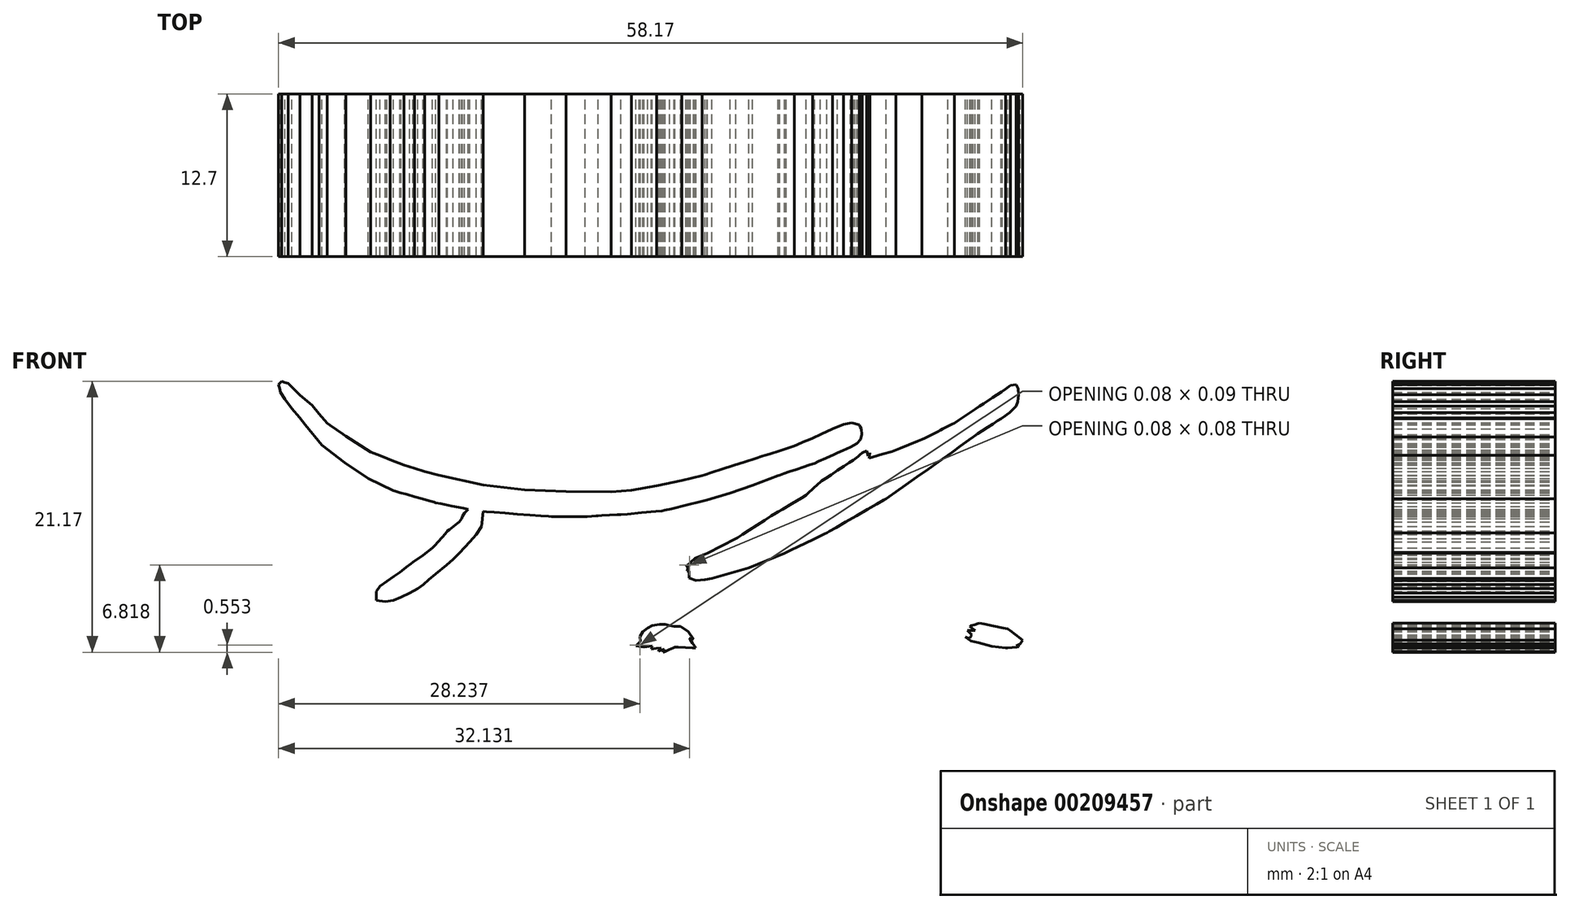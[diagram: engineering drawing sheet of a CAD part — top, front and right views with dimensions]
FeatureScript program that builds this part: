
annotation { "Feature Type Name" : "Feature", "Feature Type Description" : "" }
export const myFeature = defineFeature(function(context is Context, id is Id, definition is map)
    precondition{}
    {
        {
            var Q0;
            Q0=qCreatedBy(makeId("Front.planeOp"),FACE);
            var sketch = newSketch(context, id + "F0", { "sketchPlane" : qUnion([Q0])});
            skLineSegment(sketch, "E0", {"start": v(-84.86, 9.06) * mm, "end": v(-85.86, 10.23) * mm});
            skLineSegment(sketch, "E1", {"start": v(-85.86, 10.23) * mm, "end": v(-86.65, 11.35) * mm});
            skLineSegment(sketch, "E2", {"start": v(-86.65, 11.35) * mm, "end": v(-87.17, 12.6) * mm});
            skLineSegment(sketch, "E3", {"start": v(-87.17, 12.6) * mm, "end": v(-87.36, 14.14) * mm});
            skLineSegment(sketch, "E4", {"start": v(-87.36, 14.14) * mm, "end": v(-87.36, 15.32) * mm});
            skLineSegment(sketch, "E5", {"start": v(-87.36, 15.32) * mm, "end": v(-87.27, 15.8) * mm});
            skLineSegment(sketch, "E6", {"start": v(-87.27, 15.8) * mm, "end": v(-87.27, 16.26) * mm});
            skLineSegment(sketch, "E7", {"start": v(-87.27, 16.26) * mm, "end": v(-87.56, 16.7) * mm});
            skLineSegment(sketch, "E8", {"start": v(-87.56, 16.7) * mm, "end": v(-87.92, 17.1) * mm});
            skLineSegment(sketch, "E9", {"start": v(-87.92, 17.1) * mm, "end": v(-88.01, 17.22) * mm});
            skLineSegment(sketch, "E10", {"start": v(-88.01, 17.22) * mm, "end": v(-88.2, 17.49) * mm});
            skLineSegment(sketch, "E11", {"start": v(-88.2, 17.49) * mm, "end": v(-88.39, 17.75) * mm});
            skLineSegment(sketch, "E12", {"start": v(-88.39, 17.75) * mm, "end": v(-88.47, 17.87) * mm});
            skLineSegment(sketch, "E13", {"start": v(-88.47, 17.87) * mm, "end": v(-88.6, 18.03) * mm});
            skLineSegment(sketch, "E14", {"start": v(-88.6, 18.03) * mm, "end": v(-88.88, 18.37) * mm});
            skLineSegment(sketch, "E15", {"start": v(-88.88, 18.37) * mm, "end": v(-89.16, 18.72) * mm});
            skLineSegment(sketch, "E16", {"start": v(-89.16, 18.72) * mm, "end": v(-89.29, 18.88) * mm});
            skLineSegment(sketch, "E17", {"start": v(-89.29, 18.88) * mm, "end": v(-90.13, 20.03) * mm});
            skLineSegment(sketch, "E18", {"start": v(-90.13, 20.03) * mm, "end": v(-91.15, 21.5) * mm});
            skLineSegment(sketch, "E19", {"start": v(-91.15, 21.5) * mm, "end": v(-92.13, 23) * mm});
            skLineSegment(sketch, "E20", {"start": v(-92.13, 23) * mm, "end": v(-92.85, 24.22) * mm});
            skLineSegment(sketch, "E21", {"start": v(-92.85, 24.22) * mm, "end": v(-92.91, 24.33) * mm});
            skLineSegment(sketch, "E22", {"start": v(-92.91, 24.33) * mm, "end": v(-93.06, 24.63) * mm});
            skLineSegment(sketch, "E23", {"start": v(-93.06, 24.63) * mm, "end": v(-93.27, 25.05) * mm});
            skLineSegment(sketch, "E24", {"start": v(-93.27, 25.05) * mm, "end": v(-93.5, 25.53) * mm});
            skLineSegment(sketch, "E25", {"start": v(-93.5, 25.53) * mm, "end": v(-93.75, 26) * mm});
            skLineSegment(sketch, "E26", {"start": v(-93.75, 26) * mm, "end": v(-93.96, 26.43) * mm});
            skLineSegment(sketch, "E27", {"start": v(-93.96, 26.43) * mm, "end": v(-94.1, 26.73) * mm});
            skLineSegment(sketch, "E28", {"start": v(-94.1, 26.73) * mm, "end": v(-94.16, 26.84) * mm});
            skLineSegment(sketch, "E29", {"start": v(-94.16, 26.84) * mm, "end": v(-94.25, 27.07) * mm});
            skLineSegment(sketch, "E30", {"start": v(-94.25, 27.07) * mm, "end": v(-94.43, 27.56) * mm});
            skLineSegment(sketch, "E31", {"start": v(-94.43, 27.56) * mm, "end": v(-94.62, 28.05) * mm});
            skLineSegment(sketch, "E32", {"start": v(-94.62, 28.05) * mm, "end": v(-94.7, 28.28) * mm});
            skLineSegment(sketch, "E33", {"start": v(-94.7, 28.28) * mm, "end": v(-94.84, 28.6) * mm});
            skLineSegment(sketch, "E34", {"start": v(-94.84, 28.6) * mm, "end": v(-95.11, 29.3) * mm});
            skLineSegment(sketch, "E35", {"start": v(-95.11, 29.3) * mm, "end": v(-95.39, 30) * mm});
            skLineSegment(sketch, "E36", {"start": v(-95.39, 30) * mm, "end": v(-95.51, 30.31) * mm});
            skLineSegment(sketch, "E37", {"start": v(-95.51, 30.31) * mm, "end": v(-95.87, 32.15) * mm});
            skLineSegment(sketch, "E38", {"start": v(-95.87, 32.15) * mm, "end": v(-96.11, 34.04) * mm});
            skLineSegment(sketch, "E39", {"start": v(-96.11, 34.04) * mm, "end": v(-96.15, 34.45) * mm});
            skLineSegment(sketch, "E40", {"start": v(-96.15, 34.45) * mm, "end": v(-96.22, 35.35) * mm});
            skLineSegment(sketch, "E41", {"start": v(-96.22, 35.35) * mm, "end": v(-96.3, 36.25) * mm});
            skLineSegment(sketch, "E42", {"start": v(-96.3, 36.25) * mm, "end": v(-96.33, 36.66) * mm});
            skLineSegment(sketch, "E43", {"start": v(-96.33, 36.66) * mm, "end": v(-96.29, 36.97) * mm});
            skLineSegment(sketch, "E44", {"start": v(-96.29, 36.97) * mm, "end": v(-96.2, 37.63) * mm});
            skLineSegment(sketch, "E45", {"start": v(-96.2, 37.63) * mm, "end": v(-96.1, 38.3) * mm});
            skLineSegment(sketch, "E46", {"start": v(-96.1, 38.3) * mm, "end": v(-96.05, 38.6) * mm});
            skLineSegment(sketch, "E47", {"start": v(-96.05, 38.6) * mm, "end": v(-94.25, 44.05) * mm});
            skLineSegment(sketch, "E48", {"start": v(-94.25, 44.05) * mm, "end": v(-91, 48.77) * mm});
            skLineSegment(sketch, "E49", {"start": v(-91, 48.77) * mm, "end": v(-89.57, 50.22) * mm});
            skLineSegment(sketch, "E50", {"start": v(-89.57, 50.22) * mm, "end": v(-88.05, 51.58) * mm});
            skLineSegment(sketch, "E51", {"start": v(-88.05, 51.58) * mm, "end": v(-85.3, 53.9) * mm});
            skLineSegment(sketch, "E52", {"start": v(-85.3, 53.9) * mm, "end": v(-82.38, 56) * mm});
            skLineSegment(sketch, "E53", {"start": v(-82.38, 56) * mm, "end": v(-82.2, 56.1) * mm});
            skLineSegment(sketch, "E54", {"start": v(-82.2, 56.1) * mm, "end": v(-81.72, 56.35) * mm});
            skLineSegment(sketch, "E55", {"start": v(-81.72, 56.35) * mm, "end": v(-81.04, 56.71) * mm});
            skLineSegment(sketch, "E56", {"start": v(-81.04, 56.71) * mm, "end": v(-80.26, 57.13) * mm});
            skLineSegment(sketch, "E57", {"start": v(-80.26, 57.13) * mm, "end": v(-79.49, 57.55) * mm});
            skLineSegment(sketch, "E58", {"start": v(-79.49, 57.55) * mm, "end": v(-78.8, 57.92) * mm});
            skLineSegment(sketch, "E59", {"start": v(-78.8, 57.92) * mm, "end": v(-78.33, 58.17) * mm});
            skLineSegment(sketch, "E60", {"start": v(-78.33, 58.17) * mm, "end": v(-78.15, 58.27) * mm});
            skLineSegment(sketch, "E61", {"start": v(-78.15, 58.27) * mm, "end": v(-77.98, 58.35) * mm});
            skLineSegment(sketch, "E62", {"start": v(-77.98, 58.35) * mm, "end": v(-77.54, 58.56) * mm});
            skLineSegment(sketch, "E63", {"start": v(-77.54, 58.56) * mm, "end": v(-76.92, 58.85) * mm});
            skLineSegment(sketch, "E64", {"start": v(-76.92, 58.85) * mm, "end": v(-76.2, 59.19) * mm});
            skLineSegment(sketch, "E65", {"start": v(-76.2, 59.19) * mm, "end": v(-75.49, 59.52) * mm});
            skLineSegment(sketch, "E66", {"start": v(-75.49, 59.52) * mm, "end": v(-74.86, 59.82) * mm});
            skLineSegment(sketch, "E67", {"start": v(-74.86, 59.82) * mm, "end": v(-74.42, 60.02) * mm});
            skLineSegment(sketch, "E68", {"start": v(-74.42, 60.02) * mm, "end": v(-74.25, 60.1) * mm});
            skLineSegment(sketch, "E69", {"start": v(-74.25, 60.1) * mm, "end": v(-73.91, 60.24) * mm});
            skLineSegment(sketch, "E70", {"start": v(-73.91, 60.24) * mm, "end": v(-73.15, 60.56) * mm});
            skLineSegment(sketch, "E71", {"start": v(-73.15, 60.56) * mm, "end": v(-72.4, 60.87) * mm});
            skLineSegment(sketch, "E72", {"start": v(-72.4, 60.87) * mm, "end": v(-72.05, 61.02) * mm});
            skLineSegment(sketch, "E73", {"start": v(-72.05, 61.02) * mm, "end": v(-69.88, 61.65) * mm});
            skLineSegment(sketch, "E74", {"start": v(-69.88, 61.65) * mm, "end": v(-67.33, 62.24) * mm});
            skLineSegment(sketch, "E75", {"start": v(-67.33, 62.24) * mm, "end": v(-64.75, 62.74) * mm});
            skLineSegment(sketch, "E76", {"start": v(-64.75, 62.74) * mm, "end": v(-62.49, 63.11) * mm});
            skLineSegment(sketch, "E77", {"start": v(-62.49, 63.11) * mm, "end": v(-54.95, 63.92) * mm});
            skLineSegment(sketch, "E78", {"start": v(-54.95, 63.92) * mm, "end": v(-54.74, 63.94) * mm});
            skLineSegment(sketch, "E79", {"start": v(-54.74, 63.94) * mm, "end": v(-54.27, 63.97) * mm});
            skLineSegment(sketch, "E80", {"start": v(-54.27, 63.97) * mm, "end": v(-53.8, 64) * mm});
            skLineSegment(sketch, "E81", {"start": v(-53.8, 64) * mm, "end": v(-53.6, 64) * mm});
            skLineSegment(sketch, "E82", {"start": v(-53.6, 64) * mm, "end": v(-53.37, 64) * mm});
            skLineSegment(sketch, "E83", {"start": v(-53.37, 64) * mm, "end": v(-52.88, 64) * mm});
            skLineSegment(sketch, "E84", {"start": v(-52.88, 64) * mm, "end": v(-52.38, 64) * mm});
            skLineSegment(sketch, "E85", {"start": v(-52.38, 64) * mm, "end": v(-52.16, 64) * mm});
            skLineSegment(sketch, "E86", {"start": v(-52.16, 64) * mm, "end": v(-51.94, 64) * mm});
            skLineSegment(sketch, "E87", {"start": v(-51.94, 64) * mm, "end": v(-51.48, 63.96) * mm});
            skLineSegment(sketch, "E88", {"start": v(-51.48, 63.96) * mm, "end": v(-51.01, 63.93) * mm});
            skLineSegment(sketch, "E89", {"start": v(-51.01, 63.93) * mm, "end": v(-50.8, 63.9) * mm});
            skLineSegment(sketch, "E90", {"start": v(-50.8, 63.9) * mm, "end": v(-50.59, 63.9) * mm});
            skLineSegment(sketch, "E91", {"start": v(-50.59, 63.9) * mm, "end": v(-50.12, 63.9) * mm});
            skLineSegment(sketch, "E92", {"start": v(-50.12, 63.9) * mm, "end": v(-49.66, 63.9) * mm});
            skLineSegment(sketch, "E93", {"start": v(-49.66, 63.9) * mm, "end": v(-49.45, 63.9) * mm});
            skLineSegment(sketch, "E94", {"start": v(-49.45, 63.9) * mm, "end": v(-49.02, 63.87) * mm});
            skLineSegment(sketch, "E95", {"start": v(-49.02, 63.87) * mm, "end": v(-48.6, 63.84) * mm});
            skLineSegment(sketch, "E96", {"start": v(-48.6, 63.84) * mm, "end": v(-48.06, 63.81) * mm});
            skLineSegment(sketch, "E97", {"start": v(-48.06, 63.81) * mm, "end": v(-46.87, 63.75) * mm});
            skLineSegment(sketch, "E98", {"start": v(-46.87, 63.75) * mm, "end": v(-45.67, 63.68) * mm});
            skLineSegment(sketch, "E99", {"start": v(-45.67, 63.68) * mm, "end": v(-45.13, 63.66) * mm});
            skLineSegment(sketch, "E100", {"start": v(-45.13, 63.66) * mm, "end": v(-44.84, 63.6) * mm});
            skLineSegment(sketch, "E101", {"start": v(-44.84, 63.6) * mm, "end": v(-44.2, 63.5) * mm});
            skLineSegment(sketch, "E102", {"start": v(-44.2, 63.5) * mm, "end": v(-43.56, 63.4) * mm});
            skLineSegment(sketch, "E103", {"start": v(-43.56, 63.4) * mm, "end": v(-43.27, 63.35) * mm});
            skLineSegment(sketch, "E104", {"start": v(-43.27, 63.35) * mm, "end": v(-36.5, 62.05) * mm});
            skLineSegment(sketch, "E105", {"start": v(-36.5, 62.05) * mm, "end": v(-28.96, 59.87) * mm});
            skLineSegment(sketch, "E106", {"start": v(-28.96, 59.87) * mm, "end": v(-28.68, 59.78) * mm});
            skLineSegment(sketch, "E107", {"start": v(-28.68, 59.78) * mm, "end": v(-28.07, 59.57) * mm});
            skLineSegment(sketch, "E108", {"start": v(-28.07, 59.57) * mm, "end": v(-27.46, 59.37) * mm});
            skLineSegment(sketch, "E109", {"start": v(-27.46, 59.37) * mm, "end": v(-27.18, 59.28) * mm});
            skLineSegment(sketch, "E110", {"start": v(-27.18, 59.28) * mm, "end": v(-26.85, 59.12) * mm});
            skLineSegment(sketch, "E111", {"start": v(-26.85, 59.12) * mm, "end": v(-26.12, 58.77) * mm});
            skLineSegment(sketch, "E112", {"start": v(-26.12, 58.77) * mm, "end": v(-25.4, 58.42) * mm});
            skLineSegment(sketch, "E113", {"start": v(-25.4, 58.42) * mm, "end": v(-25.06, 58.26) * mm});
            skLineSegment(sketch, "E114", {"start": v(-25.06, 58.26) * mm, "end": v(-24.81, 58.1) * mm});
            skLineSegment(sketch, "E115", {"start": v(-24.81, 58.1) * mm, "end": v(-24.26, 57.77) * mm});
            skLineSegment(sketch, "E116", {"start": v(-24.26, 57.77) * mm, "end": v(-23.7, 57.43) * mm});
            skLineSegment(sketch, "E117", {"start": v(-23.7, 57.43) * mm, "end": v(-23.45, 57.27) * mm});
            skLineSegment(sketch, "E118", {"start": v(-23.45, 57.27) * mm, "end": v(-23.26, 57.17) * mm});
            skLineSegment(sketch, "E119", {"start": v(-23.26, 57.17) * mm, "end": v(-22.82, 56.94) * mm});
            skLineSegment(sketch, "E120", {"start": v(-22.82, 56.94) * mm, "end": v(-22.38, 56.7) * mm});
            skLineSegment(sketch, "E121", {"start": v(-22.38, 56.7) * mm, "end": v(-22.18, 56.6) * mm});
            skLineSegment(sketch, "E122", {"start": v(-22.18, 56.6) * mm, "end": v(-20.73, 55.63) * mm});
            skLineSegment(sketch, "E123", {"start": v(-20.73, 55.63) * mm, "end": v(-19.32, 54.46) * mm});
            skLineSegment(sketch, "E124", {"start": v(-19.32, 54.46) * mm, "end": v(-18.02, 53.17) * mm});
            skLineSegment(sketch, "E125", {"start": v(-18.02, 53.17) * mm, "end": v(-16.91, 51.82) * mm});
            skLineSegment(sketch, "E126", {"start": v(-16.91, 51.82) * mm, "end": v(-16.7, 51.49) * mm});
            skLineSegment(sketch, "E127", {"start": v(-16.7, 51.49) * mm, "end": v(-16.26, 50.76) * mm});
            skLineSegment(sketch, "E128", {"start": v(-16.26, 50.76) * mm, "end": v(-15.8, 50.03) * mm});
            skLineSegment(sketch, "E129", {"start": v(-15.8, 50.03) * mm, "end": v(-15.6, 49.7) * mm});
            skLineSegment(sketch, "E130", {"start": v(-15.6, 49.7) * mm, "end": v(-15.52, 49.52) * mm});
            skLineSegment(sketch, "E131", {"start": v(-15.52, 49.52) * mm, "end": v(-15.33, 49.1) * mm});
            skLineSegment(sketch, "E132", {"start": v(-15.33, 49.1) * mm, "end": v(-15.14, 48.7) * mm});
            skLineSegment(sketch, "E133", {"start": v(-15.14, 48.7) * mm, "end": v(-15.05, 48.51) * mm});
            skLineSegment(sketch, "E134", {"start": v(-15.05, 48.51) * mm, "end": v(-15, 48.4) * mm});
            skLineSegment(sketch, "E135", {"start": v(-15, 48.4) * mm, "end": v(-14.86, 48.12) * mm});
            skLineSegment(sketch, "E136", {"start": v(-14.86, 48.12) * mm, "end": v(-14.66, 47.71) * mm});
            skLineSegment(sketch, "E137", {"start": v(-14.66, 47.71) * mm, "end": v(-14.43, 47.25) * mm});
            skLineSegment(sketch, "E138", {"start": v(-14.43, 47.25) * mm, "end": v(-14.2, 46.78) * mm});
            skLineSegment(sketch, "E139", {"start": v(-14.2, 46.78) * mm, "end": v(-14, 46.37) * mm});
            skLineSegment(sketch, "E140", {"start": v(-14, 46.37) * mm, "end": v(-13.86, 46.08) * mm});
            skLineSegment(sketch, "E141", {"start": v(-13.86, 46.08) * mm, "end": v(-13.8, 45.98) * mm});
            skLineSegment(sketch, "E142", {"start": v(-13.8, 45.98) * mm, "end": v(-12.93, 42.88) * mm});
            skLineSegment(sketch, "E143", {"start": v(-12.93, 42.88) * mm, "end": v(-12.52, 39.7) * mm});
            skLineSegment(sketch, "E144", {"start": v(-12.52, 39.7) * mm, "end": v(-12.5, 39.43) * mm});
            skLineSegment(sketch, "E145", {"start": v(-12.5, 39.43) * mm, "end": v(-12.44, 38.82) * mm});
            skLineSegment(sketch, "E146", {"start": v(-12.44, 38.82) * mm, "end": v(-12.39, 38.2) * mm});
            skLineSegment(sketch, "E147", {"start": v(-12.39, 38.2) * mm, "end": v(-12.36, 37.93) * mm});
            skLineSegment(sketch, "E148", {"start": v(-12.36, 37.93) * mm, "end": v(-12.75, 33.76) * mm});
            skLineSegment(sketch, "E149", {"start": v(-12.75, 33.76) * mm, "end": v(-13.59, 29.63) * mm});
            skLineSegment(sketch, "E150", {"start": v(-13.59, 29.63) * mm, "end": v(-13.63, 29.37) * mm});
            skLineSegment(sketch, "E151", {"start": v(-13.63, 29.37) * mm, "end": v(-13.71, 28.79) * mm});
            skLineSegment(sketch, "E152", {"start": v(-13.71, 28.79) * mm, "end": v(-13.8, 28.2) * mm});
            skLineSegment(sketch, "E153", {"start": v(-13.8, 28.2) * mm, "end": v(-13.84, 27.94) * mm});
            skLineSegment(sketch, "E154", {"start": v(-13.84, 27.94) * mm, "end": v(-13.9, 27.66) * mm});
            skLineSegment(sketch, "E155", {"start": v(-13.9, 27.66) * mm, "end": v(-14.01, 27.05) * mm});
            skLineSegment(sketch, "E156", {"start": v(-14.01, 27.05) * mm, "end": v(-14.14, 26.44) * mm});
            skLineSegment(sketch, "E157", {"start": v(-14.14, 26.44) * mm, "end": v(-14.19, 26.16) * mm});
            skLineSegment(sketch, "E158", {"start": v(-14.19, 26.16) * mm, "end": v(-14.22, 25.91) * mm});
            skLineSegment(sketch, "E159", {"start": v(-14.22, 25.91) * mm, "end": v(-14.3, 25.36) * mm});
            skLineSegment(sketch, "E160", {"start": v(-14.3, 25.36) * mm, "end": v(-14.36, 24.8) * mm});
            skLineSegment(sketch, "E161", {"start": v(-14.36, 24.8) * mm, "end": v(-14.4, 24.55) * mm});
            skLineSegment(sketch, "E162", {"start": v(-14.4, 24.55) * mm, "end": v(-14.14, 24.68) * mm});
            skLineSegment(sketch, "E163", {"start": v(-14.14, 24.68) * mm, "end": v(-13.89, 24.8) * mm});
            skLineSegment(sketch, "E164", {"start": v(-13.89, 24.8) * mm, "end": v(-13.72, 24.55) * mm});
            skLineSegment(sketch, "E165", {"start": v(-13.72, 24.55) * mm, "end": v(-13.55, 24.3) * mm});
            skLineSegment(sketch, "E166", {"start": v(-13.55, 24.3) * mm, "end": v(-13.63, 24.17) * mm});
            skLineSegment(sketch, "E167", {"start": v(-13.63, 24.17) * mm, "end": v(-13.72, 24.05) * mm});
            skLineSegment(sketch, "E168", {"start": v(-13.72, 24.05) * mm, "end": v(-13.55, 24.05) * mm});
            skLineSegment(sketch, "E169", {"start": v(-13.55, 24.05) * mm, "end": v(-13.58, 23.91) * mm});
            skLineSegment(sketch, "E170", {"start": v(-13.58, 23.91) * mm, "end": v(-13.63, 23.62) * mm});
            skLineSegment(sketch, "E171", {"start": v(-13.63, 23.62) * mm, "end": v(-13.7, 23.33) * mm});
            skLineSegment(sketch, "E172", {"start": v(-13.7, 23.33) * mm, "end": v(-13.72, 23.2) * mm});
            skLineSegment(sketch, "E173", {"start": v(-13.72, 23.2) * mm, "end": v(-13.55, 23.2) * mm});
            skLineSegment(sketch, "E174", {"start": v(-13.55, 23.2) * mm, "end": v(-14.06, 22.2) * mm});
            skLineSegment(sketch, "E175", {"start": v(-14.06, 22.2) * mm, "end": v(-14.68, 21.25) * mm});
            skLineSegment(sketch, "E176", {"start": v(-14.68, 21.25) * mm, "end": v(-15.5, 20.04) * mm});
            skLineSegment(sketch, "E177", {"start": v(-15.5, 20.04) * mm, "end": v(-16.47, 18.86) * mm});
            skLineSegment(sketch, "E178", {"start": v(-16.47, 18.86) * mm, "end": v(-17.57, 17.82) * mm});
            skLineSegment(sketch, "E179", {"start": v(-17.57, 17.82) * mm, "end": v(-18.8, 17.02) * mm});
            skLineSegment(sketch, "E180", {"start": v(-18.8, 17.02) * mm, "end": v(-18.93, 16.97) * mm});
            skLineSegment(sketch, "E181", {"start": v(-18.93, 16.97) * mm, "end": v(-19.22, 16.85) * mm});
            skLineSegment(sketch, "E182", {"start": v(-19.22, 16.85) * mm, "end": v(-19.51, 16.74) * mm});
            skLineSegment(sketch, "E183", {"start": v(-19.51, 16.74) * mm, "end": v(-19.64, 16.7) * mm});
            skLineSegment(sketch, "E184", {"start": v(-19.64, 16.7) * mm, "end": v(-20.61, 16.39) * mm});
            skLineSegment(sketch, "E185", {"start": v(-20.61, 16.39) * mm, "end": v(-21.6, 16.2) * mm});
            skLineSegment(sketch, "E186", {"start": v(-21.6, 16.2) * mm, "end": v(-22.03, 16.1) * mm});
            skLineSegment(sketch, "E187", {"start": v(-22.03, 16.1) * mm, "end": v(-22.42, 16.04) * mm});
            skLineSegment(sketch, "E188", {"start": v(-22.42, 16.04) * mm, "end": v(-22.75, 16.22) * mm});
            skLineSegment(sketch, "E189", {"start": v(-22.75, 16.22) * mm, "end": v(-22.97, 16.52) * mm});
            skLineSegment(sketch, "E190", {"start": v(-22.97, 16.52) * mm, "end": v(-23.01, 17) * mm});
            skLineSegment(sketch, "E191", {"start": v(-23.01, 17) * mm, "end": v(-22.87, 17.6) * mm});
            skLineSegment(sketch, "E192", {"start": v(-22.87, 17.6) * mm, "end": v(-22.65, 18.17) * mm});
            skLineSegment(sketch, "E193", {"start": v(-22.65, 18.17) * mm, "end": v(-22.43, 18.63) * mm});
            skLineSegment(sketch, "E194", {"start": v(-22.43, 18.63) * mm, "end": v(-22.07, 19.34) * mm});
            skLineSegment(sketch, "E195", {"start": v(-22.07, 19.34) * mm, "end": v(-21.87, 19.81) * mm});
            skLineSegment(sketch, "E196", {"start": v(-21.87, 19.81) * mm, "end": v(-21.71, 20.28) * mm});
            skLineSegment(sketch, "E197", {"start": v(-21.71, 20.28) * mm, "end": v(-21.48, 21) * mm});
            skLineSegment(sketch, "E198", {"start": v(-21.48, 21) * mm, "end": v(-21.2, 21.78) * mm});
            skLineSegment(sketch, "E199", {"start": v(-21.2, 21.78) * mm, "end": v(-21.1, 22.6) * mm});
            skLineSegment(sketch, "E200", {"start": v(-21.1, 22.6) * mm, "end": v(-21.11, 22.8) * mm});
            skLineSegment(sketch, "E201", {"start": v(-21.11, 22.8) * mm, "end": v(-21.15, 23.28) * mm});
            skLineSegment(sketch, "E202", {"start": v(-21.15, 23.28) * mm, "end": v(-21.2, 23.97) * mm});
            skLineSegment(sketch, "E203", {"start": v(-21.2, 23.97) * mm, "end": v(-21.27, 24.77) * mm});
            skLineSegment(sketch, "E204", {"start": v(-21.27, 24.77) * mm, "end": v(-21.34, 25.56) * mm});
            skLineSegment(sketch, "E205", {"start": v(-21.34, 25.56) * mm, "end": v(-21.4, 26.25) * mm});
            skLineSegment(sketch, "E206", {"start": v(-21.4, 26.25) * mm, "end": v(-21.43, 26.74) * mm});
            skLineSegment(sketch, "E207", {"start": v(-21.43, 26.74) * mm, "end": v(-21.45, 26.93) * mm});
            skLineSegment(sketch, "E208", {"start": v(-21.45, 26.93) * mm, "end": v(-21.51, 27.44) * mm});
            skLineSegment(sketch, "E209", {"start": v(-21.51, 27.44) * mm, "end": v(-21.65, 28.58) * mm});
            skLineSegment(sketch, "E210", {"start": v(-21.65, 28.58) * mm, "end": v(-21.8, 29.71) * mm});
            skLineSegment(sketch, "E211", {"start": v(-21.8, 29.71) * mm, "end": v(-21.86, 30.23) * mm});
            skLineSegment(sketch, "E212", {"start": v(-21.86, 30.23) * mm, "end": v(-21.88, 30.41) * mm});
            skLineSegment(sketch, "E213", {"start": v(-21.88, 30.41) * mm, "end": v(-21.94, 30.82) * mm});
            skLineSegment(sketch, "E214", {"start": v(-21.94, 30.82) * mm, "end": v(-22, 31.23) * mm});
            skLineSegment(sketch, "E215", {"start": v(-22, 31.23) * mm, "end": v(-22.01, 31.41) * mm});
            skLineSegment(sketch, "E216", {"start": v(-22.01, 31.41) * mm, "end": v(-22.26, 30.93) * mm});
            skLineSegment(sketch, "E217", {"start": v(-22.26, 30.93) * mm, "end": v(-22.39, 30.4) * mm});
            skLineSegment(sketch, "E218", {"start": v(-22.39, 30.4) * mm, "end": v(-22.73, 29.53) * mm});
            skLineSegment(sketch, "E219", {"start": v(-22.73, 29.53) * mm, "end": v(-23.14, 28.7) * mm});
            skLineSegment(sketch, "E220", {"start": v(-23.14, 28.7) * mm, "end": v(-23.32, 28.39) * mm});
            skLineSegment(sketch, "E221", {"start": v(-23.32, 28.39) * mm, "end": v(-23.74, 27.69) * mm});
            skLineSegment(sketch, "E222", {"start": v(-23.74, 27.69) * mm, "end": v(-24.15, 26.99) * mm});
            skLineSegment(sketch, "E223", {"start": v(-24.15, 26.99) * mm, "end": v(-24.33, 26.67) * mm});
            skLineSegment(sketch, "E224", {"start": v(-24.33, 26.67) * mm, "end": v(-24.95, 25.62) * mm});
            skLineSegment(sketch, "E225", {"start": v(-24.95, 25.62) * mm, "end": v(-25.5, 24.7) * mm});
            skLineSegment(sketch, "E226", {"start": v(-25.5, 24.7) * mm, "end": v(-26.1, 23.79) * mm});
            skLineSegment(sketch, "E227", {"start": v(-26.1, 23.79) * mm, "end": v(-26.86, 22.78) * mm});
            skLineSegment(sketch, "E228", {"start": v(-26.86, 22.78) * mm, "end": v(-27.22, 22.32) * mm});
            skLineSegment(sketch, "E229", {"start": v(-27.22, 22.32) * mm, "end": v(-27.69, 21.78) * mm});
            skLineSegment(sketch, "E230", {"start": v(-27.69, 21.78) * mm, "end": v(-28.18, 21.28) * mm});
            skLineSegment(sketch, "E231", {"start": v(-28.18, 21.28) * mm, "end": v(-28.62, 20.95) * mm});
            skLineSegment(sketch, "E232", {"start": v(-28.62, 20.95) * mm, "end": v(-29.1, 20.8) * mm});
            skLineSegment(sketch, "E233", {"start": v(-29.1, 20.8) * mm, "end": v(-29.45, 20.87) * mm});
            skLineSegment(sketch, "E234", {"start": v(-29.45, 20.87) * mm, "end": v(-29.64, 21.17) * mm});
            skLineSegment(sketch, "E235", {"start": v(-29.64, 21.17) * mm, "end": v(-29.63, 21.67) * mm});
            skLineSegment(sketch, "E236", {"start": v(-29.63, 21.67) * mm, "end": v(-29.62, 22.16) * mm});
            skLineSegment(sketch, "E237", {"start": v(-29.62, 22.16) * mm, "end": v(-29.3, 22.6) * mm});
            skLineSegment(sketch, "E238", {"start": v(-29.3, 22.6) * mm, "end": v(-29.22, 22.7) * mm});
            skLineSegment(sketch, "E239", {"start": v(-29.22, 22.7) * mm, "end": v(-29.02, 22.96) * mm});
            skLineSegment(sketch, "E240", {"start": v(-29.02, 22.96) * mm, "end": v(-28.74, 23.33) * mm});
            skLineSegment(sketch, "E241", {"start": v(-28.74, 23.33) * mm, "end": v(-28.41, 23.75) * mm});
            skLineSegment(sketch, "E242", {"start": v(-28.41, 23.75) * mm, "end": v(-28.09, 24.17) * mm});
            skLineSegment(sketch, "E243", {"start": v(-28.09, 24.17) * mm, "end": v(-27.8, 24.54) * mm});
            skLineSegment(sketch, "E244", {"start": v(-27.8, 24.54) * mm, "end": v(-27.6, 24.8) * mm});
            skLineSegment(sketch, "E245", {"start": v(-27.6, 24.8) * mm, "end": v(-27.53, 24.9) * mm});
            skLineSegment(sketch, "E246", {"start": v(-27.53, 24.9) * mm, "end": v(-26.58, 26.57) * mm});
            skLineSegment(sketch, "E247", {"start": v(-26.58, 26.57) * mm, "end": v(-25.86, 28.54) * mm});
            skLineSegment(sketch, "E248", {"start": v(-25.86, 28.54) * mm, "end": v(-25.33, 30.6) * mm});
            skLineSegment(sketch, "E249", {"start": v(-25.33, 30.6) * mm, "end": v(-25, 32.51) * mm});
            skLineSegment(sketch, "E250", {"start": v(-25, 32.51) * mm, "end": v(-24.98, 32.75) * mm});
            skLineSegment(sketch, "E251", {"start": v(-24.98, 32.75) * mm, "end": v(-24.94, 33.28) * mm});
            skLineSegment(sketch, "E252", {"start": v(-24.94, 33.28) * mm, "end": v(-24.9, 33.8) * mm});
            skLineSegment(sketch, "E253", {"start": v(-24.9, 33.8) * mm, "end": v(-24.88, 34.04) * mm});
            skLineSegment(sketch, "E254", {"start": v(-24.88, 34.04) * mm, "end": v(-24.83, 34.33) * mm});
            skLineSegment(sketch, "E255", {"start": v(-24.83, 34.33) * mm, "end": v(-24.72, 34.97) * mm});
            skLineSegment(sketch, "E256", {"start": v(-24.72, 34.97) * mm, "end": v(-24.6, 35.6) * mm});
            skLineSegment(sketch, "E257", {"start": v(-24.6, 35.6) * mm, "end": v(-24.55, 35.9) * mm});
            skLineSegment(sketch, "E258", {"start": v(-24.55, 35.9) * mm, "end": v(-24.47, 35.9) * mm});
            skLineSegment(sketch, "E259", {"start": v(-24.47, 35.9) * mm, "end": v(-24.39, 35.81) * mm});
            skLineSegment(sketch, "E260", {"start": v(-24.39, 35.81) * mm, "end": v(-24.3, 35.73) * mm});
            skLineSegment(sketch, "E261", {"start": v(-24.3, 35.73) * mm, "end": v(-24.26, 35.86) * mm});
            skLineSegment(sketch, "E262", {"start": v(-24.26, 35.86) * mm, "end": v(-24.22, 35.98) * mm});
            skLineSegment(sketch, "E263", {"start": v(-24.22, 35.98) * mm, "end": v(-23.94, 35.14) * mm});
            skLineSegment(sketch, "E264", {"start": v(-23.94, 35.14) * mm, "end": v(-23.84, 34.3) * mm});
            skLineSegment(sketch, "E265", {"start": v(-23.84, 34.3) * mm, "end": v(-23.67, 33.38) * mm});
            skLineSegment(sketch, "E266", {"start": v(-23.67, 33.38) * mm, "end": v(-23.65, 32.43) * mm});
            skLineSegment(sketch, "E267", {"start": v(-23.65, 32.43) * mm, "end": v(-23.7, 31.97) * mm});
            skLineSegment(sketch, "E268", {"start": v(-23.7, 31.97) * mm, "end": v(-23.85, 30.95) * mm});
            skLineSegment(sketch, "E269", {"start": v(-23.85, 30.95) * mm, "end": v(-23.98, 29.93) * mm});
            skLineSegment(sketch, "E270", {"start": v(-23.98, 29.93) * mm, "end": v(-24.05, 29.46) * mm});
            skLineSegment(sketch, "E271", {"start": v(-24.05, 29.46) * mm, "end": v(-23.83, 29.9) * mm});
            skLineSegment(sketch, "E272", {"start": v(-23.83, 29.9) * mm, "end": v(-23.66, 30.11) * mm});
            skLineSegment(sketch, "E273", {"start": v(-23.66, 30.11) * mm, "end": v(-23.5, 30.26) * mm});
            skLineSegment(sketch, "E274", {"start": v(-23.5, 30.26) * mm, "end": v(-23.26, 30.5) * mm});
            skLineSegment(sketch, "E275", {"start": v(-23.26, 30.5) * mm, "end": v(-23.15, 30.64) * mm});
            skLineSegment(sketch, "E276", {"start": v(-23.15, 30.64) * mm, "end": v(-22.9, 30.95) * mm});
            skLineSegment(sketch, "E277", {"start": v(-22.9, 30.95) * mm, "end": v(-22.64, 31.27) * mm});
            skLineSegment(sketch, "E278", {"start": v(-22.64, 31.27) * mm, "end": v(-22.52, 31.41) * mm});
            skLineSegment(sketch, "E279", {"start": v(-22.52, 31.41) * mm, "end": v(-22.17, 31.61) * mm});
            skLineSegment(sketch, "E280", {"start": v(-22.17, 31.61) * mm, "end": v(-22.11, 32.09) * mm});
            skLineSegment(sketch, "E281", {"start": v(-22.11, 32.09) * mm, "end": v(-22.22, 32.68) * mm});
            skLineSegment(sketch, "E282", {"start": v(-22.22, 32.68) * mm, "end": v(-22.33, 33.22) * mm});
            skLineSegment(sketch, "E283", {"start": v(-22.33, 33.22) * mm, "end": v(-22.29, 33.72) * mm});
            skLineSegment(sketch, "E284", {"start": v(-22.29, 33.72) * mm, "end": v(-21.93, 34.2) * mm});
            skLineSegment(sketch, "E285", {"start": v(-21.93, 34.2) * mm, "end": v(-21.89, 34.04) * mm});
            skLineSegment(sketch, "E286", {"start": v(-21.89, 34.04) * mm, "end": v(-21.85, 33.87) * mm});
            skLineSegment(sketch, "E287", {"start": v(-21.85, 33.87) * mm, "end": v(-21.44, 33.66) * mm});
            skLineSegment(sketch, "E288", {"start": v(-21.44, 33.66) * mm, "end": v(-21.29, 33.19) * mm});
            skLineSegment(sketch, "E289", {"start": v(-21.29, 33.19) * mm, "end": v(-21.26, 33.07) * mm});
            skLineSegment(sketch, "E290", {"start": v(-21.26, 33.07) * mm, "end": v(-21.2, 32.8) * mm});
            skLineSegment(sketch, "E291", {"start": v(-21.2, 32.8) * mm, "end": v(-21.12, 32.55) * mm});
            skLineSegment(sketch, "E292", {"start": v(-21.12, 32.55) * mm, "end": v(-21.1, 32.43) * mm});
            skLineSegment(sketch, "E293", {"start": v(-21.1, 32.43) * mm, "end": v(-20.93, 32.03) * mm});
            skLineSegment(sketch, "E294", {"start": v(-20.93, 32.03) * mm, "end": v(-20.8, 31.74) * mm});
            skLineSegment(sketch, "E295", {"start": v(-20.8, 31.74) * mm, "end": v(-20.69, 31.42) * mm});
            skLineSegment(sketch, "E296", {"start": v(-20.69, 31.42) * mm, "end": v(-20.59, 30.9) * mm});
            skLineSegment(sketch, "E297", {"start": v(-20.59, 30.9) * mm, "end": v(-20.56, 30.67) * mm});
            skLineSegment(sketch, "E298", {"start": v(-20.56, 30.67) * mm, "end": v(-20.48, 30.06) * mm});
            skLineSegment(sketch, "E299", {"start": v(-20.48, 30.06) * mm, "end": v(-20.36, 29.19) * mm});
            skLineSegment(sketch, "E300", {"start": v(-20.36, 29.19) * mm, "end": v(-20.24, 28.2) * mm});
            skLineSegment(sketch, "E301", {"start": v(-20.24, 28.2) * mm, "end": v(-20.1, 27.2) * mm});
            skLineSegment(sketch, "E302", {"start": v(-20.1, 27.2) * mm, "end": v(-20, 26.33) * mm});
            skLineSegment(sketch, "E303", {"start": v(-20, 26.33) * mm, "end": v(-19.91, 25.72) * mm});
            skLineSegment(sketch, "E304", {"start": v(-19.91, 25.72) * mm, "end": v(-19.88, 25.48) * mm});
            skLineSegment(sketch, "E305", {"start": v(-19.88, 25.48) * mm, "end": v(-19.85, 25.06) * mm});
            skLineSegment(sketch, "E306", {"start": v(-19.85, 25.06) * mm, "end": v(-19.76, 24.13) * mm});
            skLineSegment(sketch, "E307", {"start": v(-19.76, 24.13) * mm, "end": v(-19.68, 23.2) * mm});
            skLineSegment(sketch, "E308", {"start": v(-19.68, 23.2) * mm, "end": v(-19.64, 22.78) * mm});
            skLineSegment(sketch, "E309", {"start": v(-19.64, 22.78) * mm, "end": v(-19.67, 22.51) * mm});
            skLineSegment(sketch, "E310", {"start": v(-19.67, 22.51) * mm, "end": v(-19.73, 21.93) * mm});
            skLineSegment(sketch, "E311", {"start": v(-19.73, 21.93) * mm, "end": v(-19.79, 21.35) * mm});
            skLineSegment(sketch, "E312", {"start": v(-19.79, 21.35) * mm, "end": v(-19.81, 21.08) * mm});
            skLineSegment(sketch, "E313", {"start": v(-19.81, 21.08) * mm, "end": v(-19.06, 21.61) * mm});
            skLineSegment(sketch, "E314", {"start": v(-19.06, 21.61) * mm, "end": v(-18.53, 22.17) * mm});
            skLineSegment(sketch, "E315", {"start": v(-18.53, 22.17) * mm, "end": v(-18.07, 22.71) * mm});
            skLineSegment(sketch, "E316", {"start": v(-18.07, 22.71) * mm, "end": v(-17.53, 23.2) * mm});
            skLineSegment(sketch, "E317", {"start": v(-17.53, 23.2) * mm, "end": v(-16.77, 23.56) * mm});
            skLineSegment(sketch, "E318", {"start": v(-16.77, 23.56) * mm, "end": v(-16.17, 23.9) * mm});
            skLineSegment(sketch, "E319", {"start": v(-16.17, 23.9) * mm, "end": v(-16.13, 24.22) * mm});
            skLineSegment(sketch, "E320", {"start": v(-16.13, 24.22) * mm, "end": v(-16.17, 24.55) * mm});
            skLineSegment(sketch, "E321", {"start": v(-16.17, 24.55) * mm, "end": v(-16.09, 25.57) * mm});
            skLineSegment(sketch, "E322", {"start": v(-16.09, 25.57) * mm, "end": v(-16.05, 25.8) * mm});
            skLineSegment(sketch, "E323", {"start": v(-16.05, 25.8) * mm, "end": v(-15.95, 26.42) * mm});
            skLineSegment(sketch, "E324", {"start": v(-15.95, 26.42) * mm, "end": v(-15.81, 27.29) * mm});
            skLineSegment(sketch, "E325", {"start": v(-15.81, 27.29) * mm, "end": v(-15.65, 28.28) * mm});
            skLineSegment(sketch, "E326", {"start": v(-15.65, 28.28) * mm, "end": v(-15.5, 29.27) * mm});
            skLineSegment(sketch, "E327", {"start": v(-15.5, 29.27) * mm, "end": v(-15.35, 30.14) * mm});
            skLineSegment(sketch, "E328", {"start": v(-15.35, 30.14) * mm, "end": v(-15.26, 30.76) * mm});
            skLineSegment(sketch, "E329", {"start": v(-15.26, 30.76) * mm, "end": v(-15.22, 30.99) * mm});
            skLineSegment(sketch, "E330", {"start": v(-15.22, 30.99) * mm, "end": v(-15.2, 31.18) * mm});
            skLineSegment(sketch, "E331", {"start": v(-15.2, 31.18) * mm, "end": v(-15.13, 31.68) * mm});
            skLineSegment(sketch, "E332", {"start": v(-15.13, 31.68) * mm, "end": v(-15.04, 32.38) * mm});
            skLineSegment(sketch, "E333", {"start": v(-15.04, 32.38) * mm, "end": v(-14.93, 33.2) * mm});
            skLineSegment(sketch, "E334", {"start": v(-14.93, 33.2) * mm, "end": v(-14.82, 34) * mm});
            skLineSegment(sketch, "E335", {"start": v(-14.82, 34) * mm, "end": v(-14.73, 34.7) * mm});
            skLineSegment(sketch, "E336", {"start": v(-14.73, 34.7) * mm, "end": v(-14.67, 35.2) * mm});
            skLineSegment(sketch, "E337", {"start": v(-14.67, 35.2) * mm, "end": v(-14.64, 35.4) * mm});
            skLineSegment(sketch, "E338", {"start": v(-14.64, 35.4) * mm, "end": v(-14.6, 35.81) * mm});
            skLineSegment(sketch, "E339", {"start": v(-14.6, 35.81) * mm, "end": v(-14.56, 36.24) * mm});
            skLineSegment(sketch, "E340", {"start": v(-14.56, 36.24) * mm, "end": v(-14.55, 36.58) * mm});
            skLineSegment(sketch, "E341", {"start": v(-14.55, 36.58) * mm, "end": v(-14.52, 37.34) * mm});
            skLineSegment(sketch, "E342", {"start": v(-14.52, 37.34) * mm, "end": v(-14.5, 38.1) * mm});
            skLineSegment(sketch, "E343", {"start": v(-14.5, 38.1) * mm, "end": v(-14.48, 38.44) * mm});
            skLineSegment(sketch, "E344", {"start": v(-14.48, 38.44) * mm, "end": v(-14.52, 38.88) * mm});
            skLineSegment(sketch, "E345", {"start": v(-14.52, 38.88) * mm, "end": v(-14.62, 39.84) * mm});
            skLineSegment(sketch, "E346", {"start": v(-14.62, 39.84) * mm, "end": v(-14.72, 40.8) * mm});
            skLineSegment(sketch, "E347", {"start": v(-14.72, 40.8) * mm, "end": v(-14.77, 41.23) * mm});
            skLineSegment(sketch, "E348", {"start": v(-14.77, 41.23) * mm, "end": v(-15.95, 45.54) * mm});
            skLineSegment(sketch, "E349", {"start": v(-15.95, 45.54) * mm, "end": v(-17.95, 49.4) * mm});
            skLineSegment(sketch, "E350", {"start": v(-17.95, 49.4) * mm, "end": v(-20.75, 52.75) * mm});
            skLineSegment(sketch, "E351", {"start": v(-20.75, 52.75) * mm, "end": v(-24.3, 55.46) * mm});
            skLineSegment(sketch, "E352", {"start": v(-24.3, 55.46) * mm, "end": v(-26.3, 56.55) * mm});
            skLineSegment(sketch, "E353", {"start": v(-26.3, 56.55) * mm, "end": v(-28.36, 57.51) * mm});
            skLineSegment(sketch, "E354", {"start": v(-28.36, 57.51) * mm, "end": v(-28.6, 57.62) * mm});
            skLineSegment(sketch, "E355", {"start": v(-28.6, 57.62) * mm, "end": v(-29.08, 57.84) * mm});
            skLineSegment(sketch, "E356", {"start": v(-29.08, 57.84) * mm, "end": v(-29.58, 58.06) * mm});
            skLineSegment(sketch, "E357", {"start": v(-29.58, 58.06) * mm, "end": v(-29.8, 58.16) * mm});
            skLineSegment(sketch, "E358", {"start": v(-29.8, 58.16) * mm, "end": v(-34.87, 59.74) * mm});
            skLineSegment(sketch, "E359", {"start": v(-34.87, 59.74) * mm, "end": v(-40.05, 60.91) * mm});
            skLineSegment(sketch, "E360", {"start": v(-40.05, 60.91) * mm, "end": v(-48.94, 62.06) * mm});
            skLineSegment(sketch, "E361", {"start": v(-48.94, 62.06) * mm, "end": v(-49.11, 62.08) * mm});
            skLineSegment(sketch, "E362", {"start": v(-49.11, 62.08) * mm, "end": v(-49.49, 62.1) * mm});
            skLineSegment(sketch, "E363", {"start": v(-49.49, 62.1) * mm, "end": v(-49.87, 62.13) * mm});
            skLineSegment(sketch, "E364", {"start": v(-49.87, 62.13) * mm, "end": v(-50.04, 62.15) * mm});
            skLineSegment(sketch, "E365", {"start": v(-50.04, 62.15) * mm, "end": v(-50.24, 62.15) * mm});
            skLineSegment(sketch, "E366", {"start": v(-50.24, 62.15) * mm, "end": v(-50.75, 62.15) * mm});
            skLineSegment(sketch, "E367", {"start": v(-50.75, 62.15) * mm, "end": v(-51.49, 62.15) * mm});
            skLineSegment(sketch, "E368", {"start": v(-51.49, 62.15) * mm, "end": v(-52.32, 62.15) * mm});
            skLineSegment(sketch, "E369", {"start": v(-52.32, 62.15) * mm, "end": v(-53.17, 62.15) * mm});
            skLineSegment(sketch, "E370", {"start": v(-53.17, 62.15) * mm, "end": v(-53.9, 62.15) * mm});
            skLineSegment(sketch, "E371", {"start": v(-53.9, 62.15) * mm, "end": v(-54.42, 62.15) * mm});
            skLineSegment(sketch, "E372", {"start": v(-54.42, 62.15) * mm, "end": v(-54.61, 62.15) * mm});
            skLineSegment(sketch, "E373", {"start": v(-54.61, 62.15) * mm, "end": v(-54.77, 62.14) * mm});
            skLineSegment(sketch, "E374", {"start": v(-54.77, 62.14) * mm, "end": v(-55.12, 62.1) * mm});
            skLineSegment(sketch, "E375", {"start": v(-55.12, 62.1) * mm, "end": v(-55.47, 62.08) * mm});
            skLineSegment(sketch, "E376", {"start": v(-55.47, 62.08) * mm, "end": v(-55.63, 62.07) * mm});
            skLineSegment(sketch, "E377", {"start": v(-55.63, 62.07) * mm, "end": v(-56.05, 62.04) * mm});
            skLineSegment(sketch, "E378", {"start": v(-56.05, 62.04) * mm, "end": v(-56.98, 61.97) * mm});
            skLineSegment(sketch, "E379", {"start": v(-56.98, 61.97) * mm, "end": v(-57.91, 61.9) * mm});
            skLineSegment(sketch, "E380", {"start": v(-57.91, 61.9) * mm, "end": v(-58.34, 61.88) * mm});
            skLineSegment(sketch, "E381", {"start": v(-58.34, 61.88) * mm, "end": v(-58.72, 61.81) * mm});
            skLineSegment(sketch, "E382", {"start": v(-58.72, 61.81) * mm, "end": v(-59.1, 61.75) * mm});
            skLineSegment(sketch, "E383", {"start": v(-59.1, 61.75) * mm, "end": v(-59.28, 61.72) * mm});
            skLineSegment(sketch, "E384", {"start": v(-59.28, 61.72) * mm, "end": v(-59.77, 61.64) * mm});
            skLineSegment(sketch, "E385", {"start": v(-59.77, 61.64) * mm, "end": v(-60.46, 61.54) * mm});
            skLineSegment(sketch, "E386", {"start": v(-60.46, 61.54) * mm, "end": v(-61.26, 61.42) * mm});
            skLineSegment(sketch, "E387", {"start": v(-61.26, 61.42) * mm, "end": v(-62.05, 61.3) * mm});
            skLineSegment(sketch, "E388", {"start": v(-62.05, 61.3) * mm, "end": v(-62.74, 61.19) * mm});
            skLineSegment(sketch, "E389", {"start": v(-62.74, 61.19) * mm, "end": v(-63.23, 61.11) * mm});
            skLineSegment(sketch, "E390", {"start": v(-63.23, 61.11) * mm, "end": v(-63.42, 61.08) * mm});
            skLineSegment(sketch, "E391", {"start": v(-63.42, 61.08) * mm, "end": v(-67.56, 60.2) * mm});
            skLineSegment(sketch, "E392", {"start": v(-67.56, 60.2) * mm, "end": v(-71.63, 59.04) * mm});
            skLineSegment(sketch, "E393", {"start": v(-71.63, 59.04) * mm, "end": v(-78.06, 56.1) * mm});
            skLineSegment(sketch, "E394", {"start": v(-78.06, 56.1) * mm, "end": v(-78.25, 56) * mm});
            skLineSegment(sketch, "E395", {"start": v(-78.25, 56) * mm, "end": v(-78.74, 55.7) * mm});
            skLineSegment(sketch, "E396", {"start": v(-78.74, 55.7) * mm, "end": v(-79.43, 55.29) * mm});
            skLineSegment(sketch, "E397", {"start": v(-79.43, 55.29) * mm, "end": v(-80.22, 54.8) * mm});
            skLineSegment(sketch, "E398", {"start": v(-80.22, 54.8) * mm, "end": v(-81.02, 54.33) * mm});
            skLineSegment(sketch, "E399", {"start": v(-81.02, 54.33) * mm, "end": v(-81.7, 53.91) * mm});
            skLineSegment(sketch, "E400", {"start": v(-81.7, 53.91) * mm, "end": v(-82.2, 53.62) * mm});
            skLineSegment(sketch, "E401", {"start": v(-82.2, 53.62) * mm, "end": v(-82.38, 53.5) * mm});
            skLineSegment(sketch, "E402", {"start": v(-82.38, 53.5) * mm, "end": v(-85, 51.53) * mm});
            skLineSegment(sketch, "E403", {"start": v(-85, 51.53) * mm, "end": v(-87.38, 49.28) * mm});
            skLineSegment(sketch, "E404", {"start": v(-87.38, 49.28) * mm, "end": v(-89.02, 47.6) * mm});
            skLineSegment(sketch, "E405", {"start": v(-89.02, 47.6) * mm, "end": v(-90.54, 45.8) * mm});
            skLineSegment(sketch, "E406", {"start": v(-90.54, 45.8) * mm, "end": v(-91.98, 43.66) * mm});
            skLineSegment(sketch, "E407", {"start": v(-91.98, 43.66) * mm, "end": v(-93.15, 41.29) * mm});
            skLineSegment(sketch, "E408", {"start": v(-93.15, 41.29) * mm, "end": v(-94, 38.79) * mm});
            skLineSegment(sketch, "E409", {"start": v(-94, 38.79) * mm, "end": v(-94.41, 36.24) * mm});
            skLineSegment(sketch, "E410", {"start": v(-94.41, 36.24) * mm, "end": v(-94.45, 35.81) * mm});
            skLineSegment(sketch, "E411", {"start": v(-94.45, 35.81) * mm, "end": v(-94.49, 35.4) * mm});
            skLineSegment(sketch, "E412", {"start": v(-94.49, 35.4) * mm, "end": v(-94.3, 32.7) * mm});
            skLineSegment(sketch, "E413", {"start": v(-94.3, 32.7) * mm, "end": v(-93.7, 30.06) * mm});
            skLineSegment(sketch, "E414", {"start": v(-93.7, 30.06) * mm, "end": v(-93.59, 29.8) * mm});
            skLineSegment(sketch, "E415", {"start": v(-93.59, 29.8) * mm, "end": v(-93.35, 29.21) * mm});
            skLineSegment(sketch, "E416", {"start": v(-93.35, 29.21) * mm, "end": v(-93.11, 28.63) * mm});
            skLineSegment(sketch, "E417", {"start": v(-93.11, 28.63) * mm, "end": v(-93, 28.36) * mm});
            skLineSegment(sketch, "E418", {"start": v(-93, 28.36) * mm, "end": v(-92.94, 28.21) * mm});
            skLineSegment(sketch, "E419", {"start": v(-92.94, 28.21) * mm, "end": v(-92.76, 27.82) * mm});
            skLineSegment(sketch, "E420", {"start": v(-92.76, 27.82) * mm, "end": v(-92.52, 27.27) * mm});
            skLineSegment(sketch, "E421", {"start": v(-92.52, 27.27) * mm, "end": v(-92.23, 26.63) * mm});
            skLineSegment(sketch, "E422", {"start": v(-92.23, 26.63) * mm, "end": v(-91.95, 26) * mm});
            skLineSegment(sketch, "E423", {"start": v(-91.95, 26) * mm, "end": v(-91.7, 25.44) * mm});
            skLineSegment(sketch, "E424", {"start": v(-91.7, 25.44) * mm, "end": v(-91.53, 25.04) * mm});
            skLineSegment(sketch, "E425", {"start": v(-91.53, 25.04) * mm, "end": v(-91.46, 24.9) * mm});
            skLineSegment(sketch, "E426", {"start": v(-91.46, 24.9) * mm, "end": v(-89.22, 21.39) * mm});
            skLineSegment(sketch, "E427", {"start": v(-89.22, 21.39) * mm, "end": v(-86.45, 18.29) * mm});
            skLineSegment(sketch, "E428", {"start": v(-86.45, 18.29) * mm, "end": v(-85.93, 19.2) * mm});
            skLineSegment(sketch, "E429", {"start": v(-85.93, 19.2) * mm, "end": v(-85.37, 19.95) * mm});
            skLineSegment(sketch, "E430", {"start": v(-85.37, 19.95) * mm, "end": v(-84.7, 20.61) * mm});
            skLineSegment(sketch, "E431", {"start": v(-84.7, 20.61) * mm, "end": v(-83.82, 21.2) * mm});
            skLineSegment(sketch, "E432", {"start": v(-83.82, 21.2) * mm, "end": v(-82.89, 21.62) * mm});
            skLineSegment(sketch, "E433", {"start": v(-82.89, 21.62) * mm, "end": v(-81.62, 21.76) * mm});
            skLineSegment(sketch, "E434", {"start": v(-81.62, 21.76) * mm, "end": v(-80.35, 21.62) * mm});
            skLineSegment(sketch, "E435", {"start": v(-80.35, 21.62) * mm, "end": v(-79.66, 21.43) * mm});
            skLineSegment(sketch, "E436", {"start": v(-79.66, 21.43) * mm, "end": v(-78.95, 21.13) * mm});
            skLineSegment(sketch, "E437", {"start": v(-78.95, 21.13) * mm, "end": v(-78.37, 20.7) * mm});
            skLineSegment(sketch, "E438", {"start": v(-78.37, 20.7) * mm, "end": v(-78.06, 20.07) * mm});
            skLineSegment(sketch, "E439", {"start": v(-78.06, 20.07) * mm, "end": v(-78.32, 19.86) * mm});
            skLineSegment(sketch, "E440", {"start": v(-78.32, 19.86) * mm, "end": v(-78.58, 19.64) * mm});
            skLineSegment(sketch, "E441", {"start": v(-78.58, 19.64) * mm, "end": v(-78.35, 19.37) * mm});
            skLineSegment(sketch, "E442", {"start": v(-78.35, 19.37) * mm, "end": v(-78.58, 19.13) * mm});
            skLineSegment(sketch, "E443", {"start": v(-78.58, 19.13) * mm, "end": v(-79.04, 19.13) * mm});
            skLineSegment(sketch, "E444", {"start": v(-79.04, 19.13) * mm, "end": v(-79.5, 19.13) * mm});
            skLineSegment(sketch, "E445", {"start": v(-79.5, 19.13) * mm, "end": v(-80.67, 18.92) * mm});
            skLineSegment(sketch, "E446", {"start": v(-80.67, 18.92) * mm, "end": v(-81.86, 18.35) * mm});
            skLineSegment(sketch, "E447", {"start": v(-81.86, 18.35) * mm, "end": v(-82.93, 17.56) * mm});
            skLineSegment(sketch, "E448", {"start": v(-82.93, 17.56) * mm, "end": v(-83.73, 16.68) * mm});
            skLineSegment(sketch, "E449", {"start": v(-83.73, 16.68) * mm, "end": v(-84.17, 15.95) * mm});
            skLineSegment(sketch, "E450", {"start": v(-84.17, 15.95) * mm, "end": v(-84.54, 15.1) * mm});
            skLineSegment(sketch, "E451", {"start": v(-84.54, 15.1) * mm, "end": v(-84.8, 14.22) * mm});
            skLineSegment(sketch, "E452", {"start": v(-84.8, 14.22) * mm, "end": v(-84.92, 13.38) * mm});
            skLineSegment(sketch, "E453", {"start": v(-84.92, 13.38) * mm, "end": v(-84.84, 12.62) * mm});
            skLineSegment(sketch, "E454", {"start": v(-84.84, 12.62) * mm, "end": v(-84.6, 11.8) * mm});
            skLineSegment(sketch, "E455", {"start": v(-84.6, 11.8) * mm, "end": v(-84.28, 11.02) * mm});
            skLineSegment(sketch, "E456", {"start": v(-84.28, 11.02) * mm, "end": v(-83.94, 10.33) * mm});
            skLineSegment(sketch, "E457", {"start": v(-83.94, 10.33) * mm, "end": v(-83.13, 9.1) * mm});
            skLineSegment(sketch, "E458", {"start": v(-83.13, 9.1) * mm, "end": v(-82.04, 8.16) * mm});
            skLineSegment(sketch, "E459", {"start": v(-82.04, 8.16) * mm, "end": v(-80.51, 7.68) * mm});
            skLineSegment(sketch, "E460", {"start": v(-80.51, 7.68) * mm, "end": v(-78.91, 7.7) * mm});
            skLineSegment(sketch, "E461", {"start": v(-78.91, 7.7) * mm, "end": v(-78.66, 7.72) * mm});
            skLineSegment(sketch, "E462", {"start": v(-78.66, 7.72) * mm, "end": v(-78.4, 7.74) * mm});
            skLineSegment(sketch, "E463", {"start": v(-78.4, 7.74) * mm, "end": v(-78.06, 7.85) * mm});
            skLineSegment(sketch, "E464", {"start": v(-78.06, 7.85) * mm, "end": v(-77.72, 7.96) * mm});
            skLineSegment(sketch, "E465", {"start": v(-77.72, 7.96) * mm, "end": v(-77.72, 7.79) * mm});
            skLineSegment(sketch, "E466", {"start": v(-77.72, 7.79) * mm, "end": v(-77.39, 7.79) * mm});
            skLineSegment(sketch, "E467", {"start": v(-77.39, 7.79) * mm, "end": v(-77.05, 7.79) * mm});
            skLineSegment(sketch, "E468", {"start": v(-77.05, 7.79) * mm, "end": v(-76.84, 7.66) * mm});
            skLineSegment(sketch, "E469", {"start": v(-76.84, 7.66) * mm, "end": v(-76.62, 7.54) * mm});
            skLineSegment(sketch, "E470", {"start": v(-76.62, 7.54) * mm, "end": v(-76.3, 9.18) * mm});
            skLineSegment(sketch, "E471", {"start": v(-76.3, 9.18) * mm, "end": v(-76.1, 10.84) * mm});
            skLineSegment(sketch, "E472", {"start": v(-76.1, 10.84) * mm, "end": v(-76.08, 10.98) * mm});
            skLineSegment(sketch, "E473", {"start": v(-76.08, 10.98) * mm, "end": v(-76.03, 11.3) * mm});
            skLineSegment(sketch, "E474", {"start": v(-76.03, 11.3) * mm, "end": v(-75.98, 11.62) * mm});
            skLineSegment(sketch, "E475", {"start": v(-75.98, 11.62) * mm, "end": v(-75.96, 11.77) * mm});
            skLineSegment(sketch, "E476", {"start": v(-75.96, 11.77) * mm, "end": v(-75.9, 12.76) * mm});
            skLineSegment(sketch, "E477", {"start": v(-75.9, 12.76) * mm, "end": v(-75.7, 13.72) * mm});
            skLineSegment(sketch, "E478", {"start": v(-75.7, 13.72) * mm, "end": v(-75.65, 13.55) * mm});
            skLineSegment(sketch, "E479", {"start": v(-75.65, 13.55) * mm, "end": v(-75.6, 13.38) * mm});
            skLineSegment(sketch, "E480", {"start": v(-75.6, 13.38) * mm, "end": v(-75.65, 13.8) * mm});
            skLineSegment(sketch, "E481", {"start": v(-75.65, 13.8) * mm, "end": v(-75.7, 14.23) * mm});
            skLineSegment(sketch, "E482", {"start": v(-75.7, 14.23) * mm, "end": v(-75.78, 14.18) * mm});
            skLineSegment(sketch, "E483", {"start": v(-75.78, 14.18) * mm, "end": v(-75.86, 14.14) * mm});
            skLineSegment(sketch, "E484", {"start": v(-75.86, 14.14) * mm, "end": v(-75.84, 14.27) * mm});
            skLineSegment(sketch, "E485", {"start": v(-75.84, 14.27) * mm, "end": v(-75.78, 14.56) * mm});
            skLineSegment(sketch, "E486", {"start": v(-75.78, 14.56) * mm, "end": v(-75.72, 14.85) * mm});
            skLineSegment(sketch, "E487", {"start": v(-75.72, 14.85) * mm, "end": v(-75.7, 14.99) * mm});
            skLineSegment(sketch, "E488", {"start": v(-75.7, 14.99) * mm, "end": v(-75.65, 14.6) * mm});
            skLineSegment(sketch, "E489", {"start": v(-75.65, 14.6) * mm, "end": v(-75.6, 14.23) * mm});
            skLineSegment(sketch, "E490", {"start": v(-75.6, 14.23) * mm, "end": v(-75.59, 14.45) * mm});
            skLineSegment(sketch, "E491", {"start": v(-75.59, 14.45) * mm, "end": v(-75.54, 14.94) * mm});
            skLineSegment(sketch, "E492", {"start": v(-75.54, 14.94) * mm, "end": v(-75.49, 15.44) * mm});
            skLineSegment(sketch, "E493", {"start": v(-75.49, 15.44) * mm, "end": v(-75.46, 15.66) * mm});
            skLineSegment(sketch, "E494", {"start": v(-75.46, 15.66) * mm, "end": v(-75.45, 15.8) * mm});
            skLineSegment(sketch, "E495", {"start": v(-75.45, 15.8) * mm, "end": v(-75.41, 16.09) * mm});
            skLineSegment(sketch, "E496", {"start": v(-75.41, 16.09) * mm, "end": v(-75.38, 16.38) * mm});
            skLineSegment(sketch, "E497", {"start": v(-75.38, 16.38) * mm, "end": v(-75.36, 16.5) * mm});
            skLineSegment(sketch, "E498", {"start": v(-75.36, 16.5) * mm, "end": v(-75.36, 16.34) * mm});
            skLineSegment(sketch, "E499", {"start": v(-75.36, 16.34) * mm, "end": v(-75.36, 15.96) * mm});
            skLineSegment(sketch, "E500", {"start": v(-75.36, 15.96) * mm, "end": v(-75.36, 15.58) * mm});
            skLineSegment(sketch, "E501", {"start": v(-75.36, 15.58) * mm, "end": v(-75.36, 15.4) * mm});
            skLineSegment(sketch, "E502", {"start": v(-75.36, 15.4) * mm, "end": v(-75.39, 15.17) * mm});
            skLineSegment(sketch, "E503", {"start": v(-75.39, 15.17) * mm, "end": v(-75.44, 14.65) * mm});
            skLineSegment(sketch, "E504", {"start": v(-75.44, 14.65) * mm, "end": v(-75.5, 14.12) * mm});
            skLineSegment(sketch, "E505", {"start": v(-75.5, 14.12) * mm, "end": v(-75.52, 13.89) * mm});
            skLineSegment(sketch, "E506", {"start": v(-75.52, 13.89) * mm, "end": v(-75.54, 13.54) * mm});
            skLineSegment(sketch, "E507", {"start": v(-75.54, 13.54) * mm, "end": v(-75.57, 12.78) * mm});
            skLineSegment(sketch, "E508", {"start": v(-75.57, 12.78) * mm, "end": v(-75.6, 12.03) * mm});
            skLineSegment(sketch, "E509", {"start": v(-75.6, 12.03) * mm, "end": v(-75.6, 11.68) * mm});
            skLineSegment(sketch, "E510", {"start": v(-75.6, 11.68) * mm, "end": v(-75.65, 11.37) * mm});
            skLineSegment(sketch, "E511", {"start": v(-75.65, 11.37) * mm, "end": v(-75.73, 10.67) * mm});
            skLineSegment(sketch, "E512", {"start": v(-75.73, 10.67) * mm, "end": v(-75.81, 9.97) * mm});
            skLineSegment(sketch, "E513", {"start": v(-75.81, 9.97) * mm, "end": v(-75.85, 9.65) * mm});
            skLineSegment(sketch, "E514", {"start": v(-75.85, 9.65) * mm, "end": v(-75.87, 9.32) * mm});
            skLineSegment(sketch, "E515", {"start": v(-75.87, 9.32) * mm, "end": v(-75.9, 8.6) * mm});
            skLineSegment(sketch, "E516", {"start": v(-75.9, 8.6) * mm, "end": v(-75.94, 7.87) * mm});
            skLineSegment(sketch, "E517", {"start": v(-75.94, 7.87) * mm, "end": v(-75.95, 7.54) * mm});
            skLineSegment(sketch, "E518", {"start": v(-75.95, 7.54) * mm, "end": v(-76, 7.11) * mm});
            skLineSegment(sketch, "E519", {"start": v(-76, 7.11) * mm, "end": v(-76.08, 6.18) * mm});
            skLineSegment(sketch, "E520", {"start": v(-76.08, 6.18) * mm, "end": v(-76.16, 5.25) * mm});
            skLineSegment(sketch, "E521", {"start": v(-76.16, 5.25) * mm, "end": v(-76.2, 4.83) * mm});
            skLineSegment(sketch, "E522", {"start": v(-76.2, 4.83) * mm, "end": v(-76.21, 4.3) * mm});
            skLineSegment(sketch, "E523", {"start": v(-76.21, 4.3) * mm, "end": v(-76.24, 3.13) * mm});
            skLineSegment(sketch, "E524", {"start": v(-76.24, 3.13) * mm, "end": v(-76.27, 1.97) * mm});
            skLineSegment(sketch, "E525", {"start": v(-76.27, 1.97) * mm, "end": v(-76.29, 1.44) * mm});
            skLineSegment(sketch, "E526", {"start": v(-76.29, 1.44) * mm, "end": v(-76.22, 0.76) * mm});
            skLineSegment(sketch, "E527", {"start": v(-76.22, 0.76) * mm, "end": v(-75.95, 0.33) * mm});
            skLineSegment(sketch, "E528", {"start": v(-75.95, 0.33) * mm, "end": v(-75.6, -0.08) * mm});
            skLineSegment(sketch, "E529", {"start": v(-75.6, -0.08) * mm, "end": v(-75.08, -0.69) * mm});
            skLineSegment(sketch, "E530", {"start": v(-75.08, -0.69) * mm, "end": v(-74.57, -1.16) * mm});
            skLineSegment(sketch, "E531", {"start": v(-74.57, -1.16) * mm, "end": v(-74, -1.57) * mm});
            skLineSegment(sketch, "E532", {"start": v(-74, -1.57) * mm, "end": v(-73.32, -1.98) * mm});
            skLineSegment(sketch, "E533", {"start": v(-73.32, -1.98) * mm, "end": v(-69.6, -3.68) * mm});
            skLineSegment(sketch, "E534", {"start": v(-69.6, -3.68) * mm, "end": v(-69.41, -3.73) * mm});
            skLineSegment(sketch, "E535", {"start": v(-69.41, -3.73) * mm, "end": v(-69, -3.85) * mm});
            skLineSegment(sketch, "E536", {"start": v(-69, -3.85) * mm, "end": v(-68.6, -3.96) * mm});
            skLineSegment(sketch, "E537", {"start": v(-68.6, -3.96) * mm, "end": v(-68.41, -4) * mm});
            skLineSegment(sketch, "E538", {"start": v(-68.41, -4) * mm, "end": v(-68.27, -4.07) * mm});
            skLineSegment(sketch, "E539", {"start": v(-68.27, -4.07) * mm, "end": v(-67.95, -4.21) * mm});
            skLineSegment(sketch, "E540", {"start": v(-67.95, -4.21) * mm, "end": v(-67.63, -4.35) * mm});
            skLineSegment(sketch, "E541", {"start": v(-67.63, -4.35) * mm, "end": v(-67.48, -4.41) * mm});
            skLineSegment(sketch, "E542", {"start": v(-67.48, -4.41) * mm, "end": v(-67.3, -4.48) * mm});
            skLineSegment(sketch, "E543", {"start": v(-67.3, -4.48) * mm, "end": v(-66.89, -4.62) * mm});
            skLineSegment(sketch, "E544", {"start": v(-66.89, -4.62) * mm, "end": v(-66.48, -4.76) * mm});
            skLineSegment(sketch, "E545", {"start": v(-66.48, -4.76) * mm, "end": v(-66.3, -4.82) * mm});
            skLineSegment(sketch, "E546", {"start": v(-66.3, -4.82) * mm, "end": v(-65.95, -4.91) * mm});
            skLineSegment(sketch, "E547", {"start": v(-65.95, -4.91) * mm, "end": v(-65.2, -5.11) * mm});
            skLineSegment(sketch, "E548", {"start": v(-65.2, -5.11) * mm, "end": v(-64.44, -5.31) * mm});
            skLineSegment(sketch, "E549", {"start": v(-64.44, -5.31) * mm, "end": v(-64.1, -5.4) * mm});
            skLineSegment(sketch, "E550", {"start": v(-64.1, -5.4) * mm, "end": v(-63.82, -5.45) * mm});
            skLineSegment(sketch, "E551", {"start": v(-63.82, -5.45) * mm, "end": v(-63.2, -5.56) * mm});
            skLineSegment(sketch, "E552", {"start": v(-63.2, -5.56) * mm, "end": v(-62.6, -5.68) * mm});
            skLineSegment(sketch, "E553", {"start": v(-62.6, -5.68) * mm, "end": v(-62.32, -5.73) * mm});
            skLineSegment(sketch, "E554", {"start": v(-62.32, -5.73) * mm, "end": v(-62.01, -5.8) * mm});
            skLineSegment(sketch, "E555", {"start": v(-62.01, -5.8) * mm, "end": v(-61.34, -5.93) * mm});
            skLineSegment(sketch, "E556", {"start": v(-61.34, -5.93) * mm, "end": v(-60.67, -6.07) * mm});
            skLineSegment(sketch, "E557", {"start": v(-60.67, -6.07) * mm, "end": v(-60.37, -6.14) * mm});
            skLineSegment(sketch, "E558", {"start": v(-60.37, -6.14) * mm, "end": v(-60.05, -6.23) * mm});
            skLineSegment(sketch, "E559", {"start": v(-60.05, -6.23) * mm, "end": v(-59.35, -6.43) * mm});
            skLineSegment(sketch, "E560", {"start": v(-59.35, -6.43) * mm, "end": v(-58.65, -6.64) * mm});
            skLineSegment(sketch, "E561", {"start": v(-58.65, -6.64) * mm, "end": v(-58.34, -6.73) * mm});
            skLineSegment(sketch, "E562", {"start": v(-58.34, -6.73) * mm, "end": v(-57.91, -6.84) * mm});
            skLineSegment(sketch, "E563", {"start": v(-57.91, -6.84) * mm, "end": v(-56.98, -7.07) * mm});
            skLineSegment(sketch, "E564", {"start": v(-56.98, -7.07) * mm, "end": v(-56.05, -7.3) * mm});
            skLineSegment(sketch, "E565", {"start": v(-56.05, -7.3) * mm, "end": v(-55.63, -7.4) * mm});
            skLineSegment(sketch, "E566", {"start": v(-55.63, -7.4) * mm, "end": v(-55.36, -7.5) * mm});
            skLineSegment(sketch, "E567", {"start": v(-55.36, -7.5) * mm, "end": v(-54.78, -7.69) * mm});
            skLineSegment(sketch, "E568", {"start": v(-54.78, -7.69) * mm, "end": v(-54.2, -7.89) * mm});
            skLineSegment(sketch, "E569", {"start": v(-54.2, -7.89) * mm, "end": v(-53.93, -7.98) * mm});
            skLineSegment(sketch, "E570", {"start": v(-53.93, -7.98) * mm, "end": v(-53.7, -8.04) * mm});
            skLineSegment(sketch, "E571", {"start": v(-53.7, -8.04) * mm, "end": v(-53.22, -8.16) * mm});
            skLineSegment(sketch, "E572", {"start": v(-53.22, -8.16) * mm, "end": v(-52.72, -8.29) * mm});
            skLineSegment(sketch, "E573", {"start": v(-52.72, -8.29) * mm, "end": v(-52.5, -8.35) * mm});
            skLineSegment(sketch, "E574", {"start": v(-52.5, -8.35) * mm, "end": v(-51.21, -8.6) * mm});
            skLineSegment(sketch, "E575", {"start": v(-51.21, -8.6) * mm, "end": v(-49.7, -8.86) * mm});
            skLineSegment(sketch, "E576", {"start": v(-49.7, -8.86) * mm, "end": v(-48.19, -9.06) * mm});
            skLineSegment(sketch, "E577", {"start": v(-48.19, -9.06) * mm, "end": v(-46.9, -9.14) * mm});
            skLineSegment(sketch, "E578", {"start": v(-46.9, -9.14) * mm, "end": v(-46.58, -9.14) * mm});
            skLineSegment(sketch, "E579", {"start": v(-46.58, -9.14) * mm, "end": v(-45.85, -9.14) * mm});
            skLineSegment(sketch, "E580", {"start": v(-45.85, -9.14) * mm, "end": v(-45.12, -9.14) * mm});
            skLineSegment(sketch, "E581", {"start": v(-45.12, -9.14) * mm, "end": v(-44.79, -9.14) * mm});
            skLineSegment(sketch, "E582", {"start": v(-44.79, -9.14) * mm, "end": v(-44.6, -9.13) * mm});
            skLineSegment(sketch, "E583", {"start": v(-44.6, -9.13) * mm, "end": v(-44.15, -9.1) * mm});
            skLineSegment(sketch, "E584", {"start": v(-44.15, -9.1) * mm, "end": v(-43.72, -9.06) * mm});
            skLineSegment(sketch, "E585", {"start": v(-43.72, -9.06) * mm, "end": v(-43.52, -9.05) * mm});
            skLineSegment(sketch, "E586", {"start": v(-43.52, -9.05) * mm, "end": v(-43.1, -9.05) * mm});
            skLineSegment(sketch, "E587", {"start": v(-43.1, -9.05) * mm, "end": v(-42.67, -9.05) * mm});
            skLineSegment(sketch, "E588", {"start": v(-42.67, -9.05) * mm, "end": v(-42.3, -8.92) * mm});
            skLineSegment(sketch, "E589", {"start": v(-42.3, -8.92) * mm, "end": v(-41.49, -8.64) * mm});
            skLineSegment(sketch, "E590", {"start": v(-41.49, -8.64) * mm, "end": v(-40.67, -8.37) * mm});
            skLineSegment(sketch, "E591", {"start": v(-40.67, -8.37) * mm, "end": v(-40.3, -8.24) * mm});
            skLineSegment(sketch, "E592", {"start": v(-40.3, -8.24) * mm, "end": v(-40.17, -8.2) * mm});
            skLineSegment(sketch, "E593", {"start": v(-40.17, -8.2) * mm, "end": v(-39.83, -8.11) * mm});
            skLineSegment(sketch, "E594", {"start": v(-39.83, -8.11) * mm, "end": v(-39.34, -7.98) * mm});
            skLineSegment(sketch, "E595", {"start": v(-39.34, -7.98) * mm, "end": v(-38.78, -7.83) * mm});
            skLineSegment(sketch, "E596", {"start": v(-38.78, -7.83) * mm, "end": v(-38.22, -7.67) * mm});
            skLineSegment(sketch, "E597", {"start": v(-38.22, -7.67) * mm, "end": v(-37.73, -7.54) * mm});
            skLineSegment(sketch, "E598", {"start": v(-37.73, -7.54) * mm, "end": v(-37.39, -7.45) * mm});
            skLineSegment(sketch, "E599", {"start": v(-37.39, -7.45) * mm, "end": v(-37.25, -7.41) * mm});
            skLineSegment(sketch, "E600", {"start": v(-37.25, -7.41) * mm, "end": v(-36.95, -7.32) * mm});
            skLineSegment(sketch, "E601", {"start": v(-36.95, -7.32) * mm, "end": v(-36.28, -7.13) * mm});
            skLineSegment(sketch, "E602", {"start": v(-36.28, -7.13) * mm, "end": v(-35.61, -6.93) * mm});
            skLineSegment(sketch, "E603", {"start": v(-35.61, -6.93) * mm, "end": v(-35.3, -6.84) * mm});
            skLineSegment(sketch, "E604", {"start": v(-35.3, -6.84) * mm, "end": v(-34.95, -6.78) * mm});
            skLineSegment(sketch, "E605", {"start": v(-34.95, -6.78) * mm, "end": v(-34.17, -6.65) * mm});
            skLineSegment(sketch, "E606", {"start": v(-34.17, -6.65) * mm, "end": v(-33.38, -6.53) * mm});
            skLineSegment(sketch, "E607", {"start": v(-33.38, -6.53) * mm, "end": v(-33.02, -6.47) * mm});
            skLineSegment(sketch, "E608", {"start": v(-33.02, -6.47) * mm, "end": v(-28.45, -5.38) * mm});
            skLineSegment(sketch, "E609", {"start": v(-28.45, -5.38) * mm, "end": v(-24.22, -3.37) * mm});
            skLineSegment(sketch, "E610", {"start": v(-24.22, -3.37) * mm, "end": v(-23.63, -2.86) * mm});
            skLineSegment(sketch, "E611", {"start": v(-23.63, -2.86) * mm, "end": v(-23.04, -2.2) * mm});
            skLineSegment(sketch, "E612", {"start": v(-23.04, -2.2) * mm, "end": v(-22.5, -1.5) * mm});
            skLineSegment(sketch, "E613", {"start": v(-22.5, -1.5) * mm, "end": v(-22.04, -0.85) * mm});
            skLineSegment(sketch, "E614", {"start": v(-22.04, -0.85) * mm, "end": v(-21.12, 0.75) * mm});
            skLineSegment(sketch, "E615", {"start": v(-21.12, 0.75) * mm, "end": v(-20.42, 2.46) * mm});
            skLineSegment(sketch, "E616", {"start": v(-20.42, 2.46) * mm, "end": v(-20.37, 2.7) * mm});
            skLineSegment(sketch, "E617", {"start": v(-20.37, 2.7) * mm, "end": v(-20.24, 3.26) * mm});
            skLineSegment(sketch, "E618", {"start": v(-20.24, 3.26) * mm, "end": v(-20.1, 3.81) * mm});
            skLineSegment(sketch, "E619", {"start": v(-20.1, 3.81) * mm, "end": v(-20.05, 4.06) * mm});
            skLineSegment(sketch, "E620", {"start": v(-20.05, 4.06) * mm, "end": v(-19.98, 4.44) * mm});
            skLineSegment(sketch, "E621", {"start": v(-19.98, 4.44) * mm, "end": v(-19.82, 5.25) * mm});
            skLineSegment(sketch, "E622", {"start": v(-19.82, 5.25) * mm, "end": v(-19.66, 6.07) * mm});
            skLineSegment(sketch, "E623", {"start": v(-19.66, 6.07) * mm, "end": v(-19.58, 6.43) * mm});
            skLineSegment(sketch, "E624", {"start": v(-19.58, 6.43) * mm, "end": v(-19.56, 6.86) * mm});
            skLineSegment(sketch, "E625", {"start": v(-19.56, 6.86) * mm, "end": v(-19.54, 7.28) * mm});
            skLineSegment(sketch, "E626", {"start": v(-19.54, 7.28) * mm, "end": v(-19.5, 7.55) * mm});
            skLineSegment(sketch, "E627", {"start": v(-19.5, 7.55) * mm, "end": v(-19.43, 8.13) * mm});
            skLineSegment(sketch, "E628", {"start": v(-19.43, 8.13) * mm, "end": v(-19.35, 8.71) * mm});
            skLineSegment(sketch, "E629", {"start": v(-19.35, 8.71) * mm, "end": v(-19.32, 8.97) * mm});
            skLineSegment(sketch, "E630", {"start": v(-19.32, 8.97) * mm, "end": v(-19.3, 9.25) * mm});
            skLineSegment(sketch, "E631", {"start": v(-19.3, 9.25) * mm, "end": v(-19.26, 9.86) * mm});
            skLineSegment(sketch, "E632", {"start": v(-19.26, 9.86) * mm, "end": v(-19.22, 10.48) * mm});
            skLineSegment(sketch, "E633", {"start": v(-19.22, 10.48) * mm, "end": v(-19.2, 10.75) * mm});
            skLineSegment(sketch, "E634", {"start": v(-19.2, 10.75) * mm, "end": v(-19.18, 10.89) * mm});
            skLineSegment(sketch, "E635", {"start": v(-19.18, 10.89) * mm, "end": v(-19.13, 11.18) * mm});
            skLineSegment(sketch, "E636", {"start": v(-19.13, 11.18) * mm, "end": v(-19.08, 11.47) * mm});
            skLineSegment(sketch, "E637", {"start": v(-19.08, 11.47) * mm, "end": v(-19.05, 11.6) * mm});
            skLineSegment(sketch, "E638", {"start": v(-19.05, 11.6) * mm, "end": v(-19.05, 11.94) * mm});
            skLineSegment(sketch, "E639", {"start": v(-19.05, 11.94) * mm, "end": v(-19.05, 12.28) * mm});
            skLineSegment(sketch, "E640", {"start": v(-19.05, 12.28) * mm, "end": v(-18.82, 13.82) * mm});
            skLineSegment(sketch, "E641", {"start": v(-18.82, 13.82) * mm, "end": v(-18.46, 15.32) * mm});
            skLineSegment(sketch, "E642", {"start": v(-18.46, 15.32) * mm, "end": v(-18.14, 15.8) * mm});
            skLineSegment(sketch, "E643", {"start": v(-18.14, 15.8) * mm, "end": v(-17.66, 16.03) * mm});
            skLineSegment(sketch, "E644", {"start": v(-17.66, 16.03) * mm, "end": v(-17.19, 16.07) * mm});
            skLineSegment(sketch, "E645", {"start": v(-17.19, 16.07) * mm, "end": v(-16.89, 15.93) * mm});
            skLineSegment(sketch, "E646", {"start": v(-16.89, 15.93) * mm, "end": v(-16.78, 15.6) * mm});
            skLineSegment(sketch, "E647", {"start": v(-16.78, 15.6) * mm, "end": v(-16.8, 15.2) * mm});
            skLineSegment(sketch, "E648", {"start": v(-16.8, 15.2) * mm, "end": v(-16.88, 14.8) * mm});
            skLineSegment(sketch, "E649", {"start": v(-16.88, 14.8) * mm, "end": v(-16.89, 14.48) * mm});
            skLineSegment(sketch, "E650", {"start": v(-16.89, 14.48) * mm, "end": v(-16.73, 14.19) * mm});
            skLineSegment(sketch, "E651", {"start": v(-16.73, 14.19) * mm, "end": v(-16.47, 13.95) * mm});
            skLineSegment(sketch, "E652", {"start": v(-16.47, 13.95) * mm, "end": v(-16.32, 13.7) * mm});
            skLineSegment(sketch, "E653", {"start": v(-16.32, 13.7) * mm, "end": v(-16.17, 13.46) * mm});
            skLineSegment(sketch, "E654", {"start": v(-16.17, 13.46) * mm, "end": v(-16.17, 13.63) * mm});
            skLineSegment(sketch, "E655", {"start": v(-16.17, 13.63) * mm, "end": v(-16.17, 13.8) * mm});
            skLineSegment(sketch, "E656", {"start": v(-16.17, 13.8) * mm, "end": v(-16.13, 13.7) * mm});
            skLineSegment(sketch, "E657", {"start": v(-16.13, 13.7) * mm, "end": v(-16.04, 13.46) * mm});
            skLineSegment(sketch, "E658", {"start": v(-16.04, 13.46) * mm, "end": v(-15.94, 13.23) * mm});
            skLineSegment(sketch, "E659", {"start": v(-15.94, 13.23) * mm, "end": v(-15.9, 13.12) * mm});
            skLineSegment(sketch, "E660", {"start": v(-15.9, 13.12) * mm, "end": v(-15.14, 11.43) * mm});
            skLineSegment(sketch, "E661", {"start": v(-15.14, 11.43) * mm, "end": v(-14.95, 9.67) * mm});
            skLineSegment(sketch, "E662", {"start": v(-14.95, 9.67) * mm, "end": v(-15.37, 7.96) * mm});
            skLineSegment(sketch, "E663", {"start": v(-15.37, 7.96) * mm, "end": v(-15.77, 7.3) * mm});
            skLineSegment(sketch, "E664", {"start": v(-15.77, 7.3) * mm, "end": v(-16.23, 6.69) * mm});
            skLineSegment(sketch, "E665", {"start": v(-16.23, 6.69) * mm, "end": v(-16.79, 6) * mm});
            skLineSegment(sketch, "E666", {"start": v(-16.79, 6) * mm, "end": v(-17.44, 5.42) * mm});
            skLineSegment(sketch, "E667", {"start": v(-17.44, 5.42) * mm, "end": v(-17.53, 5.63) * mm});
            skLineSegment(sketch, "E668", {"start": v(-17.53, 5.63) * mm, "end": v(-17.61, 5.84) * mm});
            skLineSegment(sketch, "E669", {"start": v(-17.61, 5.84) * mm, "end": v(-17.49, 6.05) * mm});
            skLineSegment(sketch, "E670", {"start": v(-17.49, 6.05) * mm, "end": v(-17.36, 6.27) * mm});
            skLineSegment(sketch, "E671", {"start": v(-17.36, 6.27) * mm, "end": v(-17.61, 6.22) * mm});
            skLineSegment(sketch, "E672", {"start": v(-17.61, 6.22) * mm, "end": v(-17.87, 6.18) * mm});
            skLineSegment(sketch, "E673", {"start": v(-17.87, 6.18) * mm, "end": v(-17.9, 6.02) * mm});
            skLineSegment(sketch, "E674", {"start": v(-17.9, 6.02) * mm, "end": v(-18, 5.59) * mm});
            skLineSegment(sketch, "E675", {"start": v(-18, 5.59) * mm, "end": v(-18.12, 4.98) * mm});
            skLineSegment(sketch, "E676", {"start": v(-18.12, 4.98) * mm, "end": v(-18.27, 4.28) * mm});
            skLineSegment(sketch, "E677", {"start": v(-18.27, 4.28) * mm, "end": v(-18.41, 3.58) * mm});
            skLineSegment(sketch, "E678", {"start": v(-18.41, 3.58) * mm, "end": v(-18.54, 2.97) * mm});
            skLineSegment(sketch, "E679", {"start": v(-18.54, 2.97) * mm, "end": v(-18.63, 2.53) * mm});
            skLineSegment(sketch, "E680", {"start": v(-18.63, 2.53) * mm, "end": v(-18.66, 2.37) * mm});
            skLineSegment(sketch, "E681", {"start": v(-18.66, 2.37) * mm, "end": v(-19.9, -0.68) * mm});
            skLineSegment(sketch, "E682", {"start": v(-19.9, -0.68) * mm, "end": v(-20.22, -1.33) * mm});
            skLineSegment(sketch, "E683", {"start": v(-20.22, -1.33) * mm, "end": v(-20.6, -2.08) * mm});
            skLineSegment(sketch, "E684", {"start": v(-20.6, -2.08) * mm, "end": v(-21.03, -2.8) * mm});
            skLineSegment(sketch, "E685", {"start": v(-21.03, -2.8) * mm, "end": v(-21.47, -3.36) * mm});
            skLineSegment(sketch, "E686", {"start": v(-21.47, -3.36) * mm, "end": v(-21.94, -3.77) * mm});
            skLineSegment(sketch, "E687", {"start": v(-21.94, -3.77) * mm, "end": v(-22.57, -4.22) * mm});
            skLineSegment(sketch, "E688", {"start": v(-22.57, -4.22) * mm, "end": v(-23.24, -4.65) * mm});
            skLineSegment(sketch, "E689", {"start": v(-23.24, -4.65) * mm, "end": v(-23.8, -5) * mm});
            skLineSegment(sketch, "E690", {"start": v(-23.8, -5) * mm, "end": v(-24.91, -5.66) * mm});
            skLineSegment(sketch, "E691", {"start": v(-24.91, -5.66) * mm, "end": v(-26.08, -6.23) * mm});
            skLineSegment(sketch, "E692", {"start": v(-26.08, -6.23) * mm, "end": v(-29.8, -7.27) * mm});
            skLineSegment(sketch, "E693", {"start": v(-29.8, -7.27) * mm, "end": v(-33.61, -7.91) * mm});
            skLineSegment(sketch, "E694", {"start": v(-33.61, -7.91) * mm, "end": v(-33.76, -7.95) * mm});
            skLineSegment(sketch, "E695", {"start": v(-33.76, -7.95) * mm, "end": v(-34.16, -8.05) * mm});
            skLineSegment(sketch, "E696", {"start": v(-34.16, -8.05) * mm, "end": v(-34.71, -8.2) * mm});
            skLineSegment(sketch, "E697", {"start": v(-34.71, -8.2) * mm, "end": v(-35.35, -8.37) * mm});
            skLineSegment(sketch, "E698", {"start": v(-35.35, -8.37) * mm, "end": v(-35.99, -8.54) * mm});
            skLineSegment(sketch, "E699", {"start": v(-35.99, -8.54) * mm, "end": v(-36.54, -8.69) * mm});
            skLineSegment(sketch, "E700", {"start": v(-36.54, -8.69) * mm, "end": v(-36.94, -8.8) * mm});
            skLineSegment(sketch, "E701", {"start": v(-36.94, -8.8) * mm, "end": v(-37.09, -8.83) * mm});
            skLineSegment(sketch, "E702", {"start": v(-37.09, -8.83) * mm, "end": v(-37.46, -8.88) * mm});
            skLineSegment(sketch, "E703", {"start": v(-37.46, -8.88) * mm, "end": v(-38.27, -9) * mm});
            skLineSegment(sketch, "E704", {"start": v(-38.27, -9) * mm, "end": v(-39.09, -9.11) * mm});
            skLineSegment(sketch, "E705", {"start": v(-39.09, -9.11) * mm, "end": v(-39.46, -9.17) * mm});
            skLineSegment(sketch, "E706", {"start": v(-39.46, -9.17) * mm, "end": v(-39.72, -9.21) * mm});
            skLineSegment(sketch, "E707", {"start": v(-39.72, -9.21) * mm, "end": v(-40.3, -9.31) * mm});
            skLineSegment(sketch, "E708", {"start": v(-40.3, -9.31) * mm, "end": v(-40.88, -9.41) * mm});
            skLineSegment(sketch, "E709", {"start": v(-40.88, -9.41) * mm, "end": v(-41.15, -9.46) * mm});
            skLineSegment(sketch, "E710", {"start": v(-41.15, -9.46) * mm, "end": v(-41.3, -9.47) * mm});
            skLineSegment(sketch, "E711", {"start": v(-41.3, -9.47) * mm, "end": v(-41.66, -9.51) * mm});
            skLineSegment(sketch, "E712", {"start": v(-41.66, -9.51) * mm, "end": v(-42, -9.55) * mm});
            skLineSegment(sketch, "E713", {"start": v(-42, -9.55) * mm, "end": v(-42.16, -9.57) * mm});
            skLineSegment(sketch, "E714", {"start": v(-42.16, -9.57) * mm, "end": v(-42.25, -9.48) * mm});
            skLineSegment(sketch, "E715", {"start": v(-42.25, -9.48) * mm, "end": v(-42.33, -9.4) * mm});
            skLineSegment(sketch, "E716", {"start": v(-42.33, -9.4) * mm, "end": v(-42.3, -9.52) * mm});
            skLineSegment(sketch, "E717", {"start": v(-42.3, -9.52) * mm, "end": v(-42.25, -9.65) * mm});
            skLineSegment(sketch, "E718", {"start": v(-42.25, -9.65) * mm, "end": v(-42.42, -9.65) * mm});
            skLineSegment(sketch, "E719", {"start": v(-42.42, -9.65) * mm, "end": v(-42.33, -10.24) * mm});
            skLineSegment(sketch, "E720", {"start": v(-42.33, -10.24) * mm, "end": v(-42.53, -10.75) * mm});
            skLineSegment(sketch, "E721", {"start": v(-42.53, -10.75) * mm, "end": v(-42.89, -10.83) * mm});
            skLineSegment(sketch, "E722", {"start": v(-42.89, -10.83) * mm, "end": v(-43.27, -10.84) * mm});
            skLineSegment(sketch, "E723", {"start": v(-43.27, -10.84) * mm, "end": v(-43.15, -11.45) * mm});
            skLineSegment(sketch, "E724", {"start": v(-43.15, -11.45) * mm, "end": v(-43.12, -12.01) * mm});
            skLineSegment(sketch, "E725", {"start": v(-43.12, -12.01) * mm, "end": v(-43.7, -12.42) * mm});
            skLineSegment(sketch, "E726", {"start": v(-43.7, -12.42) * mm, "end": v(-44.45, -12.63) * mm});
            skLineSegment(sketch, "E727", {"start": v(-44.45, -12.63) * mm, "end": v(-44.74, -12.69) * mm});
            skLineSegment(sketch, "E728", {"start": v(-44.74, -12.69) * mm, "end": v(-45.38, -12.83) * mm});
            skLineSegment(sketch, "E729", {"start": v(-45.38, -12.83) * mm, "end": v(-46.02, -12.97) * mm});
            skLineSegment(sketch, "E730", {"start": v(-46.02, -12.97) * mm, "end": v(-46.31, -13.03) * mm});
            skLineSegment(sketch, "E731", {"start": v(-46.31, -13.03) * mm, "end": v(-47.45, -13.1) * mm});
            skLineSegment(sketch, "E732", {"start": v(-47.45, -13.1) * mm, "end": v(-48.51, -13.3) * mm});
            skLineSegment(sketch, "E733", {"start": v(-48.51, -13.3) * mm, "end": v(-47.63, -13.45) * mm});
            skLineSegment(sketch, "E734", {"start": v(-47.63, -13.45) * mm, "end": v(-46.74, -13.53) * mm});
            skLineSegment(sketch, "E735", {"start": v(-46.74, -13.53) * mm, "end": v(-46.36, -13.47) * mm});
            skLineSegment(sketch, "E736", {"start": v(-46.36, -13.47) * mm, "end": v(-45.97, -13.4) * mm});
            skLineSegment(sketch, "E737", {"start": v(-45.97, -13.4) * mm, "end": v(-45.6, -13.38) * mm});
            skLineSegment(sketch, "E738", {"start": v(-45.6, -13.38) * mm, "end": v(-45.21, -13.35) * mm});
            skLineSegment(sketch, "E739", {"start": v(-45.21, -13.35) * mm, "end": v(-44.52, -13.24) * mm});
            skLineSegment(sketch, "E740", {"start": v(-44.52, -13.24) * mm, "end": v(-43.67, -13.08) * mm});
            skLineSegment(sketch, "E741", {"start": v(-43.67, -13.08) * mm, "end": v(-42.83, -12.88) * mm});
            skLineSegment(sketch, "E742", {"start": v(-42.83, -12.88) * mm, "end": v(-42.16, -12.68) * mm});
            skLineSegment(sketch, "E743", {"start": v(-42.16, -12.68) * mm, "end": v(-41.72, -12.51) * mm});
            skLineSegment(sketch, "E744", {"start": v(-41.72, -12.51) * mm, "end": v(-41.16, -12.27) * mm});
            skLineSegment(sketch, "E745", {"start": v(-41.16, -12.27) * mm, "end": v(-40.67, -11.96) * mm});
            skLineSegment(sketch, "E746", {"start": v(-40.67, -11.96) * mm, "end": v(-40.42, -11.6) * mm});
            skLineSegment(sketch, "E747", {"start": v(-40.42, -11.6) * mm, "end": v(-40.56, -11.1) * mm});
            skLineSegment(sketch, "E748", {"start": v(-40.56, -11.1) * mm, "end": v(-39.94, -10.43) * mm});
            skLineSegment(sketch, "E749", {"start": v(-39.94, -10.43) * mm, "end": v(-39.2, -10.01) * mm});
            skLineSegment(sketch, "E750", {"start": v(-39.2, -10.01) * mm, "end": v(-38.69, -10.17) * mm});
            skLineSegment(sketch, "E751", {"start": v(-38.69, -10.17) * mm, "end": v(-38.23, -10.57) * mm});
            skLineSegment(sketch, "E752", {"start": v(-38.23, -10.57) * mm, "end": v(-37.9, -11.09) * mm});
            skLineSegment(sketch, "E753", {"start": v(-37.9, -11.09) * mm, "end": v(-37.71, -11.6) * mm});
            skLineSegment(sketch, "E754", {"start": v(-37.71, -11.6) * mm, "end": v(-37.74, -12.24) * mm});
            skLineSegment(sketch, "E755", {"start": v(-37.74, -12.24) * mm, "end": v(-37.89, -12.87) * mm});
            skLineSegment(sketch, "E756", {"start": v(-37.89, -12.87) * mm, "end": v(-38.33, -13.36) * mm});
            skLineSegment(sketch, "E757", {"start": v(-38.33, -13.36) * mm, "end": v(-38.86, -13.79) * mm});
            skLineSegment(sketch, "E758", {"start": v(-38.86, -13.79) * mm, "end": v(-39.54, -14.26) * mm});
            skLineSegment(sketch, "E759", {"start": v(-39.54, -14.26) * mm, "end": v(-40.1, -14.6) * mm});
            skLineSegment(sketch, "E760", {"start": v(-40.1, -14.6) * mm, "end": v(-40.7, -14.9) * mm});
            skLineSegment(sketch, "E761", {"start": v(-40.7, -14.9) * mm, "end": v(-41.4, -15.26) * mm});
            skLineSegment(sketch, "E762", {"start": v(-41.4, -15.26) * mm, "end": v(-42.2, -15.66) * mm});
            skLineSegment(sketch, "E763", {"start": v(-42.2, -15.66) * mm, "end": v(-43.2, -16.15) * mm});
            skLineSegment(sketch, "E764", {"start": v(-43.2, -16.15) * mm, "end": v(-44.19, -16.6) * mm});
            skLineSegment(sketch, "E765", {"start": v(-44.19, -16.6) * mm, "end": v(-44.96, -16.9) * mm});
            skLineSegment(sketch, "E766", {"start": v(-44.96, -16.9) * mm, "end": v(-47.14, -17.23) * mm});
            skLineSegment(sketch, "E767", {"start": v(-47.14, -17.23) * mm, "end": v(-49.36, -17.27) * mm});
            skLineSegment(sketch, "E768", {"start": v(-49.36, -17.27) * mm, "end": v(-51.06, -17) * mm});
            skLineSegment(sketch, "E769", {"start": v(-51.06, -17) * mm, "end": v(-52.58, -16.17) * mm});
            skLineSegment(sketch, "E770", {"start": v(-52.58, -16.17) * mm, "end": v(-53.2, -17.4) * mm});
            skLineSegment(sketch, "E771", {"start": v(-53.2, -17.4) * mm, "end": v(-53.99, -18.54) * mm});
            skLineSegment(sketch, "E772", {"start": v(-53.99, -18.54) * mm, "end": v(-54.96, -19.5) * mm});
            skLineSegment(sketch, "E773", {"start": v(-54.96, -19.5) * mm, "end": v(-56.14, -20.2) * mm});
            skLineSegment(sketch, "E774", {"start": v(-56.14, -20.2) * mm, "end": v(-57.52, -20.66) * mm});
            skLineSegment(sketch, "E775", {"start": v(-57.52, -20.66) * mm, "end": v(-58.78, -20.94) * mm});
            skLineSegment(sketch, "E776", {"start": v(-58.78, -20.94) * mm, "end": v(-60.03, -21.27) * mm});
            skLineSegment(sketch, "E777", {"start": v(-60.03, -21.27) * mm, "end": v(-61.38, -21.9) * mm});
            skLineSegment(sketch, "E778", {"start": v(-61.38, -21.9) * mm, "end": v(-62.04, -22.2) * mm});
            skLineSegment(sketch, "E779", {"start": v(-62.04, -22.2) * mm, "end": v(-62.58, -22.52) * mm});
            skLineSegment(sketch, "E780", {"start": v(-62.58, -22.52) * mm, "end": v(-62.71, -23.03) * mm});
            skLineSegment(sketch, "E781", {"start": v(-62.71, -23.03) * mm, "end": v(-62.8, -23.28) * mm});
            skLineSegment(sketch, "E782", {"start": v(-62.8, -23.28) * mm, "end": v(-62.87, -23.54) * mm});
            skLineSegment(sketch, "E783", {"start": v(-62.87, -23.54) * mm, "end": v(-62.9, -23.72) * mm});
            skLineSegment(sketch, "E784", {"start": v(-62.9, -23.72) * mm, "end": v(-62.93, -24.13) * mm});
            skLineSegment(sketch, "E785", {"start": v(-62.93, -24.13) * mm, "end": v(-62.97, -24.54) * mm});
            skLineSegment(sketch, "E786", {"start": v(-62.97, -24.54) * mm, "end": v(-62.99, -24.72) * mm});
            skLineSegment(sketch, "E787", {"start": v(-62.99, -24.72) * mm, "end": v(-62.97, -24.9) * mm});
            skLineSegment(sketch, "E788", {"start": v(-62.97, -24.9) * mm, "end": v(-62.95, -25.32) * mm});
            skLineSegment(sketch, "E789", {"start": v(-62.95, -25.32) * mm, "end": v(-62.92, -25.72) * mm});
            skLineSegment(sketch, "E790", {"start": v(-62.92, -25.72) * mm, "end": v(-62.9, -25.9) * mm});
            skLineSegment(sketch, "E791", {"start": v(-62.9, -25.9) * mm, "end": v(-62.87, -26.82) * mm});
            skLineSegment(sketch, "E792", {"start": v(-62.87, -26.82) * mm, "end": v(-62.77, -27.6) * mm});
            skLineSegment(sketch, "E793", {"start": v(-62.77, -27.6) * mm, "end": v(-62.6, -28.35) * mm});
            skLineSegment(sketch, "E794", {"start": v(-62.6, -28.35) * mm, "end": v(-62.33, -29.2) * mm});
            skLineSegment(sketch, "E795", {"start": v(-62.33, -29.2) * mm, "end": v(-62.12, -29.95) * mm});
            skLineSegment(sketch, "E796", {"start": v(-62.12, -29.95) * mm, "end": v(-61.85, -30.65) * mm});
            skLineSegment(sketch, "E797", {"start": v(-61.85, -30.65) * mm, "end": v(-61.41, -31.39) * mm});
            skLineSegment(sketch, "E798", {"start": v(-61.41, -31.39) * mm, "end": v(-60.92, -32.09) * mm});
            skLineSegment(sketch, "E799", {"start": v(-60.92, -32.09) * mm, "end": v(-60.56, -32.5) * mm});
            skLineSegment(sketch, "E800", {"start": v(-60.56, -32.5) * mm, "end": v(-60.29, -32.8) * mm});
            skLineSegment(sketch, "E801", {"start": v(-60.29, -32.8) * mm, "end": v(-60.05, -33.14) * mm});
            skLineSegment(sketch, "E802", {"start": v(-60.05, -33.14) * mm, "end": v(-59.79, -33.7) * mm});
            skLineSegment(sketch, "E803", {"start": v(-59.79, -33.7) * mm, "end": v(-59.79, -34.8) * mm});
            skLineSegment(sketch, "E804", {"start": v(-59.79, -34.8) * mm, "end": v(-59.95, -35.22) * mm});
            skLineSegment(sketch, "E805", {"start": v(-59.95, -35.22) * mm, "end": v(-59.95, -35.64) * mm});
            skLineSegment(sketch, "E806", {"start": v(-59.95, -35.64) * mm, "end": v(-60.38, -36.82) * mm});
            skLineSegment(sketch, "E807", {"start": v(-60.38, -36.82) * mm, "end": v(-60.74, -37.52) * mm});
            skLineSegment(sketch, "E808", {"start": v(-60.74, -37.52) * mm, "end": v(-61.16, -38.16) * mm});
            skLineSegment(sketch, "E809", {"start": v(-61.16, -38.16) * mm, "end": v(-61.77, -39.12) * mm});
            skLineSegment(sketch, "E810", {"start": v(-61.77, -39.12) * mm, "end": v(-61.83, -39.23) * mm});
            skLineSegment(sketch, "E811", {"start": v(-61.83, -39.23) * mm, "end": v(-61.96, -39.5) * mm});
            skLineSegment(sketch, "E812", {"start": v(-61.96, -39.5) * mm, "end": v(-62.09, -39.76) * mm});
            skLineSegment(sketch, "E813", {"start": v(-62.09, -39.76) * mm, "end": v(-62.14, -39.88) * mm});
            skLineSegment(sketch, "E814", {"start": v(-62.14, -39.88) * mm, "end": v(-62.22, -40) * mm});
            skLineSegment(sketch, "E815", {"start": v(-62.22, -40) * mm, "end": v(-62.4, -40.3) * mm});
            skLineSegment(sketch, "E816", {"start": v(-62.4, -40.3) * mm, "end": v(-62.58, -40.6) * mm});
            skLineSegment(sketch, "E817", {"start": v(-62.58, -40.6) * mm, "end": v(-62.65, -40.72) * mm});
            skLineSegment(sketch, "E818", {"start": v(-62.65, -40.72) * mm, "end": v(-61.53, -41.15) * mm});
            skLineSegment(sketch, "E819", {"start": v(-61.53, -41.15) * mm, "end": v(-60.26, -41.87) * mm});
            skLineSegment(sketch, "E820", {"start": v(-60.26, -41.87) * mm, "end": v(-58.97, -42.66) * mm});
            skLineSegment(sketch, "E821", {"start": v(-58.97, -42.66) * mm, "end": v(-57.83, -43.32) * mm});
            skLineSegment(sketch, "E822", {"start": v(-57.83, -43.32) * mm, "end": v(-57.53, -43.46) * mm});
            skLineSegment(sketch, "E823", {"start": v(-57.53, -43.46) * mm, "end": v(-56.86, -43.78) * mm});
            skLineSegment(sketch, "E824", {"start": v(-56.86, -43.78) * mm, "end": v(-56.19, -44.1) * mm});
            skLineSegment(sketch, "E825", {"start": v(-56.19, -44.1) * mm, "end": v(-55.88, -44.24) * mm});
            skLineSegment(sketch, "E826", {"start": v(-55.88, -44.24) * mm, "end": v(-55.62, -44.33) * mm});
            skLineSegment(sketch, "E827", {"start": v(-55.62, -44.33) * mm, "end": v(-55.04, -44.53) * mm});
            skLineSegment(sketch, "E828", {"start": v(-55.04, -44.53) * mm, "end": v(-54.45, -44.73) * mm});
            skLineSegment(sketch, "E829", {"start": v(-54.45, -44.73) * mm, "end": v(-54.19, -44.83) * mm});
            skLineSegment(sketch, "E830", {"start": v(-54.19, -44.83) * mm, "end": v(-53.9, -44.94) * mm});
            skLineSegment(sketch, "E831", {"start": v(-53.9, -44.94) * mm, "end": v(-53.26, -45.2) * mm});
            skLineSegment(sketch, "E832", {"start": v(-53.26, -45.2) * mm, "end": v(-52.62, -45.46) * mm});
            skLineSegment(sketch, "E833", {"start": v(-52.62, -45.46) * mm, "end": v(-52.32, -45.58) * mm});
            skLineSegment(sketch, "E834", {"start": v(-52.32, -45.58) * mm, "end": v(-49.31, -46.38) * mm});
            skLineSegment(sketch, "E835", {"start": v(-49.31, -46.38) * mm, "end": v(-46.23, -46.74) * mm});
            skLineSegment(sketch, "E836", {"start": v(-46.23, -46.74) * mm, "end": v(-46.04, -46.74) * mm});
            skLineSegment(sketch, "E837", {"start": v(-46.04, -46.74) * mm, "end": v(-45.64, -46.74) * mm});
            skLineSegment(sketch, "E838", {"start": v(-45.64, -46.74) * mm, "end": v(-45.23, -46.74) * mm});
            skLineSegment(sketch, "E839", {"start": v(-45.23, -46.74) * mm, "end": v(-45.04, -46.74) * mm});
            skLineSegment(sketch, "E840", {"start": v(-45.04, -46.74) * mm, "end": v(-44.85, -46.72) * mm});
            skLineSegment(sketch, "E841", {"start": v(-44.85, -46.72) * mm, "end": v(-44.4, -46.7) * mm});
            skLineSegment(sketch, "E842", {"start": v(-44.4, -46.7) * mm, "end": v(-43.97, -46.66) * mm});
            skLineSegment(sketch, "E843", {"start": v(-43.97, -46.66) * mm, "end": v(-43.77, -46.65) * mm});
            skLineSegment(sketch, "E844", {"start": v(-43.77, -46.65) * mm, "end": v(-42.97, -46.63) * mm});
            skLineSegment(sketch, "E845", {"start": v(-42.97, -46.63) * mm, "end": v(-42.16, -46.53) * mm});
            skLineSegment(sketch, "E846", {"start": v(-42.16, -46.53) * mm, "end": v(-39.13, -45.71) * mm});
            skLineSegment(sketch, "E847", {"start": v(-39.13, -45.71) * mm, "end": v(-36.15, -44.6) * mm});
            skLineSegment(sketch, "E848", {"start": v(-36.15, -44.6) * mm, "end": v(-35.92, -44.48) * mm});
            skLineSegment(sketch, "E849", {"start": v(-35.92, -44.48) * mm, "end": v(-35.4, -44.22) * mm});
            skLineSegment(sketch, "E850", {"start": v(-35.4, -44.22) * mm, "end": v(-34.87, -43.96) * mm});
            skLineSegment(sketch, "E851", {"start": v(-34.87, -43.96) * mm, "end": v(-34.63, -43.84) * mm});
            skLineSegment(sketch, "E852", {"start": v(-34.63, -43.84) * mm, "end": v(-34.51, -43.8) * mm});
            skLineSegment(sketch, "E853", {"start": v(-34.51, -43.8) * mm, "end": v(-34.2, -43.66) * mm});
            skLineSegment(sketch, "E854", {"start": v(-34.2, -43.66) * mm, "end": v(-33.77, -43.47) * mm});
            skLineSegment(sketch, "E855", {"start": v(-33.77, -43.47) * mm, "end": v(-33.27, -43.26) * mm});
            skLineSegment(sketch, "E856", {"start": v(-33.27, -43.26) * mm, "end": v(-32.78, -43.04) * mm});
            skLineSegment(sketch, "E857", {"start": v(-32.78, -43.04) * mm, "end": v(-32.34, -42.85) * mm});
            skLineSegment(sketch, "E858", {"start": v(-32.34, -42.85) * mm, "end": v(-32.04, -42.72) * mm});
            skLineSegment(sketch, "E859", {"start": v(-32.04, -42.72) * mm, "end": v(-31.92, -42.67) * mm});
            skLineSegment(sketch, "E860", {"start": v(-31.92, -42.67) * mm, "end": v(-31.85, -43.05) * mm});
            skLineSegment(sketch, "E861", {"start": v(-31.85, -43.05) * mm, "end": v(-31.82, -43.57) * mm});
            skLineSegment(sketch, "E862", {"start": v(-31.82, -43.57) * mm, "end": v(-31.85, -44.07) * mm});
            skLineSegment(sketch, "E863", {"start": v(-31.85, -44.07) * mm, "end": v(-31.97, -44.42) * mm});
            skLineSegment(sketch, "E864", {"start": v(-31.97, -44.42) * mm, "end": v(-32.36, -44.68) * mm});
            skLineSegment(sketch, "E865", {"start": v(-32.36, -44.68) * mm, "end": v(-33.02, -45) * mm});
            skLineSegment(sketch, "E866", {"start": v(-33.02, -45) * mm, "end": v(-33.7, -45.3) * mm});
            skLineSegment(sketch, "E867", {"start": v(-33.7, -45.3) * mm, "end": v(-34.2, -45.5) * mm});
            skLineSegment(sketch, "E868", {"start": v(-34.2, -45.5) * mm, "end": v(-34.46, -45.62) * mm});
            skLineSegment(sketch, "E869", {"start": v(-34.46, -45.62) * mm, "end": v(-35.01, -45.9) * mm});
            skLineSegment(sketch, "E870", {"start": v(-35.01, -45.9) * mm, "end": v(-35.56, -46.16) * mm});
            skLineSegment(sketch, "E871", {"start": v(-35.56, -46.16) * mm, "end": v(-35.81, -46.29) * mm});
            skLineSegment(sketch, "E872", {"start": v(-35.81, -46.29) * mm, "end": v(-36.56, -46.6) * mm});
            skLineSegment(sketch, "E873", {"start": v(-36.56, -46.6) * mm, "end": v(-37.5, -46.95) * mm});
            skLineSegment(sketch, "E874", {"start": v(-37.5, -46.95) * mm, "end": v(-38.43, -47.27) * mm});
            skLineSegment(sketch, "E875", {"start": v(-38.43, -47.27) * mm, "end": v(-39.2, -47.5) * mm});
            skLineSegment(sketch, "E876", {"start": v(-39.2, -47.5) * mm, "end": v(-39.56, -47.6) * mm});
            skLineSegment(sketch, "E877", {"start": v(-39.56, -47.6) * mm, "end": v(-40.35, -47.83) * mm});
            skLineSegment(sketch, "E878", {"start": v(-40.35, -47.83) * mm, "end": v(-41.13, -48.05) * mm});
            skLineSegment(sketch, "E879", {"start": v(-41.13, -48.05) * mm, "end": v(-41.49, -48.15) * mm});
            skLineSegment(sketch, "E880", {"start": v(-41.49, -48.15) * mm, "end": v(-42.13, -48.25) * mm});
            skLineSegment(sketch, "E881", {"start": v(-42.13, -48.25) * mm, "end": v(-42.92, -48.34) * mm});
            skLineSegment(sketch, "E882", {"start": v(-42.92, -48.34) * mm, "end": v(-43.72, -48.4) * mm});
            skLineSegment(sketch, "E883", {"start": v(-43.72, -48.4) * mm, "end": v(-44.37, -48.43) * mm});
            skLineSegment(sketch, "E884", {"start": v(-44.37, -48.43) * mm, "end": v(-44.7, -48.44) * mm});
            skLineSegment(sketch, "E885", {"start": v(-44.7, -48.44) * mm, "end": v(-45.43, -48.47) * mm});
            skLineSegment(sketch, "E886", {"start": v(-45.43, -48.47) * mm, "end": v(-46.15, -48.5) * mm});
            skLineSegment(sketch, "E887", {"start": v(-46.15, -48.5) * mm, "end": v(-46.48, -48.51) * mm});
            skLineSegment(sketch, "E888", {"start": v(-46.48, -48.51) * mm, "end": v(-46.64, -48.5) * mm});
            skLineSegment(sketch, "E889", {"start": v(-46.64, -48.5) * mm, "end": v(-47, -48.47) * mm});
            skLineSegment(sketch, "E890", {"start": v(-47, -48.47) * mm, "end": v(-47.34, -48.45) * mm});
            skLineSegment(sketch, "E891", {"start": v(-47.34, -48.45) * mm, "end": v(-47.5, -48.44) * mm});
            skLineSegment(sketch, "E892", {"start": v(-47.5, -48.44) * mm, "end": v(-50.87, -47.87) * mm});
            skLineSegment(sketch, "E893", {"start": v(-50.87, -47.87) * mm, "end": v(-54.1, -46.8) * mm});
            skLineSegment(sketch, "E894", {"start": v(-54.1, -46.8) * mm, "end": v(-54.35, -46.72) * mm});
            skLineSegment(sketch, "E895", {"start": v(-54.35, -46.72) * mm, "end": v(-54.9, -46.55) * mm});
            skLineSegment(sketch, "E896", {"start": v(-54.9, -46.55) * mm, "end": v(-55.46, -46.38) * mm});
            skLineSegment(sketch, "E897", {"start": v(-55.46, -46.38) * mm, "end": v(-55.71, -46.3) * mm});
            skLineSegment(sketch, "E898", {"start": v(-55.71, -46.3) * mm, "end": v(-55.88, -46.23) * mm});
            skLineSegment(sketch, "E899", {"start": v(-55.88, -46.23) * mm, "end": v(-56.26, -46.07) * mm});
            skLineSegment(sketch, "E900", {"start": v(-56.26, -46.07) * mm, "end": v(-56.64, -45.91) * mm});
            skLineSegment(sketch, "E901", {"start": v(-56.64, -45.91) * mm, "end": v(-56.81, -45.84) * mm});
            skLineSegment(sketch, "E902", {"start": v(-56.81, -45.84) * mm, "end": v(-57.13, -45.71) * mm});
            skLineSegment(sketch, "E903", {"start": v(-57.13, -45.71) * mm, "end": v(-57.83, -45.44) * mm});
            skLineSegment(sketch, "E904", {"start": v(-57.83, -45.44) * mm, "end": v(-58.53, -45.16) * mm});
            skLineSegment(sketch, "E905", {"start": v(-58.53, -45.16) * mm, "end": v(-58.84, -45.03) * mm});
            skLineSegment(sketch, "E906", {"start": v(-58.84, -45.03) * mm, "end": v(-60.92, -44.35) * mm});
            skLineSegment(sketch, "E907", {"start": v(-60.92, -44.35) * mm, "end": v(-63.08, -43.97) * mm});
            skLineSegment(sketch, "E908", {"start": v(-63.08, -43.97) * mm, "end": v(-63.49, -43.94) * mm});
            skLineSegment(sketch, "E909", {"start": v(-63.49, -43.94) * mm, "end": v(-64.02, -43.9) * mm});
            skLineSegment(sketch, "E910", {"start": v(-64.02, -43.9) * mm, "end": v(-64.53, -43.82) * mm});
            skLineSegment(sketch, "E911", {"start": v(-64.53, -43.82) * mm, "end": v(-64.85, -43.64) * mm});
            skLineSegment(sketch, "E912", {"start": v(-64.85, -43.64) * mm, "end": v(-64.94, -43.3) * mm});
            skLineSegment(sketch, "E913", {"start": v(-64.94, -43.3) * mm, "end": v(-64.94, -42.92) * mm});
            skLineSegment(sketch, "E914", {"start": v(-64.94, -42.92) * mm, "end": v(-64.94, -42.08) * mm});
            skLineSegment(sketch, "E915", {"start": v(-64.94, -42.08) * mm, "end": v(-64.67, -41.35) * mm});
            skLineSegment(sketch, "E916", {"start": v(-64.67, -41.35) * mm, "end": v(-64.35, -40.64) * mm});
            skLineSegment(sketch, "E917", {"start": v(-64.35, -40.64) * mm, "end": v(-64.93, -40.59) * mm});
            skLineSegment(sketch, "E918", {"start": v(-64.93, -40.59) * mm, "end": v(-65.34, -40.25) * mm});
            skLineSegment(sketch, "E919", {"start": v(-65.34, -40.25) * mm, "end": v(-65.62, -39.75) * mm});
            skLineSegment(sketch, "E920", {"start": v(-65.62, -39.75) * mm, "end": v(-65.81, -39.2) * mm});
            skLineSegment(sketch, "E921", {"start": v(-65.81, -39.2) * mm, "end": v(-65.94, -38.6) * mm});
            skLineSegment(sketch, "E922", {"start": v(-65.94, -38.6) * mm, "end": v(-65.96, -38.02) * mm});
            skLineSegment(sketch, "E923", {"start": v(-65.96, -38.02) * mm, "end": v(-65.92, -36.1) * mm});
            skLineSegment(sketch, "E924", {"start": v(-65.92, -36.1) * mm, "end": v(-65.34, -34.3) * mm});
            skLineSegment(sketch, "E925", {"start": v(-65.34, -34.3) * mm, "end": v(-64.95, -33.72) * mm});
            skLineSegment(sketch, "E926", {"start": v(-64.95, -33.72) * mm, "end": v(-64.43, -33.28) * mm});
            skLineSegment(sketch, "E927", {"start": v(-64.43, -33.28) * mm, "end": v(-63.95, -33.27) * mm});
            skLineSegment(sketch, "E928", {"start": v(-63.95, -33.27) * mm, "end": v(-63.76, -33.7) * mm});
            skLineSegment(sketch, "E929", {"start": v(-63.76, -33.7) * mm, "end": v(-63.58, -33.36) * mm});
            skLineSegment(sketch, "E930", {"start": v(-63.58, -33.36) * mm, "end": v(-63.62, -33.01) * mm});
            skLineSegment(sketch, "E931", {"start": v(-63.62, -33.01) * mm, "end": v(-63.78, -32.56) * mm});
            skLineSegment(sketch, "E932", {"start": v(-63.78, -32.56) * mm, "end": v(-63.98, -32.1) * mm});
            skLineSegment(sketch, "E933", {"start": v(-63.98, -32.1) * mm, "end": v(-64.14, -31.75) * mm});
            skLineSegment(sketch, "E934", {"start": v(-64.14, -31.75) * mm, "end": v(-64.5, -30.45) * mm});
            skLineSegment(sketch, "E935", {"start": v(-64.5, -30.45) * mm, "end": v(-64.6, -29.13) * mm});
            skLineSegment(sketch, "E936", {"start": v(-64.6, -29.13) * mm, "end": v(-64.65, -28.7) * mm});
            skLineSegment(sketch, "E937", {"start": v(-64.65, -28.7) * mm, "end": v(-64.69, -28.28) * mm});
            skLineSegment(sketch, "E938", {"start": v(-64.69, -28.28) * mm, "end": v(-64.72, -27.42) * mm});
            skLineSegment(sketch, "E939", {"start": v(-64.72, -27.42) * mm, "end": v(-64.74, -26.64) * mm});
            skLineSegment(sketch, "E940", {"start": v(-64.74, -26.64) * mm, "end": v(-64.7, -25.86) * mm});
            skLineSegment(sketch, "E941", {"start": v(-64.7, -25.86) * mm, "end": v(-64.55, -24.98) * mm});
            skLineSegment(sketch, "E942", {"start": v(-64.55, -24.98) * mm, "end": v(-63.55, -22.18) * mm});
            skLineSegment(sketch, "E943", {"start": v(-63.55, -22.18) * mm, "end": v(-63.5, -22.06) * mm});
            skLineSegment(sketch, "E944", {"start": v(-63.5, -22.06) * mm, "end": v(-63.38, -21.8) * mm});
            skLineSegment(sketch, "E945", {"start": v(-63.38, -21.8) * mm, "end": v(-63.26, -21.54) * mm});
            skLineSegment(sketch, "E946", {"start": v(-63.26, -21.54) * mm, "end": v(-63.2, -21.42) * mm});
            skLineSegment(sketch, "E947", {"start": v(-63.2, -21.42) * mm, "end": v(-63.19, -21.04) * mm});
            skLineSegment(sketch, "E948", {"start": v(-63.19, -21.04) * mm, "end": v(-63.22, -20.44) * mm});
            skLineSegment(sketch, "E949", {"start": v(-63.22, -20.44) * mm, "end": v(-63.28, -19.82) * mm});
            skLineSegment(sketch, "E950", {"start": v(-63.28, -19.82) * mm, "end": v(-63.32, -19.39) * mm});
            skLineSegment(sketch, "E951", {"start": v(-63.32, -19.39) * mm, "end": v(-63.27, -18.75) * mm});
            skLineSegment(sketch, "E952", {"start": v(-63.27, -18.75) * mm, "end": v(-63.13, -18.12) * mm});
            skLineSegment(sketch, "E953", {"start": v(-63.13, -18.12) * mm, "end": v(-62.6, -16.84) * mm});
            skLineSegment(sketch, "E954", {"start": v(-62.6, -16.84) * mm, "end": v(-61.86, -15.84) * mm});
            skLineSegment(sketch, "E955", {"start": v(-61.86, -15.84) * mm, "end": v(-60.93, -14.98) * mm});
            skLineSegment(sketch, "E956", {"start": v(-60.93, -14.98) * mm, "end": v(-59.86, -14.14) * mm});
            skLineSegment(sketch, "E957", {"start": v(-59.86, -14.14) * mm, "end": v(-61.8, -13.74) * mm});
            skLineSegment(sketch, "E958", {"start": v(-61.8, -13.74) * mm, "end": v(-63.67, -13.1) * mm});
            skLineSegment(sketch, "E959", {"start": v(-63.67, -13.1) * mm, "end": v(-64.85, -12.68) * mm});
            skLineSegment(sketch, "E960", {"start": v(-64.85, -12.68) * mm, "end": v(-65.73, -12.28) * mm});
            skLineSegment(sketch, "E961", {"start": v(-65.73, -12.28) * mm, "end": v(-66.56, -11.76) * mm});
            skLineSegment(sketch, "E962", {"start": v(-66.56, -11.76) * mm, "end": v(-67.56, -11) * mm});
            skLineSegment(sketch, "E963", {"start": v(-67.56, -11) * mm, "end": v(-67.85, -10.74) * mm});
            skLineSegment(sketch, "E964", {"start": v(-67.85, -10.74) * mm, "end": v(-68.2, -10.38) * mm});
            skLineSegment(sketch, "E965", {"start": v(-68.2, -10.38) * mm, "end": v(-68.44, -9.97) * mm});
            skLineSegment(sketch, "E966", {"start": v(-68.44, -9.97) * mm, "end": v(-68.4, -9.62) * mm});
            skLineSegment(sketch, "E967", {"start": v(-68.4, -9.62) * mm, "end": v(-68.14, -9.5) * mm});
            skLineSegment(sketch, "E968", {"start": v(-68.14, -9.5) * mm, "end": v(-67.82, -9.49) * mm});
            skLineSegment(sketch, "E969", {"start": v(-67.82, -9.49) * mm, "end": v(-67.06, -9.6) * mm});
            skLineSegment(sketch, "E970", {"start": v(-67.06, -9.6) * mm, "end": v(-66.21, -9.64) * mm});
            skLineSegment(sketch, "E971", {"start": v(-66.21, -9.64) * mm, "end": v(-65.55, -9.48) * mm});
            skLineSegment(sketch, "E972", {"start": v(-65.55, -9.48) * mm, "end": v(-64.8, -9.23) * mm});
            skLineSegment(sketch, "E973", {"start": v(-64.8, -9.23) * mm, "end": v(-64.06, -8.95) * mm});
            skLineSegment(sketch, "E974", {"start": v(-64.06, -8.95) * mm, "end": v(-63.42, -8.73) * mm});
            skLineSegment(sketch, "E975", {"start": v(-63.42, -8.73) * mm, "end": v(-61.87, -8.52) * mm});
            skLineSegment(sketch, "E976", {"start": v(-61.87, -8.52) * mm, "end": v(-60.28, -8.47) * mm});
            skLineSegment(sketch, "E977", {"start": v(-60.28, -8.47) * mm, "end": v(-58.13, -8.72) * mm});
            skLineSegment(sketch, "E978", {"start": v(-58.13, -8.72) * mm, "end": v(-56.05, -9.38) * mm});
            skLineSegment(sketch, "E979", {"start": v(-56.05, -9.38) * mm, "end": v(-55.6, -9.59) * mm});
            skLineSegment(sketch, "E980", {"start": v(-55.6, -9.59) * mm, "end": v(-55.16, -9.89) * mm});
            skLineSegment(sketch, "E981", {"start": v(-55.16, -9.89) * mm, "end": v(-54.97, -10.26) * mm});
            skLineSegment(sketch, "E982", {"start": v(-54.97, -10.26) * mm, "end": v(-55.29, -10.67) * mm});
            skLineSegment(sketch, "E983", {"start": v(-55.29, -10.67) * mm, "end": v(-55.2, -10.92) * mm});
            skLineSegment(sketch, "E984", {"start": v(-55.2, -10.92) * mm, "end": v(-55.12, -11.17) * mm});
            skLineSegment(sketch, "E985", {"start": v(-55.12, -11.17) * mm, "end": v(-55.42, -11.2) * mm});
            skLineSegment(sketch, "E986", {"start": v(-55.42, -11.2) * mm, "end": v(-55.71, -11.22) * mm});
            skLineSegment(sketch, "E987", {"start": v(-55.71, -11.22) * mm, "end": v(-56, -11.13) * mm});
            skLineSegment(sketch, "E988", {"start": v(-56, -11.13) * mm, "end": v(-56.64, -10.95) * mm});
            skLineSegment(sketch, "E989", {"start": v(-56.64, -10.95) * mm, "end": v(-57.28, -10.76) * mm});
            skLineSegment(sketch, "E990", {"start": v(-57.28, -10.76) * mm, "end": v(-57.57, -10.67) * mm});
            skLineSegment(sketch, "E991", {"start": v(-57.57, -10.67) * mm, "end": v(-57.91, -10.67) * mm});
            skLineSegment(sketch, "E992", {"start": v(-57.91, -10.67) * mm, "end": v(-58.25, -10.67) * mm});
            skLineSegment(sketch, "E993", {"start": v(-58.25, -10.67) * mm, "end": v(-58.46, -10.66) * mm});
            skLineSegment(sketch, "E994", {"start": v(-58.46, -10.66) * mm, "end": v(-58.93, -10.63) * mm});
            skLineSegment(sketch, "E995", {"start": v(-58.93, -10.63) * mm, "end": v(-59.4, -10.6) * mm});
            skLineSegment(sketch, "E996", {"start": v(-59.4, -10.6) * mm, "end": v(-59.6, -10.58) * mm});
            skLineSegment(sketch, "E997", {"start": v(-59.6, -10.58) * mm, "end": v(-59.92, -10.63) * mm});
            skLineSegment(sketch, "E998", {"start": v(-59.92, -10.63) * mm, "end": v(-60.62, -10.74) * mm});
            skLineSegment(sketch, "E999", {"start": v(-60.62, -10.74) * mm, "end": v(-61.32, -10.85) * mm});
            skLineSegment(sketch, "E1000", {"start": v(-61.32, -10.85) * mm, "end": v(-61.64, -10.9) * mm});
            skLineSegment(sketch, "E1001", {"start": v(-61.64, -10.9) * mm, "end": v(-61.92, -10.94) * mm});
            skLineSegment(sketch, "E1002", {"start": v(-61.92, -10.94) * mm, "end": v(-62.53, -11.04) * mm});
            skLineSegment(sketch, "E1003", {"start": v(-62.53, -11.04) * mm, "end": v(-63.14, -11.13) * mm});
            skLineSegment(sketch, "E1004", {"start": v(-63.14, -11.13) * mm, "end": v(-63.42, -11.17) * mm});
            skLineSegment(sketch, "E1005", {"start": v(-63.42, -11.17) * mm, "end": v(-62.97, -11.28) * mm});
            skLineSegment(sketch, "E1006", {"start": v(-62.97, -11.28) * mm, "end": v(-61.98, -11.5) * mm});
            skLineSegment(sketch, "E1007", {"start": v(-61.98, -11.5) * mm, "end": v(-60.99, -11.72) * mm});
            skLineSegment(sketch, "E1008", {"start": v(-60.99, -11.72) * mm, "end": v(-60.54, -11.82) * mm});
            skLineSegment(sketch, "E1009", {"start": v(-60.54, -11.82) * mm, "end": v(-60.31, -11.79) * mm});
            skLineSegment(sketch, "E1010", {"start": v(-60.31, -11.79) * mm, "end": v(-59.82, -11.71) * mm});
            skLineSegment(sketch, "E1011", {"start": v(-59.82, -11.71) * mm, "end": v(-59.32, -11.64) * mm});
            skLineSegment(sketch, "E1012", {"start": v(-59.32, -11.64) * mm, "end": v(-59.1, -11.6) * mm});
            skLineSegment(sketch, "E1013", {"start": v(-59.1, -11.6) * mm, "end": v(-58.95, -11.66) * mm});
            skLineSegment(sketch, "E1014", {"start": v(-58.95, -11.66) * mm, "end": v(-58.63, -11.77) * mm});
            skLineSegment(sketch, "E1015", {"start": v(-58.63, -11.77) * mm, "end": v(-58.31, -11.88) * mm});
            skLineSegment(sketch, "E1016", {"start": v(-58.31, -11.88) * mm, "end": v(-58.17, -11.93) * mm});
            skLineSegment(sketch, "E1017", {"start": v(-58.17, -11.93) * mm, "end": v(-57.87, -11.9) * mm});
            skLineSegment(sketch, "E1018", {"start": v(-57.87, -11.9) * mm, "end": v(-57.57, -11.85) * mm});
            skLineSegment(sketch, "E1019", {"start": v(-57.57, -11.85) * mm, "end": v(-57.62, -12.02) * mm});
            skLineSegment(sketch, "E1020", {"start": v(-57.62, -12.02) * mm, "end": v(-57.66, -12.2) * mm});
            skLineSegment(sketch, "E1021", {"start": v(-57.66, -12.2) * mm, "end": v(-57.45, -12.02) * mm});
            skLineSegment(sketch, "E1022", {"start": v(-57.45, -12.02) * mm, "end": v(-57.24, -11.85) * mm});
            skLineSegment(sketch, "E1023", {"start": v(-57.24, -11.85) * mm, "end": v(-57.15, -12.02) * mm});
            skLineSegment(sketch, "E1024", {"start": v(-57.15, -12.02) * mm, "end": v(-57.07, -12.2) * mm});
            skLineSegment(sketch, "E1025", {"start": v(-57.07, -12.2) * mm, "end": v(-56.8, -12.11) * mm});
            skLineSegment(sketch, "E1026", {"start": v(-56.8, -12.11) * mm, "end": v(-56.61, -12.18) * mm});
            skLineSegment(sketch, "E1027", {"start": v(-56.61, -12.18) * mm, "end": v(-56.53, -12.35) * mm});
            skLineSegment(sketch, "E1028", {"start": v(-56.53, -12.35) * mm, "end": v(-56.59, -12.62) * mm});
            skLineSegment(sketch, "E1029", {"start": v(-56.59, -12.62) * mm, "end": v(-56.91, -13.05) * mm});
            skLineSegment(sketch, "E1030", {"start": v(-56.91, -13.05) * mm, "end": v(-57.3, -13.46) * mm});
            skLineSegment(sketch, "E1031", {"start": v(-57.3, -13.46) * mm, "end": v(-57.69, -13.94) * mm});
            skLineSegment(sketch, "E1032", {"start": v(-57.69, -13.94) * mm, "end": v(-57.88, -14.2) * mm});
            skLineSegment(sketch, "E1033", {"start": v(-57.88, -14.2) * mm, "end": v(-58.13, -14.46) * mm});
            skLineSegment(sketch, "E1034", {"start": v(-58.13, -14.46) * mm, "end": v(-58.67, -14.98) * mm});
            skLineSegment(sketch, "E1035", {"start": v(-58.67, -14.98) * mm, "end": v(-59.37, -15.57) * mm});
            skLineSegment(sketch, "E1036", {"start": v(-59.37, -15.57) * mm, "end": v(-60, -16.17) * mm});
            skLineSegment(sketch, "E1037", {"start": v(-60, -16.17) * mm, "end": v(-60.31, -16.78) * mm});
            skLineSegment(sketch, "E1038", {"start": v(-60.31, -16.78) * mm, "end": v(-60.6, -17.64) * mm});
            skLineSegment(sketch, "E1039", {"start": v(-60.6, -17.64) * mm, "end": v(-60.8, -18.53) * mm});
            skLineSegment(sketch, "E1040", {"start": v(-60.8, -18.53) * mm, "end": v(-60.87, -19.22) * mm});
            skLineSegment(sketch, "E1041", {"start": v(-60.87, -19.22) * mm, "end": v(-60.83, -19.56) * mm});
            skLineSegment(sketch, "E1042", {"start": v(-60.83, -19.56) * mm, "end": v(-60.8, -19.9) * mm});
            skLineSegment(sketch, "E1043", {"start": v(-60.8, -19.9) * mm, "end": v(-60.27, -19.5) * mm});
            skLineSegment(sketch, "E1044", {"start": v(-60.27, -19.5) * mm, "end": v(-59.7, -19.22) * mm});
            skLineSegment(sketch, "E1045", {"start": v(-59.7, -19.22) * mm, "end": v(-59, -19.2) * mm});
            skLineSegment(sketch, "E1046", {"start": v(-59, -19.2) * mm, "end": v(-58.25, -19.22) * mm});
            skLineSegment(sketch, "E1047", {"start": v(-58.25, -19.22) * mm, "end": v(-57.53, -19.13) * mm});
            skLineSegment(sketch, "E1048", {"start": v(-57.53, -19.13) * mm, "end": v(-56.73, -18.9) * mm});
            skLineSegment(sketch, "E1049", {"start": v(-56.73, -18.9) * mm, "end": v(-55.98, -18.58) * mm});
            skLineSegment(sketch, "E1050", {"start": v(-55.98, -18.58) * mm, "end": v(-55.38, -18.18) * mm});
            skLineSegment(sketch, "E1051", {"start": v(-55.38, -18.18) * mm, "end": v(-54.88, -17.62) * mm});
            skLineSegment(sketch, "E1052", {"start": v(-54.88, -17.62) * mm, "end": v(-54.41, -17.02) * mm});
            skLineSegment(sketch, "E1053", {"start": v(-54.41, -17.02) * mm, "end": v(-54.19, -16.7) * mm});
            skLineSegment(sketch, "E1054", {"start": v(-54.19, -16.7) * mm, "end": v(-53.9, -16.28) * mm});
            skLineSegment(sketch, "E1055", {"start": v(-53.9, -16.28) * mm, "end": v(-53.65, -15.83) * mm});
            skLineSegment(sketch, "E1056", {"start": v(-53.65, -15.83) * mm, "end": v(-53.55, -15.5) * mm});
            skLineSegment(sketch, "E1057", {"start": v(-53.55, -15.5) * mm, "end": v(-53.75, -15.06) * mm});
            skLineSegment(sketch, "E1058", {"start": v(-53.75, -15.06) * mm, "end": v(-54.06, -14.65) * mm});
            skLineSegment(sketch, "E1059", {"start": v(-54.06, -14.65) * mm, "end": v(-55.22, -13.04) * mm});
            skLineSegment(sketch, "E1060", {"start": v(-55.22, -13.04) * mm, "end": v(-55.54, -12.69) * mm});
            skLineSegment(sketch, "E1061", {"start": v(-55.54, -12.69) * mm, "end": v(-55.8, -12.35) * mm});
            skLineSegment(sketch, "E1062", {"start": v(-55.8, -12.35) * mm, "end": v(-55.94, -11.98) * mm});
            skLineSegment(sketch, "E1063", {"start": v(-55.94, -11.98) * mm, "end": v(-55.88, -11.51) * mm});
            skLineSegment(sketch, "E1064", {"start": v(-55.88, -11.51) * mm, "end": v(-55.7, -11.6) * mm});
            skLineSegment(sketch, "E1065", {"start": v(-55.7, -11.6) * mm, "end": v(-55.31, -11.76) * mm});
            skLineSegment(sketch, "E1066", {"start": v(-55.31, -11.76) * mm, "end": v(-54.92, -11.93) * mm});
            skLineSegment(sketch, "E1067", {"start": v(-54.92, -11.93) * mm, "end": v(-54.75, -12) * mm});
            skLineSegment(sketch, "E1068", {"start": v(-54.75, -12) * mm, "end": v(-54.5, -12.14) * mm});
            skLineSegment(sketch, "E1069", {"start": v(-54.5, -12.14) * mm, "end": v(-54.24, -12.27) * mm});
            skLineSegment(sketch, "E1070", {"start": v(-54.24, -12.27) * mm, "end": v(-54.17, -12.4) * mm});
            skLineSegment(sketch, "E1071", {"start": v(-54.17, -12.4) * mm, "end": v(-54.1, -12.53) * mm});
            skLineSegment(sketch, "E1072", {"start": v(-54.1, -12.53) * mm, "end": v(-53.8, -12.59) * mm});
            skLineSegment(sketch, "E1073", {"start": v(-53.8, -12.59) * mm, "end": v(-53.68, -12.87) * mm});
            skLineSegment(sketch, "E1074", {"start": v(-53.68, -12.87) * mm, "end": v(-53.37, -13.04) * mm});
            skLineSegment(sketch, "E1075", {"start": v(-53.37, -13.04) * mm, "end": v(-53.05, -13.25) * mm});
            skLineSegment(sketch, "E1076", {"start": v(-53.05, -13.25) * mm, "end": v(-52.74, -13.32) * mm});
            skLineSegment(sketch, "E1077", {"start": v(-52.74, -13.32) * mm, "end": v(-52.42, -13.1) * mm});
            skLineSegment(sketch, "E1078", {"start": v(-52.42, -13.1) * mm, "end": v(-52.24, -12.78) * mm});
            skLineSegment(sketch, "E1079", {"start": v(-52.24, -12.78) * mm, "end": v(-53.25, -12.26) * mm});
            skLineSegment(sketch, "E1080", {"start": v(-53.25, -12.26) * mm, "end": v(-53.76, -11.26) * mm});
            skLineSegment(sketch, "E1081", {"start": v(-53.76, -11.26) * mm, "end": v(-53.52, -11.1) * mm});
            skLineSegment(sketch, "E1082", {"start": v(-53.52, -11.1) * mm, "end": v(-53.43, -10.84) * mm});
            skLineSegment(sketch, "E1083", {"start": v(-53.43, -10.84) * mm, "end": v(-53.22, -10.92) * mm});
            skLineSegment(sketch, "E1084", {"start": v(-53.22, -10.92) * mm, "end": v(-53, -11) * mm});
            skLineSegment(sketch, "E1085", {"start": v(-53, -11) * mm, "end": v(-53.22, -10.75) * mm});
            skLineSegment(sketch, "E1086", {"start": v(-53.22, -10.75) * mm, "end": v(-53.43, -10.5) * mm});
            skLineSegment(sketch, "E1087", {"start": v(-53.43, -10.5) * mm, "end": v(-53.09, -10.46) * mm});
            skLineSegment(sketch, "E1088", {"start": v(-53.09, -10.46) * mm, "end": v(-52.75, -10.41) * mm});
            skLineSegment(sketch, "E1089", {"start": v(-52.75, -10.41) * mm, "end": v(-53.39, -9.93) * mm});
            skLineSegment(sketch, "E1090", {"start": v(-53.39, -9.93) * mm, "end": v(-54.19, -9.68) * mm});
            skLineSegment(sketch, "E1091", {"start": v(-54.19, -9.68) * mm, "end": v(-54.36, -9.63) * mm});
            skLineSegment(sketch, "E1092", {"start": v(-54.36, -9.63) * mm, "end": v(-54.82, -9.5) * mm});
            skLineSegment(sketch, "E1093", {"start": v(-54.82, -9.5) * mm, "end": v(-55.48, -9.32) * mm});
            skLineSegment(sketch, "E1094", {"start": v(-55.48, -9.32) * mm, "end": v(-56.22, -9.1) * mm});
            skLineSegment(sketch, "E1095", {"start": v(-56.22, -9.1) * mm, "end": v(-56.97, -8.9) * mm});
            skLineSegment(sketch, "E1096", {"start": v(-56.97, -8.9) * mm, "end": v(-57.62, -8.72) * mm});
            skLineSegment(sketch, "E1097", {"start": v(-57.62, -8.72) * mm, "end": v(-58.08, -8.59) * mm});
            skLineSegment(sketch, "E1098", {"start": v(-58.08, -8.59) * mm, "end": v(-58.25, -8.54) * mm});
            skLineSegment(sketch, "E1099", {"start": v(-58.25, -8.54) * mm, "end": v(-58.61, -8.43) * mm});
            skLineSegment(sketch, "E1100", {"start": v(-58.61, -8.43) * mm, "end": v(-59.4, -8.2) * mm});
            skLineSegment(sketch, "E1101", {"start": v(-59.4, -8.2) * mm, "end": v(-60.18, -7.98) * mm});
            skLineSegment(sketch, "E1102", {"start": v(-60.18, -7.98) * mm, "end": v(-60.54, -7.87) * mm});
            skLineSegment(sketch, "E1103", {"start": v(-60.54, -7.87) * mm, "end": v(-60.76, -7.83) * mm});
            skLineSegment(sketch, "E1104", {"start": v(-60.76, -7.83) * mm, "end": v(-61.35, -7.7) * mm});
            skLineSegment(sketch, "E1105", {"start": v(-61.35, -7.7) * mm, "end": v(-62.17, -7.54) * mm});
            skLineSegment(sketch, "E1106", {"start": v(-62.17, -7.54) * mm, "end": v(-63.12, -7.35) * mm});
            skLineSegment(sketch, "E1107", {"start": v(-63.12, -7.35) * mm, "end": v(-64.07, -7.15) * mm});
            skLineSegment(sketch, "E1108", {"start": v(-64.07, -7.15) * mm, "end": v(-64.9, -6.99) * mm});
            skLineSegment(sketch, "E1109", {"start": v(-64.9, -6.99) * mm, "end": v(-65.48, -6.87) * mm});
            skLineSegment(sketch, "E1110", {"start": v(-65.48, -6.87) * mm, "end": v(-65.7, -6.82) * mm});
            skLineSegment(sketch, "E1111", {"start": v(-65.7, -6.82) * mm, "end": v(-66, -6.72) * mm});
            skLineSegment(sketch, "E1112", {"start": v(-66, -6.72) * mm, "end": v(-66.68, -6.5) * mm});
            skLineSegment(sketch, "E1113", {"start": v(-66.68, -6.5) * mm, "end": v(-67.35, -6.27) * mm});
            skLineSegment(sketch, "E1114", {"start": v(-67.35, -6.27) * mm, "end": v(-67.65, -6.16) * mm});
            skLineSegment(sketch, "E1115", {"start": v(-67.65, -6.16) * mm, "end": v(-67.78, -6.1) * mm});
            skLineSegment(sketch, "E1116", {"start": v(-67.78, -6.1) * mm, "end": v(-68.07, -5.98) * mm});
            skLineSegment(sketch, "E1117", {"start": v(-68.07, -5.98) * mm, "end": v(-68.37, -5.85) * mm});
            skLineSegment(sketch, "E1118", {"start": v(-68.37, -5.85) * mm, "end": v(-68.5, -5.8) * mm});
            skLineSegment(sketch, "E1119", {"start": v(-68.5, -5.8) * mm, "end": v(-68.68, -5.74) * mm});
            skLineSegment(sketch, "E1120", {"start": v(-68.68, -5.74) * mm, "end": v(-69.09, -5.62) * mm});
            skLineSegment(sketch, "E1121", {"start": v(-69.09, -5.62) * mm, "end": v(-69.5, -5.5) * mm});
            skLineSegment(sketch, "E1122", {"start": v(-69.5, -5.5) * mm, "end": v(-69.68, -5.45) * mm});
            skLineSegment(sketch, "E1123", {"start": v(-69.68, -5.45) * mm, "end": v(-69.8, -5.4) * mm});
            skLineSegment(sketch, "E1124", {"start": v(-69.8, -5.4) * mm, "end": v(-70.1, -5.28) * mm});
            skLineSegment(sketch, "E1125", {"start": v(-70.1, -5.28) * mm, "end": v(-70.54, -5.1) * mm});
            skLineSegment(sketch, "E1126", {"start": v(-70.54, -5.1) * mm, "end": v(-71.04, -4.9) * mm});
            skLineSegment(sketch, "E1127", {"start": v(-71.04, -4.9) * mm, "end": v(-71.53, -4.71) * mm});
            skLineSegment(sketch, "E1128", {"start": v(-71.53, -4.71) * mm, "end": v(-71.97, -4.54) * mm});
            skLineSegment(sketch, "E1129", {"start": v(-71.97, -4.54) * mm, "end": v(-72.27, -4.42) * mm});
            skLineSegment(sketch, "E1130", {"start": v(-72.27, -4.42) * mm, "end": v(-72.4, -4.37) * mm});
            skLineSegment(sketch, "E1131", {"start": v(-72.4, -4.37) * mm, "end": v(-72.54, -4.28) * mm});
            skLineSegment(sketch, "E1132", {"start": v(-72.54, -4.28) * mm, "end": v(-72.86, -4.09) * mm});
            skLineSegment(sketch, "E1133", {"start": v(-72.86, -4.09) * mm, "end": v(-73.18, -3.9) * mm});
            skLineSegment(sketch, "E1134", {"start": v(-73.18, -3.9) * mm, "end": v(-73.32, -3.8) * mm});
            skLineSegment(sketch, "E1135", {"start": v(-73.32, -3.8) * mm, "end": v(-73.4, -3.68) * mm});
            skLineSegment(sketch, "E1136", {"start": v(-73.4, -3.68) * mm, "end": v(-73.5, -3.56) * mm});
            skLineSegment(sketch, "E1137", {"start": v(-73.5, -3.56) * mm, "end": v(-73.45, -3.64) * mm});
            skLineSegment(sketch, "E1138", {"start": v(-73.45, -3.64) * mm, "end": v(-73.4, -3.73) * mm});
            skLineSegment(sketch, "E1139", {"start": v(-73.4, -3.73) * mm, "end": v(-73.5, -3.73) * mm});
            skLineSegment(sketch, "E1140", {"start": v(-73.5, -3.73) * mm, "end": v(-73.98, -3.22) * mm});
            skLineSegment(sketch, "E1141", {"start": v(-73.98, -3.22) * mm, "end": v(-74.6, -2.84) * mm});
            skLineSegment(sketch, "E1142", {"start": v(-74.6, -2.84) * mm, "end": v(-75.73, -1.97) * mm});
            skLineSegment(sketch, "E1143", {"start": v(-75.73, -1.97) * mm, "end": v(-76.62, -0.85) * mm});
            skLineSegment(sketch, "E1144", {"start": v(-76.62, -0.85) * mm, "end": v(-76.46, -0.97) * mm});
            skLineSegment(sketch, "E1145", {"start": v(-76.46, -0.97) * mm, "end": v(-76.29, -1.1) * mm});
            skLineSegment(sketch, "E1146", {"start": v(-76.29, -1.1) * mm, "end": v(-76.53, -0.74) * mm});
            skLineSegment(sketch, "E1147", {"start": v(-76.53, -0.74) * mm, "end": v(-76.88, -0.5) * mm});
            skLineSegment(sketch, "E1148", {"start": v(-76.88, -0.5) * mm, "end": v(-76.95, -0.02) * mm});
            skLineSegment(sketch, "E1149", {"start": v(-76.95, -0.02) * mm, "end": v(-77.03, 0.39) * mm});
            skLineSegment(sketch, "E1150", {"start": v(-77.03, 0.39) * mm, "end": v(-77.1, 0.83) * mm});
            skLineSegment(sketch, "E1151", {"start": v(-77.1, 0.83) * mm, "end": v(-77.13, 1.44) * mm});
            skLineSegment(sketch, "E1152", {"start": v(-77.13, 1.44) * mm, "end": v(-77.1, 2.37) * mm});
            skLineSegment(sketch, "E1153", {"start": v(-77.1, 2.37) * mm, "end": v(-77.04, 2.81) * mm});
            skLineSegment(sketch, "E1154", {"start": v(-77.04, 2.81) * mm, "end": v(-76.94, 3.19) * mm});
            skLineSegment(sketch, "E1155", {"start": v(-76.94, 3.19) * mm, "end": v(-76.82, 3.9) * mm});
            skLineSegment(sketch, "E1156", {"start": v(-76.82, 3.9) * mm, "end": v(-76.8, 4.17) * mm});
            skLineSegment(sketch, "E1157", {"start": v(-76.8, 4.17) * mm, "end": v(-76.76, 4.78) * mm});
            skLineSegment(sketch, "E1158", {"start": v(-76.76, 4.78) * mm, "end": v(-76.73, 5.4) * mm});
            skLineSegment(sketch, "E1159", {"start": v(-76.73, 5.4) * mm, "end": v(-76.7, 5.67) * mm});
            skLineSegment(sketch, "E1160", {"start": v(-76.7, 5.67) * mm, "end": v(-76.7, 5.88) * mm});
            skLineSegment(sketch, "E1161", {"start": v(-76.7, 5.88) * mm, "end": v(-76.67, 6.35) * mm});
            skLineSegment(sketch, "E1162", {"start": v(-76.67, 6.35) * mm, "end": v(-76.64, 6.82) * mm});
            skLineSegment(sketch, "E1163", {"start": v(-76.64, 6.82) * mm, "end": v(-76.62, 7.03) * mm});
            skLineSegment(sketch, "E1164", {"start": v(-76.62, 7.03) * mm, "end": v(-78.5, 6.27) * mm});
            skLineSegment(sketch, "E1165", {"start": v(-78.5, 6.27) * mm, "end": v(-80.52, 6.3) * mm});
            skLineSegment(sketch, "E1166", {"start": v(-80.52, 6.3) * mm, "end": v(-80.72, 6.34) * mm});
            skLineSegment(sketch, "E1167", {"start": v(-80.72, 6.34) * mm, "end": v(-81.15, 6.41) * mm});
            skLineSegment(sketch, "E1168", {"start": v(-81.15, 6.41) * mm, "end": v(-81.6, 6.49) * mm});
            skLineSegment(sketch, "E1169", {"start": v(-81.6, 6.49) * mm, "end": v(-81.79, 6.52) * mm});
            skLineSegment(sketch, "E1170", {"start": v(-81.79, 6.52) * mm, "end": v(-81.92, 6.11) * mm});
            skLineSegment(sketch, "E1171", {"start": v(-81.92, 6.11) * mm, "end": v(-82.24, 5.85) * mm});
            skLineSegment(sketch, "E1172", {"start": v(-82.24, 5.85) * mm, "end": v(-82.76, 5.5) * mm});
            skLineSegment(sketch, "E1173", {"start": v(-82.76, 5.5) * mm, "end": v(-83.32, 5.15) * mm});
            skLineSegment(sketch, "E1174", {"start": v(-83.32, 5.15) * mm, "end": v(-83.74, 4.87) * mm});
            skLineSegment(sketch, "E1175", {"start": v(-83.74, 4.87) * mm, "end": v(-84.48, 4.17) * mm});
            skLineSegment(sketch, "E1176", {"start": v(-84.48, 4.17) * mm, "end": v(-85.24, 3.27) * mm});
            skLineSegment(sketch, "E1177", {"start": v(-85.24, 3.27) * mm, "end": v(-85.94, 2.31) * mm});
            skLineSegment(sketch, "E1178", {"start": v(-85.94, 2.31) * mm, "end": v(-86.5, 1.44) * mm});
            skLineSegment(sketch, "E1179", {"start": v(-86.5, 1.44) * mm, "end": v(-88.2, -2.61) * mm});
            skLineSegment(sketch, "E1180", {"start": v(-88.2, -2.61) * mm, "end": v(-88.9, -6.94) * mm});
            skLineSegment(sketch, "E1181", {"start": v(-88.9, -6.94) * mm, "end": v(-88.9, -7.5) * mm});
            skLineSegment(sketch, "E1182", {"start": v(-88.9, -7.5) * mm, "end": v(-88.9, -8.76) * mm});
            skLineSegment(sketch, "E1183", {"start": v(-88.9, -8.76) * mm, "end": v(-88.9, -10.01) * mm});
            skLineSegment(sketch, "E1184", {"start": v(-88.9, -10.01) * mm, "end": v(-88.9, -10.58) * mm});
            skLineSegment(sketch, "E1185", {"start": v(-88.9, -10.58) * mm, "end": v(-88.86, -11) * mm});
            skLineSegment(sketch, "E1186", {"start": v(-88.86, -11) * mm, "end": v(-88.82, -11.43) * mm});
            skLineSegment(sketch, "E1187", {"start": v(-88.82, -11.43) * mm, "end": v(-88.73, -12.52) * mm});
            skLineSegment(sketch, "E1188", {"start": v(-88.73, -12.52) * mm, "end": v(-88.6, -13.49) * mm});
            skLineSegment(sketch, "E1189", {"start": v(-88.6, -13.49) * mm, "end": v(-88.38, -14.44) * mm});
            skLineSegment(sketch, "E1190", {"start": v(-88.38, -14.44) * mm, "end": v(-88.05, -15.5) * mm});
            skLineSegment(sketch, "E1191", {"start": v(-88.05, -15.5) * mm, "end": v(-87.91, -15.88) * mm});
            skLineSegment(sketch, "E1192", {"start": v(-87.91, -15.88) * mm, "end": v(-87.6, -16.72) * mm});
            skLineSegment(sketch, "E1193", {"start": v(-87.6, -16.72) * mm, "end": v(-87.28, -17.56) * mm});
            skLineSegment(sketch, "E1194", {"start": v(-87.28, -17.56) * mm, "end": v(-87.14, -17.95) * mm});
            skLineSegment(sketch, "E1195", {"start": v(-87.14, -17.95) * mm, "end": v(-86.83, -18.79) * mm});
            skLineSegment(sketch, "E1196", {"start": v(-86.83, -18.79) * mm, "end": v(-86.36, -19.56) * mm});
            skLineSegment(sketch, "E1197", {"start": v(-86.36, -19.56) * mm, "end": v(-86.3, -19.32) * mm});
            skLineSegment(sketch, "E1198", {"start": v(-86.3, -19.32) * mm, "end": v(-86.17, -18.8) * mm});
            skLineSegment(sketch, "E1199", {"start": v(-86.17, -18.8) * mm, "end": v(-86.04, -18.27) * mm});
            skLineSegment(sketch, "E1200", {"start": v(-86.04, -18.27) * mm, "end": v(-85.98, -18.03) * mm});
            skLineSegment(sketch, "E1201", {"start": v(-85.98, -18.03) * mm, "end": v(-85.78, -16.9) * mm});
            skLineSegment(sketch, "E1202", {"start": v(-85.78, -16.9) * mm, "end": v(-85.27, -15.85) * mm});
            skLineSegment(sketch, "E1203", {"start": v(-85.27, -15.85) * mm, "end": v(-85.03, -15.63) * mm});
            skLineSegment(sketch, "E1204", {"start": v(-85.03, -15.63) * mm, "end": v(-84.64, -15.38) * mm});
            skLineSegment(sketch, "E1205", {"start": v(-84.64, -15.38) * mm, "end": v(-84.23, -15.18) * mm});
            skLineSegment(sketch, "E1206", {"start": v(-84.23, -15.18) * mm, "end": v(-83.94, -15.13) * mm});
            skLineSegment(sketch, "E1207", {"start": v(-83.94, -15.13) * mm, "end": v(-83.72, -15.4) * mm});
            skLineSegment(sketch, "E1208", {"start": v(-83.72, -15.4) * mm, "end": v(-83.56, -15.75) * mm});
            skLineSegment(sketch, "E1209", {"start": v(-83.56, -15.75) * mm, "end": v(-82.6, -17.36) * mm});
            skLineSegment(sketch, "E1210", {"start": v(-82.6, -17.36) * mm, "end": v(-82.5, -17.5) * mm});
            skLineSegment(sketch, "E1211", {"start": v(-82.5, -17.5) * mm, "end": v(-82.24, -17.85) * mm});
            skLineSegment(sketch, "E1212", {"start": v(-82.24, -17.85) * mm, "end": v(-81.86, -18.35) * mm});
            skLineSegment(sketch, "E1213", {"start": v(-81.86, -18.35) * mm, "end": v(-81.43, -18.92) * mm});
            skLineSegment(sketch, "E1214", {"start": v(-81.43, -18.92) * mm, "end": v(-81, -19.5) * mm});
            skLineSegment(sketch, "E1215", {"start": v(-81, -19.5) * mm, "end": v(-80.62, -20) * mm});
            skLineSegment(sketch, "E1216", {"start": v(-80.62, -20) * mm, "end": v(-80.36, -20.35) * mm});
            skLineSegment(sketch, "E1217", {"start": v(-80.36, -20.35) * mm, "end": v(-80.25, -20.49) * mm});
            skLineSegment(sketch, "E1218", {"start": v(-80.25, -20.49) * mm, "end": v(-79.22, -21.88) * mm});
            skLineSegment(sketch, "E1219", {"start": v(-79.22, -21.88) * mm, "end": v(-78.06, -23.2) * mm});
            skLineSegment(sketch, "E1220", {"start": v(-78.06, -23.2) * mm, "end": v(-77.98, -23.03) * mm});
            skLineSegment(sketch, "E1221", {"start": v(-77.98, -23.03) * mm, "end": v(-77.9, -22.86) * mm});
            skLineSegment(sketch, "E1222", {"start": v(-77.9, -22.86) * mm, "end": v(-77.98, -22.56) * mm});
            skLineSegment(sketch, "E1223", {"start": v(-77.98, -22.56) * mm, "end": v(-78.06, -22.27) * mm});
            skLineSegment(sketch, "E1224", {"start": v(-78.06, -22.27) * mm, "end": v(-77.5, -22.58) * mm});
            skLineSegment(sketch, "E1225", {"start": v(-77.5, -22.58) * mm, "end": v(-77.05, -23.02) * mm});
            skLineSegment(sketch, "E1226", {"start": v(-77.05, -23.02) * mm, "end": v(-76.81, -23.22) * mm});
            skLineSegment(sketch, "E1227", {"start": v(-76.81, -23.22) * mm, "end": v(-76.29, -23.66) * mm});
            skLineSegment(sketch, "E1228", {"start": v(-76.29, -23.66) * mm, "end": v(-75.76, -24.1) * mm});
            skLineSegment(sketch, "E1229", {"start": v(-75.76, -24.1) * mm, "end": v(-75.52, -24.3) * mm});
            skLineSegment(sketch, "E1230", {"start": v(-75.52, -24.3) * mm, "end": v(-74.57, -24.83) * mm});
            skLineSegment(sketch, "E1231", {"start": v(-74.57, -24.83) * mm, "end": v(-73.58, -25.22) * mm});
            skLineSegment(sketch, "E1232", {"start": v(-73.58, -25.22) * mm, "end": v(-73.23, -25.36) * mm});
            skLineSegment(sketch, "E1233", {"start": v(-73.23, -25.36) * mm, "end": v(-72.48, -25.7) * mm});
            skLineSegment(sketch, "E1234", {"start": v(-72.48, -25.7) * mm, "end": v(-71.72, -26.01) * mm});
            skLineSegment(sketch, "E1235", {"start": v(-71.72, -26.01) * mm, "end": v(-71.37, -26.16) * mm});
            skLineSegment(sketch, "E1236", {"start": v(-71.37, -26.16) * mm, "end": v(-71.94, -25.36) * mm});
            skLineSegment(sketch, "E1237", {"start": v(-71.94, -25.36) * mm, "end": v(-72.49, -24.55) * mm});
            skLineSegment(sketch, "E1238", {"start": v(-72.49, -24.55) * mm, "end": v(-72.88, -23.6) * mm});
            skLineSegment(sketch, "E1239", {"start": v(-72.88, -23.6) * mm, "end": v(-73.04, -22.93) * mm});
            skLineSegment(sketch, "E1240", {"start": v(-73.04, -22.93) * mm, "end": v(-73.14, -22.3) * mm});
            skLineSegment(sketch, "E1241", {"start": v(-73.14, -22.3) * mm, "end": v(-73.38, -21.42) * mm});
            skLineSegment(sketch, "E1242", {"start": v(-73.38, -21.42) * mm, "end": v(-73.44, -21.22) * mm});
            skLineSegment(sketch, "E1243", {"start": v(-73.44, -21.22) * mm, "end": v(-73.6, -20.7) * mm});
            skLineSegment(sketch, "E1244", {"start": v(-73.6, -20.7) * mm, "end": v(-73.83, -19.97) * mm});
            skLineSegment(sketch, "E1245", {"start": v(-73.83, -19.97) * mm, "end": v(-74.09, -19.13) * mm});
            skLineSegment(sketch, "E1246", {"start": v(-74.09, -19.13) * mm, "end": v(-74.34, -18.3) * mm});
            skLineSegment(sketch, "E1247", {"start": v(-74.34, -18.3) * mm, "end": v(-74.57, -17.56) * mm});
            skLineSegment(sketch, "E1248", {"start": v(-74.57, -17.56) * mm, "end": v(-74.73, -17.04) * mm});
            skLineSegment(sketch, "E1249", {"start": v(-74.73, -17.04) * mm, "end": v(-74.8, -16.85) * mm});
            skLineSegment(sketch, "E1250", {"start": v(-74.8, -16.85) * mm, "end": v(-75.2, -14.45) * mm});
            skLineSegment(sketch, "E1251", {"start": v(-75.2, -14.45) * mm, "end": v(-75.45, -12.02) * mm});
            skLineSegment(sketch, "E1252", {"start": v(-75.45, -12.02) * mm, "end": v(-75.47, -11.89) * mm});
            skLineSegment(sketch, "E1253", {"start": v(-75.47, -11.89) * mm, "end": v(-75.52, -11.6) * mm});
            skLineSegment(sketch, "E1254", {"start": v(-75.52, -11.6) * mm, "end": v(-75.57, -11.3) * mm});
            skLineSegment(sketch, "E1255", {"start": v(-75.57, -11.3) * mm, "end": v(-75.58, -11.17) * mm});
            skLineSegment(sketch, "E1256", {"start": v(-75.58, -11.17) * mm, "end": v(-75.63, -10.71) * mm});
            skLineSegment(sketch, "E1257", {"start": v(-75.63, -10.71) * mm, "end": v(-75.73, -9.7) * mm});
            skLineSegment(sketch, "E1258", {"start": v(-75.73, -9.7) * mm, "end": v(-75.82, -8.67) * mm});
            skLineSegment(sketch, "E1259", {"start": v(-75.82, -8.67) * mm, "end": v(-75.87, -8.21) * mm});
            skLineSegment(sketch, "E1260", {"start": v(-75.87, -8.21) * mm, "end": v(-75.88, -8.04) * mm});
            skLineSegment(sketch, "E1261", {"start": v(-75.88, -8.04) * mm, "end": v(-75.92, -7.59) * mm});
            skLineSegment(sketch, "E1262", {"start": v(-75.92, -7.59) * mm, "end": v(-75.97, -6.95) * mm});
            skLineSegment(sketch, "E1263", {"start": v(-75.97, -6.95) * mm, "end": v(-76.03, -6.22) * mm});
            skLineSegment(sketch, "E1264", {"start": v(-76.03, -6.22) * mm, "end": v(-76.1, -5.5) * mm});
            skLineSegment(sketch, "E1265", {"start": v(-76.1, -5.5) * mm, "end": v(-76.15, -4.85) * mm});
            skLineSegment(sketch, "E1266", {"start": v(-76.15, -4.85) * mm, "end": v(-76.19, -4.4) * mm});
            skLineSegment(sketch, "E1267", {"start": v(-76.19, -4.4) * mm, "end": v(-76.2, -4.23) * mm});
            skLineSegment(sketch, "E1268", {"start": v(-76.2, -4.23) * mm, "end": v(-76.25, -3.76) * mm});
            skLineSegment(sketch, "E1269", {"start": v(-76.25, -3.76) * mm, "end": v(-76.28, -3.36) * mm});
            skLineSegment(sketch, "E1270", {"start": v(-76.28, -3.36) * mm, "end": v(-76.18, -3) * mm});
            skLineSegment(sketch, "E1271", {"start": v(-76.18, -3) * mm, "end": v(-75.86, -2.62) * mm});
            skLineSegment(sketch, "E1272", {"start": v(-75.86, -2.62) * mm, "end": v(-75.22, -3.23) * mm});
            skLineSegment(sketch, "E1273", {"start": v(-75.22, -3.23) * mm, "end": v(-74.68, -3.83) * mm});
            skLineSegment(sketch, "E1274", {"start": v(-74.68, -3.83) * mm, "end": v(-74.57, -4.25) * mm});
            skLineSegment(sketch, "E1275", {"start": v(-74.57, -4.25) * mm, "end": v(-74.5, -4.84) * mm});
            skLineSegment(sketch, "E1276", {"start": v(-74.5, -4.84) * mm, "end": v(-74.44, -5.45) * mm});
            skLineSegment(sketch, "E1277", {"start": v(-74.44, -5.45) * mm, "end": v(-74.41, -5.93) * mm});
            skLineSegment(sketch, "E1278", {"start": v(-74.41, -5.93) * mm, "end": v(-74.4, -6.11) * mm});
            skLineSegment(sketch, "E1279", {"start": v(-74.4, -6.11) * mm, "end": v(-74.36, -6.6) * mm});
            skLineSegment(sketch, "E1280", {"start": v(-74.36, -6.6) * mm, "end": v(-74.3, -7.3) * mm});
            skLineSegment(sketch, "E1281", {"start": v(-74.3, -7.3) * mm, "end": v(-74.25, -8.09) * mm});
            skLineSegment(sketch, "E1282", {"start": v(-74.25, -8.09) * mm, "end": v(-74.18, -8.88) * mm});
            skLineSegment(sketch, "E1283", {"start": v(-74.18, -8.88) * mm, "end": v(-74.13, -9.57) * mm});
            skLineSegment(sketch, "E1284", {"start": v(-74.13, -9.57) * mm, "end": v(-74.1, -10.06) * mm});
            skLineSegment(sketch, "E1285", {"start": v(-74.1, -10.06) * mm, "end": v(-74.08, -10.24) * mm});
            skLineSegment(sketch, "E1286", {"start": v(-74.08, -10.24) * mm, "end": v(-74.04, -10.52) * mm});
            skLineSegment(sketch, "E1287", {"start": v(-74.04, -10.52) * mm, "end": v(-73.96, -11.13) * mm});
            skLineSegment(sketch, "E1288", {"start": v(-73.96, -11.13) * mm, "end": v(-73.88, -11.74) * mm});
            skLineSegment(sketch, "E1289", {"start": v(-73.88, -11.74) * mm, "end": v(-73.84, -12.02) * mm});
            skLineSegment(sketch, "E1290", {"start": v(-73.84, -12.02) * mm, "end": v(-73.56, -14.6) * mm});
            skLineSegment(sketch, "E1291", {"start": v(-73.56, -14.6) * mm, "end": v(-73.24, -16.8) * mm});
            skLineSegment(sketch, "E1292", {"start": v(-73.24, -16.8) * mm, "end": v(-72.77, -18.99) * mm});
            skLineSegment(sketch, "E1293", {"start": v(-72.77, -18.99) * mm, "end": v(-72.05, -21.5) * mm});
            skLineSegment(sketch, "E1294", {"start": v(-72.05, -21.5) * mm, "end": v(-71.9, -21.9) * mm});
            skLineSegment(sketch, "E1295", {"start": v(-71.9, -21.9) * mm, "end": v(-71.55, -22.77) * mm});
            skLineSegment(sketch, "E1296", {"start": v(-71.55, -22.77) * mm, "end": v(-71.2, -23.65) * mm});
            skLineSegment(sketch, "E1297", {"start": v(-71.2, -23.65) * mm, "end": v(-71.05, -24.04) * mm});
            skLineSegment(sketch, "E1298", {"start": v(-71.05, -24.04) * mm, "end": v(-70.96, -24.28) * mm});
            skLineSegment(sketch, "E1299", {"start": v(-70.96, -24.28) * mm, "end": v(-70.76, -24.8) * mm});
            skLineSegment(sketch, "E1300", {"start": v(-70.76, -24.8) * mm, "end": v(-70.56, -25.33) * mm});
            skLineSegment(sketch, "E1301", {"start": v(-70.56, -25.33) * mm, "end": v(-70.47, -25.57) * mm});
            skLineSegment(sketch, "E1302", {"start": v(-70.47, -25.57) * mm, "end": v(-69.84, -26.38) * mm});
            skLineSegment(sketch, "E1303", {"start": v(-69.84, -26.38) * mm, "end": v(-69.33, -26.93) * mm});
            skLineSegment(sketch, "E1304", {"start": v(-69.33, -26.93) * mm, "end": v(-69.04, -27.71) * mm});
            skLineSegment(sketch, "E1305", {"start": v(-69.04, -27.71) * mm, "end": v(-69, -28.53) * mm});
            skLineSegment(sketch, "E1306", {"start": v(-69, -28.53) * mm, "end": v(-71, -28.1) * mm});
            skLineSegment(sketch, "E1307", {"start": v(-71, -28.1) * mm, "end": v(-72.9, -27.33) * mm});
            skLineSegment(sketch, "E1308", {"start": v(-72.9, -27.33) * mm, "end": v(-73.99, -26.9) * mm});
            skLineSegment(sketch, "E1309", {"start": v(-73.99, -26.9) * mm, "end": v(-74.86, -26.53) * mm});
            skLineSegment(sketch, "E1310", {"start": v(-74.86, -26.53) * mm, "end": v(-75.68, -26.04) * mm});
            skLineSegment(sketch, "E1311", {"start": v(-75.68, -26.04) * mm, "end": v(-76.62, -25.23) * mm});
            skLineSegment(sketch, "E1312", {"start": v(-76.62, -25.23) * mm, "end": v(-76.58, -25.72) * mm});
            skLineSegment(sketch, "E1313", {"start": v(-76.58, -25.72) * mm, "end": v(-76.57, -25.93) * mm});
            skLineSegment(sketch, "E1314", {"start": v(-76.57, -25.93) * mm, "end": v(-76.63, -26.12) * mm});
            skLineSegment(sketch, "E1315", {"start": v(-76.63, -26.12) * mm, "end": v(-76.8, -26.58) * mm});
            skLineSegment(sketch, "E1316", {"start": v(-76.8, -26.58) * mm, "end": v(-77.48, -26.2) * mm});
            skLineSegment(sketch, "E1317", {"start": v(-77.48, -26.2) * mm, "end": v(-77.98, -25.57) * mm});
            skLineSegment(sketch, "E1318", {"start": v(-77.98, -25.57) * mm, "end": v(-78.16, -25.36) * mm});
            skLineSegment(sketch, "E1319", {"start": v(-78.16, -25.36) * mm, "end": v(-78.54, -24.9) * mm});
            skLineSegment(sketch, "E1320", {"start": v(-78.54, -24.9) * mm, "end": v(-78.93, -24.43) * mm});
            skLineSegment(sketch, "E1321", {"start": v(-78.93, -24.43) * mm, "end": v(-79.1, -24.21) * mm});
            skLineSegment(sketch, "E1322", {"start": v(-79.1, -24.21) * mm, "end": v(-79.24, -24.04) * mm});
            skLineSegment(sketch, "E1323", {"start": v(-79.24, -24.04) * mm, "end": v(-79.51, -23.66) * mm});
            skLineSegment(sketch, "E1324", {"start": v(-79.51, -23.66) * mm, "end": v(-79.8, -23.28) * mm});
            skLineSegment(sketch, "E1325", {"start": v(-79.8, -23.28) * mm, "end": v(-79.92, -23.11) * mm});
            skLineSegment(sketch, "E1326", {"start": v(-79.92, -23.11) * mm, "end": v(-80.06, -22.89) * mm});
            skLineSegment(sketch, "E1327", {"start": v(-80.06, -22.89) * mm, "end": v(-80.36, -22.4) * mm});
            skLineSegment(sketch, "E1328", {"start": v(-80.36, -22.4) * mm, "end": v(-80.66, -21.9) * mm});
            skLineSegment(sketch, "E1329", {"start": v(-80.66, -21.9) * mm, "end": v(-80.8, -21.67) * mm});
            skLineSegment(sketch, "E1330", {"start": v(-80.8, -21.67) * mm, "end": v(-80.98, -21.44) * mm});
            skLineSegment(sketch, "E1331", {"start": v(-80.98, -21.44) * mm, "end": v(-81.36, -20.91) * mm});
            skLineSegment(sketch, "E1332", {"start": v(-81.36, -20.91) * mm, "end": v(-81.74, -20.39) * mm});
            skLineSegment(sketch, "E1333", {"start": v(-81.74, -20.39) * mm, "end": v(-81.91, -20.15) * mm});
            skLineSegment(sketch, "E1334", {"start": v(-81.91, -20.15) * mm, "end": v(-81.98, -20.03) * mm});
            skLineSegment(sketch, "E1335", {"start": v(-81.98, -20.03) * mm, "end": v(-82.17, -19.7) * mm});
            skLineSegment(sketch, "E1336", {"start": v(-82.17, -19.7) * mm, "end": v(-82.43, -19.24) * mm});
            skLineSegment(sketch, "E1337", {"start": v(-82.43, -19.24) * mm, "end": v(-82.73, -18.71) * mm});
            skLineSegment(sketch, "E1338", {"start": v(-82.73, -18.71) * mm, "end": v(-83.03, -18.18) * mm});
            skLineSegment(sketch, "E1339", {"start": v(-83.03, -18.18) * mm, "end": v(-83.29, -17.72) * mm});
            skLineSegment(sketch, "E1340", {"start": v(-83.29, -17.72) * mm, "end": v(-83.47, -17.4) * mm});
            skLineSegment(sketch, "E1341", {"start": v(-83.47, -17.4) * mm, "end": v(-83.54, -17.27) * mm});
            skLineSegment(sketch, "E1342", {"start": v(-83.54, -17.27) * mm, "end": v(-83.6, -17.09) * mm});
            skLineSegment(sketch, "E1343", {"start": v(-83.6, -17.09) * mm, "end": v(-83.72, -16.68) * mm});
            skLineSegment(sketch, "E1344", {"start": v(-83.72, -16.68) * mm, "end": v(-83.85, -16.27) * mm});
            skLineSegment(sketch, "E1345", {"start": v(-83.85, -16.27) * mm, "end": v(-83.9, -16.09) * mm});
            skLineSegment(sketch, "E1346", {"start": v(-83.9, -16.09) * mm, "end": v(-84.17, -16.55) * mm});
            skLineSegment(sketch, "E1347", {"start": v(-84.17, -16.55) * mm, "end": v(-84.4, -17.02) * mm});
            skLineSegment(sketch, "E1348", {"start": v(-84.4, -17.02) * mm, "end": v(-84.42, -17.16) * mm});
            skLineSegment(sketch, "E1349", {"start": v(-84.42, -17.16) * mm, "end": v(-84.49, -17.48) * mm});
            skLineSegment(sketch, "E1350", {"start": v(-84.49, -17.48) * mm, "end": v(-84.55, -17.8) * mm});
            skLineSegment(sketch, "E1351", {"start": v(-84.55, -17.8) * mm, "end": v(-84.58, -17.95) * mm});
            skLineSegment(sketch, "E1352", {"start": v(-84.58, -17.95) * mm, "end": v(-84.71, -18.48) * mm});
            skLineSegment(sketch, "E1353", {"start": v(-84.71, -18.48) * mm, "end": v(-84.93, -19.26) * mm});
            skLineSegment(sketch, "E1354", {"start": v(-84.93, -19.26) * mm, "end": v(-85.16, -20.02) * mm});
            skLineSegment(sketch, "E1355", {"start": v(-85.16, -20.02) * mm, "end": v(-85.34, -20.49) * mm});
            skLineSegment(sketch, "E1356", {"start": v(-85.34, -20.49) * mm, "end": v(-85.87, -21.12) * mm});
            skLineSegment(sketch, "E1357", {"start": v(-85.87, -21.12) * mm, "end": v(-86.61, -21.47) * mm});
            skLineSegment(sketch, "E1358", {"start": v(-86.61, -21.47) * mm, "end": v(-87.11, -21.62) * mm});
            skLineSegment(sketch, "E1359", {"start": v(-87.11, -21.62) * mm, "end": v(-87.38, -21.45) * mm});
            skLineSegment(sketch, "E1360", {"start": v(-87.38, -21.45) * mm, "end": v(-87.56, -21.17) * mm});
            skLineSegment(sketch, "E1361", {"start": v(-87.56, -21.17) * mm, "end": v(-88.44, -19.56) * mm});
            skLineSegment(sketch, "E1362", {"start": v(-88.44, -19.56) * mm, "end": v(-89.78, -16.22) * mm});
            skLineSegment(sketch, "E1363", {"start": v(-89.78, -16.22) * mm, "end": v(-90.52, -12.7) * mm});
            skLineSegment(sketch, "E1364", {"start": v(-90.52, -12.7) * mm, "end": v(-90.53, -12.55) * mm});
            skLineSegment(sketch, "E1365", {"start": v(-90.53, -12.55) * mm, "end": v(-90.56, -12.14) * mm});
            skLineSegment(sketch, "E1366", {"start": v(-90.56, -12.14) * mm, "end": v(-90.6, -11.57) * mm});
            skLineSegment(sketch, "E1367", {"start": v(-90.6, -11.57) * mm, "end": v(-90.64, -10.92) * mm});
            skLineSegment(sketch, "E1368", {"start": v(-90.64, -10.92) * mm, "end": v(-90.7, -10.27) * mm});
            skLineSegment(sketch, "E1369", {"start": v(-90.7, -10.27) * mm, "end": v(-90.73, -9.7) * mm});
            skLineSegment(sketch, "E1370", {"start": v(-90.73, -9.7) * mm, "end": v(-90.76, -9.3) * mm});
            skLineSegment(sketch, "E1371", {"start": v(-90.76, -9.3) * mm, "end": v(-90.77, -9.14) * mm});
            skLineSegment(sketch, "E1372", {"start": v(-90.77, -9.14) * mm, "end": v(-90.78, -8.98) * mm});
            skLineSegment(sketch, "E1373", {"start": v(-90.78, -8.98) * mm, "end": v(-90.8, -8.64) * mm});
            skLineSegment(sketch, "E1374", {"start": v(-90.8, -8.64) * mm, "end": v(-90.84, -8.29) * mm});
            skLineSegment(sketch, "E1375", {"start": v(-90.84, -8.29) * mm, "end": v(-90.85, -8.13) * mm});
            skLineSegment(sketch, "E1376", {"start": v(-90.85, -8.13) * mm, "end": v(-90.85, -7.88) * mm});
            skLineSegment(sketch, "E1377", {"start": v(-90.85, -7.88) * mm, "end": v(-90.85, -7.32) * mm});
            skLineSegment(sketch, "E1378", {"start": v(-90.85, -7.32) * mm, "end": v(-90.85, -6.77) * mm});
            skLineSegment(sketch, "E1379", {"start": v(-90.85, -6.77) * mm, "end": v(-90.85, -6.52) * mm});
            skLineSegment(sketch, "E1380", {"start": v(-90.85, -6.52) * mm, "end": v(-90.73, -5.2) * mm});
            skLineSegment(sketch, "E1381", {"start": v(-90.73, -5.2) * mm, "end": v(-90.52, -3.9) * mm});
            skLineSegment(sketch, "E1382", {"start": v(-90.52, -3.9) * mm, "end": v(-89.34, 0.3) * mm});
            skLineSegment(sketch, "E1383", {"start": v(-89.34, 0.3) * mm, "end": v(-87.03, 3.98) * mm});
            skLineSegment(sketch, "E1384", {"start": v(-87.03, 3.98) * mm, "end": v(-86.91, 4.09) * mm});
            skLineSegment(sketch, "E1385", {"start": v(-86.91, 4.09) * mm, "end": v(-86.65, 4.32) * mm});
            skLineSegment(sketch, "E1386", {"start": v(-86.65, 4.32) * mm, "end": v(-86.4, 4.56) * mm});
            skLineSegment(sketch, "E1387", {"start": v(-86.4, 4.56) * mm, "end": v(-86.28, 4.67) * mm});
            skLineSegment(sketch, "E1388", {"start": v(-86.28, 4.67) * mm, "end": v(-85.8, 5.11) * mm});
            skLineSegment(sketch, "E1389", {"start": v(-85.8, 5.11) * mm, "end": v(-85.26, 5.53) * mm});
            skLineSegment(sketch, "E1390", {"start": v(-85.26, 5.53) * mm, "end": v(-84.72, 5.82) * mm});
            skLineSegment(sketch, "E1391", {"start": v(-84.72, 5.82) * mm, "end": v(-84, 6.12) * mm});
            skLineSegment(sketch, "E1392", {"start": v(-84, 6.12) * mm, "end": v(-83.26, 6.38) * mm});
            skLineSegment(sketch, "E1393", {"start": v(-83.26, 6.38) * mm, "end": v(-82.65, 6.55) * mm});
            skLineSegment(sketch, "E1394", {"start": v(-82.65, 6.55) * mm, "end": v(-82.26, 6.62) * mm});
            skLineSegment(sketch, "E1395", {"start": v(-82.26, 6.62) * mm, "end": v(-81.87, 6.69) * mm});
            skLineSegment(sketch, "E1396", {"start": v(-81.87, 6.69) * mm, "end": v(-82.66, 7.1) * mm});
            skLineSegment(sketch, "E1397", {"start": v(-82.66, 7.1) * mm, "end": v(-83.48, 7.72) * mm});
            skLineSegment(sketch, "E1398", {"start": v(-83.48, 7.72) * mm, "end": v(-84.24, 8.4) * mm});
            skLineSegment(sketch, "E1399", {"start": v(-84.24, 8.4) * mm, "end": v(-84.86, 9.06) * mm});
            skLineSegment(sketch, "E1400", {"start": v(-82.13, 37) * mm, "end": v(-81.22, 36.08) * mm});
            skLineSegment(sketch, "E1401", {"start": v(-81.22, 36.08) * mm, "end": v(-80.28, 35.28) * mm});
            skLineSegment(sketch, "E1402", {"start": v(-80.28, 35.28) * mm, "end": v(-79.73, 34.61) * mm});
            skLineSegment(sketch, "E1403", {"start": v(-79.73, 34.61) * mm, "end": v(-79.08, 33.9) * mm});
            skLineSegment(sketch, "E1404", {"start": v(-79.08, 33.9) * mm, "end": v(-78.85, 33.74) * mm});
            skLineSegment(sketch, "E1405", {"start": v(-78.85, 33.74) * mm, "end": v(-78.36, 33.39) * mm});
            skLineSegment(sketch, "E1406", {"start": v(-78.36, 33.39) * mm, "end": v(-77.87, 33.04) * mm});
            skLineSegment(sketch, "E1407", {"start": v(-77.87, 33.04) * mm, "end": v(-77.64, 32.88) * mm});
            skLineSegment(sketch, "E1408", {"start": v(-77.64, 32.88) * mm, "end": v(-75.7, 31.65) * mm});
            skLineSegment(sketch, "E1409", {"start": v(-75.7, 31.65) * mm, "end": v(-75.46, 31.56) * mm});
            skLineSegment(sketch, "E1410", {"start": v(-75.46, 31.56) * mm, "end": v(-74.93, 31.34) * mm});
            skLineSegment(sketch, "E1411", {"start": v(-74.93, 31.34) * mm, "end": v(-74.4, 31.13) * mm});
            skLineSegment(sketch, "E1412", {"start": v(-74.4, 31.13) * mm, "end": v(-74.17, 31.04) * mm});
            skLineSegment(sketch, "E1413", {"start": v(-74.17, 31.04) * mm, "end": v(-73.09, 30.64) * mm});
            skLineSegment(sketch, "E1414", {"start": v(-73.09, 30.64) * mm, "end": v(-72.28, 30.36) * mm});
            skLineSegment(sketch, "E1415", {"start": v(-72.28, 30.36) * mm, "end": v(-71.46, 30.12) * mm});
            skLineSegment(sketch, "E1416", {"start": v(-71.46, 30.12) * mm, "end": v(-70.36, 29.83) * mm});
            skLineSegment(sketch, "E1417", {"start": v(-70.36, 29.83) * mm, "end": v(-66.89, 29.07) * mm});
            skLineSegment(sketch, "E1418", {"start": v(-66.89, 29.07) * mm, "end": v(-63.66, 28.69) * mm});
            skLineSegment(sketch, "E1419", {"start": v(-63.66, 28.69) * mm, "end": v(-60.42, 28.55) * mm});
            skLineSegment(sketch, "E1420", {"start": v(-60.42, 28.55) * mm, "end": v(-56.9, 28.53) * mm});
            skLineSegment(sketch, "E1421", {"start": v(-56.9, 28.53) * mm, "end": v(-55.32, 28.67) * mm});
            skLineSegment(sketch, "E1422", {"start": v(-55.32, 28.67) * mm, "end": v(-53.35, 29) * mm});
            skLineSegment(sketch, "E1423", {"start": v(-53.35, 29) * mm, "end": v(-51.38, 29.4) * mm});
            skLineSegment(sketch, "E1424", {"start": v(-51.38, 29.4) * mm, "end": v(-49.79, 29.8) * mm});
            skLineSegment(sketch, "E1425", {"start": v(-49.79, 29.8) * mm, "end": v(-49.57, 29.86) * mm});
            skLineSegment(sketch, "E1426", {"start": v(-49.57, 29.86) * mm, "end": v(-49.02, 30.04) * mm});
            skLineSegment(sketch, "E1427", {"start": v(-49.02, 30.04) * mm, "end": v(-48.23, 30.3) * mm});
            skLineSegment(sketch, "E1428", {"start": v(-48.23, 30.3) * mm, "end": v(-47.33, 30.59) * mm});
            skLineSegment(sketch, "E1429", {"start": v(-47.33, 30.59) * mm, "end": v(-46.43, 30.88) * mm});
            skLineSegment(sketch, "E1430", {"start": v(-46.43, 30.88) * mm, "end": v(-45.64, 31.14) * mm});
            skLineSegment(sketch, "E1431", {"start": v(-45.64, 31.14) * mm, "end": v(-45.09, 31.32) * mm});
            skLineSegment(sketch, "E1432", {"start": v(-45.09, 31.32) * mm, "end": v(-44.87, 31.38) * mm});
            skLineSegment(sketch, "E1433", {"start": v(-44.87, 31.38) * mm, "end": v(-44.52, 31.5) * mm});
            skLineSegment(sketch, "E1434", {"start": v(-44.52, 31.5) * mm, "end": v(-43.73, 31.75) * mm});
            skLineSegment(sketch, "E1435", {"start": v(-43.73, 31.75) * mm, "end": v(-42.95, 32) * mm});
            skLineSegment(sketch, "E1436", {"start": v(-42.95, 32) * mm, "end": v(-42.59, 32.12) * mm});
            skLineSegment(sketch, "E1437", {"start": v(-42.59, 32.12) * mm, "end": v(-42.36, 32.22) * mm});
            skLineSegment(sketch, "E1438", {"start": v(-42.36, 32.22) * mm, "end": v(-41.87, 32.43) * mm});
            skLineSegment(sketch, "E1439", {"start": v(-41.87, 32.43) * mm, "end": v(-41.37, 32.64) * mm});
            skLineSegment(sketch, "E1440", {"start": v(-41.37, 32.64) * mm, "end": v(-41.15, 32.73) * mm});
            skLineSegment(sketch, "E1441", {"start": v(-41.15, 32.73) * mm, "end": v(-40.47, 33.04) * mm});
            skLineSegment(sketch, "E1442", {"start": v(-40.47, 33.04) * mm, "end": v(-39.6, 33.44) * mm});
            skLineSegment(sketch, "E1443", {"start": v(-39.6, 33.44) * mm, "end": v(-38.74, 33.8) * mm});
            skLineSegment(sketch, "E1444", {"start": v(-38.74, 33.8) * mm, "end": v(-38.1, 33.94) * mm});
            skLineSegment(sketch, "E1445", {"start": v(-38.1, 33.94) * mm, "end": v(-37.5, 33.78) * mm});
            skLineSegment(sketch, "E1446", {"start": v(-37.5, 33.78) * mm, "end": v(-37.42, 33.61) * mm});
            skLineSegment(sketch, "E1447", {"start": v(-37.42, 33.61) * mm, "end": v(-37.34, 33.44) * mm});
            skLineSegment(sketch, "E1448", {"start": v(-37.34, 33.44) * mm, "end": v(-37.32, 33.02) * mm});
            skLineSegment(sketch, "E1449", {"start": v(-37.32, 33.02) * mm, "end": v(-37.39, 32.61) * mm});
            skLineSegment(sketch, "E1450", {"start": v(-37.39, 32.61) * mm, "end": v(-37.7, 32.33) * mm});
            skLineSegment(sketch, "E1451", {"start": v(-37.7, 32.33) * mm, "end": v(-38.21, 32.03) * mm});
            skLineSegment(sketch, "E1452", {"start": v(-38.21, 32.03) * mm, "end": v(-38.77, 31.78) * mm});
            skLineSegment(sketch, "E1453", {"start": v(-38.77, 31.78) * mm, "end": v(-39.2, 31.6) * mm});
            skLineSegment(sketch, "E1454", {"start": v(-39.2, 31.6) * mm, "end": v(-39.48, 31.46) * mm});
            skLineSegment(sketch, "E1455", {"start": v(-39.48, 31.46) * mm, "end": v(-40.1, 31.18) * mm});
            skLineSegment(sketch, "E1456", {"start": v(-40.1, 31.18) * mm, "end": v(-40.7, 30.9) * mm});
            skLineSegment(sketch, "E1457", {"start": v(-40.7, 30.9) * mm, "end": v(-40.98, 30.77) * mm});
            skLineSegment(sketch, "E1458", {"start": v(-40.98, 30.77) * mm, "end": v(-41.1, 30.73) * mm});
            skLineSegment(sketch, "E1459", {"start": v(-41.1, 30.73) * mm, "end": v(-41.43, 30.62) * mm});
            skLineSegment(sketch, "E1460", {"start": v(-41.43, 30.62) * mm, "end": v(-41.9, 30.46) * mm});
            skLineSegment(sketch, "E1461", {"start": v(-41.9, 30.46) * mm, "end": v(-42.42, 30.28) * mm});
            skLineSegment(sketch, "E1462", {"start": v(-42.42, 30.28) * mm, "end": v(-42.95, 30.1) * mm});
            skLineSegment(sketch, "E1463", {"start": v(-42.95, 30.1) * mm, "end": v(-43.4, 29.95) * mm});
            skLineSegment(sketch, "E1464", {"start": v(-43.4, 29.95) * mm, "end": v(-43.74, 29.84) * mm});
            skLineSegment(sketch, "E1465", {"start": v(-43.74, 29.84) * mm, "end": v(-43.86, 29.8) * mm});
            skLineSegment(sketch, "E1466", {"start": v(-43.86, 29.8) * mm, "end": v(-45.86, 29.05) * mm});
            skLineSegment(sketch, "E1467", {"start": v(-45.86, 29.05) * mm, "end": v(-47.6, 28.44) * mm});
            skLineSegment(sketch, "E1468", {"start": v(-47.6, 28.44) * mm, "end": v(-49.4, 27.9) * mm});
            skLineSegment(sketch, "E1469", {"start": v(-49.4, 27.9) * mm, "end": v(-51.48, 27.38) * mm});
            skLineSegment(sketch, "E1470", {"start": v(-51.48, 27.38) * mm, "end": v(-51.7, 27.33) * mm});
            skLineSegment(sketch, "E1471", {"start": v(-51.7, 27.33) * mm, "end": v(-52.2, 27.21) * mm});
            skLineSegment(sketch, "E1472", {"start": v(-52.2, 27.21) * mm, "end": v(-52.7, 27.1) * mm});
            skLineSegment(sketch, "E1473", {"start": v(-52.7, 27.1) * mm, "end": v(-52.92, 27.05) * mm});
            skLineSegment(sketch, "E1474", {"start": v(-52.92, 27.05) * mm, "end": v(-53.42, 27) * mm});
            skLineSegment(sketch, "E1475", {"start": v(-53.42, 27) * mm, "end": v(-54.53, 26.9) * mm});
            skLineSegment(sketch, "E1476", {"start": v(-54.53, 26.9) * mm, "end": v(-55.63, 26.8) * mm});
            skLineSegment(sketch, "E1477", {"start": v(-55.63, 26.8) * mm, "end": v(-56.14, 26.76) * mm});
            skLineSegment(sketch, "E1478", {"start": v(-56.14, 26.76) * mm, "end": v(-56.41, 26.74) * mm});
            skLineSegment(sketch, "E1479", {"start": v(-56.41, 26.74) * mm, "end": v(-57.02, 26.71) * mm});
            skLineSegment(sketch, "E1480", {"start": v(-57.02, 26.71) * mm, "end": v(-57.64, 26.68) * mm});
            skLineSegment(sketch, "E1481", {"start": v(-57.64, 26.68) * mm, "end": v(-57.91, 26.67) * mm});
            skLineSegment(sketch, "E1482", {"start": v(-57.91, 26.67) * mm, "end": v(-58.07, 26.66) * mm});
            skLineSegment(sketch, "E1483", {"start": v(-58.07, 26.66) * mm, "end": v(-58.42, 26.63) * mm});
            skLineSegment(sketch, "E1484", {"start": v(-58.42, 26.63) * mm, "end": v(-58.77, 26.6) * mm});
            skLineSegment(sketch, "E1485", {"start": v(-58.77, 26.6) * mm, "end": v(-58.93, 26.6) * mm});
            skLineSegment(sketch, "E1486", {"start": v(-58.93, 26.6) * mm, "end": v(-59.11, 26.6) * mm});
            skLineSegment(sketch, "E1487", {"start": v(-59.11, 26.6) * mm, "end": v(-59.52, 26.6) * mm});
            skLineSegment(sketch, "E1488", {"start": v(-59.52, 26.6) * mm, "end": v(-59.93, 26.6) * mm});
            skLineSegment(sketch, "E1489", {"start": v(-59.93, 26.6) * mm, "end": v(-60.11, 26.6) * mm});
            skLineSegment(sketch, "E1490", {"start": v(-60.11, 26.6) * mm, "end": v(-60.34, 26.6) * mm});
            skLineSegment(sketch, "E1491", {"start": v(-60.34, 26.6) * mm, "end": v(-60.83, 26.6) * mm});
            skLineSegment(sketch, "E1492", {"start": v(-60.83, 26.6) * mm, "end": v(-61.33, 26.6) * mm});
            skLineSegment(sketch, "E1493", {"start": v(-61.33, 26.6) * mm, "end": v(-61.55, 26.6) * mm});
            skLineSegment(sketch, "E1494", {"start": v(-61.55, 26.6) * mm, "end": v(-61.78, 26.61) * mm});
            skLineSegment(sketch, "E1495", {"start": v(-61.78, 26.61) * mm, "end": v(-62.39, 26.66) * mm});
            skLineSegment(sketch, "E1496", {"start": v(-62.39, 26.66) * mm, "end": v(-63.24, 26.73) * mm});
            skLineSegment(sketch, "E1497", {"start": v(-63.24, 26.73) * mm, "end": v(-64.22, 26.8) * mm});
            skLineSegment(sketch, "E1498", {"start": v(-64.22, 26.8) * mm, "end": v(-65.2, 26.88) * mm});
            skLineSegment(sketch, "E1499", {"start": v(-65.2, 26.88) * mm, "end": v(-66.06, 26.95) * mm});
            skLineSegment(sketch, "E1500", {"start": v(-66.06, 26.95) * mm, "end": v(-66.66, 27) * mm});
            skLineSegment(sketch, "E1501", {"start": v(-66.66, 27) * mm, "end": v(-66.89, 27) * mm});
            skLineSegment(sketch, "E1502", {"start": v(-66.89, 27) * mm, "end": v(-67.02, 25.82) * mm});
            skLineSegment(sketch, "E1503", {"start": v(-67.02, 25.82) * mm, "end": v(-67.44, 25.2) * mm});
            skLineSegment(sketch, "E1504", {"start": v(-67.44, 25.2) * mm, "end": v(-67.95, 24.64) * mm});
            skLineSegment(sketch, "E1505", {"start": v(-67.95, 24.64) * mm, "end": v(-68.73, 23.77) * mm});
            skLineSegment(sketch, "E1506", {"start": v(-68.73, 23.77) * mm, "end": v(-69.23, 23.26) * mm});
            skLineSegment(sketch, "E1507", {"start": v(-69.23, 23.26) * mm, "end": v(-69.77, 22.82) * mm});
            skLineSegment(sketch, "E1508", {"start": v(-69.77, 22.82) * mm, "end": v(-70.61, 22.12) * mm});
            skLineSegment(sketch, "E1509", {"start": v(-70.61, 22.12) * mm, "end": v(-71.15, 21.66) * mm});
            skLineSegment(sketch, "E1510", {"start": v(-71.15, 21.66) * mm, "end": v(-71.56, 21.3) * mm});
            skLineSegment(sketch, "E1511", {"start": v(-71.56, 21.3) * mm, "end": v(-72, 20.99) * mm});
            skLineSegment(sketch, "E1512", {"start": v(-72, 20.99) * mm, "end": v(-72.65, 20.64) * mm});
            skLineSegment(sketch, "E1513", {"start": v(-72.65, 20.64) * mm, "end": v(-73.3, 20.3) * mm});
            skLineSegment(sketch, "E1514", {"start": v(-73.3, 20.3) * mm, "end": v(-73.91, 20.06) * mm});
            skLineSegment(sketch, "E1515", {"start": v(-73.91, 20.06) * mm, "end": v(-74.54, 19.96) * mm});
            skLineSegment(sketch, "E1516", {"start": v(-74.54, 19.96) * mm, "end": v(-75.26, 20.07) * mm});
            skLineSegment(sketch, "E1517", {"start": v(-75.26, 20.07) * mm, "end": v(-75.26, 20.74) * mm});
            skLineSegment(sketch, "E1518", {"start": v(-75.26, 20.74) * mm, "end": v(-74.95, 21.16) * mm});
            skLineSegment(sketch, "E1519", {"start": v(-74.95, 21.16) * mm, "end": v(-74.44, 21.56) * mm});
            skLineSegment(sketch, "E1520", {"start": v(-74.44, 21.56) * mm, "end": v(-73.87, 21.93) * mm});
            skLineSegment(sketch, "E1521", {"start": v(-73.87, 21.93) * mm, "end": v(-73.4, 22.24) * mm});
            skLineSegment(sketch, "E1522", {"start": v(-73.4, 22.24) * mm, "end": v(-73.25, 22.37) * mm});
            skLineSegment(sketch, "E1523", {"start": v(-73.25, 22.37) * mm, "end": v(-72.9, 22.64) * mm});
            skLineSegment(sketch, "E1524", {"start": v(-72.9, 22.64) * mm, "end": v(-72.55, 22.92) * mm});
            skLineSegment(sketch, "E1525", {"start": v(-72.55, 22.92) * mm, "end": v(-72.4, 23.05) * mm});
            skLineSegment(sketch, "E1526", {"start": v(-72.4, 23.05) * mm, "end": v(-71.61, 23.58) * mm});
            skLineSegment(sketch, "E1527", {"start": v(-71.61, 23.58) * mm, "end": v(-70.87, 24.15) * mm});
            skLineSegment(sketch, "E1528", {"start": v(-70.87, 24.15) * mm, "end": v(-70.68, 24.36) * mm});
            skLineSegment(sketch, "E1529", {"start": v(-70.68, 24.36) * mm, "end": v(-70.28, 24.81) * mm});
            skLineSegment(sketch, "E1530", {"start": v(-70.28, 24.81) * mm, "end": v(-69.87, 25.27) * mm});
            skLineSegment(sketch, "E1531", {"start": v(-69.87, 25.27) * mm, "end": v(-69.68, 25.48) * mm});
            skLineSegment(sketch, "E1532", {"start": v(-69.68, 25.48) * mm, "end": v(-69.54, 25.59) * mm});
            skLineSegment(sketch, "E1533", {"start": v(-69.54, 25.59) * mm, "end": v(-69.23, 25.83) * mm});
            skLineSegment(sketch, "E1534", {"start": v(-69.23, 25.83) * mm, "end": v(-68.91, 26.08) * mm});
            skLineSegment(sketch, "E1535", {"start": v(-68.91, 26.08) * mm, "end": v(-68.77, 26.19) * mm});
            skLineSegment(sketch, "E1536", {"start": v(-68.77, 26.19) * mm, "end": v(-68.6, 26.43) * mm});
            skLineSegment(sketch, "E1537", {"start": v(-68.6, 26.43) * mm, "end": v(-68.5, 26.64) * mm});
            skLineSegment(sketch, "E1538", {"start": v(-68.5, 26.64) * mm, "end": v(-68.37, 26.87) * mm});
            skLineSegment(sketch, "E1539", {"start": v(-68.37, 26.87) * mm, "end": v(-68.07, 27.18) * mm});
            skLineSegment(sketch, "E1540", {"start": v(-68.07, 27.18) * mm, "end": v(-68.47, 27.26) * mm});
            skLineSegment(sketch, "E1541", {"start": v(-68.47, 27.26) * mm, "end": v(-69.34, 27.43) * mm});
            skLineSegment(sketch, "E1542", {"start": v(-69.34, 27.43) * mm, "end": v(-70.22, 27.6) * mm});
            skLineSegment(sketch, "E1543", {"start": v(-70.22, 27.6) * mm, "end": v(-70.61, 27.69) * mm});
            skLineSegment(sketch, "E1544", {"start": v(-70.61, 27.69) * mm, "end": v(-70.75, 27.73) * mm});
            skLineSegment(sketch, "E1545", {"start": v(-70.75, 27.73) * mm, "end": v(-71.13, 27.83) * mm});
            skLineSegment(sketch, "E1546", {"start": v(-71.13, 27.83) * mm, "end": v(-71.66, 27.98) * mm});
            skLineSegment(sketch, "E1547", {"start": v(-71.66, 27.98) * mm, "end": v(-72.26, 28.15) * mm});
            skLineSegment(sketch, "E1548", {"start": v(-72.26, 28.15) * mm, "end": v(-72.87, 28.33) * mm});
            skLineSegment(sketch, "E1549", {"start": v(-72.87, 28.33) * mm, "end": v(-73.4, 28.48) * mm});
            skLineSegment(sketch, "E1550", {"start": v(-73.4, 28.48) * mm, "end": v(-73.77, 28.58) * mm});
            skLineSegment(sketch, "E1551", {"start": v(-73.77, 28.58) * mm, "end": v(-73.91, 28.62) * mm});
            skLineSegment(sketch, "E1552", {"start": v(-73.91, 28.62) * mm, "end": v(-75.89, 29.59) * mm});
            skLineSegment(sketch, "E1553", {"start": v(-75.89, 29.59) * mm, "end": v(-77.72, 30.8) * mm});
            skLineSegment(sketch, "E1554", {"start": v(-77.72, 30.8) * mm, "end": v(-79.5, 32.17) * mm});
            skLineSegment(sketch, "E1555", {"start": v(-79.5, 32.17) * mm, "end": v(-80.82, 33.78) * mm});
            skLineSegment(sketch, "E1556", {"start": v(-80.82, 33.78) * mm, "end": v(-81.26, 34.33) * mm});
            skLineSegment(sketch, "E1557", {"start": v(-81.26, 34.33) * mm, "end": v(-81.85, 35.04) * mm});
            skLineSegment(sketch, "E1558", {"start": v(-81.85, 35.04) * mm, "end": v(-82.4, 35.77) * mm});
            skLineSegment(sketch, "E1559", {"start": v(-82.4, 35.77) * mm, "end": v(-82.73, 36.32) * mm});
            skLineSegment(sketch, "E1560", {"start": v(-82.73, 36.32) * mm, "end": v(-82.81, 36.62) * mm});
            skLineSegment(sketch, "E1561", {"start": v(-82.81, 36.62) * mm, "end": v(-82.89, 36.92) * mm});
            skLineSegment(sketch, "E1562", {"start": v(-82.89, 36.92) * mm, "end": v(-82.76, 37.04) * mm});
            skLineSegment(sketch, "E1563", {"start": v(-82.76, 37.04) * mm, "end": v(-82.64, 37.17) * mm});
            skLineSegment(sketch, "E1564", {"start": v(-82.64, 37.17) * mm, "end": v(-82.38, 37.09) * mm});
            skLineSegment(sketch, "E1565", {"start": v(-82.38, 37.09) * mm, "end": v(-82.13, 37) * mm});
            skLineSegment(sketch, "E1566", {"start": v(-34.63, 31.79) * mm, "end": v(-34.31, 31.92) * mm});
            skLineSegment(sketch, "E1567", {"start": v(-34.31, 31.92) * mm, "end": v(-33.61, 32.2) * mm});
            skLineSegment(sketch, "E1568", {"start": v(-33.61, 32.2) * mm, "end": v(-32.92, 32.5) * mm});
            skLineSegment(sketch, "E1569", {"start": v(-32.92, 32.5) * mm, "end": v(-32.6, 32.62) * mm});
            skLineSegment(sketch, "E1570", {"start": v(-32.6, 32.62) * mm, "end": v(-32.37, 32.74) * mm});
            skLineSegment(sketch, "E1571", {"start": v(-32.37, 32.74) * mm, "end": v(-31.88, 33) * mm});
            skLineSegment(sketch, "E1572", {"start": v(-31.88, 33) * mm, "end": v(-31.38, 33.25) * mm});
            skLineSegment(sketch, "E1573", {"start": v(-31.38, 33.25) * mm, "end": v(-31.16, 33.36) * mm});
            skLineSegment(sketch, "E1574", {"start": v(-31.16, 33.36) * mm, "end": v(-30.99, 33.45) * mm});
            skLineSegment(sketch, "E1575", {"start": v(-30.99, 33.45) * mm, "end": v(-30.6, 33.63) * mm});
            skLineSegment(sketch, "E1576", {"start": v(-30.6, 33.63) * mm, "end": v(-30.23, 33.82) * mm});
            skLineSegment(sketch, "E1577", {"start": v(-30.23, 33.82) * mm, "end": v(-30.06, 33.9) * mm});
            skLineSegment(sketch, "E1578", {"start": v(-30.06, 33.9) * mm, "end": v(-29.75, 34.11) * mm});
            skLineSegment(sketch, "E1579", {"start": v(-29.75, 34.11) * mm, "end": v(-29.08, 34.56) * mm});
            skLineSegment(sketch, "E1580", {"start": v(-29.08, 34.56) * mm, "end": v(-28.41, 35.01) * mm});
            skLineSegment(sketch, "E1581", {"start": v(-28.41, 35.01) * mm, "end": v(-28.11, 35.22) * mm});
            skLineSegment(sketch, "E1582", {"start": v(-28.11, 35.22) * mm, "end": v(-27.8, 35.43) * mm});
            skLineSegment(sketch, "E1583", {"start": v(-27.8, 35.43) * mm, "end": v(-27.1, 35.9) * mm});
            skLineSegment(sketch, "E1584", {"start": v(-27.1, 35.9) * mm, "end": v(-26.4, 36.36) * mm});
            skLineSegment(sketch, "E1585", {"start": v(-26.4, 36.36) * mm, "end": v(-26.08, 36.57) * mm});
            skLineSegment(sketch, "E1586", {"start": v(-26.08, 36.57) * mm, "end": v(-25.7, 36.84) * mm});
            skLineSegment(sketch, "E1587", {"start": v(-25.7, 36.84) * mm, "end": v(-25.26, 36.9) * mm});
            skLineSegment(sketch, "E1588", {"start": v(-25.26, 36.9) * mm, "end": v(-25.07, 36.6) * mm});
            skLineSegment(sketch, "E1589", {"start": v(-25.07, 36.6) * mm, "end": v(-25.04, 36.1) * mm});
            skLineSegment(sketch, "E1590", {"start": v(-25.04, 36.1) * mm, "end": v(-25.12, 35.6) * mm});
            skLineSegment(sketch, "E1591", {"start": v(-25.12, 35.6) * mm, "end": v(-25.26, 35.22) * mm});
            skLineSegment(sketch, "E1592", {"start": v(-25.26, 35.22) * mm, "end": v(-25.74, 34.72) * mm});
            skLineSegment(sketch, "E1593", {"start": v(-25.74, 34.72) * mm, "end": v(-26.33, 34.32) * mm});
            skLineSegment(sketch, "E1594", {"start": v(-26.33, 34.32) * mm, "end": v(-26.43, 34.25) * mm});
            skLineSegment(sketch, "E1595", {"start": v(-26.43, 34.25) * mm, "end": v(-26.7, 34.09) * mm});
            skLineSegment(sketch, "E1596", {"start": v(-26.7, 34.09) * mm, "end": v(-27.06, 33.85) * mm});
            skLineSegment(sketch, "E1597", {"start": v(-27.06, 33.85) * mm, "end": v(-27.48, 33.57) * mm});
            skLineSegment(sketch, "E1598", {"start": v(-27.48, 33.57) * mm, "end": v(-27.9, 33.3) * mm});
            skLineSegment(sketch, "E1599", {"start": v(-27.9, 33.3) * mm, "end": v(-28.26, 33.06) * mm});
            skLineSegment(sketch, "E1600", {"start": v(-28.26, 33.06) * mm, "end": v(-28.52, 32.89) * mm});
            skLineSegment(sketch, "E1601", {"start": v(-28.52, 32.89) * mm, "end": v(-28.62, 32.82) * mm});
            skLineSegment(sketch, "E1602", {"start": v(-28.62, 32.82) * mm, "end": v(-28.92, 32.6) * mm});
            skLineSegment(sketch, "E1603", {"start": v(-28.92, 32.6) * mm, "end": v(-29.6, 32.11) * mm});
            skLineSegment(sketch, "E1604", {"start": v(-29.6, 32.11) * mm, "end": v(-30.26, 31.63) * mm});
            skLineSegment(sketch, "E1605", {"start": v(-30.26, 31.63) * mm, "end": v(-30.57, 31.4) * mm});
            skLineSegment(sketch, "E1606", {"start": v(-30.57, 31.4) * mm, "end": v(-30.77, 31.26) * mm});
            skLineSegment(sketch, "E1607", {"start": v(-30.77, 31.26) * mm, "end": v(-31.32, 30.87) * mm});
            skLineSegment(sketch, "E1608", {"start": v(-31.32, 30.87) * mm, "end": v(-32.1, 30.33) * mm});
            skLineSegment(sketch, "E1609", {"start": v(-32.1, 30.33) * mm, "end": v(-32.98, 29.7) * mm});
            skLineSegment(sketch, "E1610", {"start": v(-32.98, 29.7) * mm, "end": v(-33.86, 29.08) * mm});
            skLineSegment(sketch, "E1611", {"start": v(-33.86, 29.08) * mm, "end": v(-34.64, 28.53) * mm});
            skLineSegment(sketch, "E1612", {"start": v(-34.64, 28.53) * mm, "end": v(-35.18, 28.15) * mm});
            skLineSegment(sketch, "E1613", {"start": v(-35.18, 28.15) * mm, "end": v(-35.4, 28) * mm});
            skLineSegment(sketch, "E1614", {"start": v(-35.4, 28) * mm, "end": v(-35.6, 27.89) * mm});
            skLineSegment(sketch, "E1615", {"start": v(-35.6, 27.89) * mm, "end": v(-36.12, 27.58) * mm});
            skLineSegment(sketch, "E1616", {"start": v(-36.12, 27.58) * mm, "end": v(-36.87, 27.16) * mm});
            skLineSegment(sketch, "E1617", {"start": v(-36.87, 27.16) * mm, "end": v(-37.72, 26.67) * mm});
            skLineSegment(sketch, "E1618", {"start": v(-37.72, 26.67) * mm, "end": v(-38.57, 26.18) * mm});
            skLineSegment(sketch, "E1619", {"start": v(-38.57, 26.18) * mm, "end": v(-39.32, 25.75) * mm});
            skLineSegment(sketch, "E1620", {"start": v(-39.32, 25.75) * mm, "end": v(-39.85, 25.45) * mm});
            skLineSegment(sketch, "E1621", {"start": v(-39.85, 25.45) * mm, "end": v(-40.05, 25.34) * mm});
            skLineSegment(sketch, "E1622", {"start": v(-40.05, 25.34) * mm, "end": v(-40.19, 25.27) * mm});
            skLineSegment(sketch, "E1623", {"start": v(-40.19, 25.27) * mm, "end": v(-40.56, 25.09) * mm});
            skLineSegment(sketch, "E1624", {"start": v(-40.56, 25.09) * mm, "end": v(-41.1, 24.83) * mm});
            skLineSegment(sketch, "E1625", {"start": v(-41.1, 24.83) * mm, "end": v(-41.7, 24.53) * mm});
            skLineSegment(sketch, "E1626", {"start": v(-41.7, 24.53) * mm, "end": v(-42.3, 24.24) * mm});
            skLineSegment(sketch, "E1627", {"start": v(-42.3, 24.24) * mm, "end": v(-42.84, 23.98) * mm});
            skLineSegment(sketch, "E1628", {"start": v(-42.84, 23.98) * mm, "end": v(-43.21, 23.8) * mm});
            skLineSegment(sketch, "E1629", {"start": v(-43.21, 23.8) * mm, "end": v(-43.35, 23.73) * mm});
            skLineSegment(sketch, "E1630", {"start": v(-43.35, 23.73) * mm, "end": v(-46.13, 22.58) * mm});
            skLineSegment(sketch, "E1631", {"start": v(-46.13, 22.58) * mm, "end": v(-49.02, 21.78) * mm});
            skLineSegment(sketch, "E1632", {"start": v(-49.02, 21.78) * mm, "end": v(-49.58, 21.67) * mm});
            skLineSegment(sketch, "E1633", {"start": v(-49.58, 21.67) * mm, "end": v(-50.28, 21.62) * mm});
            skLineSegment(sketch, "E1634", {"start": v(-50.28, 21.62) * mm, "end": v(-50.8, 21.79) * mm});
            skLineSegment(sketch, "E1635", {"start": v(-50.8, 21.79) * mm, "end": v(-50.8, 22.35) * mm});
            skLineSegment(sketch, "E1636", {"start": v(-50.8, 22.35) * mm, "end": v(-50.97, 22.35) * mm});
            skLineSegment(sketch, "E1637", {"start": v(-50.97, 22.35) * mm, "end": v(-50.89, 22.56) * mm});
            skLineSegment(sketch, "E1638", {"start": v(-50.89, 22.56) * mm, "end": v(-50.8, 22.78) * mm});
            skLineSegment(sketch, "E1639", {"start": v(-50.8, 22.78) * mm, "end": v(-50.93, 22.73) * mm});
            skLineSegment(sketch, "E1640", {"start": v(-50.93, 22.73) * mm, "end": v(-51.06, 22.7) * mm});
            skLineSegment(sketch, "E1641", {"start": v(-51.06, 22.7) * mm, "end": v(-50.31, 23.37) * mm});
            skLineSegment(sketch, "E1642", {"start": v(-50.31, 23.37) * mm, "end": v(-49.36, 23.75) * mm});
            skLineSegment(sketch, "E1643", {"start": v(-49.36, 23.75) * mm, "end": v(-47.16, 24.87) * mm});
            skLineSegment(sketch, "E1644", {"start": v(-47.16, 24.87) * mm, "end": v(-47.02, 24.96) * mm});
            skLineSegment(sketch, "E1645", {"start": v(-47.02, 24.96) * mm, "end": v(-46.64, 25.2) * mm});
            skLineSegment(sketch, "E1646", {"start": v(-46.64, 25.2) * mm, "end": v(-46.12, 25.53) * mm});
            skLineSegment(sketch, "E1647", {"start": v(-46.12, 25.53) * mm, "end": v(-45.5, 25.92) * mm});
            skLineSegment(sketch, "E1648", {"start": v(-45.5, 25.92) * mm, "end": v(-44.9, 26.3) * mm});
            skLineSegment(sketch, "E1649", {"start": v(-44.9, 26.3) * mm, "end": v(-44.37, 26.65) * mm});
            skLineSegment(sketch, "E1650", {"start": v(-44.37, 26.65) * mm, "end": v(-44, 26.89) * mm});
            skLineSegment(sketch, "E1651", {"start": v(-44, 26.89) * mm, "end": v(-43.86, 26.97) * mm});
            skLineSegment(sketch, "E1652", {"start": v(-43.86, 26.97) * mm, "end": v(-43.51, 27.18) * mm});
            skLineSegment(sketch, "E1653", {"start": v(-43.51, 27.18) * mm, "end": v(-42.76, 27.62) * mm});
            skLineSegment(sketch, "E1654", {"start": v(-42.76, 27.62) * mm, "end": v(-42, 28.07) * mm});
            skLineSegment(sketch, "E1655", {"start": v(-42, 28.07) * mm, "end": v(-41.66, 28.27) * mm});
            skLineSegment(sketch, "E1656", {"start": v(-41.66, 28.27) * mm, "end": v(-41.49, 28.44) * mm});
            skLineSegment(sketch, "E1657", {"start": v(-41.49, 28.44) * mm, "end": v(-41.1, 28.79) * mm});
            skLineSegment(sketch, "E1658", {"start": v(-41.1, 28.79) * mm, "end": v(-40.73, 29.14) * mm});
            skLineSegment(sketch, "E1659", {"start": v(-40.73, 29.14) * mm, "end": v(-40.56, 29.3) * mm});
            skLineSegment(sketch, "E1660", {"start": v(-40.56, 29.3) * mm, "end": v(-40.44, 29.38) * mm});
            skLineSegment(sketch, "E1661", {"start": v(-40.44, 29.38) * mm, "end": v(-40.14, 29.59) * mm});
            skLineSegment(sketch, "E1662", {"start": v(-40.14, 29.59) * mm, "end": v(-39.7, 29.87) * mm});
            skLineSegment(sketch, "E1663", {"start": v(-39.7, 29.87) * mm, "end": v(-39.2, 30.2) * mm});
            skLineSegment(sketch, "E1664", {"start": v(-39.2, 30.2) * mm, "end": v(-38.71, 30.53) * mm});
            skLineSegment(sketch, "E1665", {"start": v(-38.71, 30.53) * mm, "end": v(-38.28, 30.82) * mm});
            skLineSegment(sketch, "E1666", {"start": v(-38.28, 30.82) * mm, "end": v(-37.98, 31.02) * mm});
            skLineSegment(sketch, "E1667", {"start": v(-37.98, 31.02) * mm, "end": v(-37.86, 31.1) * mm});
            skLineSegment(sketch, "E1668", {"start": v(-37.86, 31.1) * mm, "end": v(-37.6, 31.3) * mm});
            skLineSegment(sketch, "E1669", {"start": v(-37.6, 31.3) * mm, "end": v(-37.47, 31.43) * mm});
            skLineSegment(sketch, "E1670", {"start": v(-37.47, 31.43) * mm, "end": v(-37.28, 31.57) * mm});
            skLineSegment(sketch, "E1671", {"start": v(-37.28, 31.57) * mm, "end": v(-36.92, 31.75) * mm});
            skLineSegment(sketch, "E1672", {"start": v(-36.92, 31.75) * mm, "end": v(-36.87, 31.54) * mm});
            skLineSegment(sketch, "E1673", {"start": v(-36.87, 31.54) * mm, "end": v(-36.83, 31.33) * mm});
            skLineSegment(sketch, "E1674", {"start": v(-36.83, 31.33) * mm, "end": v(-36.75, 31.45) * mm});
            skLineSegment(sketch, "E1675", {"start": v(-36.75, 31.45) * mm, "end": v(-36.66, 31.58) * mm});
            skLineSegment(sketch, "E1676", {"start": v(-36.66, 31.58) * mm, "end": v(-36.7, 31.37) * mm});
            skLineSegment(sketch, "E1677", {"start": v(-36.7, 31.37) * mm, "end": v(-36.75, 31.16) * mm});
            skLineSegment(sketch, "E1678", {"start": v(-36.75, 31.16) * mm, "end": v(-36.42, 31.26) * mm});
            skLineSegment(sketch, "E1679", {"start": v(-36.42, 31.26) * mm, "end": v(-35.69, 31.47) * mm});
            skLineSegment(sketch, "E1680", {"start": v(-35.69, 31.47) * mm, "end": v(-34.96, 31.7) * mm});
            skLineSegment(sketch, "E1681", {"start": v(-34.96, 31.7) * mm, "end": v(-34.63, 31.79) * mm});
            skLineSegment(sketch, "E1682", {"start": v(-50.8, 22.86) * mm, "end": v(-50.72, 22.78) * mm});
            skLineSegment(sketch, "E1683", {"start": v(-50.72, 22.78) * mm, "end": v(-50.72, 22.86) * mm});
            skLineSegment(sketch, "E1684", {"start": v(-50.72, 22.86) * mm, "end": v(-50.8, 22.86) * mm});
            skLineSegment(sketch, "E1685", {"start": v(-25.9, 17.83) * mm, "end": v(-25.72, 17.7) * mm});
            skLineSegment(sketch, "E1686", {"start": v(-25.72, 17.7) * mm, "end": v(-25.32, 17.38) * mm});
            skLineSegment(sketch, "E1687", {"start": v(-25.32, 17.38) * mm, "end": v(-24.91, 17.08) * mm});
            skLineSegment(sketch, "E1688", {"start": v(-24.91, 17.08) * mm, "end": v(-24.72, 16.93) * mm});
            skLineSegment(sketch, "E1689", {"start": v(-24.72, 16.93) * mm, "end": v(-24.93, 16.66) * mm});
            skLineSegment(sketch, "E1690", {"start": v(-24.93, 16.66) * mm, "end": v(-25.23, 16.5) * mm});
            skLineSegment(sketch, "E1691", {"start": v(-25.23, 16.5) * mm, "end": v(-25.06, 16.5) * mm});
            skLineSegment(sketch, "E1692", {"start": v(-25.06, 16.5) * mm, "end": v(-25.06, 16.43) * mm});
            skLineSegment(sketch, "E1693", {"start": v(-25.06, 16.43) * mm, "end": v(-25.22, 16.41) * mm});
            skLineSegment(sketch, "E1694", {"start": v(-25.22, 16.41) * mm, "end": v(-25.57, 16.38) * mm});
            skLineSegment(sketch, "E1695", {"start": v(-25.57, 16.38) * mm, "end": v(-25.92, 16.36) * mm});
            skLineSegment(sketch, "E1696", {"start": v(-25.92, 16.36) * mm, "end": v(-26.08, 16.34) * mm});
            skLineSegment(sketch, "E1697", {"start": v(-26.08, 16.34) * mm, "end": v(-27.16, 16.45) * mm});
            skLineSegment(sketch, "E1698", {"start": v(-27.16, 16.45) * mm, "end": v(-28.2, 16.76) * mm});
            skLineSegment(sketch, "E1699", {"start": v(-28.2, 16.76) * mm, "end": v(-28.78, 16.87) * mm});
            skLineSegment(sketch, "E1700", {"start": v(-28.78, 16.87) * mm, "end": v(-29.21, 17.19) * mm});
            skLineSegment(sketch, "E1701", {"start": v(-29.21, 17.19) * mm, "end": v(-29.04, 17.15) * mm});
            skLineSegment(sketch, "E1702", {"start": v(-29.04, 17.15) * mm, "end": v(-28.87, 17.1) * mm});
            skLineSegment(sketch, "E1703", {"start": v(-28.87, 17.1) * mm, "end": v(-28.79, 17.23) * mm});
            skLineSegment(sketch, "E1704", {"start": v(-28.79, 17.23) * mm, "end": v(-28.7, 17.36) * mm});
            skLineSegment(sketch, "E1705", {"start": v(-28.7, 17.36) * mm, "end": v(-28.87, 17.53) * mm});
            skLineSegment(sketch, "E1706", {"start": v(-28.87, 17.53) * mm, "end": v(-29.04, 17.7) * mm});
            skLineSegment(sketch, "E1707", {"start": v(-29.04, 17.7) * mm, "end": v(-28.75, 17.7) * mm});
            skLineSegment(sketch, "E1708", {"start": v(-28.75, 17.7) * mm, "end": v(-28.45, 17.7) * mm});
            skLineSegment(sketch, "E1709", {"start": v(-28.45, 17.7) * mm, "end": v(-28.66, 17.87) * mm});
            skLineSegment(sketch, "E1710", {"start": v(-28.66, 17.87) * mm, "end": v(-28.87, 18.03) * mm});
            skLineSegment(sketch, "E1711", {"start": v(-28.87, 18.03) * mm, "end": v(-28.75, 18.07) * mm});
            skLineSegment(sketch, "E1712", {"start": v(-28.75, 18.07) * mm, "end": v(-28.5, 18.16) * mm});
            skLineSegment(sketch, "E1713", {"start": v(-28.5, 18.16) * mm, "end": v(-28.23, 18.25) * mm});
            skLineSegment(sketch, "E1714", {"start": v(-28.23, 18.25) * mm, "end": v(-28.11, 18.29) * mm});
            skLineSegment(sketch, "E1715", {"start": v(-28.11, 18.29) * mm, "end": v(-27.77, 18.22) * mm});
            skLineSegment(sketch, "E1716", {"start": v(-27.77, 18.22) * mm, "end": v(-27.01, 18.06) * mm});
            skLineSegment(sketch, "E1717", {"start": v(-27.01, 18.06) * mm, "end": v(-26.25, 17.9) * mm});
            skLineSegment(sketch, "E1718", {"start": v(-26.25, 17.9) * mm, "end": v(-25.9, 17.83) * mm});
            skLineSegment(sketch, "E1719", {"start": v(-53.68, 18.07) * mm, "end": v(-53.11, 18.2) * mm});
            skLineSegment(sketch, "E1720", {"start": v(-53.11, 18.2) * mm, "end": v(-52.69, 18.18) * mm});
            skLineSegment(sketch, "E1721", {"start": v(-52.69, 18.18) * mm, "end": v(-52.34, 18.1) * mm});
            skLineSegment(sketch, "E1722", {"start": v(-52.34, 18.1) * mm, "end": v(-51.99, 18.03) * mm});
            skLineSegment(sketch, "E1723", {"start": v(-51.99, 18.03) * mm, "end": v(-51.48, 18.03) * mm});
            skLineSegment(sketch, "E1724", {"start": v(-51.48, 18.03) * mm, "end": v(-50.86, 17.63) * mm});
            skLineSegment(sketch, "E1725", {"start": v(-50.86, 17.63) * mm, "end": v(-50.46, 17.02) * mm});
            skLineSegment(sketch, "E1726", {"start": v(-50.46, 17.02) * mm, "end": v(-50.63, 17.06) * mm});
            skLineSegment(sketch, "E1727", {"start": v(-50.63, 17.06) * mm, "end": v(-50.8, 17.1) * mm});
            skLineSegment(sketch, "E1728", {"start": v(-50.8, 17.1) * mm, "end": v(-50.72, 16.98) * mm});
            skLineSegment(sketch, "E1729", {"start": v(-50.72, 16.98) * mm, "end": v(-50.55, 16.72) * mm});
            skLineSegment(sketch, "E1730", {"start": v(-50.55, 16.72) * mm, "end": v(-50.37, 16.46) * mm});
            skLineSegment(sketch, "E1731", {"start": v(-50.37, 16.46) * mm, "end": v(-50.3, 16.34) * mm});
            skLineSegment(sketch, "E1732", {"start": v(-50.3, 16.34) * mm, "end": v(-50.55, 16.35) * mm});
            skLineSegment(sketch, "E1733", {"start": v(-50.55, 16.35) * mm, "end": v(-51.1, 16.38) * mm});
            skLineSegment(sketch, "E1734", {"start": v(-51.1, 16.38) * mm, "end": v(-51.65, 16.4) * mm});
            skLineSegment(sketch, "E1735", {"start": v(-51.65, 16.4) * mm, "end": v(-51.9, 16.42) * mm});
            skLineSegment(sketch, "E1736", {"start": v(-51.9, 16.42) * mm, "end": v(-52.05, 16.35) * mm});
            skLineSegment(sketch, "E1737", {"start": v(-52.05, 16.35) * mm, "end": v(-52.37, 16.21) * mm});
            skLineSegment(sketch, "E1738", {"start": v(-52.37, 16.21) * mm, "end": v(-52.69, 16.07) * mm});
            skLineSegment(sketch, "E1739", {"start": v(-52.69, 16.07) * mm, "end": v(-52.83, 16) * mm});
            skLineSegment(sketch, "E1740", {"start": v(-52.83, 16) * mm, "end": v(-52.8, 16.13) * mm});
            skLineSegment(sketch, "E1741", {"start": v(-52.8, 16.13) * mm, "end": v(-52.75, 16.26) * mm});
            skLineSegment(sketch, "E1742", {"start": v(-52.75, 16.26) * mm, "end": v(-52.96, 16.17) * mm});
            skLineSegment(sketch, "E1743", {"start": v(-52.96, 16.17) * mm, "end": v(-53.17, 16.09) * mm});
            skLineSegment(sketch, "E1744", {"start": v(-53.17, 16.09) * mm, "end": v(-53.17, 16.17) * mm});
            skLineSegment(sketch, "E1745", {"start": v(-53.17, 16.17) * mm, "end": v(-53.09, 16.26) * mm});
            skLineSegment(sketch, "E1746", {"start": v(-53.09, 16.26) * mm, "end": v(-53, 16.34) * mm});
            skLineSegment(sketch, "E1747", {"start": v(-53, 16.34) * mm, "end": v(-53.38, 16.3) * mm});
            skLineSegment(sketch, "E1748", {"start": v(-53.38, 16.3) * mm, "end": v(-53.76, 16.26) * mm});
            skLineSegment(sketch, "E1749", {"start": v(-53.76, 16.26) * mm, "end": v(-53.72, 16.38) * mm});
            skLineSegment(sketch, "E1750", {"start": v(-53.72, 16.38) * mm, "end": v(-53.68, 16.5) * mm});
            skLineSegment(sketch, "E1751", {"start": v(-53.68, 16.5) * mm, "end": v(-54.31, 16.42) * mm});
            skLineSegment(sketch, "E1752", {"start": v(-54.31, 16.42) * mm, "end": v(-54.95, 16.5) * mm});
            skLineSegment(sketch, "E1753", {"start": v(-54.95, 16.5) * mm, "end": v(-54.78, 16.68) * mm});
            skLineSegment(sketch, "E1754", {"start": v(-54.78, 16.68) * mm, "end": v(-54.61, 16.85) * mm});
            skLineSegment(sketch, "E1755", {"start": v(-54.61, 16.85) * mm, "end": v(-54.64, 17.23) * mm});
            skLineSegment(sketch, "E1756", {"start": v(-54.64, 17.23) * mm, "end": v(-54.41, 17.6) * mm});
            skLineSegment(sketch, "E1757", {"start": v(-54.41, 17.6) * mm, "end": v(-54.05, 17.9) * mm});
            skLineSegment(sketch, "E1758", {"start": v(-54.05, 17.9) * mm, "end": v(-53.68, 18.07) * mm});
            skLineSegment(sketch, "E1759", {"start": v(-54.7, 16.6) * mm, "end": v(-54.61, 16.5) * mm});
            skLineSegment(sketch, "E1760", {"start": v(-54.61, 16.5) * mm, "end": v(-54.61, 16.6) * mm});
            skLineSegment(sketch, "E1761", {"start": v(-54.61, 16.6) * mm, "end": v(-54.7, 16.6) * mm});
            skLineSegment(sketch, "E1762", {"start": v(-25.82, 15.58) * mm, "end": v(-25.9, 15.5) * mm});
            skLineSegment(sketch, "E1763", {"start": v(-25.9, 15.5) * mm, "end": v(-25.9, 15.58) * mm});
            skLineSegment(sketch, "E1764", {"start": v(-25.9, 15.58) * mm, "end": v(-25.82, 15.58) * mm});
            skLineSegment(sketch, "E1765", {"start": v(-17.1, 14.14) * mm, "end": v(-17.13, 13.95) * mm});
            skLineSegment(sketch, "E1766", {"start": v(-17.13, 13.95) * mm, "end": v(-17.2, 13.55) * mm});
            skLineSegment(sketch, "E1767", {"start": v(-17.2, 13.55) * mm, "end": v(-17.25, 13.14) * mm});
            skLineSegment(sketch, "E1768", {"start": v(-17.25, 13.14) * mm, "end": v(-17.28, 12.95) * mm});
            skLineSegment(sketch, "E1769", {"start": v(-17.28, 12.95) * mm, "end": v(-17.28, 12.53) * mm});
            skLineSegment(sketch, "E1770", {"start": v(-17.28, 12.53) * mm, "end": v(-17.28, 12.1) * mm});
            skLineSegment(sketch, "E1771", {"start": v(-17.28, 12.1) * mm, "end": v(-17.32, 11.78) * mm});
            skLineSegment(sketch, "E1772", {"start": v(-17.32, 11.78) * mm, "end": v(-17.4, 11.05) * mm});
            skLineSegment(sketch, "E1773", {"start": v(-17.4, 11.05) * mm, "end": v(-17.49, 10.32) * mm});
            skLineSegment(sketch, "E1774", {"start": v(-17.49, 10.32) * mm, "end": v(-17.53, 10) * mm});
            skLineSegment(sketch, "E1775", {"start": v(-17.53, 10) * mm, "end": v(-17.57, 9.57) * mm});
            skLineSegment(sketch, "E1776", {"start": v(-17.57, 9.57) * mm, "end": v(-17.65, 8.64) * mm});
            skLineSegment(sketch, "E1777", {"start": v(-17.65, 8.64) * mm, "end": v(-17.74, 7.7) * mm});
            skLineSegment(sketch, "E1778", {"start": v(-17.74, 7.7) * mm, "end": v(-17.78, 7.28) * mm});
            skLineSegment(sketch, "E1779", {"start": v(-17.78, 7.28) * mm, "end": v(-17.32, 7.7) * mm});
            skLineSegment(sketch, "E1780", {"start": v(-17.32, 7.7) * mm, "end": v(-16.95, 8.21) * mm});
            skLineSegment(sketch, "E1781", {"start": v(-16.95, 8.21) * mm, "end": v(-16.65, 8.65) * mm});
            skLineSegment(sketch, "E1782", {"start": v(-16.65, 8.65) * mm, "end": v(-16.32, 9.19) * mm});
            skLineSegment(sketch, "E1783", {"start": v(-16.32, 9.19) * mm, "end": v(-16.06, 9.75) * mm});
            skLineSegment(sketch, "E1784", {"start": v(-16.06, 9.75) * mm, "end": v(-15.93, 10.25) * mm});
            skLineSegment(sketch, "E1785", {"start": v(-15.93, 10.25) * mm, "end": v(-16.03, 11.02) * mm});
            skLineSegment(sketch, "E1786", {"start": v(-16.03, 11.02) * mm, "end": v(-16.28, 11.77) * mm});
            skLineSegment(sketch, "E1787", {"start": v(-16.28, 11.77) * mm, "end": v(-16.67, 12.95) * mm});
            skLineSegment(sketch, "E1788", {"start": v(-16.67, 12.95) * mm, "end": v(-16.93, 14.14) * mm});
            skLineSegment(sketch, "E1789", {"start": v(-16.93, 14.14) * mm, "end": v(-17.1, 14.14) * mm});
            skLineSegment(sketch, "E1790", {"start": v(-54.7, 9.8) * mm, "end": v(-53.86, 10.58) * mm});
            skLineSegment(sketch, "E1791", {"start": v(-53.86, 10.58) * mm, "end": v(-52.83, 11.03) * mm});
            skLineSegment(sketch, "E1792", {"start": v(-52.83, 11.03) * mm, "end": v(-52.05, 11.4) * mm});
            skLineSegment(sketch, "E1793", {"start": v(-52.05, 11.4) * mm, "end": v(-51.22, 11.63) * mm});
            skLineSegment(sketch, "E1794", {"start": v(-51.22, 11.63) * mm, "end": v(-50.55, 11.63) * mm});
            skLineSegment(sketch, "E1795", {"start": v(-50.55, 11.63) * mm, "end": v(-49.86, 11.53) * mm});
            skLineSegment(sketch, "E1796", {"start": v(-49.86, 11.53) * mm, "end": v(-49.29, 11.36) * mm});
            skLineSegment(sketch, "E1797", {"start": v(-49.29, 11.36) * mm, "end": v(-48.75, 11.1) * mm});
            skLineSegment(sketch, "E1798", {"start": v(-48.75, 11.1) * mm, "end": v(-48.18, 10.7) * mm});
            skLineSegment(sketch, "E1799", {"start": v(-48.18, 10.7) * mm, "end": v(-47.7, 10.25) * mm});
            skLineSegment(sketch, "E1800", {"start": v(-47.7, 10.25) * mm, "end": v(-47.5, 9.65) * mm});
            skLineSegment(sketch, "E1801", {"start": v(-47.5, 9.65) * mm, "end": v(-47.58, 9.76) * mm});
            skLineSegment(sketch, "E1802", {"start": v(-47.58, 9.76) * mm, "end": v(-47.75, 10) * mm});
            skLineSegment(sketch, "E1803", {"start": v(-47.75, 10) * mm, "end": v(-47.93, 10.22) * mm});
            skLineSegment(sketch, "E1804", {"start": v(-47.93, 10.22) * mm, "end": v(-48, 10.33) * mm});
            skLineSegment(sketch, "E1805", {"start": v(-48, 10.33) * mm, "end": v(-47.68, 9.67) * mm});
            skLineSegment(sketch, "E1806", {"start": v(-47.68, 9.67) * mm, "end": v(-47.5, 8.97) * mm});
            skLineSegment(sketch, "E1807", {"start": v(-47.5, 8.97) * mm, "end": v(-47.75, 9.5) * mm});
            skLineSegment(sketch, "E1808", {"start": v(-47.75, 9.5) * mm, "end": v(-47.97, 9.9) * mm});
            skLineSegment(sketch, "E1809", {"start": v(-47.97, 9.9) * mm, "end": v(-48.27, 10.23) * mm});
            skLineSegment(sketch, "E1810", {"start": v(-48.27, 10.23) * mm, "end": v(-48.77, 10.58) * mm});
            skLineSegment(sketch, "E1811", {"start": v(-48.77, 10.58) * mm, "end": v(-48.2, 10.02) * mm});
            skLineSegment(sketch, "E1812", {"start": v(-48.2, 10.02) * mm, "end": v(-47.92, 9.31) * mm});
            skLineSegment(sketch, "E1813", {"start": v(-47.92, 9.31) * mm, "end": v(-48.1, 9.57) * mm});
            skLineSegment(sketch, "E1814", {"start": v(-48.1, 9.57) * mm, "end": v(-48.26, 9.82) * mm});
            skLineSegment(sketch, "E1815", {"start": v(-48.26, 9.82) * mm, "end": v(-47.88, 9.01) * mm});
            skLineSegment(sketch, "E1816", {"start": v(-47.88, 9.01) * mm, "end": v(-47.68, 8.4) * mm});
            skLineSegment(sketch, "E1817", {"start": v(-47.68, 8.4) * mm, "end": v(-47.57, 7.79) * mm});
            skLineSegment(sketch, "E1818", {"start": v(-47.57, 7.79) * mm, "end": v(-47.47, 6.94) * mm});
            skLineSegment(sketch, "E1819", {"start": v(-47.47, 6.94) * mm, "end": v(-47.45, 6.81) * mm});
            skLineSegment(sketch, "E1820", {"start": v(-47.45, 6.81) * mm, "end": v(-47.41, 6.52) * mm});
            skLineSegment(sketch, "E1821", {"start": v(-47.41, 6.52) * mm, "end": v(-47.37, 6.23) * mm});
            skLineSegment(sketch, "E1822", {"start": v(-47.37, 6.23) * mm, "end": v(-47.35, 6.1) * mm});
            skLineSegment(sketch, "E1823", {"start": v(-47.35, 6.1) * mm, "end": v(-47.4, 5.7) * mm});
            skLineSegment(sketch, "E1824", {"start": v(-47.4, 5.7) * mm, "end": v(-47.41, 5.25) * mm});
            skLineSegment(sketch, "E1825", {"start": v(-47.41, 5.25) * mm, "end": v(-47.29, 5.46) * mm});
            skLineSegment(sketch, "E1826", {"start": v(-47.29, 5.46) * mm, "end": v(-47.16, 5.67) * mm});
            skLineSegment(sketch, "E1827", {"start": v(-47.16, 5.67) * mm, "end": v(-47.33, 5.18) * mm});
            skLineSegment(sketch, "E1828", {"start": v(-47.33, 5.18) * mm, "end": v(-47.58, 4.74) * mm});
            skLineSegment(sketch, "E1829", {"start": v(-47.58, 4.74) * mm, "end": v(-47.63, 4.64) * mm});
            skLineSegment(sketch, "E1830", {"start": v(-47.63, 4.64) * mm, "end": v(-47.74, 4.4) * mm});
            skLineSegment(sketch, "E1831", {"start": v(-47.74, 4.4) * mm, "end": v(-47.85, 4.17) * mm});
            skLineSegment(sketch, "E1832", {"start": v(-47.85, 4.17) * mm, "end": v(-47.9, 4.06) * mm});
            skLineSegment(sketch, "E1833", {"start": v(-47.9, 4.06) * mm, "end": v(-48.27, 3.63) * mm});
            skLineSegment(sketch, "E1834", {"start": v(-48.27, 3.63) * mm, "end": v(-48.68, 3.22) * mm});
            skLineSegment(sketch, "E1835", {"start": v(-48.68, 3.22) * mm, "end": v(-49.3, 2.54) * mm});
            skLineSegment(sketch, "E1836", {"start": v(-49.3, 2.54) * mm, "end": v(-50.04, 2) * mm});
            skLineSegment(sketch, "E1837", {"start": v(-50.04, 2) * mm, "end": v(-50.97, 1.76) * mm});
            skLineSegment(sketch, "E1838", {"start": v(-50.97, 1.76) * mm, "end": v(-51.61, 1.67) * mm});
            skLineSegment(sketch, "E1839", {"start": v(-51.61, 1.67) * mm, "end": v(-52.22, 1.66) * mm});
            skLineSegment(sketch, "E1840", {"start": v(-52.22, 1.66) * mm, "end": v(-52.33, 1.76) * mm});
            skLineSegment(sketch, "E1841", {"start": v(-52.33, 1.76) * mm, "end": v(-52.57, 1.97) * mm});
            skLineSegment(sketch, "E1842", {"start": v(-52.57, 1.97) * mm, "end": v(-52.8, 2.2) * mm});
            skLineSegment(sketch, "E1843", {"start": v(-52.8, 2.2) * mm, "end": v(-52.92, 2.29) * mm});
            skLineSegment(sketch, "E1844", {"start": v(-52.92, 2.29) * mm, "end": v(-52.88, 2.46) * mm});
            skLineSegment(sketch, "E1845", {"start": v(-52.88, 2.46) * mm, "end": v(-52.83, 2.62) * mm});
            skLineSegment(sketch, "E1846", {"start": v(-52.83, 2.62) * mm, "end": v(-52.96, 2.67) * mm});
            skLineSegment(sketch, "E1847", {"start": v(-52.96, 2.67) * mm, "end": v(-53.09, 2.7) * mm});
            skLineSegment(sketch, "E1848", {"start": v(-53.09, 2.7) * mm, "end": v(-52.96, 2.84) * mm});
            skLineSegment(sketch, "E1849", {"start": v(-52.96, 2.84) * mm, "end": v(-52.83, 2.96) * mm});
            skLineSegment(sketch, "E1850", {"start": v(-52.83, 2.96) * mm, "end": v(-53.02, 3.55) * mm});
            skLineSegment(sketch, "E1851", {"start": v(-53.02, 3.55) * mm, "end": v(-52.98, 3.92) * mm});
            skLineSegment(sketch, "E1852", {"start": v(-52.98, 3.92) * mm, "end": v(-52.84, 4.22) * mm});
            skLineSegment(sketch, "E1853", {"start": v(-52.84, 4.22) * mm, "end": v(-52.71, 4.57) * mm});
            skLineSegment(sketch, "E1854", {"start": v(-52.71, 4.57) * mm, "end": v(-52.72, 4.78) * mm});
            skLineSegment(sketch, "E1855", {"start": v(-52.72, 4.78) * mm, "end": v(-52.74, 5) * mm});
            skLineSegment(sketch, "E1856", {"start": v(-52.74, 5) * mm, "end": v(-52.68, 5.25) * mm});
            skLineSegment(sketch, "E1857", {"start": v(-52.68, 5.25) * mm, "end": v(-52.46, 5.58) * mm});
            skLineSegment(sketch, "E1858", {"start": v(-52.46, 5.58) * mm, "end": v(-52.07, 5.85) * mm});
            skLineSegment(sketch, "E1859", {"start": v(-52.07, 5.85) * mm, "end": v(-51.77, 5.8) * mm});
            skLineSegment(sketch, "E1860", {"start": v(-51.77, 5.8) * mm, "end": v(-51.48, 5.65) * mm});
            skLineSegment(sketch, "E1861", {"start": v(-51.48, 5.65) * mm, "end": v(-50.6, 5.4) * mm});
            skLineSegment(sketch, "E1862", {"start": v(-50.6, 5.4) * mm, "end": v(-49.85, 5.84) * mm});
            skLineSegment(sketch, "E1863", {"start": v(-49.85, 5.84) * mm, "end": v(-49.6, 6.27) * mm});
            skLineSegment(sketch, "E1864", {"start": v(-49.6, 6.27) * mm, "end": v(-49.63, 6.93) * mm});
            skLineSegment(sketch, "E1865", {"start": v(-49.63, 6.93) * mm, "end": v(-49.94, 7.54) * mm});
            skLineSegment(sketch, "E1866", {"start": v(-49.94, 7.54) * mm, "end": v(-50.42, 8.29) * mm});
            skLineSegment(sketch, "E1867", {"start": v(-50.42, 8.29) * mm, "end": v(-50.88, 8.71) * mm});
            skLineSegment(sketch, "E1868", {"start": v(-50.88, 8.71) * mm, "end": v(-51.43, 9.03) * mm});
            skLineSegment(sketch, "E1869", {"start": v(-51.43, 9.03) * mm, "end": v(-52.05, 9.2) * mm});
            skLineSegment(sketch, "E1870", {"start": v(-52.05, 9.2) * mm, "end": v(-52.66, 9.14) * mm});
            skLineSegment(sketch, "E1871", {"start": v(-52.66, 9.14) * mm, "end": v(-52.5, 9.06) * mm});
            skLineSegment(sketch, "E1872", {"start": v(-52.5, 9.06) * mm, "end": v(-52.32, 8.97) * mm});
            skLineSegment(sketch, "E1873", {"start": v(-52.32, 8.97) * mm, "end": v(-53.03, 8.83) * mm});
            skLineSegment(sketch, "E1874", {"start": v(-53.03, 8.83) * mm, "end": v(-53.43, 8.3) * mm});
            skLineSegment(sketch, "E1875", {"start": v(-53.43, 8.3) * mm, "end": v(-53.95, 8) * mm});
            skLineSegment(sketch, "E1876", {"start": v(-53.95, 8) * mm, "end": v(-54.36, 7.54) * mm});
            skLineSegment(sketch, "E1877", {"start": v(-54.36, 7.54) * mm, "end": v(-54.48, 7.62) * mm});
            skLineSegment(sketch, "E1878", {"start": v(-54.48, 7.62) * mm, "end": v(-54.61, 7.7) * mm});
            skLineSegment(sketch, "E1879", {"start": v(-54.61, 7.7) * mm, "end": v(-54.7, 7.4) * mm});
            skLineSegment(sketch, "E1880", {"start": v(-54.7, 7.4) * mm, "end": v(-54.78, 7.11) * mm});
            skLineSegment(sketch, "E1881", {"start": v(-54.78, 7.11) * mm, "end": v(-54.86, 7.11) * mm});
            skLineSegment(sketch, "E1882", {"start": v(-54.86, 7.11) * mm, "end": v(-54.95, 7.2) * mm});
            skLineSegment(sketch, "E1883", {"start": v(-54.95, 7.2) * mm, "end": v(-55.03, 7.28) * mm});
            skLineSegment(sketch, "E1884", {"start": v(-55.03, 7.28) * mm, "end": v(-55.08, 7.07) * mm});
            skLineSegment(sketch, "E1885", {"start": v(-55.08, 7.07) * mm, "end": v(-55.12, 6.86) * mm});
            skLineSegment(sketch, "E1886", {"start": v(-55.12, 6.86) * mm, "end": v(-55.24, 7.22) * mm});
            skLineSegment(sketch, "E1887", {"start": v(-55.24, 7.22) * mm, "end": v(-55.54, 7.45) * mm});
            skLineSegment(sketch, "E1888", {"start": v(-55.54, 7.45) * mm, "end": v(-55.38, 8) * mm});
            skLineSegment(sketch, "E1889", {"start": v(-55.38, 8) * mm, "end": v(-55.17, 8.68) * mm});
            skLineSegment(sketch, "E1890", {"start": v(-55.17, 8.68) * mm, "end": v(-54.93, 9.34) * mm});
            skLineSegment(sketch, "E1891", {"start": v(-54.93, 9.34) * mm, "end": v(-54.7, 9.8) * mm});
            skLineSegment(sketch, "E1892", {"start": v(-25.3, 8.8) * mm, "end": v(-25.09, 7.63) * mm});
            skLineSegment(sketch, "E1893", {"start": v(-25.09, 7.63) * mm, "end": v(-25.1, 6.43) * mm});
            skLineSegment(sketch, "E1894", {"start": v(-25.1, 6.43) * mm, "end": v(-25.32, 5.83) * mm});
            skLineSegment(sketch, "E1895", {"start": v(-25.32, 5.83) * mm, "end": v(-25.47, 5.43) * mm});
            skLineSegment(sketch, "E1896", {"start": v(-25.47, 5.43) * mm, "end": v(-25.38, 5.16) * mm});
            skLineSegment(sketch, "E1897", {"start": v(-25.38, 5.16) * mm, "end": v(-25.18, 4.81) * mm});
            skLineSegment(sketch, "E1898", {"start": v(-25.18, 4.81) * mm, "end": v(-25.05, 4.42) * mm});
            skLineSegment(sketch, "E1899", {"start": v(-25.05, 4.42) * mm, "end": v(-25.15, 3.98) * mm});
            skLineSegment(sketch, "E1900", {"start": v(-25.15, 3.98) * mm, "end": v(-26.1, 3.06) * mm});
            skLineSegment(sketch, "E1901", {"start": v(-26.1, 3.06) * mm, "end": v(-27.43, 2.68) * mm});
            skLineSegment(sketch, "E1902", {"start": v(-27.43, 2.68) * mm, "end": v(-28.86, 2.73) * mm});
            skLineSegment(sketch, "E1903", {"start": v(-28.86, 2.73) * mm, "end": v(-30.13, 3.13) * mm});
            skLineSegment(sketch, "E1904", {"start": v(-30.13, 3.13) * mm, "end": v(-30.4, 3.3) * mm});
            skLineSegment(sketch, "E1905", {"start": v(-30.4, 3.3) * mm, "end": v(-30.65, 3.48) * mm});
            skLineSegment(sketch, "E1906", {"start": v(-30.65, 3.48) * mm, "end": v(-31.23, 3.79) * mm});
            skLineSegment(sketch, "E1907", {"start": v(-31.23, 3.79) * mm, "end": v(-31.75, 4.23) * mm});
            skLineSegment(sketch, "E1908", {"start": v(-31.75, 4.23) * mm, "end": v(-31.67, 4.2) * mm});
            skLineSegment(sketch, "E1909", {"start": v(-31.67, 4.2) * mm, "end": v(-31.58, 4.15) * mm});
            skLineSegment(sketch, "E1910", {"start": v(-31.58, 4.15) * mm, "end": v(-31.63, 4.25) * mm});
            skLineSegment(sketch, "E1911", {"start": v(-31.63, 4.25) * mm, "end": v(-31.75, 4.49) * mm});
            skLineSegment(sketch, "E1912", {"start": v(-31.75, 4.49) * mm, "end": v(-31.87, 4.72) * mm});
            skLineSegment(sketch, "E1913", {"start": v(-31.87, 4.72) * mm, "end": v(-31.92, 4.83) * mm});
            skLineSegment(sketch, "E1914", {"start": v(-31.92, 4.83) * mm, "end": v(-31.7, 4.7) * mm});
            skLineSegment(sketch, "E1915", {"start": v(-31.7, 4.7) * mm, "end": v(-31.5, 4.57) * mm});
            skLineSegment(sketch, "E1916", {"start": v(-31.5, 4.57) * mm, "end": v(-31.63, 5) * mm});
            skLineSegment(sketch, "E1917", {"start": v(-31.63, 5) * mm, "end": v(-31.58, 5.42) * mm});
            skLineSegment(sketch, "E1918", {"start": v(-31.58, 5.42) * mm, "end": v(-31.45, 5.34) * mm});
            skLineSegment(sketch, "E1919", {"start": v(-31.45, 5.34) * mm, "end": v(-31.33, 5.25) * mm});
            skLineSegment(sketch, "E1920", {"start": v(-31.33, 5.25) * mm, "end": v(-31.04, 5.1) * mm});
            skLineSegment(sketch, "E1921", {"start": v(-31.04, 5.1) * mm, "end": v(-30.74, 5.25) * mm});
            skLineSegment(sketch, "E1922", {"start": v(-30.74, 5.25) * mm, "end": v(-30.64, 5.17) * mm});
            skLineSegment(sketch, "E1923", {"start": v(-30.64, 5.17) * mm, "end": v(-30.44, 5) * mm});
            skLineSegment(sketch, "E1924", {"start": v(-30.44, 5) * mm, "end": v(-30.24, 4.82) * mm});
            skLineSegment(sketch, "E1925", {"start": v(-30.24, 4.82) * mm, "end": v(-30.14, 4.74) * mm});
            skLineSegment(sketch, "E1926", {"start": v(-30.14, 4.74) * mm, "end": v(-30.06, 4.83) * mm});
            skLineSegment(sketch, "E1927", {"start": v(-30.06, 4.83) * mm, "end": v(-30.14, 5.04) * mm});
            skLineSegment(sketch, "E1928", {"start": v(-30.14, 5.04) * mm, "end": v(-30.23, 5.25) * mm});
            skLineSegment(sketch, "E1929", {"start": v(-30.23, 5.25) * mm, "end": v(-30.1, 5.12) * mm});
            skLineSegment(sketch, "E1930", {"start": v(-30.1, 5.12) * mm, "end": v(-29.97, 5) * mm});
            skLineSegment(sketch, "E1931", {"start": v(-29.97, 5) * mm, "end": v(-29.3, 5.15) * mm});
            skLineSegment(sketch, "E1932", {"start": v(-29.3, 5.15) * mm, "end": v(-28.72, 5.37) * mm});
            skLineSegment(sketch, "E1933", {"start": v(-28.72, 5.37) * mm, "end": v(-28.4, 5.8) * mm});
            skLineSegment(sketch, "E1934", {"start": v(-28.4, 5.8) * mm, "end": v(-28.14, 6.43) * mm});
            skLineSegment(sketch, "E1935", {"start": v(-28.14, 6.43) * mm, "end": v(-28, 7.09) * mm});
            skLineSegment(sketch, "E1936", {"start": v(-28, 7.09) * mm, "end": v(-28, 7.62) * mm});
            skLineSegment(sketch, "E1937", {"start": v(-28, 7.62) * mm, "end": v(-28.17, 7.97) * mm});
            skLineSegment(sketch, "E1938", {"start": v(-28.17, 7.97) * mm, "end": v(-28.4, 8.3) * mm});
            skLineSegment(sketch, "E1939", {"start": v(-28.4, 8.3) * mm, "end": v(-28.96, 8.73) * mm});
            skLineSegment(sketch, "E1940", {"start": v(-28.96, 8.73) * mm, "end": v(-29.38, 8.73) * mm});
            skLineSegment(sketch, "E1941", {"start": v(-29.38, 8.73) * mm, "end": v(-29.93, 8.68) * mm});
            skLineSegment(sketch, "E1942", {"start": v(-29.93, 8.68) * mm, "end": v(-30.24, 8.6) * mm});
            skLineSegment(sketch, "E1943", {"start": v(-30.24, 8.6) * mm, "end": v(-30.52, 8.49) * mm});
            skLineSegment(sketch, "E1944", {"start": v(-30.52, 8.49) * mm, "end": v(-30.99, 8.3) * mm});
            skLineSegment(sketch, "E1945", {"start": v(-30.99, 8.3) * mm, "end": v(-30.95, 8.38) * mm});
            skLineSegment(sketch, "E1946", {"start": v(-30.95, 8.38) * mm, "end": v(-30.9, 8.47) * mm});
            skLineSegment(sketch, "E1947", {"start": v(-30.9, 8.47) * mm, "end": v(-31.07, 8.3) * mm});
            skLineSegment(sketch, "E1948", {"start": v(-31.07, 8.3) * mm, "end": v(-31.24, 8.13) * mm});
            skLineSegment(sketch, "E1949", {"start": v(-31.24, 8.13) * mm, "end": v(-31.46, 8.09) * mm});
            skLineSegment(sketch, "E1950", {"start": v(-31.46, 8.09) * mm, "end": v(-31.67, 8.04) * mm});
            skLineSegment(sketch, "E1951", {"start": v(-31.67, 8.04) * mm, "end": v(-31.62, 8.21) * mm});
            skLineSegment(sketch, "E1952", {"start": v(-31.62, 8.21) * mm, "end": v(-31.58, 8.38) * mm});
            skLineSegment(sketch, "E1953", {"start": v(-31.58, 8.38) * mm, "end": v(-31.66, 8.3) * mm});
            skLineSegment(sketch, "E1954", {"start": v(-31.66, 8.3) * mm, "end": v(-31.84, 8.13) * mm});
            skLineSegment(sketch, "E1955", {"start": v(-31.84, 8.13) * mm, "end": v(-32.01, 7.96) * mm});
            skLineSegment(sketch, "E1956", {"start": v(-32.01, 7.96) * mm, "end": v(-32.09, 7.88) * mm});
            skLineSegment(sketch, "E1957", {"start": v(-32.09, 7.88) * mm, "end": v(-32.22, 7.96) * mm});
            skLineSegment(sketch, "E1958", {"start": v(-32.22, 7.96) * mm, "end": v(-32.34, 8.04) * mm});
            skLineSegment(sketch, "E1959", {"start": v(-32.34, 8.04) * mm, "end": v(-32.43, 7.92) * mm});
            skLineSegment(sketch, "E1960", {"start": v(-32.43, 7.92) * mm, "end": v(-32.51, 7.79) * mm});
            skLineSegment(sketch, "E1961", {"start": v(-32.51, 7.79) * mm, "end": v(-32.2, 8.53) * mm});
            skLineSegment(sketch, "E1962", {"start": v(-32.2, 8.53) * mm, "end": v(-31.77, 9.03) * mm});
            skLineSegment(sketch, "E1963", {"start": v(-31.77, 9.03) * mm, "end": v(-31.27, 9.46) * mm});
            skLineSegment(sketch, "E1964", {"start": v(-31.27, 9.46) * mm, "end": v(-30.74, 10) * mm});
            skLineSegment(sketch, "E1965", {"start": v(-30.74, 10) * mm, "end": v(-31, 9.9) * mm});
            skLineSegment(sketch, "E1966", {"start": v(-31, 9.9) * mm, "end": v(-31.24, 9.82) * mm});
            skLineSegment(sketch, "E1967", {"start": v(-31.24, 9.82) * mm, "end": v(-30.89, 10.14) * mm});
            skLineSegment(sketch, "E1968", {"start": v(-30.89, 10.14) * mm, "end": v(-30.4, 10.33) * mm});
            skLineSegment(sketch, "E1969", {"start": v(-30.4, 10.33) * mm, "end": v(-30.65, 10.33) * mm});
            skLineSegment(sketch, "E1970", {"start": v(-30.65, 10.33) * mm, "end": v(-30.9, 10.33) * mm});
            skLineSegment(sketch, "E1971", {"start": v(-30.9, 10.33) * mm, "end": v(-30.21, 10.49) * mm});
            skLineSegment(sketch, "E1972", {"start": v(-30.21, 10.49) * mm, "end": v(-29.42, 10.58) * mm});
            skLineSegment(sketch, "E1973", {"start": v(-29.42, 10.58) * mm, "end": v(-28.58, 10.6) * mm});
            skLineSegment(sketch, "E1974", {"start": v(-28.58, 10.6) * mm, "end": v(-27.73, 10.5) * mm});
            skLineSegment(sketch, "E1975", {"start": v(-27.73, 10.5) * mm, "end": v(-26.92, 10.3) * mm});
            skLineSegment(sketch, "E1976", {"start": v(-26.92, 10.3) * mm, "end": v(-26.22, 9.97) * mm});
            skLineSegment(sketch, "E1977", {"start": v(-26.22, 9.97) * mm, "end": v(-25.66, 9.47) * mm});
            skLineSegment(sketch, "E1978", {"start": v(-25.66, 9.47) * mm, "end": v(-25.3, 8.8) * mm});
            skLineSegment(sketch, "E1979", {"start": v(-27.26, 10) * mm, "end": v(-27.18, 9.9) * mm});
            skLineSegment(sketch, "E1980", {"start": v(-27.18, 9.9) * mm, "end": v(-27.18, 10) * mm});
            skLineSegment(sketch, "E1981", {"start": v(-27.18, 10) * mm, "end": v(-27.26, 10) * mm});
            skLineSegment(sketch, "E1982", {"start": v(-27.69, 9.9) * mm, "end": v(-27.6, 9.82) * mm});
            skLineSegment(sketch, "E1983", {"start": v(-27.6, 9.82) * mm, "end": v(-27.6, 9.9) * mm});
            skLineSegment(sketch, "E1984", {"start": v(-27.6, 9.9) * mm, "end": v(-27.69, 9.9) * mm});
            skLineSegment(sketch, "E1985", {"start": v(-26.16, 8.72) * mm, "end": v(-26.49, 9.43) * mm});
            skLineSegment(sketch, "E1986", {"start": v(-26.49, 9.43) * mm, "end": v(-27.1, 9.9) * mm});
            skLineSegment(sketch, "E1987", {"start": v(-27.1, 9.9) * mm, "end": v(-26.7, 9.28) * mm});
            skLineSegment(sketch, "E1988", {"start": v(-26.7, 9.28) * mm, "end": v(-26.16, 8.72) * mm});
            skLineSegment(sketch, "E1989", {"start": v(-25.83, 8.64) * mm, "end": v(-25.78, 8.32) * mm});
            skLineSegment(sketch, "E1990", {"start": v(-25.78, 8.32) * mm, "end": v(-25.66, 7.62) * mm});
            skLineSegment(sketch, "E1991", {"start": v(-25.66, 7.62) * mm, "end": v(-25.54, 6.92) * mm});
            skLineSegment(sketch, "E1992", {"start": v(-25.54, 6.92) * mm, "end": v(-25.49, 6.6) * mm});
            skLineSegment(sketch, "E1993", {"start": v(-25.49, 6.6) * mm, "end": v(-25.5, 7.51) * mm});
            skLineSegment(sketch, "E1994", {"start": v(-25.5, 7.51) * mm, "end": v(-25.58, 8.34) * mm});
            skLineSegment(sketch, "E1995", {"start": v(-25.58, 8.34) * mm, "end": v(-25.86, 9.1) * mm});
            skLineSegment(sketch, "E1996", {"start": v(-25.86, 9.1) * mm, "end": v(-26.42, 9.82) * mm});
            skLineSegment(sketch, "E1997", {"start": v(-26.42, 9.82) * mm, "end": v(-26.33, 9.64) * mm});
            skLineSegment(sketch, "E1998", {"start": v(-26.33, 9.64) * mm, "end": v(-26.13, 9.23) * mm});
            skLineSegment(sketch, "E1999", {"start": v(-26.13, 9.23) * mm, "end": v(-25.93, 8.82) * mm});
            skLineSegment(sketch, "E2000", {"start": v(-25.93, 8.82) * mm, "end": v(-25.83, 8.64) * mm});
            skLineSegment(sketch, "E2001", {"start": v(-25.9, 9.48) * mm, "end": v(-25.82, 9.4) * mm});
            skLineSegment(sketch, "E2002", {"start": v(-25.82, 9.4) * mm, "end": v(-25.82, 9.48) * mm});
            skLineSegment(sketch, "E2003", {"start": v(-25.82, 9.48) * mm, "end": v(-25.9, 9.48) * mm});
            skLineSegment(sketch, "E2004", {"start": v(-25.82, 9.4) * mm, "end": v(-25.74, 9.31) * mm});
            skLineSegment(sketch, "E2005", {"start": v(-25.74, 9.31) * mm, "end": v(-25.74, 9.4) * mm});
            skLineSegment(sketch, "E2006", {"start": v(-25.74, 9.4) * mm, "end": v(-25.82, 9.4) * mm});
            skLineSegment(sketch, "E2007", {"start": v(-25.49, 8.8) * mm, "end": v(-25.57, 9.06) * mm});
            skLineSegment(sketch, "E2008", {"start": v(-25.57, 9.06) * mm, "end": v(-25.66, 9.31) * mm});
            skLineSegment(sketch, "E2009", {"start": v(-25.66, 9.31) * mm, "end": v(-25.57, 9.06) * mm});
            skLineSegment(sketch, "E2010", {"start": v(-25.57, 9.06) * mm, "end": v(-25.49, 8.8) * mm});
            skLineSegment(sketch, "E2011", {"start": v(-25.32, 6.94) * mm, "end": v(-25.36, 6.52) * mm});
            skLineSegment(sketch, "E2012", {"start": v(-25.36, 6.52) * mm, "end": v(-25.4, 6.1) * mm});
            skLineSegment(sketch, "E2013", {"start": v(-25.4, 6.1) * mm, "end": v(-25.23, 7.2) * mm});
            skLineSegment(sketch, "E2014", {"start": v(-25.23, 7.2) * mm, "end": v(-25.32, 8.3) * mm});
            skLineSegment(sketch, "E2015", {"start": v(-25.32, 8.3) * mm, "end": v(-25.32, 8.09) * mm});
            skLineSegment(sketch, "E2016", {"start": v(-25.32, 8.09) * mm, "end": v(-25.32, 7.62) * mm});
            skLineSegment(sketch, "E2017", {"start": v(-25.32, 7.62) * mm, "end": v(-25.32, 7.16) * mm});
            skLineSegment(sketch, "E2018", {"start": v(-25.32, 7.16) * mm, "end": v(-25.32, 6.94) * mm});
            skLineSegment(sketch, "E2019", {"start": v(-77.13, 7.62) * mm, "end": v(-77.05, 7.54) * mm});
            skLineSegment(sketch, "E2020", {"start": v(-77.05, 7.54) * mm, "end": v(-77.05, 7.62) * mm});
            skLineSegment(sketch, "E2021", {"start": v(-77.05, 7.62) * mm, "end": v(-77.13, 7.62) * mm});
            skLineSegment(sketch, "E2022", {"start": v(-25.74, 6.52) * mm, "end": v(-25.74, 6.73) * mm});
            skLineSegment(sketch, "E2023", {"start": v(-25.74, 6.73) * mm, "end": v(-25.74, 6.94) * mm});
            skLineSegment(sketch, "E2024", {"start": v(-25.74, 6.94) * mm, "end": v(-25.74, 6.73) * mm});
            skLineSegment(sketch, "E2025", {"start": v(-25.74, 6.73) * mm, "end": v(-25.74, 6.52) * mm});
            skLineSegment(sketch, "E2026", {"start": v(-25.66, 5.67) * mm, "end": v(-25.57, 5.88) * mm});
            skLineSegment(sketch, "E2027", {"start": v(-25.57, 5.88) * mm, "end": v(-25.49, 6.1) * mm});
            skLineSegment(sketch, "E2028", {"start": v(-25.49, 6.1) * mm, "end": v(-25.57, 5.88) * mm});
            skLineSegment(sketch, "E2029", {"start": v(-25.57, 5.88) * mm, "end": v(-25.66, 5.67) * mm});
            skLineSegment(sketch, "E2030", {"start": v(-31.5, 4.57) * mm, "end": v(-31.41, 4.49) * mm});
            skLineSegment(sketch, "E2031", {"start": v(-31.41, 4.49) * mm, "end": v(-31.41, 4.57) * mm});
            skLineSegment(sketch, "E2032", {"start": v(-31.41, 4.57) * mm, "end": v(-31.5, 4.57) * mm});
            skLineSegment(sketch, "E2033", {"start": v(-25.82, 3.73) * mm, "end": v(-25.74, 3.64) * mm});
            skLineSegment(sketch, "E2034", {"start": v(-25.74, 3.64) * mm, "end": v(-25.74, 3.73) * mm});
            skLineSegment(sketch, "E2035", {"start": v(-25.74, 3.73) * mm, "end": v(-25.82, 3.73) * mm});
            skLineSegment(sketch, "E2036", {"start": v(-25.9, 3.64) * mm, "end": v(-25.82, 3.56) * mm});
            skLineSegment(sketch, "E2037", {"start": v(-25.82, 3.56) * mm, "end": v(-25.82, 3.64) * mm});
            skLineSegment(sketch, "E2038", {"start": v(-25.82, 3.64) * mm, "end": v(-25.9, 3.64) * mm});
            skLineSegment(sketch, "E2039", {"start": v(-26, 3.56) * mm, "end": v(-25.9, 3.47) * mm});
            skLineSegment(sketch, "E2040", {"start": v(-25.9, 3.47) * mm, "end": v(-25.9, 3.56) * mm});
            skLineSegment(sketch, "E2041", {"start": v(-25.9, 3.56) * mm, "end": v(-26, 3.56) * mm});
            skLineSegment(sketch, "E2042", {"start": v(-26.42, 3.3) * mm, "end": v(-26.33, 3.22) * mm});
            skLineSegment(sketch, "E2043", {"start": v(-26.33, 3.22) * mm, "end": v(-26.33, 3.3) * mm});
            skLineSegment(sketch, "E2044", {"start": v(-26.33, 3.3) * mm, "end": v(-26.42, 3.3) * mm});
            skLineSegment(sketch, "E2045", {"start": v(-76.29, -1.1) * mm, "end": v(-76.2, -1.18) * mm});
            skLineSegment(sketch, "E2046", {"start": v(-76.2, -1.18) * mm, "end": v(-76.2, -1.1) * mm});
            skLineSegment(sketch, "E2047", {"start": v(-76.2, -1.1) * mm, "end": v(-76.29, -1.1) * mm});
            skLineSegment(sketch, "E2048", {"start": v(-76.2, -1.18) * mm, "end": v(-76.12, -1.27) * mm});
            skLineSegment(sketch, "E2049", {"start": v(-76.12, -1.27) * mm, "end": v(-76.12, -1.18) * mm});
            skLineSegment(sketch, "E2050", {"start": v(-76.12, -1.18) * mm, "end": v(-76.2, -1.18) * mm});
            skLineSegment(sketch, "E2051", {"start": v(-75.86, -1.52) * mm, "end": v(-75.86, -1.44) * mm});
            skLineSegment(sketch, "E2052", {"start": v(-75.86, -1.44) * mm, "end": v(-75.95, -1.35) * mm});
            skLineSegment(sketch, "E2053", {"start": v(-75.95, -1.35) * mm, "end": v(-76.03, -1.27) * mm});
            skLineSegment(sketch, "E2054", {"start": v(-76.03, -1.27) * mm, "end": v(-75.95, -1.4) * mm});
            skLineSegment(sketch, "E2055", {"start": v(-75.95, -1.4) * mm, "end": v(-75.86, -1.52) * mm});
            skLineSegment(sketch, "E2056", {"start": v(-41.49, -3.17) * mm, "end": v(-41.24, -3.22) * mm});
            skLineSegment(sketch, "E2057", {"start": v(-41.24, -3.22) * mm, "end": v(-40.68, -3.32) * mm});
            skLineSegment(sketch, "E2058", {"start": v(-40.68, -3.32) * mm, "end": v(-40.13, -3.42) * mm});
            skLineSegment(sketch, "E2059", {"start": v(-40.13, -3.42) * mm, "end": v(-39.88, -3.47) * mm});
            skLineSegment(sketch, "E2060", {"start": v(-39.88, -3.47) * mm, "end": v(-39.54, -3.42) * mm});
            skLineSegment(sketch, "E2061", {"start": v(-39.54, -3.42) * mm, "end": v(-38.78, -3.3) * mm});
            skLineSegment(sketch, "E2062", {"start": v(-38.78, -3.3) * mm, "end": v(-38.02, -3.19) * mm});
            skLineSegment(sketch, "E2063", {"start": v(-38.02, -3.19) * mm, "end": v(-37.68, -3.13) * mm});
            skLineSegment(sketch, "E2064", {"start": v(-37.68, -3.13) * mm, "end": v(-37.57, -3.25) * mm});
            skLineSegment(sketch, "E2065", {"start": v(-37.57, -3.25) * mm, "end": v(-37.34, -3.51) * mm});
            skLineSegment(sketch, "E2066", {"start": v(-37.34, -3.51) * mm, "end": v(-37.1, -3.77) * mm});
            skLineSegment(sketch, "E2067", {"start": v(-37.1, -3.77) * mm, "end": v(-37, -3.9) * mm});
            skLineSegment(sketch, "E2068", {"start": v(-37, -3.9) * mm, "end": v(-37.09, -3.98) * mm});
            skLineSegment(sketch, "E2069", {"start": v(-37.09, -3.98) * mm, "end": v(-37.17, -4.06) * mm});
            skLineSegment(sketch, "E2070", {"start": v(-37.17, -4.06) * mm, "end": v(-37.17, -4.15) * mm});
            skLineSegment(sketch, "E2071", {"start": v(-37.17, -4.15) * mm, "end": v(-37.09, -4.32) * mm});
            skLineSegment(sketch, "E2072", {"start": v(-37.09, -4.32) * mm, "end": v(-37, -4.49) * mm});
            skLineSegment(sketch, "E2073", {"start": v(-37, -4.49) * mm, "end": v(-38.08, -4.73) * mm});
            skLineSegment(sketch, "E2074", {"start": v(-38.08, -4.73) * mm, "end": v(-38.9, -4.84) * mm});
            skLineSegment(sketch, "E2075", {"start": v(-38.9, -4.84) * mm, "end": v(-39.73, -4.73) * mm});
            skLineSegment(sketch, "E2076", {"start": v(-39.73, -4.73) * mm, "end": v(-40.81, -4.33) * mm});
            skLineSegment(sketch, "E2077", {"start": v(-40.81, -4.33) * mm, "end": v(-41.25, -4.14) * mm});
            skLineSegment(sketch, "E2078", {"start": v(-41.25, -4.14) * mm, "end": v(-41.6, -3.95) * mm});
            skLineSegment(sketch, "E2079", {"start": v(-41.6, -3.95) * mm, "end": v(-41.84, -3.67) * mm});
            skLineSegment(sketch, "E2080", {"start": v(-41.84, -3.67) * mm, "end": v(-42, -3.22) * mm});
            skLineSegment(sketch, "E2081", {"start": v(-42, -3.22) * mm, "end": v(-41.74, -3.2) * mm});
            skLineSegment(sketch, "E2082", {"start": v(-41.74, -3.2) * mm, "end": v(-41.49, -3.17) * mm});
            skLineSegment(sketch, "E2083", {"start": v(-45.64, -6.18) * mm, "end": v(-45.68, -6.3) * mm});
            skLineSegment(sketch, "E2084", {"start": v(-45.68, -6.3) * mm, "end": v(-45.72, -6.43) * mm});
            skLineSegment(sketch, "E2085", {"start": v(-45.72, -6.43) * mm, "end": v(-45.38, -6.5) * mm});
            skLineSegment(sketch, "E2086", {"start": v(-45.38, -6.5) * mm, "end": v(-45.13, -6.33) * mm});
            skLineSegment(sketch, "E2087", {"start": v(-45.13, -6.33) * mm, "end": v(-44.8, -6.33) * mm});
            skLineSegment(sketch, "E2088", {"start": v(-44.8, -6.33) * mm, "end": v(-44.47, -6.33) * mm});
            skLineSegment(sketch, "E2089", {"start": v(-44.47, -6.33) * mm, "end": v(-44.32, -6.38) * mm});
            skLineSegment(sketch, "E2090", {"start": v(-44.32, -6.38) * mm, "end": v(-43.98, -6.49) * mm});
            skLineSegment(sketch, "E2091", {"start": v(-43.98, -6.49) * mm, "end": v(-43.65, -6.6) * mm});
            skLineSegment(sketch, "E2092", {"start": v(-43.65, -6.6) * mm, "end": v(-43.5, -6.64) * mm});
            skLineSegment(sketch, "E2093", {"start": v(-43.5, -6.64) * mm, "end": v(-43.38, -6.8) * mm});
            skLineSegment(sketch, "E2094", {"start": v(-43.38, -6.8) * mm, "end": v(-43.27, -6.94) * mm});
            skLineSegment(sketch, "E2095", {"start": v(-43.27, -6.94) * mm, "end": v(-43.75, -7.27) * mm});
            skLineSegment(sketch, "E2096", {"start": v(-43.75, -7.27) * mm, "end": v(-44.37, -7.3) * mm});
            skLineSegment(sketch, "E2097", {"start": v(-44.37, -7.3) * mm, "end": v(-45.16, -7.29) * mm});
            skLineSegment(sketch, "E2098", {"start": v(-45.16, -7.29) * mm, "end": v(-46.05, -7.13) * mm});
            skLineSegment(sketch, "E2099", {"start": v(-46.05, -7.13) * mm, "end": v(-46.83, -6.77) * mm});
            skLineSegment(sketch, "E2100", {"start": v(-46.83, -6.77) * mm, "end": v(-47.33, -6.18) * mm});
            skLineSegment(sketch, "E2101", {"start": v(-47.33, -6.18) * mm, "end": v(-47.16, -6.18) * mm});
            skLineSegment(sketch, "E2102", {"start": v(-47.16, -6.18) * mm, "end": v(-47.2, -6.01) * mm});
            skLineSegment(sketch, "E2103", {"start": v(-47.2, -6.01) * mm, "end": v(-47.25, -5.84) * mm});
            skLineSegment(sketch, "E2104", {"start": v(-47.25, -5.84) * mm, "end": v(-46.42, -5.9) * mm});
            skLineSegment(sketch, "E2105", {"start": v(-46.42, -5.9) * mm, "end": v(-45.64, -6.18) * mm});
            skLineSegment(sketch, "E2106", {"start": v(-42.08, -9.31) * mm, "end": v(-42, -9.4) * mm});
            skLineSegment(sketch, "E2107", {"start": v(-42, -9.4) * mm, "end": v(-42, -9.31) * mm});
            skLineSegment(sketch, "E2108", {"start": v(-42, -9.31) * mm, "end": v(-42.08, -9.31) * mm});
            skLineSegment(sketch, "E2109", {"start": v(-35.14, -10.47) * mm, "end": v(-34.49, -10.4) * mm});
            skLineSegment(sketch, "E2110", {"start": v(-34.49, -10.4) * mm, "end": v(-33.7, -10.35) * mm});
            skLineSegment(sketch, "E2111", {"start": v(-33.7, -10.35) * mm, "end": v(-33.58, -10.38) * mm});
            skLineSegment(sketch, "E2112", {"start": v(-33.58, -10.38) * mm, "end": v(-33.32, -10.45) * mm});
            skLineSegment(sketch, "E2113", {"start": v(-33.32, -10.45) * mm, "end": v(-33.06, -10.52) * mm});
            skLineSegment(sketch, "E2114", {"start": v(-33.06, -10.52) * mm, "end": v(-32.94, -10.55) * mm});
            skLineSegment(sketch, "E2115", {"start": v(-32.94, -10.55) * mm, "end": v(-32.8, -10.58) * mm});
            skLineSegment(sketch, "E2116", {"start": v(-32.8, -10.58) * mm, "end": v(-32.51, -10.64) * mm});
            skLineSegment(sketch, "E2117", {"start": v(-32.51, -10.64) * mm, "end": v(-32.22, -10.7) * mm});
            skLineSegment(sketch, "E2118", {"start": v(-32.22, -10.7) * mm, "end": v(-32.09, -10.73) * mm});
            skLineSegment(sketch, "E2119", {"start": v(-32.09, -10.73) * mm, "end": v(-31.97, -10.79) * mm});
            skLineSegment(sketch, "E2120", {"start": v(-31.97, -10.79) * mm, "end": v(-31.7, -10.9) * mm});
            skLineSegment(sketch, "E2121", {"start": v(-31.7, -10.9) * mm, "end": v(-31.45, -11.02) * mm});
            skLineSegment(sketch, "E2122", {"start": v(-31.45, -11.02) * mm, "end": v(-31.33, -11.07) * mm});
            skLineSegment(sketch, "E2123", {"start": v(-31.33, -11.07) * mm, "end": v(-31.2, -11.11) * mm});
            skLineSegment(sketch, "E2124", {"start": v(-31.2, -11.11) * mm, "end": v(-30.95, -11.2) * mm});
            skLineSegment(sketch, "E2125", {"start": v(-30.95, -11.2) * mm, "end": v(-30.69, -11.3) * mm});
            skLineSegment(sketch, "E2126", {"start": v(-30.69, -11.3) * mm, "end": v(-30.57, -11.34) * mm});
            skLineSegment(sketch, "E2127", {"start": v(-30.57, -11.34) * mm, "end": v(-30.22, -11.56) * mm});
            skLineSegment(sketch, "E2128", {"start": v(-30.22, -11.56) * mm, "end": v(-29.47, -12.02) * mm});
            skLineSegment(sketch, "E2129", {"start": v(-29.47, -12.02) * mm, "end": v(-28.7, -12.49) * mm});
            skLineSegment(sketch, "E2130", {"start": v(-28.7, -12.49) * mm, "end": v(-28.36, -12.7) * mm});
            skLineSegment(sketch, "E2131", {"start": v(-28.36, -12.7) * mm, "end": v(-27.57, -13.29) * mm});
            skLineSegment(sketch, "E2132", {"start": v(-27.57, -13.29) * mm, "end": v(-26.86, -14) * mm});
            skLineSegment(sketch, "E2133", {"start": v(-26.86, -14) * mm, "end": v(-26.44, -14.85) * mm});
            skLineSegment(sketch, "E2134", {"start": v(-26.44, -14.85) * mm, "end": v(-26.5, -15.83) * mm});
            skLineSegment(sketch, "E2135", {"start": v(-26.5, -15.83) * mm, "end": v(-26.89, -15.8) * mm});
            skLineSegment(sketch, "E2136", {"start": v(-26.89, -15.8) * mm, "end": v(-27.73, -15.7) * mm});
            skLineSegment(sketch, "E2137", {"start": v(-27.73, -15.7) * mm, "end": v(-28.57, -15.62) * mm});
            skLineSegment(sketch, "E2138", {"start": v(-28.57, -15.62) * mm, "end": v(-28.96, -15.58) * mm});
            skLineSegment(sketch, "E2139", {"start": v(-28.96, -15.58) * mm, "end": v(-29.16, -15.56) * mm});
            skLineSegment(sketch, "E2140", {"start": v(-29.16, -15.56) * mm, "end": v(-29.6, -15.51) * mm});
            skLineSegment(sketch, "E2141", {"start": v(-29.6, -15.51) * mm, "end": v(-30.03, -15.47) * mm});
            skLineSegment(sketch, "E2142", {"start": v(-30.03, -15.47) * mm, "end": v(-30.22, -15.45) * mm});
            skLineSegment(sketch, "E2143", {"start": v(-30.22, -15.45) * mm, "end": v(-30.38, -15.7) * mm});
            skLineSegment(sketch, "E2144", {"start": v(-30.38, -15.7) * mm, "end": v(-30.44, -16) * mm});
            skLineSegment(sketch, "E2145", {"start": v(-30.44, -16) * mm, "end": v(-30.54, -16.43) * mm});
            skLineSegment(sketch, "E2146", {"start": v(-30.54, -16.43) * mm, "end": v(-30.82, -16.77) * mm});
            skLineSegment(sketch, "E2147", {"start": v(-30.82, -16.77) * mm, "end": v(-30.96, -16.87) * mm});
            skLineSegment(sketch, "E2148", {"start": v(-30.96, -16.87) * mm, "end": v(-31.25, -17.09) * mm});
            skLineSegment(sketch, "E2149", {"start": v(-31.25, -17.09) * mm, "end": v(-31.54, -17.3) * mm});
            skLineSegment(sketch, "E2150", {"start": v(-31.54, -17.3) * mm, "end": v(-31.67, -17.4) * mm});
            skLineSegment(sketch, "E2151", {"start": v(-31.67, -17.4) * mm, "end": v(-33.33, -18.89) * mm});
            skLineSegment(sketch, "E2152", {"start": v(-33.33, -18.89) * mm, "end": v(-34.78, -20.57) * mm});
            skLineSegment(sketch, "E2153", {"start": v(-34.78, -20.57) * mm, "end": v(-34.83, -20.68) * mm});
            skLineSegment(sketch, "E2154", {"start": v(-34.83, -20.68) * mm, "end": v(-34.98, -20.97) * mm});
            skLineSegment(sketch, "E2155", {"start": v(-34.98, -20.97) * mm, "end": v(-35.17, -21.38) * mm});
            skLineSegment(sketch, "E2156", {"start": v(-35.17, -21.38) * mm, "end": v(-35.4, -21.84) * mm});
            skLineSegment(sketch, "E2157", {"start": v(-35.4, -21.84) * mm, "end": v(-35.63, -22.3) * mm});
            skLineSegment(sketch, "E2158", {"start": v(-35.63, -22.3) * mm, "end": v(-35.83, -22.72) * mm});
            skLineSegment(sketch, "E2159", {"start": v(-35.83, -22.72) * mm, "end": v(-35.97, -23) * mm});
            skLineSegment(sketch, "E2160", {"start": v(-35.97, -23) * mm, "end": v(-36.02, -23.11) * mm});
            skLineSegment(sketch, "E2161", {"start": v(-36.02, -23.11) * mm, "end": v(-36.15, -23.4) * mm});
            skLineSegment(sketch, "E2162", {"start": v(-36.15, -23.4) * mm, "end": v(-36.43, -24) * mm});
            skLineSegment(sketch, "E2163", {"start": v(-36.43, -24) * mm, "end": v(-36.71, -24.61) * mm});
            skLineSegment(sketch, "E2164", {"start": v(-36.71, -24.61) * mm, "end": v(-36.84, -24.9) * mm});
            skLineSegment(sketch, "E2165", {"start": v(-36.84, -24.9) * mm, "end": v(-37.01, -25.3) * mm});
            skLineSegment(sketch, "E2166", {"start": v(-37.01, -25.3) * mm, "end": v(-37.08, -25.74) * mm});
            skLineSegment(sketch, "E2167", {"start": v(-37.08, -25.74) * mm, "end": v(-36.82, -26.33) * mm});
            skLineSegment(sketch, "E2168", {"start": v(-36.82, -26.33) * mm, "end": v(-36.7, -26.72) * mm});
            skLineSegment(sketch, "E2169", {"start": v(-36.7, -26.72) * mm, "end": v(-36.45, -27.26) * mm});
            skLineSegment(sketch, "E2170", {"start": v(-36.45, -27.26) * mm, "end": v(-36.38, -27.36) * mm});
            skLineSegment(sketch, "E2171", {"start": v(-36.38, -27.36) * mm, "end": v(-36.17, -27.6) * mm});
            skLineSegment(sketch, "E2172", {"start": v(-36.17, -27.6) * mm, "end": v(-35.88, -27.96) * mm});
            skLineSegment(sketch, "E2173", {"start": v(-35.88, -27.96) * mm, "end": v(-35.55, -28.36) * mm});
            skLineSegment(sketch, "E2174", {"start": v(-35.55, -28.36) * mm, "end": v(-35.22, -28.77) * mm});
            skLineSegment(sketch, "E2175", {"start": v(-35.22, -28.77) * mm, "end": v(-34.92, -29.12) * mm});
            skLineSegment(sketch, "E2176", {"start": v(-34.92, -29.12) * mm, "end": v(-34.72, -29.37) * mm});
            skLineSegment(sketch, "E2177", {"start": v(-34.72, -29.37) * mm, "end": v(-34.64, -29.46) * mm});
            skLineSegment(sketch, "E2178", {"start": v(-34.64, -29.46) * mm, "end": v(-34.05, -30.12) * mm});
            skLineSegment(sketch, "E2179", {"start": v(-34.05, -30.12) * mm, "end": v(-33.74, -30.9) * mm});
            skLineSegment(sketch, "E2180", {"start": v(-33.74, -30.9) * mm, "end": v(-33.74, -31.67) * mm});
            skLineSegment(sketch, "E2181", {"start": v(-33.74, -31.67) * mm, "end": v(-33.94, -32.31) * mm});
            skLineSegment(sketch, "E2182", {"start": v(-33.94, -32.31) * mm, "end": v(-34.32, -32.76) * mm});
            skLineSegment(sketch, "E2183", {"start": v(-34.32, -32.76) * mm, "end": v(-34.8, -33.13) * mm});
            skLineSegment(sketch, "E2184", {"start": v(-34.8, -33.13) * mm, "end": v(-35.3, -33.54) * mm});
            skLineSegment(sketch, "E2185", {"start": v(-35.3, -33.54) * mm, "end": v(-35.93, -34.16) * mm});
            skLineSegment(sketch, "E2186", {"start": v(-35.93, -34.16) * mm, "end": v(-36.57, -34.7) * mm});
            skLineSegment(sketch, "E2187", {"start": v(-36.57, -34.7) * mm, "end": v(-37.25, -34.8) * mm});
            skLineSegment(sketch, "E2188", {"start": v(-37.25, -34.8) * mm, "end": v(-37.3, -34.71) * mm});
            skLineSegment(sketch, "E2189", {"start": v(-37.3, -34.71) * mm, "end": v(-37.34, -34.63) * mm});
            skLineSegment(sketch, "E2190", {"start": v(-37.34, -34.63) * mm, "end": v(-37.42, -34.63) * mm});
            skLineSegment(sketch, "E2191", {"start": v(-37.42, -34.63) * mm, "end": v(-37.38, -34.5) * mm});
            skLineSegment(sketch, "E2192", {"start": v(-37.38, -34.5) * mm, "end": v(-37.34, -34.37) * mm});
            skLineSegment(sketch, "E2193", {"start": v(-37.34, -34.37) * mm, "end": v(-37.47, -34.29) * mm});
            skLineSegment(sketch, "E2194", {"start": v(-37.47, -34.29) * mm, "end": v(-37.6, -34.2) * mm});
            skLineSegment(sketch, "E2195", {"start": v(-37.6, -34.2) * mm, "end": v(-38.21, -34.65) * mm});
            skLineSegment(sketch, "E2196", {"start": v(-38.21, -34.65) * mm, "end": v(-38.98, -34.9) * mm});
            skLineSegment(sketch, "E2197", {"start": v(-38.98, -34.9) * mm, "end": v(-39.8, -34.97) * mm});
            skLineSegment(sketch, "E2198", {"start": v(-39.8, -34.97) * mm, "end": v(-40.56, -34.84) * mm});
            skLineSegment(sketch, "E2199", {"start": v(-40.56, -34.84) * mm, "end": v(-41.12, -34.58) * mm});
            skLineSegment(sketch, "E2200", {"start": v(-41.12, -34.58) * mm, "end": v(-41.66, -34.25) * mm});
            skLineSegment(sketch, "E2201", {"start": v(-41.66, -34.25) * mm, "end": v(-41.96, -34) * mm});
            skLineSegment(sketch, "E2202", {"start": v(-41.96, -34) * mm, "end": v(-42.33, -33.65) * mm});
            skLineSegment(sketch, "E2203", {"start": v(-42.33, -33.65) * mm, "end": v(-42.67, -33.35) * mm});
            skLineSegment(sketch, "E2204", {"start": v(-42.67, -33.35) * mm, "end": v(-42.93, -33.2) * mm});
            skLineSegment(sketch, "E2205", {"start": v(-42.93, -33.2) * mm, "end": v(-43.57, -33.38) * mm});
            skLineSegment(sketch, "E2206", {"start": v(-43.57, -33.38) * mm, "end": v(-44.17, -33.72) * mm});
            skLineSegment(sketch, "E2207", {"start": v(-44.17, -33.72) * mm, "end": v(-44.63, -34.08) * mm});
            skLineSegment(sketch, "E2208", {"start": v(-44.63, -34.08) * mm, "end": v(-44.93, -34.54) * mm});
            skLineSegment(sketch, "E2209", {"start": v(-44.93, -34.54) * mm, "end": v(-44.9, -35.04) * mm});
            skLineSegment(sketch, "E2210", {"start": v(-44.9, -35.04) * mm, "end": v(-44.8, -35.73) * mm});
            skLineSegment(sketch, "E2211", {"start": v(-44.8, -35.73) * mm, "end": v(-44.8, -35.98) * mm});
            skLineSegment(sketch, "E2212", {"start": v(-44.8, -35.98) * mm, "end": v(-44.8, -36.53) * mm});
            skLineSegment(sketch, "E2213", {"start": v(-44.8, -36.53) * mm, "end": v(-44.8, -37.08) * mm});
            skLineSegment(sketch, "E2214", {"start": v(-44.8, -37.08) * mm, "end": v(-44.8, -37.34) * mm});
            skLineSegment(sketch, "E2215", {"start": v(-44.8, -37.34) * mm, "end": v(-44.76, -38.13) * mm});
            skLineSegment(sketch, "E2216", {"start": v(-44.76, -38.13) * mm, "end": v(-44.6, -39.03) * mm});
            skLineSegment(sketch, "E2217", {"start": v(-44.6, -39.03) * mm, "end": v(-44.32, -39.88) * mm});
            skLineSegment(sketch, "E2218", {"start": v(-44.32, -39.88) * mm, "end": v(-43.9, -40.53) * mm});
            skLineSegment(sketch, "E2219", {"start": v(-43.9, -40.53) * mm, "end": v(-43.32, -40.95) * mm});
            skLineSegment(sketch, "E2220", {"start": v(-43.32, -40.95) * mm, "end": v(-42.67, -41.27) * mm});
            skLineSegment(sketch, "E2221", {"start": v(-42.67, -41.27) * mm, "end": v(-41.57, -41.64) * mm});
            skLineSegment(sketch, "E2222", {"start": v(-41.57, -41.64) * mm, "end": v(-40.87, -41.63) * mm});
            skLineSegment(sketch, "E2223", {"start": v(-40.87, -41.63) * mm, "end": v(-40, -41.5) * mm});
            skLineSegment(sketch, "E2224", {"start": v(-40, -41.5) * mm, "end": v(-39.16, -41.26) * mm});
            skLineSegment(sketch, "E2225", {"start": v(-39.16, -41.26) * mm, "end": v(-38.52, -40.98) * mm});
            skLineSegment(sketch, "E2226", {"start": v(-38.52, -40.98) * mm, "end": v(-37.97, -40.47) * mm});
            skLineSegment(sketch, "E2227", {"start": v(-37.97, -40.47) * mm, "end": v(-37.42, -39.89) * mm});
            skLineSegment(sketch, "E2228", {"start": v(-37.42, -39.89) * mm, "end": v(-36.95, -39.58) * mm});
            skLineSegment(sketch, "E2229", {"start": v(-36.95, -39.58) * mm, "end": v(-36.6, -39.43) * mm});
            skLineSegment(sketch, "E2230", {"start": v(-36.6, -39.43) * mm, "end": v(-36.2, -38.96) * mm});
            skLineSegment(sketch, "E2231", {"start": v(-36.2, -38.96) * mm, "end": v(-35.73, -38.6) * mm});
            skLineSegment(sketch, "E2232", {"start": v(-35.73, -38.6) * mm, "end": v(-35.69, -38.48) * mm});
            skLineSegment(sketch, "E2233", {"start": v(-35.69, -38.48) * mm, "end": v(-35.65, -38.35) * mm});
            skLineSegment(sketch, "E2234", {"start": v(-35.65, -38.35) * mm, "end": v(-35.14, -38.25) * mm});
            skLineSegment(sketch, "E2235", {"start": v(-35.14, -38.25) * mm, "end": v(-34.7, -38.05) * mm});
            skLineSegment(sketch, "E2236", {"start": v(-34.7, -38.05) * mm, "end": v(-34.2, -38.02) * mm});
            skLineSegment(sketch, "E2237", {"start": v(-34.2, -38.02) * mm, "end": v(-33.7, -37.95) * mm});
            skLineSegment(sketch, "E2238", {"start": v(-33.7, -37.95) * mm, "end": v(-32.85, -37.39) * mm});
            skLineSegment(sketch, "E2239", {"start": v(-32.85, -37.39) * mm, "end": v(-32.4, -37.12) * mm});
            skLineSegment(sketch, "E2240", {"start": v(-32.4, -37.12) * mm, "end": v(-31.92, -36.8) * mm});
            skLineSegment(sketch, "E2241", {"start": v(-31.92, -36.8) * mm, "end": v(-30.82, -35.64) * mm});
            skLineSegment(sketch, "E2242", {"start": v(-30.82, -35.64) * mm, "end": v(-27.77, -32.8) * mm});
            skLineSegment(sketch, "E2243", {"start": v(-27.77, -32.8) * mm, "end": v(-27.42, -32.52) * mm});
            skLineSegment(sketch, "E2244", {"start": v(-27.42, -32.52) * mm, "end": v(-26.95, -32.13) * mm});
            skLineSegment(sketch, "E2245", {"start": v(-26.95, -32.13) * mm, "end": v(-26.52, -31.73) * mm});
            skLineSegment(sketch, "E2246", {"start": v(-26.52, -31.73) * mm, "end": v(-26.29, -31.41) * mm});
            skLineSegment(sketch, "E2247", {"start": v(-26.29, -31.41) * mm, "end": v(-26.28, -30.91) * mm});
            skLineSegment(sketch, "E2248", {"start": v(-26.28, -30.91) * mm, "end": v(-26.36, -30.4) * mm});
            skLineSegment(sketch, "E2249", {"start": v(-26.36, -30.4) * mm, "end": v(-26.53, -29.5) * mm});
            skLineSegment(sketch, "E2250", {"start": v(-26.53, -29.5) * mm, "end": v(-26.78, -28.8) * mm});
            skLineSegment(sketch, "E2251", {"start": v(-26.78, -28.8) * mm, "end": v(-27.12, -28.12) * mm});
            skLineSegment(sketch, "E2252", {"start": v(-27.12, -28.12) * mm, "end": v(-27.55, -27.35) * mm});
            skLineSegment(sketch, "E2253", {"start": v(-27.55, -27.35) * mm, "end": v(-27.68, -27.13) * mm});
            skLineSegment(sketch, "E2254", {"start": v(-27.68, -27.13) * mm, "end": v(-28, -26.58) * mm});
            skLineSegment(sketch, "E2255", {"start": v(-28, -26.58) * mm, "end": v(-28.46, -25.8) * mm});
            skLineSegment(sketch, "E2256", {"start": v(-28.46, -25.8) * mm, "end": v(-28.98, -24.9) * mm});
            skLineSegment(sketch, "E2257", {"start": v(-28.98, -24.9) * mm, "end": v(-29.5, -23.99) * mm});
            skLineSegment(sketch, "E2258", {"start": v(-29.5, -23.99) * mm, "end": v(-29.97, -23.2) * mm});
            skLineSegment(sketch, "E2259", {"start": v(-29.97, -23.2) * mm, "end": v(-30.3, -22.65) * mm});
            skLineSegment(sketch, "E2260", {"start": v(-30.3, -22.65) * mm, "end": v(-30.41, -22.44) * mm});
            skLineSegment(sketch, "E2261", {"start": v(-30.41, -22.44) * mm, "end": v(-30.99, -21.49) * mm});
            skLineSegment(sketch, "E2262", {"start": v(-30.99, -21.49) * mm, "end": v(-31.52, -20.5) * mm});
            skLineSegment(sketch, "E2263", {"start": v(-31.52, -20.5) * mm, "end": v(-31.92, -19.46) * mm});
            skLineSegment(sketch, "E2264", {"start": v(-31.92, -19.46) * mm, "end": v(-32.09, -18.37) * mm});
            skLineSegment(sketch, "E2265", {"start": v(-32.09, -18.37) * mm, "end": v(-31.88, -18.29) * mm});
            skLineSegment(sketch, "E2266", {"start": v(-31.88, -18.29) * mm, "end": v(-31.67, -18.2) * mm});
            skLineSegment(sketch, "E2267", {"start": v(-31.67, -18.2) * mm, "end": v(-31.46, -18.29) * mm});
            skLineSegment(sketch, "E2268", {"start": v(-31.46, -18.29) * mm, "end": v(-31.24, -18.37) * mm});
            skLineSegment(sketch, "E2269", {"start": v(-31.24, -18.37) * mm, "end": v(-31.33, -18.16) * mm});
            skLineSegment(sketch, "E2270", {"start": v(-31.33, -18.16) * mm, "end": v(-31.41, -17.95) * mm});
            skLineSegment(sketch, "E2271", {"start": v(-31.41, -17.95) * mm, "end": v(-31.25, -18.01) * mm});
            skLineSegment(sketch, "E2272", {"start": v(-31.25, -18.01) * mm, "end": v(-30.9, -18.16) * mm});
            skLineSegment(sketch, "E2273", {"start": v(-30.9, -18.16) * mm, "end": v(-30.56, -18.3) * mm});
            skLineSegment(sketch, "E2274", {"start": v(-30.56, -18.3) * mm, "end": v(-30.4, -18.37) * mm});
            skLineSegment(sketch, "E2275", {"start": v(-30.4, -18.37) * mm, "end": v(-30.27, -18.52) * mm});
            skLineSegment(sketch, "E2276", {"start": v(-30.27, -18.52) * mm, "end": v(-30, -18.84) * mm});
            skLineSegment(sketch, "E2277", {"start": v(-30, -18.84) * mm, "end": v(-29.73, -19.16) * mm});
            skLineSegment(sketch, "E2278", {"start": v(-29.73, -19.16) * mm, "end": v(-29.6, -19.3) * mm});
            skLineSegment(sketch, "E2279", {"start": v(-29.6, -19.3) * mm, "end": v(-29.48, -19.53) * mm});
            skLineSegment(sketch, "E2280", {"start": v(-29.48, -19.53) * mm, "end": v(-29.2, -20.02) * mm});
            skLineSegment(sketch, "E2281", {"start": v(-29.2, -20.02) * mm, "end": v(-28.92, -20.52) * mm});
            skLineSegment(sketch, "E2282", {"start": v(-28.92, -20.52) * mm, "end": v(-28.79, -20.74) * mm});
            skLineSegment(sketch, "E2283", {"start": v(-28.79, -20.74) * mm, "end": v(-28.46, -20.63) * mm});
            skLineSegment(sketch, "E2284", {"start": v(-28.46, -20.63) * mm, "end": v(-28.12, -20.66) * mm});
            skLineSegment(sketch, "E2285", {"start": v(-28.12, -20.66) * mm, "end": v(-27.83, -20.95) * mm});
            skLineSegment(sketch, "E2286", {"start": v(-27.83, -20.95) * mm, "end": v(-27.66, -21.34) * mm});
            skLineSegment(sketch, "E2287", {"start": v(-27.66, -21.34) * mm, "end": v(-27.58, -21.59) * mm});
            skLineSegment(sketch, "E2288", {"start": v(-27.58, -21.59) * mm, "end": v(-27.38, -22.14) * mm});
            skLineSegment(sketch, "E2289", {"start": v(-27.38, -22.14) * mm, "end": v(-27.19, -22.7) * mm});
            skLineSegment(sketch, "E2290", {"start": v(-27.19, -22.7) * mm, "end": v(-27.1, -22.94) * mm});
            skLineSegment(sketch, "E2291", {"start": v(-27.1, -22.94) * mm, "end": v(-27.02, -23.17) * mm});
            skLineSegment(sketch, "E2292", {"start": v(-27.02, -23.17) * mm, "end": v(-26.86, -23.66) * mm});
            skLineSegment(sketch, "E2293", {"start": v(-26.86, -23.66) * mm, "end": v(-26.69, -24.16) * mm});
            skLineSegment(sketch, "E2294", {"start": v(-26.69, -24.16) * mm, "end": v(-26.61, -24.38) * mm});
            skLineSegment(sketch, "E2295", {"start": v(-26.61, -24.38) * mm, "end": v(-26.56, -24.53) * mm});
            skLineSegment(sketch, "E2296", {"start": v(-26.56, -24.53) * mm, "end": v(-26.43, -24.85) * mm});
            skLineSegment(sketch, "E2297", {"start": v(-26.43, -24.85) * mm, "end": v(-26.3, -25.17) * mm});
            skLineSegment(sketch, "E2298", {"start": v(-26.3, -25.17) * mm, "end": v(-26.25, -25.32) * mm});
            skLineSegment(sketch, "E2299", {"start": v(-26.25, -25.32) * mm, "end": v(-26.2, -25.49) * mm});
            skLineSegment(sketch, "E2300", {"start": v(-26.2, -25.49) * mm, "end": v(-26.1, -25.87) * mm});
            skLineSegment(sketch, "E2301", {"start": v(-26.1, -25.87) * mm, "end": v(-26, -26.24) * mm});
            skLineSegment(sketch, "E2302", {"start": v(-26, -26.24) * mm, "end": v(-25.96, -26.42) * mm});
            skLineSegment(sketch, "E2303", {"start": v(-25.96, -26.42) * mm, "end": v(-25.9, -26.56) * mm});
            skLineSegment(sketch, "E2304", {"start": v(-25.9, -26.56) * mm, "end": v(-25.77, -26.88) * mm});
            skLineSegment(sketch, "E2305", {"start": v(-25.77, -26.88) * mm, "end": v(-25.64, -27.2) * mm});
            skLineSegment(sketch, "E2306", {"start": v(-25.64, -27.2) * mm, "end": v(-25.58, -27.35) * mm});
            skLineSegment(sketch, "E2307", {"start": v(-25.58, -27.35) * mm, "end": v(-25.52, -27.53) * mm});
            skLineSegment(sketch, "E2308", {"start": v(-25.52, -27.53) * mm, "end": v(-25.4, -27.94) * mm});
            skLineSegment(sketch, "E2309", {"start": v(-25.4, -27.94) * mm, "end": v(-25.29, -28.35) * mm});
            skLineSegment(sketch, "E2310", {"start": v(-25.29, -28.35) * mm, "end": v(-25.23, -28.53) * mm});
            skLineSegment(sketch, "E2311", {"start": v(-25.23, -28.53) * mm, "end": v(-25.13, -29) * mm});
            skLineSegment(sketch, "E2312", {"start": v(-25.13, -29) * mm, "end": v(-25.01, -29.68) * mm});
            skLineSegment(sketch, "E2313", {"start": v(-25.01, -29.68) * mm, "end": v(-24.92, -30.35) * mm});
            skLineSegment(sketch, "E2314", {"start": v(-24.92, -30.35) * mm, "end": v(-24.9, -30.81) * mm});
            skLineSegment(sketch, "E2315", {"start": v(-24.9, -30.81) * mm, "end": v(-25.06, -31.33) * mm});
            skLineSegment(sketch, "E2316", {"start": v(-25.06, -31.33) * mm, "end": v(-24.93, -31.35) * mm});
            skLineSegment(sketch, "E2317", {"start": v(-24.93, -31.35) * mm, "end": v(-24.64, -31.41) * mm});
            skLineSegment(sketch, "E2318", {"start": v(-24.64, -31.41) * mm, "end": v(-24.35, -31.47) * mm});
            skLineSegment(sketch, "E2319", {"start": v(-24.35, -31.47) * mm, "end": v(-24.22, -31.5) * mm});
            skLineSegment(sketch, "E2320", {"start": v(-24.22, -31.5) * mm, "end": v(-24.26, -31.89) * mm});
            skLineSegment(sketch, "E2321", {"start": v(-24.26, -31.89) * mm, "end": v(-24.44, -32.1) * mm});
            skLineSegment(sketch, "E2322", {"start": v(-24.44, -32.1) * mm, "end": v(-24.75, -32.37) * mm});
            skLineSegment(sketch, "E2323", {"start": v(-24.75, -32.37) * mm, "end": v(-25.08, -32.64) * mm});
            skLineSegment(sketch, "E2324", {"start": v(-25.08, -32.64) * mm, "end": v(-25.32, -32.83) * mm});
            skLineSegment(sketch, "E2325", {"start": v(-25.32, -32.83) * mm, "end": v(-26.8, -34.07) * mm});
            skLineSegment(sketch, "E2326", {"start": v(-26.8, -34.07) * mm, "end": v(-28.2, -35.4) * mm});
            skLineSegment(sketch, "E2327", {"start": v(-28.2, -35.4) * mm, "end": v(-28.28, -35.48) * mm});
            skLineSegment(sketch, "E2328", {"start": v(-28.28, -35.48) * mm, "end": v(-28.47, -35.69) * mm});
            skLineSegment(sketch, "E2329", {"start": v(-28.47, -35.69) * mm, "end": v(-28.66, -35.89) * mm});
            skLineSegment(sketch, "E2330", {"start": v(-28.66, -35.89) * mm, "end": v(-28.74, -35.98) * mm});
            skLineSegment(sketch, "E2331", {"start": v(-28.74, -35.98) * mm, "end": v(-28.82, -36.08) * mm});
            skLineSegment(sketch, "E2332", {"start": v(-28.82, -36.08) * mm, "end": v(-29, -36.3) * mm});
            skLineSegment(sketch, "E2333", {"start": v(-29, -36.3) * mm, "end": v(-29.16, -36.53) * mm});
            skLineSegment(sketch, "E2334", {"start": v(-29.16, -36.53) * mm, "end": v(-29.24, -36.64) * mm});
            skLineSegment(sketch, "E2335", {"start": v(-29.24, -36.64) * mm, "end": v(-30.28, -37.5) * mm});
            skLineSegment(sketch, "E2336", {"start": v(-30.28, -37.5) * mm, "end": v(-31.41, -38.27) * mm});
            skLineSegment(sketch, "E2337", {"start": v(-31.41, -38.27) * mm, "end": v(-32, -38.7) * mm});
            skLineSegment(sketch, "E2338", {"start": v(-32, -38.7) * mm, "end": v(-32.6, -39.08) * mm});
            skLineSegment(sketch, "E2339", {"start": v(-32.6, -39.08) * mm, "end": v(-33.78, -39.36) * mm});
            skLineSegment(sketch, "E2340", {"start": v(-33.78, -39.36) * mm, "end": v(-34.21, -39.37) * mm});
            skLineSegment(sketch, "E2341", {"start": v(-34.21, -39.37) * mm, "end": v(-34.61, -39.46) * mm});
            skLineSegment(sketch, "E2342", {"start": v(-34.61, -39.46) * mm, "end": v(-34.95, -39.88) * mm});
            skLineSegment(sketch, "E2343", {"start": v(-34.95, -39.88) * mm, "end": v(-35.21, -40.39) * mm});
            skLineSegment(sketch, "E2344", {"start": v(-35.21, -40.39) * mm, "end": v(-35.58, -40.87) * mm});
            skLineSegment(sketch, "E2345", {"start": v(-35.58, -40.87) * mm, "end": v(-36.07, -41.24) * mm});
            skLineSegment(sketch, "E2346", {"start": v(-36.07, -41.24) * mm, "end": v(-37.38, -41.97) * mm});
            skLineSegment(sketch, "E2347", {"start": v(-37.38, -41.97) * mm, "end": v(-38.78, -42.5) * mm});
            skLineSegment(sketch, "E2348", {"start": v(-38.78, -42.5) * mm, "end": v(-39.5, -42.78) * mm});
            skLineSegment(sketch, "E2349", {"start": v(-39.5, -42.78) * mm, "end": v(-40.22, -42.98) * mm});
            skLineSegment(sketch, "E2350", {"start": v(-40.22, -42.98) * mm, "end": v(-40.93, -43.04) * mm});
            skLineSegment(sketch, "E2351", {"start": v(-40.93, -43.04) * mm, "end": v(-41.78, -43.04) * mm});
            skLineSegment(sketch, "E2352", {"start": v(-41.78, -43.04) * mm, "end": v(-42.64, -42.98) * mm});
            skLineSegment(sketch, "E2353", {"start": v(-42.64, -42.98) * mm, "end": v(-43.35, -42.9) * mm});
            skLineSegment(sketch, "E2354", {"start": v(-43.35, -42.9) * mm, "end": v(-44.36, -42.69) * mm});
            skLineSegment(sketch, "E2355", {"start": v(-44.36, -42.69) * mm, "end": v(-45.3, -42.37) * mm});
            skLineSegment(sketch, "E2356", {"start": v(-45.3, -42.37) * mm, "end": v(-45.95, -41.78) * mm});
            skLineSegment(sketch, "E2357", {"start": v(-45.95, -41.78) * mm, "end": v(-46.47, -40.96) * mm});
            skLineSegment(sketch, "E2358", {"start": v(-46.47, -40.96) * mm, "end": v(-46.87, -40.05) * mm});
            skLineSegment(sketch, "E2359", {"start": v(-46.87, -40.05) * mm, "end": v(-47.12, -39.2) * mm});
            skLineSegment(sketch, "E2360", {"start": v(-47.12, -39.2) * mm, "end": v(-47.17, -38.87) * mm});
            skLineSegment(sketch, "E2361", {"start": v(-47.17, -38.87) * mm, "end": v(-47.27, -38.14) * mm});
            skLineSegment(sketch, "E2362", {"start": v(-47.27, -38.14) * mm, "end": v(-47.37, -37.41) * mm});
            skLineSegment(sketch, "E2363", {"start": v(-47.37, -37.41) * mm, "end": v(-47.42, -37.08) * mm});
            skLineSegment(sketch, "E2364", {"start": v(-47.42, -37.08) * mm, "end": v(-47.51, -36.66) * mm});
            skLineSegment(sketch, "E2365", {"start": v(-47.51, -36.66) * mm, "end": v(-47.63, -36.13) * mm});
            skLineSegment(sketch, "E2366", {"start": v(-47.63, -36.13) * mm, "end": v(-47.72, -35.6) * mm});
            skLineSegment(sketch, "E2367", {"start": v(-47.72, -35.6) * mm, "end": v(-47.72, -35.22) * mm});
            skLineSegment(sketch, "E2368", {"start": v(-47.72, -35.22) * mm, "end": v(-47.55, -34.94) * mm});
            skLineSegment(sketch, "E2369", {"start": v(-47.55, -34.94) * mm, "end": v(-47.33, -34.7) * mm});
            skLineSegment(sketch, "E2370", {"start": v(-47.33, -34.7) * mm, "end": v(-47.1, -34.24) * mm});
            skLineSegment(sketch, "E2371", {"start": v(-47.1, -34.24) * mm, "end": v(-46.79, -33.7) * mm});
            skLineSegment(sketch, "E2372", {"start": v(-46.79, -33.7) * mm, "end": v(-46.14, -33.17) * mm});
            skLineSegment(sketch, "E2373", {"start": v(-46.14, -33.17) * mm, "end": v(-45.46, -32.76) * mm});
            skLineSegment(sketch, "E2374", {"start": v(-45.46, -32.76) * mm, "end": v(-44.84, -32.56) * mm});
            skLineSegment(sketch, "E2375", {"start": v(-44.84, -32.56) * mm, "end": v(-44.2, -32.48) * mm});
            skLineSegment(sketch, "E2376", {"start": v(-44.2, -32.48) * mm, "end": v(-43.44, -32.42) * mm});
            skLineSegment(sketch, "E2377", {"start": v(-43.44, -32.42) * mm, "end": v(-43.05, -32.38) * mm});
            skLineSegment(sketch, "E2378", {"start": v(-43.05, -32.38) * mm, "end": v(-42.67, -32.34) * mm});
            skLineSegment(sketch, "E2379", {"start": v(-42.67, -32.34) * mm, "end": v(-42.76, -32.17) * mm});
            skLineSegment(sketch, "E2380", {"start": v(-42.76, -32.17) * mm, "end": v(-42.84, -32) * mm});
            skLineSegment(sketch, "E2381", {"start": v(-42.84, -32) * mm, "end": v(-42.46, -32.05) * mm});
            skLineSegment(sketch, "E2382", {"start": v(-42.46, -32.05) * mm, "end": v(-42.08, -32.09) * mm});
            skLineSegment(sketch, "E2383", {"start": v(-42.08, -32.09) * mm, "end": v(-42.23, -31.4) * mm});
            skLineSegment(sketch, "E2384", {"start": v(-42.23, -31.4) * mm, "end": v(-42.55, -30.73) * mm});
            skLineSegment(sketch, "E2385", {"start": v(-42.55, -30.73) * mm, "end": v(-42.87, -29.77) * mm});
            skLineSegment(sketch, "E2386", {"start": v(-42.87, -29.77) * mm, "end": v(-43.07, -28.79) * mm});
            skLineSegment(sketch, "E2387", {"start": v(-43.07, -28.79) * mm, "end": v(-43.1, -28.53) * mm});
            skLineSegment(sketch, "E2388", {"start": v(-43.1, -28.53) * mm, "end": v(-43.13, -27.98) * mm});
            skLineSegment(sketch, "E2389", {"start": v(-43.13, -27.98) * mm, "end": v(-43.18, -27.43) * mm});
            skLineSegment(sketch, "E2390", {"start": v(-43.18, -27.43) * mm, "end": v(-43.2, -27.18) * mm});
            skLineSegment(sketch, "E2391", {"start": v(-43.2, -27.18) * mm, "end": v(-43.32, -23.4) * mm});
            skLineSegment(sketch, "E2392", {"start": v(-43.32, -23.4) * mm, "end": v(-42.93, -19.64) * mm});
            skLineSegment(sketch, "E2393", {"start": v(-42.93, -19.64) * mm, "end": v(-42.8, -18.98) * mm});
            skLineSegment(sketch, "E2394", {"start": v(-42.8, -18.98) * mm, "end": v(-42.6, -18.17) * mm});
            skLineSegment(sketch, "E2395", {"start": v(-42.6, -18.17) * mm, "end": v(-42.36, -17.38) * mm});
            skLineSegment(sketch, "E2396", {"start": v(-42.36, -17.38) * mm, "end": v(-42.12, -16.76) * mm});
            skLineSegment(sketch, "E2397", {"start": v(-42.12, -16.76) * mm, "end": v(-41.97, -16.44) * mm});
            skLineSegment(sketch, "E2398", {"start": v(-41.97, -16.44) * mm, "end": v(-41.8, -16.18) * mm});
            skLineSegment(sketch, "E2399", {"start": v(-41.8, -16.18) * mm, "end": v(-41.57, -16.04) * mm});
            skLineSegment(sketch, "E2400", {"start": v(-41.57, -16.04) * mm, "end": v(-41.23, -16.09) * mm});
            skLineSegment(sketch, "E2401", {"start": v(-41.23, -16.09) * mm, "end": v(-41.2, -16) * mm});
            skLineSegment(sketch, "E2402", {"start": v(-41.2, -16) * mm, "end": v(-41.15, -15.92) * mm});
            skLineSegment(sketch, "E2403", {"start": v(-41.15, -15.92) * mm, "end": v(-41.06, -15.92) * mm});
            skLineSegment(sketch, "E2404", {"start": v(-41.06, -15.92) * mm, "end": v(-40.95, -16.15) * mm});
            skLineSegment(sketch, "E2405", {"start": v(-40.95, -16.15) * mm, "end": v(-40.73, -16.26) * mm});
            skLineSegment(sketch, "E2406", {"start": v(-40.73, -16.26) * mm, "end": v(-40.8, -17.07) * mm});
            skLineSegment(sketch, "E2407", {"start": v(-40.8, -17.07) * mm, "end": v(-41.06, -17.86) * mm});
            skLineSegment(sketch, "E2408", {"start": v(-41.06, -17.86) * mm, "end": v(-41.14, -18.27) * mm});
            skLineSegment(sketch, "E2409", {"start": v(-41.14, -18.27) * mm, "end": v(-41.32, -19.18) * mm});
            skLineSegment(sketch, "E2410", {"start": v(-41.32, -19.18) * mm, "end": v(-41.5, -20.08) * mm});
            skLineSegment(sketch, "E2411", {"start": v(-41.5, -20.08) * mm, "end": v(-41.57, -20.49) * mm});
            skLineSegment(sketch, "E2412", {"start": v(-41.57, -20.49) * mm, "end": v(-41.57, -25.15) * mm});
            skLineSegment(sketch, "E2413", {"start": v(-41.57, -25.15) * mm, "end": v(-41.45, -26.84) * mm});
            skLineSegment(sketch, "E2414", {"start": v(-41.45, -26.84) * mm, "end": v(-40.61, -29.46) * mm});
            skLineSegment(sketch, "E2415", {"start": v(-40.61, -29.46) * mm, "end": v(-40.44, -29.97) * mm});
            skLineSegment(sketch, "E2416", {"start": v(-40.44, -29.97) * mm, "end": v(-40.23, -30.61) * mm});
            skLineSegment(sketch, "E2417", {"start": v(-40.23, -30.61) * mm, "end": v(-40, -31.23) * mm});
            skLineSegment(sketch, "E2418", {"start": v(-40, -31.23) * mm, "end": v(-39.8, -31.67) * mm});
            skLineSegment(sketch, "E2419", {"start": v(-39.8, -31.67) * mm, "end": v(-39.78, -30.96) * mm});
            skLineSegment(sketch, "E2420", {"start": v(-39.78, -30.96) * mm, "end": v(-39.75, -30.5) * mm});
            skLineSegment(sketch, "E2421", {"start": v(-39.75, -30.5) * mm, "end": v(-39.68, -30.04) * mm});
            skLineSegment(sketch, "E2422", {"start": v(-39.68, -30.04) * mm, "end": v(-39.58, -29.38) * mm});
            skLineSegment(sketch, "E2423", {"start": v(-39.58, -29.38) * mm, "end": v(-39.17, -27) * mm});
            skLineSegment(sketch, "E2424", {"start": v(-39.17, -27) * mm, "end": v(-39.1, -26.82) * mm});
            skLineSegment(sketch, "E2425", {"start": v(-39.1, -26.82) * mm, "end": v(-38.95, -26.42) * mm});
            skLineSegment(sketch, "E2426", {"start": v(-38.95, -26.42) * mm, "end": v(-38.8, -26) * mm});
            skLineSegment(sketch, "E2427", {"start": v(-38.8, -26) * mm, "end": v(-38.73, -25.82) * mm});
            skLineSegment(sketch, "E2428", {"start": v(-38.73, -25.82) * mm, "end": v(-38.57, -25.43) * mm});
            skLineSegment(sketch, "E2429", {"start": v(-38.57, -25.43) * mm, "end": v(-38.22, -24.55) * mm});
            skLineSegment(sketch, "E2430", {"start": v(-38.22, -24.55) * mm, "end": v(-37.87, -23.68) * mm});
            skLineSegment(sketch, "E2431", {"start": v(-37.87, -23.68) * mm, "end": v(-37.71, -23.28) * mm});
            skLineSegment(sketch, "E2432", {"start": v(-37.71, -23.28) * mm, "end": v(-37.65, -23.14) * mm});
            skLineSegment(sketch, "E2433", {"start": v(-37.65, -23.14) * mm, "end": v(-37.5, -22.78) * mm});
            skLineSegment(sketch, "E2434", {"start": v(-37.5, -22.78) * mm, "end": v(-37.26, -22.26) * mm});
            skLineSegment(sketch, "E2435", {"start": v(-37.26, -22.26) * mm, "end": v(-37, -21.67) * mm});
            skLineSegment(sketch, "E2436", {"start": v(-37, -21.67) * mm, "end": v(-36.74, -21.08) * mm});
            skLineSegment(sketch, "E2437", {"start": v(-36.74, -21.08) * mm, "end": v(-36.5, -20.57) * mm});
            skLineSegment(sketch, "E2438", {"start": v(-36.5, -20.57) * mm, "end": v(-36.35, -20.2) * mm});
            skLineSegment(sketch, "E2439", {"start": v(-36.35, -20.2) * mm, "end": v(-36.28, -20.07) * mm});
            skLineSegment(sketch, "E2440", {"start": v(-36.28, -20.07) * mm, "end": v(-35.23, -18.66) * mm});
            skLineSegment(sketch, "E2441", {"start": v(-35.23, -18.66) * mm, "end": v(-34.04, -17.36) * mm});
            skLineSegment(sketch, "E2442", {"start": v(-34.04, -17.36) * mm, "end": v(-33.83, -17.17) * mm});
            skLineSegment(sketch, "E2443", {"start": v(-33.83, -17.17) * mm, "end": v(-33.55, -16.91) * mm});
            skLineSegment(sketch, "E2444", {"start": v(-33.55, -16.91) * mm, "end": v(-33.32, -16.64) * mm});
            skLineSegment(sketch, "E2445", {"start": v(-33.32, -16.64) * mm, "end": v(-33.27, -16.42) * mm});
            skLineSegment(sketch, "E2446", {"start": v(-33.27, -16.42) * mm, "end": v(-33.76, -16.13) * mm});
            skLineSegment(sketch, "E2447", {"start": v(-33.76, -16.13) * mm, "end": v(-34.36, -15.88) * mm});
            skLineSegment(sketch, "E2448", {"start": v(-34.36, -15.88) * mm, "end": v(-34.57, -15.6) * mm});
            skLineSegment(sketch, "E2449", {"start": v(-34.57, -15.6) * mm, "end": v(-35.02, -15.01) * mm});
            skLineSegment(sketch, "E2450", {"start": v(-35.02, -15.01) * mm, "end": v(-35.47, -14.41) * mm});
            skLineSegment(sketch, "E2451", {"start": v(-35.47, -14.41) * mm, "end": v(-35.67, -14.14) * mm});
            skLineSegment(sketch, "E2452", {"start": v(-35.67, -14.14) * mm, "end": v(-36.34, -13.5) * mm});
            skLineSegment(sketch, "E2453", {"start": v(-36.34, -13.5) * mm, "end": v(-36.86, -12.95) * mm});
            skLineSegment(sketch, "E2454", {"start": v(-36.86, -12.95) * mm, "end": v(-37.02, -12.69) * mm});
            skLineSegment(sketch, "E2455", {"start": v(-37.02, -12.69) * mm, "end": v(-37.16, -12.36) * mm});
            skLineSegment(sketch, "E2456", {"start": v(-37.16, -12.36) * mm, "end": v(-37.2, -12.03) * mm});
            skLineSegment(sketch, "E2457", {"start": v(-37.2, -12.03) * mm, "end": v(-37.09, -11.77) * mm});
            skLineSegment(sketch, "E2458", {"start": v(-37.09, -11.77) * mm, "end": v(-37.13, -11.6) * mm});
            skLineSegment(sketch, "E2459", {"start": v(-37.13, -11.6) * mm, "end": v(-37.17, -11.43) * mm});
            skLineSegment(sketch, "E2460", {"start": v(-37.17, -11.43) * mm, "end": v(-37.04, -11.39) * mm});
            skLineSegment(sketch, "E2461", {"start": v(-37.04, -11.39) * mm, "end": v(-36.92, -11.34) * mm});
            skLineSegment(sketch, "E2462", {"start": v(-36.92, -11.34) * mm, "end": v(-36.88, -10.72) * mm});
            skLineSegment(sketch, "E2463", {"start": v(-36.88, -10.72) * mm, "end": v(-36.66, -10.08) * mm});
            skLineSegment(sketch, "E2464", {"start": v(-36.66, -10.08) * mm, "end": v(-36.04, -10.13) * mm});
            skLineSegment(sketch, "E2465", {"start": v(-36.04, -10.13) * mm, "end": v(-35.7, -10.26) * mm});
            skLineSegment(sketch, "E2466", {"start": v(-35.7, -10.26) * mm, "end": v(-35.44, -10.39) * mm});
            skLineSegment(sketch, "E2467", {"start": v(-35.44, -10.39) * mm, "end": v(-35.14, -10.47) * mm});
            skLineSegment(sketch, "E2468", {"start": v(-57.74, -10.24) * mm, "end": v(-57.66, -10.33) * mm});
            skLineSegment(sketch, "E2469", {"start": v(-57.66, -10.33) * mm, "end": v(-57.66, -10.24) * mm});
            skLineSegment(sketch, "E2470", {"start": v(-57.66, -10.24) * mm, "end": v(-57.74, -10.24) * mm});
            skLineSegment(sketch, "E2471", {"start": v(-53, -11) * mm, "end": v(-52.92, -11.1) * mm});
            skLineSegment(sketch, "E2472", {"start": v(-52.92, -11.1) * mm, "end": v(-52.92, -11) * mm});
            skLineSegment(sketch, "E2473", {"start": v(-52.92, -11) * mm, "end": v(-53, -11) * mm});
            skLineSegment(sketch, "E2474", {"start": v(-54.7, -12.1) * mm, "end": v(-54.61, -12.2) * mm});
            skLineSegment(sketch, "E2475", {"start": v(-54.61, -12.2) * mm, "end": v(-54.61, -12.1) * mm});
            skLineSegment(sketch, "E2476", {"start": v(-54.61, -12.1) * mm, "end": v(-54.7, -12.1) * mm});
            skLineSegment(sketch, "E2477", {"start": v(-53.93, -12.53) * mm, "end": v(-53.85, -12.62) * mm});
            skLineSegment(sketch, "E2478", {"start": v(-53.85, -12.62) * mm, "end": v(-53.85, -12.53) * mm});
            skLineSegment(sketch, "E2479", {"start": v(-53.85, -12.53) * mm, "end": v(-53.93, -12.53) * mm});
            skLineSegment(sketch, "E2480", {"start": v(-53.76, -12.7) * mm, "end": v(-53.68, -12.78) * mm});
            skLineSegment(sketch, "E2481", {"start": v(-53.68, -12.78) * mm, "end": v(-53.68, -12.7) * mm});
            skLineSegment(sketch, "E2482", {"start": v(-53.68, -12.7) * mm, "end": v(-53.76, -12.7) * mm});
            skLineSegment(sketch, "E2483", {"start": v(-30.65, -13.44) * mm, "end": v(-31.1, -13.22) * mm});
            skLineSegment(sketch, "E2484", {"start": v(-31.1, -13.22) * mm, "end": v(-31.5, -13) * mm});
            skLineSegment(sketch, "E2485", {"start": v(-31.5, -13) * mm, "end": v(-32.04, -12.86) * mm});
            skLineSegment(sketch, "E2486", {"start": v(-32.04, -12.86) * mm, "end": v(-32.6, -12.78) * mm});
            skLineSegment(sketch, "E2487", {"start": v(-32.6, -12.78) * mm, "end": v(-32.12, -13.14) * mm});
            skLineSegment(sketch, "E2488", {"start": v(-32.12, -13.14) * mm, "end": v(-31.58, -13.4) * mm});
            skLineSegment(sketch, "E2489", {"start": v(-31.58, -13.4) * mm, "end": v(-31.26, -13.65) * mm});
            skLineSegment(sketch, "E2490", {"start": v(-31.26, -13.65) * mm, "end": v(-31.1, -13.84) * mm});
            skLineSegment(sketch, "E2491", {"start": v(-31.1, -13.84) * mm, "end": v(-31, -14) * mm});
            skLineSegment(sketch, "E2492", {"start": v(-31, -14) * mm, "end": v(-30.81, -14.14) * mm});
            skLineSegment(sketch, "E2493", {"start": v(-30.81, -14.14) * mm, "end": v(-29.83, -14.29) * mm});
            skLineSegment(sketch, "E2494", {"start": v(-29.83, -14.29) * mm, "end": v(-28.79, -14.22) * mm});
            skLineSegment(sketch, "E2495", {"start": v(-28.79, -14.22) * mm, "end": v(-29.64, -13.67) * mm});
            skLineSegment(sketch, "E2496", {"start": v(-29.64, -13.67) * mm, "end": v(-30.65, -13.44) * mm});
            skLineSegment(sketch, "E2497", {"start": v(-85.1, -15.66) * mm, "end": v(-85, -15.75) * mm});
            skLineSegment(sketch, "E2498", {"start": v(-85, -15.75) * mm, "end": v(-85, -15.66) * mm});
            skLineSegment(sketch, "E2499", {"start": v(-85, -15.66) * mm, "end": v(-85.1, -15.66) * mm});
            skLineSegment(sketch, "E2500", {"start": v(-26.08, -16.76) * mm, "end": v(-26.04, -16.89) * mm});
            skLineSegment(sketch, "E2501", {"start": v(-26.04, -16.89) * mm, "end": v(-26, -17.02) * mm});
            skLineSegment(sketch, "E2502", {"start": v(-26, -17.02) * mm, "end": v(-25.95, -16.89) * mm});
            skLineSegment(sketch, "E2503", {"start": v(-25.95, -16.89) * mm, "end": v(-25.9, -16.76) * mm});
            skLineSegment(sketch, "E2504", {"start": v(-25.9, -16.76) * mm, "end": v(-25.83, -17.1) * mm});
            skLineSegment(sketch, "E2505", {"start": v(-25.83, -17.1) * mm, "end": v(-25.74, -17.44) * mm});
            skLineSegment(sketch, "E2506", {"start": v(-25.74, -17.44) * mm, "end": v(-25.72, -17.05) * mm});
            skLineSegment(sketch, "E2507", {"start": v(-25.72, -17.05) * mm, "end": v(-25.49, -16.76) * mm});
            skLineSegment(sketch, "E2508", {"start": v(-25.49, -16.76) * mm, "end": v(-25.36, -16.89) * mm});
            skLineSegment(sketch, "E2509", {"start": v(-25.36, -16.89) * mm, "end": v(-25.23, -17.02) * mm});
            skLineSegment(sketch, "E2510", {"start": v(-25.23, -17.02) * mm, "end": v(-25.13, -17.43) * mm});
            skLineSegment(sketch, "E2511", {"start": v(-25.13, -17.43) * mm, "end": v(-24.97, -17.65) * mm});
            skLineSegment(sketch, "E2512", {"start": v(-24.97, -17.65) * mm, "end": v(-24.79, -17.83) * mm});
            skLineSegment(sketch, "E2513", {"start": v(-24.79, -17.83) * mm, "end": v(-24.6, -18.12) * mm});
            skLineSegment(sketch, "E2514", {"start": v(-24.6, -18.12) * mm, "end": v(-24.4, -18.65) * mm});
            skLineSegment(sketch, "E2515", {"start": v(-24.4, -18.65) * mm, "end": v(-24.15, -19.36) * mm});
            skLineSegment(sketch, "E2516", {"start": v(-24.15, -19.36) * mm, "end": v(-23.93, -20.1) * mm});
            skLineSegment(sketch, "E2517", {"start": v(-23.93, -20.1) * mm, "end": v(-23.78, -20.66) * mm});
            skLineSegment(sketch, "E2518", {"start": v(-23.78, -20.66) * mm, "end": v(-23.74, -21.02) * mm});
            skLineSegment(sketch, "E2519", {"start": v(-23.74, -21.02) * mm, "end": v(-23.64, -21.8) * mm});
            skLineSegment(sketch, "E2520", {"start": v(-23.64, -21.8) * mm, "end": v(-23.55, -22.59) * mm});
            skLineSegment(sketch, "E2521", {"start": v(-23.55, -22.59) * mm, "end": v(-23.5, -22.94) * mm});
            skLineSegment(sketch, "E2522", {"start": v(-23.5, -22.94) * mm, "end": v(-23.45, -23.2) * mm});
            skLineSegment(sketch, "E2523", {"start": v(-23.45, -23.2) * mm, "end": v(-23.33, -23.75) * mm});
            skLineSegment(sketch, "E2524", {"start": v(-23.33, -23.75) * mm, "end": v(-23.2, -24.3) * mm});
            skLineSegment(sketch, "E2525", {"start": v(-23.2, -24.3) * mm, "end": v(-23.15, -24.55) * mm});
            skLineSegment(sketch, "E2526", {"start": v(-23.15, -24.55) * mm, "end": v(-23.1, -24.8) * mm});
            skLineSegment(sketch, "E2527", {"start": v(-23.1, -24.8) * mm, "end": v(-22.98, -25.36) * mm});
            skLineSegment(sketch, "E2528", {"start": v(-22.98, -25.36) * mm, "end": v(-22.87, -25.9) * mm});
            skLineSegment(sketch, "E2529", {"start": v(-22.87, -25.9) * mm, "end": v(-22.82, -26.16) * mm});
            skLineSegment(sketch, "E2530", {"start": v(-22.82, -26.16) * mm, "end": v(-22.77, -26.36) * mm});
            skLineSegment(sketch, "E2531", {"start": v(-22.77, -26.36) * mm, "end": v(-22.64, -26.9) * mm});
            skLineSegment(sketch, "E2532", {"start": v(-22.64, -26.9) * mm, "end": v(-22.47, -27.66) * mm});
            skLineSegment(sketch, "E2533", {"start": v(-22.47, -27.66) * mm, "end": v(-22.26, -28.53) * mm});
            skLineSegment(sketch, "E2534", {"start": v(-22.26, -28.53) * mm, "end": v(-22.05, -29.4) * mm});
            skLineSegment(sketch, "E2535", {"start": v(-22.05, -29.4) * mm, "end": v(-21.88, -30.16) * mm});
            skLineSegment(sketch, "E2536", {"start": v(-21.88, -30.16) * mm, "end": v(-21.75, -30.7) * mm});
            skLineSegment(sketch, "E2537", {"start": v(-21.75, -30.7) * mm, "end": v(-21.7, -30.9) * mm});
            skLineSegment(sketch, "E2538", {"start": v(-21.7, -30.9) * mm, "end": v(-21.68, -31.1) * mm});
            skLineSegment(sketch, "E2539", {"start": v(-21.68, -31.1) * mm, "end": v(-21.64, -31.54) * mm});
            skLineSegment(sketch, "E2540", {"start": v(-21.64, -31.54) * mm, "end": v(-21.6, -31.97) * mm});
            skLineSegment(sketch, "E2541", {"start": v(-21.6, -31.97) * mm, "end": v(-21.58, -32.17) * mm});
            skLineSegment(sketch, "E2542", {"start": v(-21.58, -32.17) * mm, "end": v(-21.55, -32.6) * mm});
            skLineSegment(sketch, "E2543", {"start": v(-21.55, -32.6) * mm, "end": v(-21.5, -33.02) * mm});
            skLineSegment(sketch, "E2544", {"start": v(-21.5, -33.02) * mm, "end": v(-21.66, -34.74) * mm});
            skLineSegment(sketch, "E2545", {"start": v(-21.66, -34.74) * mm, "end": v(-22.07, -36.4) * mm});
            skLineSegment(sketch, "E2546", {"start": v(-22.07, -36.4) * mm, "end": v(-22.4, -37.7) * mm});
            skLineSegment(sketch, "E2547", {"start": v(-22.4, -37.7) * mm, "end": v(-22.85, -38.95) * mm});
            skLineSegment(sketch, "E2548", {"start": v(-22.85, -38.95) * mm, "end": v(-23, -39.21) * mm});
            skLineSegment(sketch, "E2549", {"start": v(-23, -39.21) * mm, "end": v(-23.33, -39.8) * mm});
            skLineSegment(sketch, "E2550", {"start": v(-23.33, -39.8) * mm, "end": v(-23.66, -40.37) * mm});
            skLineSegment(sketch, "E2551", {"start": v(-23.66, -40.37) * mm, "end": v(-23.81, -40.64) * mm});
            skLineSegment(sketch, "E2552", {"start": v(-23.81, -40.64) * mm, "end": v(-24, -41.02) * mm});
            skLineSegment(sketch, "E2553", {"start": v(-24, -41.02) * mm, "end": v(-24.4, -41.87) * mm});
            skLineSegment(sketch, "E2554", {"start": v(-24.4, -41.87) * mm, "end": v(-24.8, -42.71) * mm});
            skLineSegment(sketch, "E2555", {"start": v(-24.8, -42.71) * mm, "end": v(-24.99, -43.1) * mm});
            skLineSegment(sketch, "E2556", {"start": v(-24.99, -43.1) * mm, "end": v(-25.32, -43.95) * mm});
            skLineSegment(sketch, "E2557", {"start": v(-25.32, -43.95) * mm, "end": v(-25.65, -44.65) * mm});
            skLineSegment(sketch, "E2558", {"start": v(-25.65, -44.65) * mm, "end": v(-26.15, -45.21) * mm});
            skLineSegment(sketch, "E2559", {"start": v(-26.15, -45.21) * mm, "end": v(-27.01, -45.63) * mm});
            skLineSegment(sketch, "E2560", {"start": v(-27.01, -45.63) * mm, "end": v(-27.18, -45.34) * mm});
            skLineSegment(sketch, "E2561", {"start": v(-27.18, -45.34) * mm, "end": v(-27.35, -45.04) * mm});
            skLineSegment(sketch, "E2562", {"start": v(-27.35, -45.04) * mm, "end": v(-27, -43.77) * mm});
            skLineSegment(sketch, "E2563", {"start": v(-27, -43.77) * mm, "end": v(-26.42, -42.43) * mm});
            skLineSegment(sketch, "E2564", {"start": v(-26.42, -42.43) * mm, "end": v(-25.74, -41.12) * mm});
            skLineSegment(sketch, "E2565", {"start": v(-25.74, -41.12) * mm, "end": v(-25.06, -39.96) * mm});
            skLineSegment(sketch, "E2566", {"start": v(-25.06, -39.96) * mm, "end": v(-24.91, -39.71) * mm});
            skLineSegment(sketch, "E2567", {"start": v(-24.91, -39.71) * mm, "end": v(-24.59, -39.16) * mm});
            skLineSegment(sketch, "E2568", {"start": v(-24.59, -39.16) * mm, "end": v(-24.26, -38.6) * mm});
            skLineSegment(sketch, "E2569", {"start": v(-24.26, -38.6) * mm, "end": v(-24.11, -38.35) * mm});
            skLineSegment(sketch, "E2570", {"start": v(-24.11, -38.35) * mm, "end": v(-23.69, -37.23) * mm});
            skLineSegment(sketch, "E2571", {"start": v(-23.69, -37.23) * mm, "end": v(-23.36, -36.07) * mm});
            skLineSegment(sketch, "E2572", {"start": v(-23.36, -36.07) * mm, "end": v(-23.1, -35.02) * mm});
            skLineSegment(sketch, "E2573", {"start": v(-23.1, -35.02) * mm, "end": v(-22.99, -33.95) * mm});
            skLineSegment(sketch, "E2574", {"start": v(-22.99, -33.95) * mm, "end": v(-23.41, -31.03) * mm});
            skLineSegment(sketch, "E2575", {"start": v(-23.41, -31.03) * mm, "end": v(-24.24, -28.2) * mm});
            skLineSegment(sketch, "E2576", {"start": v(-24.24, -28.2) * mm, "end": v(-24.34, -27.93) * mm});
            skLineSegment(sketch, "E2577", {"start": v(-24.34, -27.93) * mm, "end": v(-24.54, -27.35) * mm});
            skLineSegment(sketch, "E2578", {"start": v(-24.54, -27.35) * mm, "end": v(-24.74, -26.76) * mm});
            skLineSegment(sketch, "E2579", {"start": v(-24.74, -26.76) * mm, "end": v(-24.83, -26.5) * mm});
            skLineSegment(sketch, "E2580", {"start": v(-24.83, -26.5) * mm, "end": v(-24.87, -26.34) * mm});
            skLineSegment(sketch, "E2581", {"start": v(-24.87, -26.34) * mm, "end": v(-24.97, -25.9) * mm});
            skLineSegment(sketch, "E2582", {"start": v(-24.97, -25.9) * mm, "end": v(-25.11, -25.3) * mm});
            skLineSegment(sketch, "E2583", {"start": v(-25.11, -25.3) * mm, "end": v(-25.27, -24.6) * mm});
            skLineSegment(sketch, "E2584", {"start": v(-25.27, -24.6) * mm, "end": v(-25.44, -23.9) * mm});
            skLineSegment(sketch, "E2585", {"start": v(-25.44, -23.9) * mm, "end": v(-25.58, -23.29) * mm});
            skLineSegment(sketch, "E2586", {"start": v(-25.58, -23.29) * mm, "end": v(-25.68, -22.85) * mm});
            skLineSegment(sketch, "E2587", {"start": v(-25.68, -22.85) * mm, "end": v(-25.71, -22.7) * mm});
            skLineSegment(sketch, "E2588", {"start": v(-25.71, -22.7) * mm, "end": v(-26.25, -20.72) * mm});
            skLineSegment(sketch, "E2589", {"start": v(-26.25, -20.72) * mm, "end": v(-26.6, -18.71) * mm});
            skLineSegment(sketch, "E2590", {"start": v(-26.6, -18.71) * mm, "end": v(-26.67, -17.77) * mm});
            skLineSegment(sketch, "E2591", {"start": v(-26.67, -17.77) * mm, "end": v(-26.5, -16.85) * mm});
            skLineSegment(sketch, "E2592", {"start": v(-26.5, -16.85) * mm, "end": v(-26.42, -16.76) * mm});
            skLineSegment(sketch, "E2593", {"start": v(-26.42, -16.76) * mm, "end": v(-26.33, -16.68) * mm});
            skLineSegment(sketch, "E2594", {"start": v(-26.33, -16.68) * mm, "end": v(-26.2, -16.72) * mm});
            skLineSegment(sketch, "E2595", {"start": v(-26.2, -16.72) * mm, "end": v(-26.08, -16.76) * mm});
            skLineSegment(sketch, "E2596", {"start": v(-31.75, -18.29) * mm, "end": v(-31.67, -18.37) * mm});
            skLineSegment(sketch, "E2597", {"start": v(-31.67, -18.37) * mm, "end": v(-31.67, -18.29) * mm});
            skLineSegment(sketch, "E2598", {"start": v(-31.67, -18.29) * mm, "end": v(-31.75, -18.29) * mm});
            skLineSegment(sketch, "E2599", {"start": v(-31.41, -18.46) * mm, "end": v(-31.33, -18.54) * mm});
            skLineSegment(sketch, "E2600", {"start": v(-31.33, -18.54) * mm, "end": v(-31.33, -18.46) * mm});
            skLineSegment(sketch, "E2601", {"start": v(-31.33, -18.46) * mm, "end": v(-31.41, -18.46) * mm});
            skLineSegment(sketch, "E2602", {"start": v(-59.6, -21.5) * mm, "end": v(-59.59, -21.76) * mm});
            skLineSegment(sketch, "E2603", {"start": v(-59.59, -21.76) * mm, "end": v(-59.54, -22.3) * mm});
            skLineSegment(sketch, "E2604", {"start": v(-59.54, -22.3) * mm, "end": v(-59.5, -22.86) * mm});
            skLineSegment(sketch, "E2605", {"start": v(-59.5, -22.86) * mm, "end": v(-59.47, -23.11) * mm});
            skLineSegment(sketch, "E2606", {"start": v(-59.47, -23.11) * mm, "end": v(-59.57, -23.66) * mm});
            skLineSegment(sketch, "E2607", {"start": v(-59.57, -23.66) * mm, "end": v(-59.64, -24.38) * mm});
            skLineSegment(sketch, "E2608", {"start": v(-59.64, -24.38) * mm, "end": v(-59.66, -24.76) * mm});
            skLineSegment(sketch, "E2609", {"start": v(-59.66, -24.76) * mm, "end": v(-59.68, -25.15) * mm});
            skLineSegment(sketch, "E2610", {"start": v(-59.68, -25.15) * mm, "end": v(-59.67, -25.34) * mm});
            skLineSegment(sketch, "E2611", {"start": v(-59.67, -25.34) * mm, "end": v(-59.64, -25.78) * mm});
            skLineSegment(sketch, "E2612", {"start": v(-59.64, -25.78) * mm, "end": v(-59.6, -26.22) * mm});
            skLineSegment(sketch, "E2613", {"start": v(-59.6, -26.22) * mm, "end": v(-59.6, -26.42) * mm});
            skLineSegment(sketch, "E2614", {"start": v(-59.6, -26.42) * mm, "end": v(-59.5, -27.07) * mm});
            skLineSegment(sketch, "E2615", {"start": v(-59.5, -27.07) * mm, "end": v(-59.4, -27.47) * mm});
            skLineSegment(sketch, "E2616", {"start": v(-59.4, -27.47) * mm, "end": v(-59.28, -27.82) * mm});
            skLineSegment(sketch, "E2617", {"start": v(-59.28, -27.82) * mm, "end": v(-59.11, -28.36) * mm});
            skLineSegment(sketch, "E2618", {"start": v(-59.11, -28.36) * mm, "end": v(-59.07, -28.6) * mm});
            skLineSegment(sketch, "E2619", {"start": v(-59.07, -28.6) * mm, "end": v(-58.96, -29.13) * mm});
            skLineSegment(sketch, "E2620", {"start": v(-58.96, -29.13) * mm, "end": v(-58.86, -29.65) * mm});
            skLineSegment(sketch, "E2621", {"start": v(-58.86, -29.65) * mm, "end": v(-58.81, -29.89) * mm});
            skLineSegment(sketch, "E2622", {"start": v(-58.81, -29.89) * mm, "end": v(-58.7, -30.86) * mm});
            skLineSegment(sketch, "E2623", {"start": v(-58.7, -30.86) * mm, "end": v(-58.81, -31.8) * mm});
            skLineSegment(sketch, "E2624", {"start": v(-58.81, -31.8) * mm, "end": v(-58.96, -32.15) * mm});
            skLineSegment(sketch, "E2625", {"start": v(-58.96, -32.15) * mm, "end": v(-59.27, -32.34) * mm});
            skLineSegment(sketch, "E2626", {"start": v(-59.27, -32.34) * mm, "end": v(-59.27, -32.51) * mm});
            skLineSegment(sketch, "E2627", {"start": v(-59.27, -32.51) * mm, "end": v(-59.27, -32.68) * mm});
            skLineSegment(sketch, "E2628", {"start": v(-59.27, -32.68) * mm, "end": v(-59.54, -32.8) * mm});
            skLineSegment(sketch, "E2629", {"start": v(-59.54, -32.8) * mm, "end": v(-59.83, -32.8) * mm});
            skLineSegment(sketch, "E2630", {"start": v(-59.83, -32.8) * mm, "end": v(-60.05, -32.49) * mm});
            skLineSegment(sketch, "E2631", {"start": v(-60.05, -32.49) * mm, "end": v(-60.14, -32.09) * mm});
            skLineSegment(sketch, "E2632", {"start": v(-60.14, -32.09) * mm, "end": v(-60.3, -31.47) * mm});
            skLineSegment(sketch, "E2633", {"start": v(-60.3, -31.47) * mm, "end": v(-60.4, -31.1) * mm});
            skLineSegment(sketch, "E2634", {"start": v(-60.4, -31.1) * mm, "end": v(-60.55, -30.77) * mm});
            skLineSegment(sketch, "E2635", {"start": v(-60.55, -30.77) * mm, "end": v(-60.75, -30.22) * mm});
            skLineSegment(sketch, "E2636", {"start": v(-60.75, -30.22) * mm, "end": v(-60.96, -29.43) * mm});
            skLineSegment(sketch, "E2637", {"start": v(-60.96, -29.43) * mm, "end": v(-61.05, -28.62) * mm});
            skLineSegment(sketch, "E2638", {"start": v(-61.05, -28.62) * mm, "end": v(-61.06, -28.36) * mm});
            skLineSegment(sketch, "E2639", {"start": v(-61.06, -28.36) * mm, "end": v(-61.09, -27.81) * mm});
            skLineSegment(sketch, "E2640", {"start": v(-61.09, -27.81) * mm, "end": v(-61.11, -27.26) * mm});
            skLineSegment(sketch, "E2641", {"start": v(-61.11, -27.26) * mm, "end": v(-61.13, -27) * mm});
            skLineSegment(sketch, "E2642", {"start": v(-61.13, -27) * mm, "end": v(-61.07, -26.57) * mm});
            skLineSegment(sketch, "E2643", {"start": v(-61.07, -26.57) * mm, "end": v(-60.95, -25.61) * mm});
            skLineSegment(sketch, "E2644", {"start": v(-60.95, -25.61) * mm, "end": v(-60.83, -24.65) * mm});
            skLineSegment(sketch, "E2645", {"start": v(-60.83, -24.65) * mm, "end": v(-60.77, -24.21) * mm});
            skLineSegment(sketch, "E2646", {"start": v(-60.77, -24.21) * mm, "end": v(-60.74, -24) * mm});
            skLineSegment(sketch, "E2647", {"start": v(-60.74, -24) * mm, "end": v(-60.66, -23.54) * mm});
            skLineSegment(sketch, "E2648", {"start": v(-60.66, -23.54) * mm, "end": v(-60.6, -23.07) * mm});
            skLineSegment(sketch, "E2649", {"start": v(-60.6, -23.07) * mm, "end": v(-60.56, -22.86) * mm});
            skLineSegment(sketch, "E2650", {"start": v(-60.56, -22.86) * mm, "end": v(-60.47, -22.65) * mm});
            skLineSegment(sketch, "E2651", {"start": v(-60.47, -22.65) * mm, "end": v(-60.3, -22.18) * mm});
            skLineSegment(sketch, "E2652", {"start": v(-60.3, -22.18) * mm, "end": v(-60.11, -21.72) * mm});
            skLineSegment(sketch, "E2653", {"start": v(-60.11, -21.72) * mm, "end": v(-60.03, -21.5) * mm});
            skLineSegment(sketch, "E2654", {"start": v(-60.03, -21.5) * mm, "end": v(-59.82, -21.5) * mm});
            skLineSegment(sketch, "E2655", {"start": v(-59.82, -21.5) * mm, "end": v(-59.6, -21.5) * mm});
            skLineSegment(sketch, "E2656", {"start": v(-78.06, -23.2) * mm, "end": v(-77.98, -23.28) * mm});
            skLineSegment(sketch, "E2657", {"start": v(-77.98, -23.28) * mm, "end": v(-77.98, -23.2) * mm});
            skLineSegment(sketch, "E2658", {"start": v(-77.98, -23.2) * mm, "end": v(-78.06, -23.2) * mm});
            skLineSegment(sketch, "E2659", {"start": v(-28.2, -23.28) * mm, "end": v(-28.11, -23.37) * mm});
            skLineSegment(sketch, "E2660", {"start": v(-28.11, -23.37) * mm, "end": v(-28.11, -23.28) * mm});
            skLineSegment(sketch, "E2661", {"start": v(-28.11, -23.28) * mm, "end": v(-28.2, -23.28) * mm});
            skLineSegment(sketch, "E2662", {"start": v(-28.11, -23.45) * mm, "end": v(-28.03, -23.54) * mm});
            skLineSegment(sketch, "E2663", {"start": v(-28.03, -23.54) * mm, "end": v(-28.03, -23.45) * mm});
            skLineSegment(sketch, "E2664", {"start": v(-28.03, -23.45) * mm, "end": v(-28.11, -23.45) * mm});
            skLineSegment(sketch, "E2665", {"start": v(-28.03, -23.62) * mm, "end": v(-27.94, -23.7) * mm});
            skLineSegment(sketch, "E2666", {"start": v(-27.94, -23.7) * mm, "end": v(-27.94, -23.62) * mm});
            skLineSegment(sketch, "E2667", {"start": v(-27.94, -23.62) * mm, "end": v(-28.03, -23.62) * mm});
            skLineSegment(sketch, "E2668", {"start": v(-27.94, -23.8) * mm, "end": v(-27.86, -23.87) * mm});
            skLineSegment(sketch, "E2669", {"start": v(-27.86, -23.87) * mm, "end": v(-27.86, -23.8) * mm});
            skLineSegment(sketch, "E2670", {"start": v(-27.86, -23.8) * mm, "end": v(-27.94, -23.8) * mm});
            skLineSegment(sketch, "E2671", {"start": v(-37.68, -26.84) * mm, "end": v(-38.1, -28.4) * mm});
            skLineSegment(sketch, "E2672", {"start": v(-38.1, -28.4) * mm, "end": v(-38.37, -29.97) * mm});
            skLineSegment(sketch, "E2673", {"start": v(-38.37, -29.97) * mm, "end": v(-38.44, -30.58) * mm});
            skLineSegment(sketch, "E2674", {"start": v(-38.44, -30.58) * mm, "end": v(-38.46, -31.15) * mm});
            skLineSegment(sketch, "E2675", {"start": v(-38.46, -31.15) * mm, "end": v(-38.22, -31.49) * mm});
            skLineSegment(sketch, "E2676", {"start": v(-38.22, -31.49) * mm, "end": v(-37.92, -31.83) * mm});
            skLineSegment(sketch, "E2677", {"start": v(-37.92, -31.83) * mm, "end": v(-37.83, -32.14) * mm});
            skLineSegment(sketch, "E2678", {"start": v(-37.83, -32.14) * mm, "end": v(-37.74, -32.56) * mm});
            skLineSegment(sketch, "E2679", {"start": v(-37.74, -32.56) * mm, "end": v(-37.6, -32.93) * mm});
            skLineSegment(sketch, "E2680", {"start": v(-37.6, -32.93) * mm, "end": v(-37.34, -33.09) * mm});
            skLineSegment(sketch, "E2681", {"start": v(-37.34, -33.09) * mm, "end": v(-37.05, -32.92) * mm});
            skLineSegment(sketch, "E2682", {"start": v(-37.05, -32.92) * mm, "end": v(-36.79, -32.6) * mm});
            skLineSegment(sketch, "E2683", {"start": v(-36.79, -32.6) * mm, "end": v(-36.7, -32.33) * mm});
            skLineSegment(sketch, "E2684", {"start": v(-36.7, -32.33) * mm, "end": v(-36.65, -32.07) * mm});
            skLineSegment(sketch, "E2685", {"start": v(-36.65, -32.07) * mm, "end": v(-36.55, -31.75) * mm});
            skLineSegment(sketch, "E2686", {"start": v(-36.55, -31.75) * mm, "end": v(-36.11, -31.2) * mm});
            skLineSegment(sketch, "E2687", {"start": v(-36.11, -31.2) * mm, "end": v(-35.48, -30.9) * mm});
            skLineSegment(sketch, "E2688", {"start": v(-35.48, -30.9) * mm, "end": v(-35.9, -30.23) * mm});
            skLineSegment(sketch, "E2689", {"start": v(-35.9, -30.23) * mm, "end": v(-36.42, -29.63) * mm});
            skLineSegment(sketch, "E2690", {"start": v(-36.42, -29.63) * mm, "end": v(-37.22, -28.33) * mm});
            skLineSegment(sketch, "E2691", {"start": v(-37.22, -28.33) * mm, "end": v(-37.5, -26.84) * mm});
            skLineSegment(sketch, "E2692", {"start": v(-37.5, -26.84) * mm, "end": v(-37.68, -26.84) * mm});
            skLineSegment(sketch, "E2693", {"start": v(-40.05, -32.09) * mm, "end": v(-40.13, -32.43) * mm});
            skLineSegment(sketch, "E2694", {"start": v(-40.13, -32.43) * mm, "end": v(-40.22, -32.77) * mm});
            skLineSegment(sketch, "E2695", {"start": v(-40.22, -32.77) * mm, "end": v(-39.93, -32.49) * mm});
            skLineSegment(sketch, "E2696", {"start": v(-39.93, -32.49) * mm, "end": v(-39.88, -32.09) * mm});
            skLineSegment(sketch, "E2697", {"start": v(-39.88, -32.09) * mm, "end": v(-40.05, -32.09) * mm});
            skLineSegment(sketch, "E2698", {"start": v(-37.25, -34.54) * mm, "end": v(-37.17, -34.63) * mm});
            skLineSegment(sketch, "E2699", {"start": v(-37.17, -34.63) * mm, "end": v(-37.17, -34.54) * mm});
            skLineSegment(sketch, "E2700", {"start": v(-37.17, -34.54) * mm, "end": v(-37.25, -34.54) * mm});
            skLineSegment(sketch, "E2701", {"start": v(-62.74, -37.68) * mm, "end": v(-62.57, -37.68) * mm});
            skLineSegment(sketch, "E2702", {"start": v(-62.57, -37.68) * mm, "end": v(-61.96, -36.69) * mm});
            skLineSegment(sketch, "E2703", {"start": v(-61.96, -36.69) * mm, "end": v(-61.47, -35.64) * mm});
            skLineSegment(sketch, "E2704", {"start": v(-61.47, -35.64) * mm, "end": v(-61.64, -35.49) * mm});
            skLineSegment(sketch, "E2705", {"start": v(-61.64, -35.49) * mm, "end": v(-62.02, -35.14) * mm});
            skLineSegment(sketch, "E2706", {"start": v(-62.02, -35.14) * mm, "end": v(-62.4, -34.79) * mm});
            skLineSegment(sketch, "E2707", {"start": v(-62.4, -34.79) * mm, "end": v(-62.57, -34.63) * mm});
            skLineSegment(sketch, "E2708", {"start": v(-62.57, -34.63) * mm, "end": v(-62.79, -35.27) * mm});
            skLineSegment(sketch, "E2709", {"start": v(-62.79, -35.27) * mm, "end": v(-62.88, -36.12) * mm});
            skLineSegment(sketch, "E2710", {"start": v(-62.88, -36.12) * mm, "end": v(-62.86, -36.99) * mm});
            skLineSegment(sketch, "E2711", {"start": v(-62.86, -36.99) * mm, "end": v(-62.74, -37.68) * mm});
            skLineSegment(sketch, "E2712", {"start": v(-59.6, -46.48) * mm, "end": v(-59.5, -47.2) * mm});
            skLineSegment(sketch, "E2713", {"start": v(-59.5, -47.2) * mm, "end": v(-59.35, -47.92) * mm});
            skLineSegment(sketch, "E2714", {"start": v(-59.35, -47.92) * mm, "end": v(-58.67, -49.45) * mm});
            skLineSegment(sketch, "E2715", {"start": v(-58.67, -49.45) * mm, "end": v(-57.71, -50.96) * mm});
            skLineSegment(sketch, "E2716", {"start": v(-57.71, -50.96) * mm, "end": v(-56.79, -52.35) * mm});
            skLineSegment(sketch, "E2717", {"start": v(-56.79, -52.35) * mm, "end": v(-56.18, -53.5) * mm});
            skLineSegment(sketch, "E2718", {"start": v(-56.18, -53.5) * mm, "end": v(-56.05, -54.27) * mm});
            skLineSegment(sketch, "E2719", {"start": v(-56.05, -54.27) * mm, "end": v(-56.22, -54.27) * mm});
            skLineSegment(sketch, "E2720", {"start": v(-56.22, -54.27) * mm, "end": v(-56.14, -54.64) * mm});
            skLineSegment(sketch, "E2721", {"start": v(-56.14, -54.64) * mm, "end": v(-56.3, -54.95) * mm});
            skLineSegment(sketch, "E2722", {"start": v(-56.3, -54.95) * mm, "end": v(-56.3, -55.16) * mm});
            skLineSegment(sketch, "E2723", {"start": v(-56.3, -55.16) * mm, "end": v(-56.3, -55.37) * mm});
            skLineSegment(sketch, "E2724", {"start": v(-56.3, -55.37) * mm, "end": v(-56.14, -55.17) * mm});
            skLineSegment(sketch, "E2725", {"start": v(-56.14, -55.17) * mm, "end": v(-55.79, -54.74) * mm});
            skLineSegment(sketch, "E2726", {"start": v(-55.79, -54.74) * mm, "end": v(-55.44, -54.3) * mm});
            skLineSegment(sketch, "E2727", {"start": v(-55.44, -54.3) * mm, "end": v(-55.27, -54.1) * mm});
            skLineSegment(sketch, "E2728", {"start": v(-55.27, -54.1) * mm, "end": v(-55.01, -53.84) * mm});
            skLineSegment(sketch, "E2729", {"start": v(-55.01, -53.84) * mm, "end": v(-54.43, -53.25) * mm});
            skLineSegment(sketch, "E2730", {"start": v(-54.43, -53.25) * mm, "end": v(-53.86, -52.67) * mm});
            skLineSegment(sketch, "E2731", {"start": v(-53.86, -52.67) * mm, "end": v(-53.6, -52.4) * mm});
            skLineSegment(sketch, "E2732", {"start": v(-53.6, -52.4) * mm, "end": v(-53.37, -52.2) * mm});
            skLineSegment(sketch, "E2733", {"start": v(-53.37, -52.2) * mm, "end": v(-52.88, -51.73) * mm});
            skLineSegment(sketch, "E2734", {"start": v(-52.88, -51.73) * mm, "end": v(-52.39, -51.27) * mm});
            skLineSegment(sketch, "E2735", {"start": v(-52.39, -51.27) * mm, "end": v(-52.16, -51.06) * mm});
            skLineSegment(sketch, "E2736", {"start": v(-52.16, -51.06) * mm, "end": v(-51.9, -50.97) * mm});
            skLineSegment(sketch, "E2737", {"start": v(-51.9, -50.97) * mm, "end": v(-51.65, -50.88) * mm});
            skLineSegment(sketch, "E2738", {"start": v(-51.65, -50.88) * mm, "end": v(-51.45, -51.06) * mm});
            skLineSegment(sketch, "E2739", {"start": v(-51.45, -51.06) * mm, "end": v(-51.18, -51.02) * mm});
            skLineSegment(sketch, "E2740", {"start": v(-51.18, -51.02) * mm, "end": v(-50.78, -51.14) * mm});
            skLineSegment(sketch, "E2741", {"start": v(-50.78, -51.14) * mm, "end": v(-50.77, -51.52) * mm});
            skLineSegment(sketch, "E2742", {"start": v(-50.77, -51.52) * mm, "end": v(-50.97, -51.98) * mm});
            skLineSegment(sketch, "E2743", {"start": v(-50.97, -51.98) * mm, "end": v(-51.18, -52.32) * mm});
            skLineSegment(sketch, "E2744", {"start": v(-51.18, -52.32) * mm, "end": v(-51.82, -52.94) * mm});
            skLineSegment(sketch, "E2745", {"start": v(-51.82, -52.94) * mm, "end": v(-52.5, -53.5) * mm});
            skLineSegment(sketch, "E2746", {"start": v(-52.5, -53.5) * mm, "end": v(-52.57, -53.6) * mm});
            skLineSegment(sketch, "E2747", {"start": v(-52.57, -53.6) * mm, "end": v(-52.77, -53.84) * mm});
            skLineSegment(sketch, "E2748", {"start": v(-52.77, -53.84) * mm, "end": v(-53.06, -54.18) * mm});
            skLineSegment(sketch, "E2749", {"start": v(-53.06, -54.18) * mm, "end": v(-53.38, -54.57) * mm});
            skLineSegment(sketch, "E2750", {"start": v(-53.38, -54.57) * mm, "end": v(-53.7, -54.96) * mm});
            skLineSegment(sketch, "E2751", {"start": v(-53.7, -54.96) * mm, "end": v(-54, -55.3) * mm});
            skLineSegment(sketch, "E2752", {"start": v(-54, -55.3) * mm, "end": v(-54.2, -55.53) * mm});
            skLineSegment(sketch, "E2753", {"start": v(-54.2, -55.53) * mm, "end": v(-54.27, -55.62) * mm});
            skLineSegment(sketch, "E2754", {"start": v(-54.27, -55.62) * mm, "end": v(-54.36, -55.73) * mm});
            skLineSegment(sketch, "E2755", {"start": v(-54.36, -55.73) * mm, "end": v(-54.6, -56) * mm});
            skLineSegment(sketch, "E2756", {"start": v(-54.6, -56) * mm, "end": v(-54.94, -56.37) * mm});
            skLineSegment(sketch, "E2757", {"start": v(-54.94, -56.37) * mm, "end": v(-55.32, -56.81) * mm});
            skLineSegment(sketch, "E2758", {"start": v(-55.32, -56.81) * mm, "end": v(-55.71, -57.25) * mm});
            skLineSegment(sketch, "E2759", {"start": v(-55.71, -57.25) * mm, "end": v(-56.05, -57.63) * mm});
            skLineSegment(sketch, "E2760", {"start": v(-56.05, -57.63) * mm, "end": v(-56.29, -57.9) * mm});
            skLineSegment(sketch, "E2761", {"start": v(-56.29, -57.9) * mm, "end": v(-56.38, -58) * mm});
            skLineSegment(sketch, "E2762", {"start": v(-56.38, -58) * mm, "end": v(-59.28, -61.8) * mm});
            skLineSegment(sketch, "E2763", {"start": v(-59.28, -61.8) * mm, "end": v(-59.38, -61.99) * mm});
            skLineSegment(sketch, "E2764", {"start": v(-59.38, -61.99) * mm, "end": v(-59.66, -62.47) * mm});
            skLineSegment(sketch, "E2765", {"start": v(-59.66, -62.47) * mm, "end": v(-60.05, -63.15) * mm});
            skLineSegment(sketch, "E2766", {"start": v(-60.05, -63.15) * mm, "end": v(-60.5, -63.92) * mm});
            skLineSegment(sketch, "E2767", {"start": v(-60.5, -63.92) * mm, "end": v(-60.94, -64.7) * mm});
            skLineSegment(sketch, "E2768", {"start": v(-60.94, -64.7) * mm, "end": v(-61.32, -65.38) * mm});
            skLineSegment(sketch, "E2769", {"start": v(-61.32, -65.38) * mm, "end": v(-61.6, -65.86) * mm});
            skLineSegment(sketch, "E2770", {"start": v(-61.6, -65.86) * mm, "end": v(-61.7, -66.04) * mm});
            skLineSegment(sketch, "E2771", {"start": v(-61.7, -66.04) * mm, "end": v(-61.77, -66.19) * mm});
            skLineSegment(sketch, "E2772", {"start": v(-61.77, -66.19) * mm, "end": v(-61.96, -66.57) * mm});
            skLineSegment(sketch, "E2773", {"start": v(-61.96, -66.57) * mm, "end": v(-62.22, -67.11) * mm});
            skLineSegment(sketch, "E2774", {"start": v(-62.22, -67.11) * mm, "end": v(-62.52, -67.73) * mm});
            skLineSegment(sketch, "E2775", {"start": v(-62.52, -67.73) * mm, "end": v(-62.82, -68.35) * mm});
            skLineSegment(sketch, "E2776", {"start": v(-62.82, -68.35) * mm, "end": v(-63.08, -68.9) * mm});
            skLineSegment(sketch, "E2777", {"start": v(-63.08, -68.9) * mm, "end": v(-63.26, -69.28) * mm});
            skLineSegment(sketch, "E2778", {"start": v(-63.26, -69.28) * mm, "end": v(-63.33, -69.43) * mm});
            skLineSegment(sketch, "E2779", {"start": v(-63.33, -69.43) * mm, "end": v(-63.64, -69.52) * mm});
            skLineSegment(sketch, "E2780", {"start": v(-63.64, -69.52) * mm, "end": v(-63.86, -69.63) * mm});
            skLineSegment(sketch, "E2781", {"start": v(-63.86, -69.63) * mm, "end": v(-64.1, -69.7) * mm});
            skLineSegment(sketch, "E2782", {"start": v(-64.1, -69.7) * mm, "end": v(-64.44, -69.68) * mm});
            skLineSegment(sketch, "E2783", {"start": v(-64.44, -69.68) * mm, "end": v(-64.42, -70.18) * mm});
            skLineSegment(sketch, "E2784", {"start": v(-64.42, -70.18) * mm, "end": v(-64.44, -70.5) * mm});
            skLineSegment(sketch, "E2785", {"start": v(-64.44, -70.5) * mm, "end": v(-64.92, -70.87) * mm});
            skLineSegment(sketch, "E2786", {"start": v(-64.92, -70.87) * mm, "end": v(-65.53, -70.93) * mm});
            skLineSegment(sketch, "E2787", {"start": v(-65.53, -70.93) * mm, "end": v(-66.25, -70.78) * mm});
            skLineSegment(sketch, "E2788", {"start": v(-66.25, -70.78) * mm, "end": v(-66.8, -70.6) * mm});
            skLineSegment(sketch, "E2789", {"start": v(-66.8, -70.6) * mm, "end": v(-67.42, -70.43) * mm});
            skLineSegment(sketch, "E2790", {"start": v(-67.42, -70.43) * mm, "end": v(-68.41, -70.36) * mm});
            skLineSegment(sketch, "E2791", {"start": v(-68.41, -70.36) * mm, "end": v(-68.75, -70.34) * mm});
            skLineSegment(sketch, "E2792", {"start": v(-68.75, -70.34) * mm, "end": v(-69.19, -70.34) * mm});
            skLineSegment(sketch, "E2793", {"start": v(-69.19, -70.34) * mm, "end": v(-69.6, -70.37) * mm});
            skLineSegment(sketch, "E2794", {"start": v(-69.6, -70.37) * mm, "end": v(-69.89, -70.5) * mm});
            skLineSegment(sketch, "E2795", {"start": v(-69.89, -70.5) * mm, "end": v(-69.98, -70.89) * mm});
            skLineSegment(sketch, "E2796", {"start": v(-69.98, -70.89) * mm, "end": v(-69.8, -71.27) * mm});
            skLineSegment(sketch, "E2797", {"start": v(-69.8, -71.27) * mm, "end": v(-69.1, -71.98) * mm});
            skLineSegment(sketch, "E2798", {"start": v(-69.1, -71.98) * mm, "end": v(-68.24, -72.45) * mm});
            skLineSegment(sketch, "E2799", {"start": v(-68.24, -72.45) * mm, "end": v(-67.58, -72.69) * mm});
            skLineSegment(sketch, "E2800", {"start": v(-67.58, -72.69) * mm, "end": v(-67.06, -72.74) * mm});
            skLineSegment(sketch, "E2801", {"start": v(-67.06, -72.74) * mm, "end": v(-66.5, -72.74) * mm});
            skLineSegment(sketch, "E2802", {"start": v(-66.5, -72.74) * mm, "end": v(-65.79, -72.83) * mm});
            skLineSegment(sketch, "E2803", {"start": v(-65.79, -72.83) * mm, "end": v(-65.52, -72.9) * mm});
            skLineSegment(sketch, "E2804", {"start": v(-65.52, -72.9) * mm, "end": v(-64.94, -73.04) * mm});
            skLineSegment(sketch, "E2805", {"start": v(-64.94, -73.04) * mm, "end": v(-64.36, -73.18) * mm});
            skLineSegment(sketch, "E2806", {"start": v(-64.36, -73.18) * mm, "end": v(-64.1, -73.25) * mm});
            skLineSegment(sketch, "E2807", {"start": v(-64.1, -73.25) * mm, "end": v(-63.08, -73.74) * mm});
            skLineSegment(sketch, "E2808", {"start": v(-63.08, -73.74) * mm, "end": v(-62.92, -73.74) * mm});
            skLineSegment(sketch, "E2809", {"start": v(-62.92, -73.74) * mm, "end": v(-62.58, -73.74) * mm});
            skLineSegment(sketch, "E2810", {"start": v(-62.58, -73.74) * mm, "end": v(-62.24, -73.74) * mm});
            skLineSegment(sketch, "E2811", {"start": v(-62.24, -73.74) * mm, "end": v(-62.09, -73.74) * mm});
            skLineSegment(sketch, "E2812", {"start": v(-62.09, -73.74) * mm, "end": v(-61.94, -73.74) * mm});
            skLineSegment(sketch, "E2813", {"start": v(-61.94, -73.74) * mm, "end": v(-61.8, -73.74) * mm});
            skLineSegment(sketch, "E2814", {"start": v(-61.8, -73.74) * mm, "end": v(-61.4, -73.53) * mm});
            skLineSegment(sketch, "E2815", {"start": v(-61.4, -73.53) * mm, "end": v(-61.56, -73.19) * mm});
            skLineSegment(sketch, "E2816", {"start": v(-61.56, -73.19) * mm, "end": v(-61.97, -72.83) * mm});
            skLineSegment(sketch, "E2817", {"start": v(-61.97, -72.83) * mm, "end": v(-62.31, -72.6) * mm});
            skLineSegment(sketch, "E2818", {"start": v(-62.31, -72.6) * mm, "end": v(-62.6, -72.29) * mm});
            skLineSegment(sketch, "E2819", {"start": v(-62.6, -72.29) * mm, "end": v(-62.5, -71.97) * mm});
            skLineSegment(sketch, "E2820", {"start": v(-62.5, -71.97) * mm, "end": v(-62.23, -71.63) * mm});
            skLineSegment(sketch, "E2821", {"start": v(-62.23, -71.63) * mm, "end": v(-62.06, -71.63) * mm});
            skLineSegment(sketch, "E2822", {"start": v(-62.06, -71.63) * mm, "end": v(-61.9, -71.63) * mm});
            skLineSegment(sketch, "E2823", {"start": v(-61.9, -71.63) * mm, "end": v(-62, -70.95) * mm});
            skLineSegment(sketch, "E2824", {"start": v(-62, -70.95) * mm, "end": v(-61.87, -70.73) * mm});
            skLineSegment(sketch, "E2825", {"start": v(-61.87, -70.73) * mm, "end": v(-61.58, -70.23) * mm});
            skLineSegment(sketch, "E2826", {"start": v(-61.58, -70.23) * mm, "end": v(-61.29, -69.74) * mm});
            skLineSegment(sketch, "E2827", {"start": v(-61.29, -69.74) * mm, "end": v(-61.16, -69.51) * mm});
            skLineSegment(sketch, "E2828", {"start": v(-61.16, -69.51) * mm, "end": v(-60.85, -68.86) * mm});
            skLineSegment(sketch, "E2829", {"start": v(-60.85, -68.86) * mm, "end": v(-60.48, -68.24) * mm});
            skLineSegment(sketch, "E2830", {"start": v(-60.48, -68.24) * mm, "end": v(-59.96, -67.67) * mm});
            skLineSegment(sketch, "E2831", {"start": v(-59.96, -67.67) * mm, "end": v(-59.24, -67.03) * mm});
            skLineSegment(sketch, "E2832", {"start": v(-59.24, -67.03) * mm, "end": v(-58.48, -66.41) * mm});
            skLineSegment(sketch, "E2833", {"start": v(-58.48, -66.41) * mm, "end": v(-57.83, -65.92) * mm});
            skLineSegment(sketch, "E2834", {"start": v(-57.83, -65.92) * mm, "end": v(-57.7, -65.84) * mm});
            skLineSegment(sketch, "E2835", {"start": v(-57.7, -65.84) * mm, "end": v(-57.4, -65.62) * mm});
            skLineSegment(sketch, "E2836", {"start": v(-57.4, -65.62) * mm, "end": v(-56.95, -65.3) * mm});
            skLineSegment(sketch, "E2837", {"start": v(-56.95, -65.3) * mm, "end": v(-56.43, -64.95) * mm});
            skLineSegment(sketch, "E2838", {"start": v(-56.43, -64.95) * mm, "end": v(-55.92, -64.59) * mm});
            skLineSegment(sketch, "E2839", {"start": v(-55.92, -64.59) * mm, "end": v(-55.47, -64.27) * mm});
            skLineSegment(sketch, "E2840", {"start": v(-55.47, -64.27) * mm, "end": v(-55.16, -64.05) * mm});
            skLineSegment(sketch, "E2841", {"start": v(-55.16, -64.05) * mm, "end": v(-55.03, -63.97) * mm});
            skLineSegment(sketch, "E2842", {"start": v(-55.03, -63.97) * mm, "end": v(-54.92, -63.9) * mm});
            skLineSegment(sketch, "E2843", {"start": v(-54.92, -63.9) * mm, "end": v(-54.64, -63.74) * mm});
            skLineSegment(sketch, "E2844", {"start": v(-54.64, -63.74) * mm, "end": v(-54.23, -63.5) * mm});
            skLineSegment(sketch, "E2845", {"start": v(-54.23, -63.5) * mm, "end": v(-53.76, -63.24) * mm});
            skLineSegment(sketch, "E2846", {"start": v(-53.76, -63.24) * mm, "end": v(-53.3, -62.97) * mm});
            skLineSegment(sketch, "E2847", {"start": v(-53.3, -62.97) * mm, "end": v(-52.9, -62.73) * mm});
            skLineSegment(sketch, "E2848", {"start": v(-52.9, -62.73) * mm, "end": v(-52.6, -62.57) * mm});
            skLineSegment(sketch, "E2849", {"start": v(-52.6, -62.57) * mm, "end": v(-52.5, -62.5) * mm});
            skLineSegment(sketch, "E2850", {"start": v(-52.5, -62.5) * mm, "end": v(-52.32, -62.43) * mm});
            skLineSegment(sketch, "E2851", {"start": v(-52.32, -62.43) * mm, "end": v(-51.85, -62.23) * mm});
            skLineSegment(sketch, "E2852", {"start": v(-51.85, -62.23) * mm, "end": v(-51.18, -61.94) * mm});
            skLineSegment(sketch, "E2853", {"start": v(-51.18, -61.94) * mm, "end": v(-50.42, -61.61) * mm});
            skLineSegment(sketch, "E2854", {"start": v(-50.42, -61.61) * mm, "end": v(-49.66, -61.29) * mm});
            skLineSegment(sketch, "E2855", {"start": v(-49.66, -61.29) * mm, "end": v(-49, -61) * mm});
            skLineSegment(sketch, "E2856", {"start": v(-49, -61) * mm, "end": v(-48.52, -60.8) * mm});
            skLineSegment(sketch, "E2857", {"start": v(-48.52, -60.8) * mm, "end": v(-48.35, -60.72) * mm});
            skLineSegment(sketch, "E2858", {"start": v(-48.35, -60.72) * mm, "end": v(-48.22, -60.68) * mm});
            skLineSegment(sketch, "E2859", {"start": v(-48.22, -60.68) * mm, "end": v(-47.88, -60.56) * mm});
            skLineSegment(sketch, "E2860", {"start": v(-47.88, -60.56) * mm, "end": v(-47.4, -60.39) * mm});
            skLineSegment(sketch, "E2861", {"start": v(-47.4, -60.39) * mm, "end": v(-46.86, -60.2) * mm});
            skLineSegment(sketch, "E2862", {"start": v(-46.86, -60.2) * mm, "end": v(-46.32, -60) * mm});
            skLineSegment(sketch, "E2863", {"start": v(-46.32, -60) * mm, "end": v(-45.85, -59.83) * mm});
            skLineSegment(sketch, "E2864", {"start": v(-45.85, -59.83) * mm, "end": v(-45.51, -59.7) * mm});
            skLineSegment(sketch, "E2865", {"start": v(-45.51, -59.7) * mm, "end": v(-45.38, -59.66) * mm});
            skLineSegment(sketch, "E2866", {"start": v(-45.38, -59.66) * mm, "end": v(-44.22, -59.06) * mm});
            skLineSegment(sketch, "E2867", {"start": v(-44.22, -59.06) * mm, "end": v(-42.94, -58.3) * mm});
            skLineSegment(sketch, "E2868", {"start": v(-42.94, -58.3) * mm, "end": v(-41.68, -57.49) * mm});
            skLineSegment(sketch, "E2869", {"start": v(-41.68, -57.49) * mm, "end": v(-40.56, -56.76) * mm});
            skLineSegment(sketch, "E2870", {"start": v(-40.56, -56.76) * mm, "end": v(-39.14, -55.83) * mm});
            skLineSegment(sketch, "E2871", {"start": v(-39.14, -55.83) * mm, "end": v(-37.87, -54.93) * mm});
            skLineSegment(sketch, "E2872", {"start": v(-37.87, -54.93) * mm, "end": v(-36.74, -53.86) * mm});
            skLineSegment(sketch, "E2873", {"start": v(-36.74, -53.86) * mm, "end": v(-35.71, -52.5) * mm});
            skLineSegment(sketch, "E2874", {"start": v(-35.71, -52.5) * mm, "end": v(-35.17, -51.44) * mm});
            skLineSegment(sketch, "E2875", {"start": v(-35.17, -51.44) * mm, "end": v(-34.82, -50.3) * mm});
            skLineSegment(sketch, "E2876", {"start": v(-34.82, -50.3) * mm, "end": v(-34.8, -49.28) * mm});
            skLineSegment(sketch, "E2877", {"start": v(-34.8, -49.28) * mm, "end": v(-34.88, -48.26) * mm});
            skLineSegment(sketch, "E2878", {"start": v(-34.88, -48.26) * mm, "end": v(-34.88, -47.34) * mm});
            skLineSegment(sketch, "E2879", {"start": v(-34.88, -47.34) * mm, "end": v(-34.6, -46.48) * mm});
            skLineSegment(sketch, "E2880", {"start": v(-34.6, -46.48) * mm, "end": v(-33.97, -45.79) * mm});
            skLineSegment(sketch, "E2881", {"start": v(-33.97, -45.79) * mm, "end": v(-33.1, -45.5) * mm});
            skLineSegment(sketch, "E2882", {"start": v(-33.1, -45.5) * mm, "end": v(-32.44, -45.58) * mm});
            skLineSegment(sketch, "E2883", {"start": v(-32.44, -45.58) * mm, "end": v(-32.09, -45.94) * mm});
            skLineSegment(sketch, "E2884", {"start": v(-32.09, -45.94) * mm, "end": v(-31.84, -46.4) * mm});
            skLineSegment(sketch, "E2885", {"start": v(-31.84, -46.4) * mm, "end": v(-31.68, -46.36) * mm});
            skLineSegment(sketch, "E2886", {"start": v(-31.68, -46.36) * mm, "end": v(-31.33, -46.27) * mm});
            skLineSegment(sketch, "E2887", {"start": v(-31.33, -46.27) * mm, "end": v(-30.98, -46.18) * mm});
            skLineSegment(sketch, "E2888", {"start": v(-30.98, -46.18) * mm, "end": v(-30.82, -46.14) * mm});
            skLineSegment(sketch, "E2889", {"start": v(-30.82, -46.14) * mm, "end": v(-31.2, -46.14) * mm});
            skLineSegment(sketch, "E2890", {"start": v(-31.2, -46.14) * mm, "end": v(-31.58, -46.14) * mm});
            skLineSegment(sketch, "E2891", {"start": v(-31.58, -46.14) * mm, "end": v(-30.9, -45.92) * mm});
            skLineSegment(sketch, "E2892", {"start": v(-30.9, -45.92) * mm, "end": v(-30.23, -45.86) * mm});
            skLineSegment(sketch, "E2893", {"start": v(-30.23, -45.86) * mm, "end": v(-29.89, -45.77) * mm});
            skLineSegment(sketch, "E2894", {"start": v(-29.89, -45.77) * mm, "end": v(-29.55, -45.69) * mm});
            skLineSegment(sketch, "E2895", {"start": v(-29.55, -45.69) * mm, "end": v(-28.35, -45.7) * mm});
            skLineSegment(sketch, "E2896", {"start": v(-28.35, -45.7) * mm, "end": v(-27.18, -45.97) * mm});
            skLineSegment(sketch, "E2897", {"start": v(-27.18, -45.97) * mm, "end": v(-27.14, -46.18) * mm});
            skLineSegment(sketch, "E2898", {"start": v(-27.14, -46.18) * mm, "end": v(-27.1, -46.4) * mm});
            skLineSegment(sketch, "E2899", {"start": v(-27.1, -46.4) * mm, "end": v(-27.19, -46.9) * mm});
            skLineSegment(sketch, "E2900", {"start": v(-27.19, -46.9) * mm, "end": v(-27.79, -47.3) * mm});
            skLineSegment(sketch, "E2901", {"start": v(-27.79, -47.3) * mm, "end": v(-28.53, -47.42) * mm});
            skLineSegment(sketch, "E2902", {"start": v(-28.53, -47.42) * mm, "end": v(-28.77, -47.43) * mm});
            skLineSegment(sketch, "E2903", {"start": v(-28.77, -47.43) * mm, "end": v(-29.3, -47.46) * mm});
            skLineSegment(sketch, "E2904", {"start": v(-29.3, -47.46) * mm, "end": v(-29.82, -47.48) * mm});
            skLineSegment(sketch, "E2905", {"start": v(-29.82, -47.48) * mm, "end": v(-30.06, -47.5) * mm});
            skLineSegment(sketch, "E2906", {"start": v(-30.06, -47.5) * mm, "end": v(-30.3, -47.47) * mm});
            skLineSegment(sketch, "E2907", {"start": v(-30.3, -47.47) * mm, "end": v(-30.82, -47.41) * mm});
            skLineSegment(sketch, "E2908", {"start": v(-30.82, -47.41) * mm, "end": v(-31.34, -47.35) * mm});
            skLineSegment(sketch, "E2909", {"start": v(-31.34, -47.35) * mm, "end": v(-31.58, -47.33) * mm});
            skLineSegment(sketch, "E2910", {"start": v(-31.58, -47.33) * mm, "end": v(-31.58, -47.63) * mm});
            skLineSegment(sketch, "E2911", {"start": v(-31.58, -47.63) * mm, "end": v(-31.58, -48.3) * mm});
            skLineSegment(sketch, "E2912", {"start": v(-31.58, -48.3) * mm, "end": v(-31.58, -48.97) * mm});
            skLineSegment(sketch, "E2913", {"start": v(-31.58, -48.97) * mm, "end": v(-31.58, -49.27) * mm});
            skLineSegment(sketch, "E2914", {"start": v(-31.58, -49.27) * mm, "end": v(-31.66, -50.14) * mm});
            skLineSegment(sketch, "E2915", {"start": v(-31.66, -50.14) * mm, "end": v(-31.9, -50.97) * mm});
            skLineSegment(sketch, "E2916", {"start": v(-31.9, -50.97) * mm, "end": v(-32.47, -52.35) * mm});
            skLineSegment(sketch, "E2917", {"start": v(-32.47, -52.35) * mm, "end": v(-33.3, -53.6) * mm});
            skLineSegment(sketch, "E2918", {"start": v(-33.3, -53.6) * mm, "end": v(-33.78, -54.05) * mm});
            skLineSegment(sketch, "E2919", {"start": v(-33.78, -54.05) * mm, "end": v(-34.3, -54.49) * mm});
            skLineSegment(sketch, "E2920", {"start": v(-34.3, -54.49) * mm, "end": v(-34.5, -54.66) * mm});
            skLineSegment(sketch, "E2921", {"start": v(-34.5, -54.66) * mm, "end": v(-34.97, -55.04) * mm});
            skLineSegment(sketch, "E2922", {"start": v(-34.97, -55.04) * mm, "end": v(-35.43, -55.42) * mm});
            skLineSegment(sketch, "E2923", {"start": v(-35.43, -55.42) * mm, "end": v(-35.65, -55.59) * mm});
            skLineSegment(sketch, "E2924", {"start": v(-35.65, -55.59) * mm, "end": v(-35.78, -55.69) * mm});
            skLineSegment(sketch, "E2925", {"start": v(-35.78, -55.69) * mm, "end": v(-36.15, -55.95) * mm});
            skLineSegment(sketch, "E2926", {"start": v(-36.15, -55.95) * mm, "end": v(-36.66, -56.32) * mm});
            skLineSegment(sketch, "E2927", {"start": v(-36.66, -56.32) * mm, "end": v(-37.25, -56.75) * mm});
            skLineSegment(sketch, "E2928", {"start": v(-37.25, -56.75) * mm, "end": v(-37.85, -57.18) * mm});
            skLineSegment(sketch, "E2929", {"start": v(-37.85, -57.18) * mm, "end": v(-38.36, -57.55) * mm});
            skLineSegment(sketch, "E2930", {"start": v(-38.36, -57.55) * mm, "end": v(-38.72, -57.81) * mm});
            skLineSegment(sketch, "E2931", {"start": v(-38.72, -57.81) * mm, "end": v(-38.86, -57.91) * mm});
            skLineSegment(sketch, "E2932", {"start": v(-38.86, -57.91) * mm, "end": v(-38.7, -58) * mm});
            skLineSegment(sketch, "E2933", {"start": v(-38.7, -58) * mm, "end": v(-38.52, -58.08) * mm});
            skLineSegment(sketch, "E2934", {"start": v(-38.52, -58.08) * mm, "end": v(-38.48, -57.95) * mm});
            skLineSegment(sketch, "E2935", {"start": v(-38.48, -57.95) * mm, "end": v(-38.44, -57.83) * mm});
            skLineSegment(sketch, "E2936", {"start": v(-38.44, -57.83) * mm, "end": v(-37.88, -58.96) * mm});
            skLineSegment(sketch, "E2937", {"start": v(-37.88, -58.96) * mm, "end": v(-37.52, -59.94) * mm});
            skLineSegment(sketch, "E2938", {"start": v(-37.52, -59.94) * mm, "end": v(-37.22, -60.93) * mm});
            skLineSegment(sketch, "E2939", {"start": v(-37.22, -60.93) * mm, "end": v(-36.86, -62.06) * mm});
            skLineSegment(sketch, "E2940", {"start": v(-36.86, -62.06) * mm, "end": v(-36.73, -62.35) * mm});
            skLineSegment(sketch, "E2941", {"start": v(-36.73, -62.35) * mm, "end": v(-36.45, -63) * mm});
            skLineSegment(sketch, "E2942", {"start": v(-36.45, -63) * mm, "end": v(-36.17, -63.63) * mm});
            skLineSegment(sketch, "E2943", {"start": v(-36.17, -63.63) * mm, "end": v(-36.04, -63.92) * mm});
            skLineSegment(sketch, "E2944", {"start": v(-36.04, -63.92) * mm, "end": v(-35.92, -64.12) * mm});
            skLineSegment(sketch, "E2945", {"start": v(-35.92, -64.12) * mm, "end": v(-35.66, -64.56) * mm});
            skLineSegment(sketch, "E2946", {"start": v(-35.66, -64.56) * mm, "end": v(-35.4, -65) * mm});
            skLineSegment(sketch, "E2947", {"start": v(-35.4, -65) * mm, "end": v(-35.28, -65.2) * mm});
            skLineSegment(sketch, "E2948", {"start": v(-35.28, -65.2) * mm, "end": v(-34.84, -65.93) * mm});
            skLineSegment(sketch, "E2949", {"start": v(-34.84, -65.93) * mm, "end": v(-34.52, -66.72) * mm});
            skLineSegment(sketch, "E2950", {"start": v(-34.52, -66.72) * mm, "end": v(-34.43, -67.14) * mm});
            skLineSegment(sketch, "E2951", {"start": v(-34.43, -67.14) * mm, "end": v(-34.71, -67.4) * mm});
            skLineSegment(sketch, "E2952", {"start": v(-34.71, -67.4) * mm, "end": v(-34.71, -67.23) * mm});
            skLineSegment(sketch, "E2953", {"start": v(-34.71, -67.23) * mm, "end": v(-34.71, -67.06) * mm});
            skLineSegment(sketch, "E2954", {"start": v(-34.71, -67.06) * mm, "end": v(-35.02, -66.96) * mm});
            skLineSegment(sketch, "E2955", {"start": v(-35.02, -66.96) * mm, "end": v(-35.22, -66.72) * mm});
            skLineSegment(sketch, "E2956", {"start": v(-35.22, -66.72) * mm, "end": v(-35.35, -66.76) * mm});
            skLineSegment(sketch, "E2957", {"start": v(-35.35, -66.76) * mm, "end": v(-35.48, -66.8) * mm});
            skLineSegment(sketch, "E2958", {"start": v(-35.48, -66.8) * mm, "end": v(-35.52, -66.67) * mm});
            skLineSegment(sketch, "E2959", {"start": v(-35.52, -66.67) * mm, "end": v(-35.56, -66.55) * mm});
            skLineSegment(sketch, "E2960", {"start": v(-35.56, -66.55) * mm, "end": v(-35.73, -66.63) * mm});
            skLineSegment(sketch, "E2961", {"start": v(-35.73, -66.63) * mm, "end": v(-35.9, -66.72) * mm});
            skLineSegment(sketch, "E2962", {"start": v(-35.9, -66.72) * mm, "end": v(-36.23, -65.9) * mm});
            skLineSegment(sketch, "E2963", {"start": v(-36.23, -65.9) * mm, "end": v(-36.64, -65.1) * mm});
            skLineSegment(sketch, "E2964", {"start": v(-36.64, -65.1) * mm, "end": v(-36.7, -64.97) * mm});
            skLineSegment(sketch, "E2965", {"start": v(-36.7, -64.97) * mm, "end": v(-36.83, -64.68) * mm});
            skLineSegment(sketch, "E2966", {"start": v(-36.83, -64.68) * mm, "end": v(-36.97, -64.4) * mm});
            skLineSegment(sketch, "E2967", {"start": v(-36.97, -64.4) * mm, "end": v(-37.03, -64.26) * mm});
            skLineSegment(sketch, "E2968", {"start": v(-37.03, -64.26) * mm, "end": v(-37.15, -64.05) * mm});
            skLineSegment(sketch, "E2969", {"start": v(-37.15, -64.05) * mm, "end": v(-37.42, -63.58) * mm});
            skLineSegment(sketch, "E2970", {"start": v(-37.42, -63.58) * mm, "end": v(-37.68, -63.12) * mm});
            skLineSegment(sketch, "E2971", {"start": v(-37.68, -63.12) * mm, "end": v(-37.8, -62.9) * mm});
            skLineSegment(sketch, "E2972", {"start": v(-37.8, -62.9) * mm, "end": v(-37.86, -62.8) * mm});
            skLineSegment(sketch, "E2973", {"start": v(-37.86, -62.8) * mm, "end": v(-37.97, -62.57) * mm});
            skLineSegment(sketch, "E2974", {"start": v(-37.97, -62.57) * mm, "end": v(-38.08, -62.33) * mm});
            skLineSegment(sketch, "E2975", {"start": v(-38.08, -62.33) * mm, "end": v(-38.13, -62.23) * mm});
            skLineSegment(sketch, "E2976", {"start": v(-38.13, -62.23) * mm, "end": v(-38.23, -62.07) * mm});
            skLineSegment(sketch, "E2977", {"start": v(-38.23, -62.07) * mm, "end": v(-38.44, -61.72) * mm});
            skLineSegment(sketch, "E2978", {"start": v(-38.44, -61.72) * mm, "end": v(-38.65, -61.37) * mm});
            skLineSegment(sketch, "E2979", {"start": v(-38.65, -61.37) * mm, "end": v(-38.74, -61.21) * mm});
            skLineSegment(sketch, "E2980", {"start": v(-38.74, -61.21) * mm, "end": v(-38.94, -60.62) * mm});
            skLineSegment(sketch, "E2981", {"start": v(-38.94, -60.62) * mm, "end": v(-39.14, -59.76) * mm});
            skLineSegment(sketch, "E2982", {"start": v(-39.14, -59.76) * mm, "end": v(-39.3, -58.89) * mm});
            skLineSegment(sketch, "E2983", {"start": v(-39.3, -58.89) * mm, "end": v(-39.37, -58.25) * mm});
            skLineSegment(sketch, "E2984", {"start": v(-39.37, -58.25) * mm, "end": v(-39.68, -58.45) * mm});
            skLineSegment(sketch, "E2985", {"start": v(-39.68, -58.45) * mm, "end": v(-40.35, -58.88) * mm});
            skLineSegment(sketch, "E2986", {"start": v(-40.35, -58.88) * mm, "end": v(-41.02, -59.32) * mm});
            skLineSegment(sketch, "E2987", {"start": v(-41.02, -59.32) * mm, "end": v(-41.32, -59.52) * mm});
            skLineSegment(sketch, "E2988", {"start": v(-41.32, -59.52) * mm, "end": v(-42.5, -60.19) * mm});
            skLineSegment(sketch, "E2989", {"start": v(-42.5, -60.19) * mm, "end": v(-43.5, -60.67) * mm});
            skLineSegment(sketch, "E2990", {"start": v(-43.5, -60.67) * mm, "end": v(-44.53, -61.07) * mm});
            skLineSegment(sketch, "E2991", {"start": v(-44.53, -61.07) * mm, "end": v(-45.8, -61.5) * mm});
            skLineSegment(sketch, "E2992", {"start": v(-45.8, -61.5) * mm, "end": v(-46, -61.56) * mm});
            skLineSegment(sketch, "E2993", {"start": v(-46, -61.56) * mm, "end": v(-46.44, -61.7) * mm});
            skLineSegment(sketch, "E2994", {"start": v(-46.44, -61.7) * mm, "end": v(-46.88, -61.83) * mm});
            skLineSegment(sketch, "E2995", {"start": v(-46.88, -61.83) * mm, "end": v(-47.08, -61.9) * mm});
            skLineSegment(sketch, "E2996", {"start": v(-47.08, -61.9) * mm, "end": v(-47.08, -62.06) * mm});
            skLineSegment(sketch, "E2997", {"start": v(-47.08, -62.06) * mm, "end": v(-46.82, -62.18) * mm});
            skLineSegment(sketch, "E2998", {"start": v(-46.82, -62.18) * mm, "end": v(-46.27, -62.46) * mm});
            skLineSegment(sketch, "E2999", {"start": v(-46.27, -62.46) * mm, "end": v(-45.72, -62.73) * mm});
            skLineSegment(sketch, "E3000", {"start": v(-45.72, -62.73) * mm, "end": v(-45.47, -62.86) * mm});
            skLineSegment(sketch, "E3001", {"start": v(-45.47, -62.86) * mm, "end": v(-45.23, -63) * mm});
            skLineSegment(sketch, "E3002", {"start": v(-45.23, -63) * mm, "end": v(-44.7, -63.3) * mm});
            skLineSegment(sketch, "E3003", {"start": v(-44.7, -63.3) * mm, "end": v(-44.18, -63.62) * mm});
            skLineSegment(sketch, "E3004", {"start": v(-44.18, -63.62) * mm, "end": v(-43.94, -63.76) * mm});
            skLineSegment(sketch, "E3005", {"start": v(-43.94, -63.76) * mm, "end": v(-43.15, -64.15) * mm});
            skLineSegment(sketch, "E3006", {"start": v(-43.15, -64.15) * mm, "end": v(-42.1, -64.68) * mm});
            skLineSegment(sketch, "E3007", {"start": v(-42.1, -64.68) * mm, "end": v(-41.1, -65.23) * mm});
            skLineSegment(sketch, "E3008", {"start": v(-41.1, -65.23) * mm, "end": v(-40.4, -65.68) * mm});
            skLineSegment(sketch, "E3009", {"start": v(-40.4, -65.68) * mm, "end": v(-39.84, -66.44) * mm});
            skLineSegment(sketch, "E3010", {"start": v(-39.84, -66.44) * mm, "end": v(-39.43, -67.3) * mm});
            skLineSegment(sketch, "E3011", {"start": v(-39.43, -67.3) * mm, "end": v(-39.33, -67.67) * mm});
            skLineSegment(sketch, "E3012", {"start": v(-39.33, -67.67) * mm, "end": v(-39.39, -68.02) * mm});
            skLineSegment(sketch, "E3013", {"start": v(-39.39, -68.02) * mm, "end": v(-39.86, -68.18) * mm});
            skLineSegment(sketch, "E3014", {"start": v(-39.86, -68.18) * mm, "end": v(-40.39, -68.16) * mm});
            skLineSegment(sketch, "E3015", {"start": v(-40.39, -68.16) * mm, "end": v(-40.45, -67.77) * mm});
            skLineSegment(sketch, "E3016", {"start": v(-40.45, -67.77) * mm, "end": v(-40.79, -67.52) * mm});
            skLineSegment(sketch, "E3017", {"start": v(-40.79, -67.52) * mm, "end": v(-41.36, -67.25) * mm});
            skLineSegment(sketch, "E3018", {"start": v(-41.36, -67.25) * mm, "end": v(-41.97, -67) * mm});
            skLineSegment(sketch, "E3019", {"start": v(-41.97, -67) * mm, "end": v(-42.42, -66.84) * mm});
            skLineSegment(sketch, "E3020", {"start": v(-42.42, -66.84) * mm, "end": v(-42.65, -66.73) * mm});
            skLineSegment(sketch, "E3021", {"start": v(-42.65, -66.73) * mm, "end": v(-43.14, -66.5) * mm});
            skLineSegment(sketch, "E3022", {"start": v(-43.14, -66.5) * mm, "end": v(-43.63, -66.26) * mm});
            skLineSegment(sketch, "E3023", {"start": v(-43.63, -66.26) * mm, "end": v(-43.86, -66.15) * mm});
            skLineSegment(sketch, "E3024", {"start": v(-43.86, -66.15) * mm, "end": v(-44.77, -65.75) * mm});
            skLineSegment(sketch, "E3025", {"start": v(-44.77, -65.75) * mm, "end": v(-45.48, -65.44) * mm});
            skLineSegment(sketch, "E3026", {"start": v(-45.48, -65.44) * mm, "end": v(-46.18, -65.04) * mm});
            skLineSegment(sketch, "E3027", {"start": v(-46.18, -65.04) * mm, "end": v(-47.08, -64.39) * mm});
            skLineSegment(sketch, "E3028", {"start": v(-47.08, -64.39) * mm, "end": v(-47.48, -64.02) * mm});
            skLineSegment(sketch, "E3029", {"start": v(-47.48, -64.02) * mm, "end": v(-47.86, -63.54) * mm});
            skLineSegment(sketch, "E3030", {"start": v(-47.86, -63.54) * mm, "end": v(-48.13, -63.01) * mm});
            skLineSegment(sketch, "E3031", {"start": v(-48.13, -63.01) * mm, "end": v(-48.18, -62.48) * mm});
            skLineSegment(sketch, "E3032", {"start": v(-48.18, -62.48) * mm, "end": v(-49.87, -63.06) * mm});
            skLineSegment(sketch, "E3033", {"start": v(-49.87, -63.06) * mm, "end": v(-50.87, -63.45) * mm});
            skLineSegment(sketch, "E3034", {"start": v(-50.87, -63.45) * mm, "end": v(-51.42, -63.68) * mm});
            skLineSegment(sketch, "E3035", {"start": v(-51.42, -63.68) * mm, "end": v(-51.96, -63.96) * mm});
            skLineSegment(sketch, "E3036", {"start": v(-51.96, -63.96) * mm, "end": v(-52.92, -64.5) * mm});
            skLineSegment(sketch, "E3037", {"start": v(-52.92, -64.5) * mm, "end": v(-53.26, -64.68) * mm});
            skLineSegment(sketch, "E3038", {"start": v(-53.26, -64.68) * mm, "end": v(-54.02, -65.1) * mm});
            skLineSegment(sketch, "E3039", {"start": v(-54.02, -65.1) * mm, "end": v(-54.78, -65.52) * mm});
            skLineSegment(sketch, "E3040", {"start": v(-54.78, -65.52) * mm, "end": v(-55.12, -65.7) * mm});
            skLineSegment(sketch, "E3041", {"start": v(-55.12, -65.7) * mm, "end": v(-55.38, -65.9) * mm});
            skLineSegment(sketch, "E3042", {"start": v(-55.38, -65.9) * mm, "end": v(-55.97, -66.3) * mm});
            skLineSegment(sketch, "E3043", {"start": v(-55.97, -66.3) * mm, "end": v(-56.55, -66.72) * mm});
            skLineSegment(sketch, "E3044", {"start": v(-56.55, -66.72) * mm, "end": v(-56.81, -66.9) * mm});
            skLineSegment(sketch, "E3045", {"start": v(-56.81, -66.9) * mm, "end": v(-57.64, -67.47) * mm});
            skLineSegment(sketch, "E3046", {"start": v(-57.64, -67.47) * mm, "end": v(-58.42, -68.08) * mm});
            skLineSegment(sketch, "E3047", {"start": v(-58.42, -68.08) * mm, "end": v(-58.7, -68.35) * mm});
            skLineSegment(sketch, "E3048", {"start": v(-58.7, -68.35) * mm, "end": v(-59.28, -68.96) * mm});
            skLineSegment(sketch, "E3049", {"start": v(-59.28, -68.96) * mm, "end": v(-59.87, -69.57) * mm});
            skLineSegment(sketch, "E3050", {"start": v(-59.87, -69.57) * mm, "end": v(-60.14, -69.85) * mm});
            skLineSegment(sketch, "E3051", {"start": v(-60.14, -69.85) * mm, "end": v(-60.5, -70.24) * mm});
            skLineSegment(sketch, "E3052", {"start": v(-60.5, -70.24) * mm, "end": v(-60.7, -70.7) * mm});
            skLineSegment(sketch, "E3053", {"start": v(-60.7, -70.7) * mm, "end": v(-60.2, -70.8) * mm});
            skLineSegment(sketch, "E3054", {"start": v(-60.2, -70.8) * mm, "end": v(-59.89, -71.29) * mm});
            skLineSegment(sketch, "E3055", {"start": v(-59.89, -71.29) * mm, "end": v(-59.47, -72.36) * mm});
            skLineSegment(sketch, "E3056", {"start": v(-59.47, -72.36) * mm, "end": v(-59.56, -73.5) * mm});
            skLineSegment(sketch, "E3057", {"start": v(-59.56, -73.5) * mm, "end": v(-60.34, -74.35) * mm});
            skLineSegment(sketch, "E3058", {"start": v(-60.34, -74.35) * mm, "end": v(-61.47, -74.65) * mm});
            skLineSegment(sketch, "E3059", {"start": v(-61.47, -74.65) * mm, "end": v(-61.85, -74.65) * mm});
            skLineSegment(sketch, "E3060", {"start": v(-61.85, -74.65) * mm, "end": v(-62.23, -74.65) * mm});
            skLineSegment(sketch, "E3061", {"start": v(-62.23, -74.65) * mm, "end": v(-62.5, -74.69) * mm});
            skLineSegment(sketch, "E3062", {"start": v(-62.5, -74.69) * mm, "end": v(-62.71, -74.75) * mm});
            skLineSegment(sketch, "E3063", {"start": v(-62.71, -74.75) * mm, "end": v(-63.01, -74.83) * mm});
            skLineSegment(sketch, "E3064", {"start": v(-63.01, -74.83) * mm, "end": v(-63.5, -74.88) * mm});
            skLineSegment(sketch, "E3065", {"start": v(-63.5, -74.88) * mm, "end": v(-63.78, -74.88) * mm});
            skLineSegment(sketch, "E3066", {"start": v(-63.78, -74.88) * mm, "end": v(-64.39, -74.88) * mm});
            skLineSegment(sketch, "E3067", {"start": v(-64.39, -74.88) * mm, "end": v(-65, -74.88) * mm});
            skLineSegment(sketch, "E3068", {"start": v(-65, -74.88) * mm, "end": v(-65.28, -74.88) * mm});
            skLineSegment(sketch, "E3069", {"start": v(-65.28, -74.88) * mm, "end": v(-65.66, -74.88) * mm});
            skLineSegment(sketch, "E3070", {"start": v(-65.66, -74.88) * mm, "end": v(-66.04, -74.88) * mm});
            skLineSegment(sketch, "E3071", {"start": v(-66.04, -74.88) * mm, "end": v(-66.3, -74.88) * mm});
            skLineSegment(sketch, "E3072", {"start": v(-66.3, -74.88) * mm, "end": v(-66.55, -74.88) * mm});
            skLineSegment(sketch, "E3073", {"start": v(-66.55, -74.88) * mm, "end": v(-66.83, -74.9) * mm});
            skLineSegment(sketch, "E3074", {"start": v(-66.83, -74.9) * mm, "end": v(-67.14, -74.88) * mm});
            skLineSegment(sketch, "E3075", {"start": v(-67.14, -74.88) * mm, "end": v(-69.17, -74.72) * mm});
            skLineSegment(sketch, "E3076", {"start": v(-69.17, -74.72) * mm, "end": v(-69.81, -74.5) * mm});
            skLineSegment(sketch, "E3077", {"start": v(-69.81, -74.5) * mm, "end": v(-70.57, -74.17) * mm});
            skLineSegment(sketch, "E3078", {"start": v(-70.57, -74.17) * mm, "end": v(-71.31, -73.78) * mm});
            skLineSegment(sketch, "E3079", {"start": v(-71.31, -73.78) * mm, "end": v(-71.88, -73.42) * mm});
            skLineSegment(sketch, "E3080", {"start": v(-71.88, -73.42) * mm, "end": v(-72.35, -73.02) * mm});
            skLineSegment(sketch, "E3081", {"start": v(-72.35, -73.02) * mm, "end": v(-72.75, -72.56) * mm});
            skLineSegment(sketch, "E3082", {"start": v(-72.75, -72.56) * mm, "end": v(-72.83, -72.46) * mm});
            skLineSegment(sketch, "E3083", {"start": v(-72.83, -72.46) * mm, "end": v(-73.01, -72.26) * mm});
            skLineSegment(sketch, "E3084", {"start": v(-73.01, -72.26) * mm, "end": v(-73.19, -72.06) * mm});
            skLineSegment(sketch, "E3085", {"start": v(-73.19, -72.06) * mm, "end": v(-73.27, -71.97) * mm});
            skLineSegment(sketch, "E3086", {"start": v(-73.27, -71.97) * mm, "end": v(-73.67, -71.1) * mm});
            skLineSegment(sketch, "E3087", {"start": v(-73.67, -71.1) * mm, "end": v(-73.9, -70.19) * mm});
            skLineSegment(sketch, "E3088", {"start": v(-73.9, -70.19) * mm, "end": v(-73.86, -69.56) * mm});
            skLineSegment(sketch, "E3089", {"start": v(-73.86, -69.56) * mm, "end": v(-73.63, -69) * mm});
            skLineSegment(sketch, "E3090", {"start": v(-73.63, -69) * mm, "end": v(-72.8, -68.72) * mm});
            skLineSegment(sketch, "E3091", {"start": v(-72.8, -68.72) * mm, "end": v(-71.88, -68.66) * mm});
            skLineSegment(sketch, "E3092", {"start": v(-71.88, -68.66) * mm, "end": v(-69.8, -68.68) * mm});
            skLineSegment(sketch, "E3093", {"start": v(-69.8, -68.68) * mm, "end": v(-67.73, -68.87) * mm});
            skLineSegment(sketch, "E3094", {"start": v(-67.73, -68.87) * mm, "end": v(-67.5, -68.92) * mm});
            skLineSegment(sketch, "E3095", {"start": v(-67.5, -68.92) * mm, "end": v(-67.01, -69.03) * mm});
            skLineSegment(sketch, "E3096", {"start": v(-67.01, -69.03) * mm, "end": v(-66.52, -69.14) * mm});
            skLineSegment(sketch, "E3097", {"start": v(-66.52, -69.14) * mm, "end": v(-66.3, -69.19) * mm});
            skLineSegment(sketch, "E3098", {"start": v(-66.3, -69.19) * mm, "end": v(-66.14, -69.21) * mm});
            skLineSegment(sketch, "E3099", {"start": v(-66.14, -69.21) * mm, "end": v(-65.79, -69.26) * mm});
            skLineSegment(sketch, "E3100", {"start": v(-65.79, -69.26) * mm, "end": v(-65.44, -69.32) * mm});
            skLineSegment(sketch, "E3101", {"start": v(-65.44, -69.32) * mm, "end": v(-65.28, -69.34) * mm});
            skLineSegment(sketch, "E3102", {"start": v(-65.28, -69.34) * mm, "end": v(-64.4, -67.25) * mm});
            skLineSegment(sketch, "E3103", {"start": v(-64.4, -67.25) * mm, "end": v(-63.35, -64.97) * mm});
            skLineSegment(sketch, "E3104", {"start": v(-63.35, -64.97) * mm, "end": v(-62.18, -62.76) * mm});
            skLineSegment(sketch, "E3105", {"start": v(-62.18, -62.76) * mm, "end": v(-60.97, -60.88) * mm});
            skLineSegment(sketch, "E3106", {"start": v(-60.97, -60.88) * mm, "end": v(-58.32, -57.66) * mm});
            skLineSegment(sketch, "E3107", {"start": v(-58.32, -57.66) * mm, "end": v(-57.35, -56.64) * mm});
            skLineSegment(sketch, "E3108", {"start": v(-57.35, -56.64) * mm, "end": v(-56.47, -55.54) * mm});
            skLineSegment(sketch, "E3109", {"start": v(-56.47, -55.54) * mm, "end": v(-56.96, -55.48) * mm});
            skLineSegment(sketch, "E3110", {"start": v(-56.96, -55.48) * mm, "end": v(-57.3, -55.03) * mm});
            skLineSegment(sketch, "E3111", {"start": v(-57.3, -55.03) * mm, "end": v(-57.48, -54.8) * mm});
            skLineSegment(sketch, "E3112", {"start": v(-57.48, -54.8) * mm, "end": v(-57.9, -54.27) * mm});
            skLineSegment(sketch, "E3113", {"start": v(-57.9, -54.27) * mm, "end": v(-58.3, -53.75) * mm});
            skLineSegment(sketch, "E3114", {"start": v(-58.3, -53.75) * mm, "end": v(-58.5, -53.5) * mm});
            skLineSegment(sketch, "E3115", {"start": v(-58.5, -53.5) * mm, "end": v(-60.11, -50.7) * mm});
            skLineSegment(sketch, "E3116", {"start": v(-60.11, -50.7) * mm, "end": v(-60.98, -47.58) * mm});
            skLineSegment(sketch, "E3117", {"start": v(-60.98, -47.58) * mm, "end": v(-61.02, -47.16) * mm});
            skLineSegment(sketch, "E3118", {"start": v(-61.02, -47.16) * mm, "end": v(-61.06, -46.74) * mm});
            skLineSegment(sketch, "E3119", {"start": v(-61.06, -46.74) * mm, "end": v(-61.14, -45.84) * mm});
            skLineSegment(sketch, "E3120", {"start": v(-61.14, -45.84) * mm, "end": v(-60.8, -45.04) * mm});
            skLineSegment(sketch, "E3121", {"start": v(-60.8, -45.04) * mm, "end": v(-60.75, -45.17) * mm});
            skLineSegment(sketch, "E3122", {"start": v(-60.75, -45.17) * mm, "end": v(-60.7, -45.3) * mm});
            skLineSegment(sketch, "E3123", {"start": v(-60.7, -45.3) * mm, "end": v(-60.58, -45.25) * mm});
            skLineSegment(sketch, "E3124", {"start": v(-60.58, -45.25) * mm, "end": v(-60.45, -45.21) * mm});
            skLineSegment(sketch, "E3125", {"start": v(-60.45, -45.21) * mm, "end": v(-60.33, -45.34) * mm});
            skLineSegment(sketch, "E3126", {"start": v(-60.33, -45.34) * mm, "end": v(-60.2, -45.47) * mm});
            skLineSegment(sketch, "E3127", {"start": v(-60.2, -45.47) * mm, "end": v(-60.24, -45.25) * mm});
            skLineSegment(sketch, "E3128", {"start": v(-60.24, -45.25) * mm, "end": v(-60.28, -45.04) * mm});
            skLineSegment(sketch, "E3129", {"start": v(-60.28, -45.04) * mm, "end": v(-60.2, -45) * mm});
            skLineSegment(sketch, "E3130", {"start": v(-60.2, -45) * mm, "end": v(-60.11, -44.96) * mm});
            skLineSegment(sketch, "E3131", {"start": v(-60.11, -44.96) * mm, "end": v(-59.67, -45.63) * mm});
            skLineSegment(sketch, "E3132", {"start": v(-59.67, -45.63) * mm, "end": v(-59.6, -46.48) * mm});
            skLineSegment(sketch, "E3133", {"start": v(-47.75, -62.23) * mm, "end": v(-47.67, -62.31) * mm});
            skLineSegment(sketch, "E3134", {"start": v(-47.67, -62.31) * mm, "end": v(-47.67, -62.23) * mm});
            skLineSegment(sketch, "E3135", {"start": v(-47.67, -62.23) * mm, "end": v(-47.75, -62.23) * mm});
            skLineSegment(sketch, "E3136", {"start": v(-33.97, -69.51) * mm, "end": v(-34.6, -71.12) * mm});
            skLineSegment(sketch, "E3137", {"start": v(-34.6, -71.12) * mm, "end": v(-35.57, -72.56) * mm});
            skLineSegment(sketch, "E3138", {"start": v(-35.57, -72.56) * mm, "end": v(-35.74, -72.72) * mm});
            skLineSegment(sketch, "E3139", {"start": v(-35.74, -72.72) * mm, "end": v(-36.12, -73.07) * mm});
            skLineSegment(sketch, "E3140", {"start": v(-36.12, -73.07) * mm, "end": v(-36.5, -73.42) * mm});
            skLineSegment(sketch, "E3141", {"start": v(-36.5, -73.42) * mm, "end": v(-36.66, -73.58) * mm});
            skLineSegment(sketch, "E3142", {"start": v(-36.66, -73.58) * mm, "end": v(-37.18, -74.05) * mm});
            skLineSegment(sketch, "E3143", {"start": v(-37.18, -74.05) * mm, "end": v(-37.8, -74.56) * mm});
            skLineSegment(sketch, "E3144", {"start": v(-37.8, -74.56) * mm, "end": v(-38.45, -75.04) * mm});
            skLineSegment(sketch, "E3145", {"start": v(-38.45, -75.04) * mm, "end": v(-39.03, -75.41) * mm});
            skLineSegment(sketch, "E3146", {"start": v(-39.03, -75.41) * mm, "end": v(-39.64, -75.66) * mm});
            skLineSegment(sketch, "E3147", {"start": v(-39.64, -75.66) * mm, "end": v(-40.36, -75.86) * mm});
            skLineSegment(sketch, "E3148", {"start": v(-40.36, -75.86) * mm, "end": v(-41.1, -75.95) * mm});
            skLineSegment(sketch, "E3149", {"start": v(-41.1, -75.95) * mm, "end": v(-41.74, -75.9) * mm});
            skLineSegment(sketch, "E3150", {"start": v(-41.74, -75.9) * mm, "end": v(-42.2, -75.74) * mm});
            skLineSegment(sketch, "E3151", {"start": v(-42.2, -75.74) * mm, "end": v(-42.59, -75.48) * mm});
            skLineSegment(sketch, "E3152", {"start": v(-42.59, -75.48) * mm, "end": v(-42.76, -74.93) * mm});
            skLineSegment(sketch, "E3153", {"start": v(-42.76, -74.93) * mm, "end": v(-42.8, -75.06) * mm});
            skLineSegment(sketch, "E3154", {"start": v(-42.8, -75.06) * mm, "end": v(-42.84, -75.18) * mm});
            skLineSegment(sketch, "E3155", {"start": v(-42.84, -75.18) * mm, "end": v(-42.43, -72.52) * mm});
            skLineSegment(sketch, "E3156", {"start": v(-42.43, -72.52) * mm, "end": v(-41.22, -70.1) * mm});
            skLineSegment(sketch, "E3157", {"start": v(-41.22, -70.1) * mm, "end": v(-40.67, -69.3) * mm});
            skLineSegment(sketch, "E3158", {"start": v(-40.67, -69.3) * mm, "end": v(-40.05, -68.58) * mm});
            skLineSegment(sketch, "E3159", {"start": v(-40.05, -68.58) * mm, "end": v(-40.1, -68.75) * mm});
            skLineSegment(sketch, "E3160", {"start": v(-40.1, -68.75) * mm, "end": v(-40.13, -68.92) * mm});
            skLineSegment(sketch, "E3161", {"start": v(-40.13, -68.92) * mm, "end": v(-39.96, -68.7) * mm});
            skLineSegment(sketch, "E3162", {"start": v(-39.96, -68.7) * mm, "end": v(-39.8, -68.5) * mm});
            skLineSegment(sketch, "E3163", {"start": v(-39.8, -68.5) * mm, "end": v(-39.58, -68.45) * mm});
            skLineSegment(sketch, "E3164", {"start": v(-39.58, -68.45) * mm, "end": v(-39.37, -68.41) * mm});
            skLineSegment(sketch, "E3165", {"start": v(-39.37, -68.41) * mm, "end": v(-39.46, -68.75) * mm});
            skLineSegment(sketch, "E3166", {"start": v(-39.46, -68.75) * mm, "end": v(-39.54, -69.09) * mm});
            skLineSegment(sketch, "E3167", {"start": v(-39.54, -69.09) * mm, "end": v(-39.37, -69) * mm});
            skLineSegment(sketch, "E3168", {"start": v(-39.37, -69) * mm, "end": v(-39.2, -68.92) * mm});
            skLineSegment(sketch, "E3169", {"start": v(-39.2, -68.92) * mm, "end": v(-39.38, -69.33) * mm});
            skLineSegment(sketch, "E3170", {"start": v(-39.38, -69.33) * mm, "end": v(-39.37, -69.68) * mm});
            skLineSegment(sketch, "E3171", {"start": v(-39.37, -69.68) * mm, "end": v(-39.48, -69.92) * mm});
            skLineSegment(sketch, "E3172", {"start": v(-39.48, -69.92) * mm, "end": v(-39.71, -70.44) * mm});
            skLineSegment(sketch, "E3173", {"start": v(-39.71, -70.44) * mm, "end": v(-39.94, -70.97) * mm});
            skLineSegment(sketch, "E3174", {"start": v(-39.94, -70.97) * mm, "end": v(-40.05, -71.2) * mm});
            skLineSegment(sketch, "E3175", {"start": v(-40.05, -71.2) * mm, "end": v(-39.92, -71.03) * mm});
            skLineSegment(sketch, "E3176", {"start": v(-39.92, -71.03) * mm, "end": v(-39.8, -70.87) * mm});
            skLineSegment(sketch, "E3177", {"start": v(-39.8, -70.87) * mm, "end": v(-40.05, -71.33) * mm});
            skLineSegment(sketch, "E3178", {"start": v(-40.05, -71.33) * mm, "end": v(-40.35, -71.86) * mm});
            skLineSegment(sketch, "E3179", {"start": v(-40.35, -71.86) * mm, "end": v(-40.58, -72.4) * mm});
            skLineSegment(sketch, "E3180", {"start": v(-40.58, -72.4) * mm, "end": v(-40.65, -72.9) * mm});
            skLineSegment(sketch, "E3181", {"start": v(-40.65, -72.9) * mm, "end": v(-40.5, -73.21) * mm});
            skLineSegment(sketch, "E3182", {"start": v(-40.5, -73.21) * mm, "end": v(-40.22, -73.44) * mm});
            skLineSegment(sketch, "E3183", {"start": v(-40.22, -73.44) * mm, "end": v(-39.8, -73.66) * mm});
            skLineSegment(sketch, "E3184", {"start": v(-39.8, -73.66) * mm, "end": v(-39.31, -73.59) * mm});
            skLineSegment(sketch, "E3185", {"start": v(-39.31, -73.59) * mm, "end": v(-38.76, -73.31) * mm});
            skLineSegment(sketch, "E3186", {"start": v(-38.76, -73.31) * mm, "end": v(-38.24, -72.95) * mm});
            skLineSegment(sketch, "E3187", {"start": v(-38.24, -72.95) * mm, "end": v(-37.85, -72.63) * mm});
            skLineSegment(sketch, "E3188", {"start": v(-37.85, -72.63) * mm, "end": v(-37.65, -72.45) * mm});
            skLineSegment(sketch, "E3189", {"start": v(-37.65, -72.45) * mm, "end": v(-37.21, -72.06) * mm});
            skLineSegment(sketch, "E3190", {"start": v(-37.21, -72.06) * mm, "end": v(-36.78, -71.67) * mm});
            skLineSegment(sketch, "E3191", {"start": v(-36.78, -71.67) * mm, "end": v(-36.58, -71.5) * mm});
            skLineSegment(sketch, "E3192", {"start": v(-36.58, -71.5) * mm, "end": v(-35.84, -70.93) * mm});
            skLineSegment(sketch, "E3193", {"start": v(-35.84, -70.93) * mm, "end": v(-35.2, -70.27) * mm});
            skLineSegment(sketch, "E3194", {"start": v(-35.2, -70.27) * mm, "end": v(-34.85, -69.4) * mm});
            skLineSegment(sketch, "E3195", {"start": v(-34.85, -69.4) * mm, "end": v(-34.7, -68.68) * mm});
            skLineSegment(sketch, "E3196", {"start": v(-34.7, -68.68) * mm, "end": v(-34.51, -68.33) * mm});
            skLineSegment(sketch, "E3197", {"start": v(-34.51, -68.33) * mm, "end": v(-34.3, -67.99) * mm});
            skLineSegment(sketch, "E3198", {"start": v(-34.3, -67.99) * mm, "end": v(-34.21, -67.6) * mm});
            skLineSegment(sketch, "E3199", {"start": v(-34.21, -67.6) * mm, "end": v(-34.12, -67.23) * mm});
            skLineSegment(sketch, "E3200", {"start": v(-34.12, -67.23) * mm, "end": v(-34.04, -67.3) * mm});
            skLineSegment(sketch, "E3201", {"start": v(-34.04, -67.3) * mm, "end": v(-33.95, -67.4) * mm});
            skLineSegment(sketch, "E3202", {"start": v(-33.95, -67.4) * mm, "end": v(-33.91, -67.18) * mm});
            skLineSegment(sketch, "E3203", {"start": v(-33.91, -67.18) * mm, "end": v(-33.87, -66.97) * mm});
            skLineSegment(sketch, "E3204", {"start": v(-33.87, -66.97) * mm, "end": v(-33.7, -67.54) * mm});
            skLineSegment(sketch, "E3205", {"start": v(-33.7, -67.54) * mm, "end": v(-33.7, -68.22) * mm});
            skLineSegment(sketch, "E3206", {"start": v(-33.7, -68.22) * mm, "end": v(-33.82, -68.91) * mm});
            skLineSegment(sketch, "E3207", {"start": v(-33.82, -68.91) * mm, "end": v(-33.97, -69.51) * mm});
            skLineSegment(sketch, "E3208", {"start": v(-39.8, -68.66) * mm, "end": v(-39.71, -68.75) * mm});
            skLineSegment(sketch, "E3209", {"start": v(-39.71, -68.75) * mm, "end": v(-39.71, -68.66) * mm});
            skLineSegment(sketch, "E3210", {"start": v(-40.22, -68.92) * mm, "end": v(-40.13, -69) * mm});
            skLineSegment(sketch, "E3211", {"start": v(-40.13, -69) * mm, "end": v(-40.13, -68.92) * mm});
            skLineSegment(sketch, "E3212", {"start": v(-39.62, -69.77) * mm, "end": v(-39.54, -69.85) * mm});
            skLineSegment(sketch, "E3213", {"start": v(-39.54, -69.85) * mm, "end": v(-39.54, -69.77) * mm});
            skLineSegment(sketch, "E3214", {"start": v(-39.54, -69.77) * mm, "end": v(-39.62, -69.77) * mm});
            skLineSegment(sketch, "E3215", {"start": v(-61.98, -70.95) * mm, "end": v(-61.9, -71.03) * mm});
            skLineSegment(sketch, "E3216", {"start": v(-61.9, -71.03) * mm, "end": v(-61.9, -70.95) * mm});
            skLineSegment(sketch, "E3217", {"start": v(-61.9, -70.95) * mm, "end": v(-61.98, -70.95) * mm});
            skLineSegment(sketch, "E3218", {"start": v(-42.33, -75.44) * mm, "end": v(-42.38, -75.23) * mm});
            skLineSegment(sketch, "E3219", {"start": v(-42.38, -75.23) * mm, "end": v(-42.42, -75.01) * mm});
            skLineSegment(sketch, "E3220", {"start": v(-42.42, -75.01) * mm, "end": v(-42.47, -75.25) * mm});
            skLineSegment(sketch, "E3221", {"start": v(-42.47, -75.25) * mm, "end": v(-42.33, -75.44) * mm});
            skSolve(sketch);
        }
        {
            var Q0;
            Q0=makeQuery(id+"F0.imprint","IMPRINT",FACE,{"disambiguationData":[TD([[makeQuery(id+"F0.imprint","IMPRINT",EDGE,{"derivedFrom":sQuery(id+"F0.wireOp",EDGE,"E1566")}),-1.0]])]});
            var Q1;
            Q1=makeQuery(id+"F0.imprint","IMPRINT",FACE,{"disambiguationData":[TD([[makeQuery(id+"F0.imprint","IMPRINT",EDGE,{"derivedFrom":sQuery(id+"F0.wireOp",EDGE,"E1400")}),-1.0]])]});
            var Q2;
            Q2=makeQuery(id+"F0.imprint","IMPRINT",FACE,{"disambiguationData":[TD([[makeQuery(id+"F0.imprint","IMPRINT",EDGE,{"derivedFrom":sQuery(id+"F0.wireOp",EDGE,"E1719")}),-1.0]])]});
            var Q3;
            Q3=makeQuery(id+"F0.imprint","IMPRINT",FACE,{"disambiguationData":[TD([[makeQuery(id+"F0.imprint","IMPRINT",EDGE,{"derivedFrom":sQuery(id+"F0.wireOp",EDGE,"E1685")}),-1.0]])]});
            extrude(context, id + "F1", {"entities" : qUnion([Q0, Q1, Q2, Q3]), "depth" : 12.7 * mm});
        }
    });
